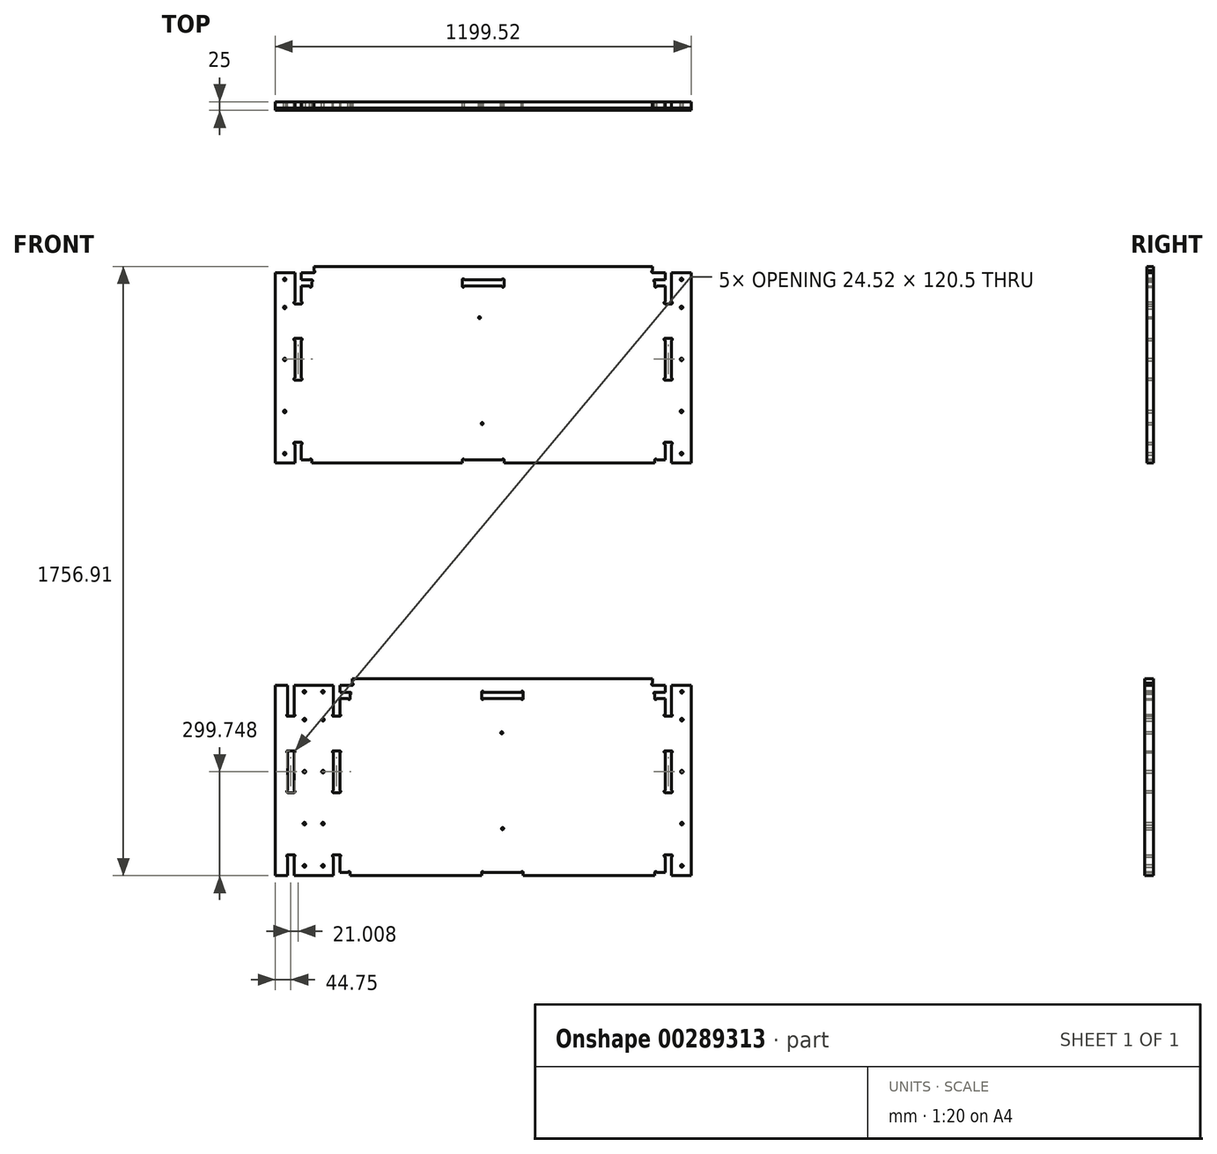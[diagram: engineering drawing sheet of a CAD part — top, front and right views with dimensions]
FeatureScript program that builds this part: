
annotation { "Feature Type Name" : "Feature", "Feature Type Description" : "" }
export const myFeature = defineFeature(function(context is Context, id is Id, definition is map)
    precondition{}
    {
        {
            var Q0;
            Q0=qCreatedBy(makeId("Front.planeOp"),FACE);
            var sketch = newSketch(context, id + "F0", { "sketchPlane" : qUnion([Q0])});
            skLineSegment(sketch, "E0", {"start": v(-600, -1200) * mm, "end": v(600, -1200) * mm});
            skLineSegment(sketch, "E1", {"start": v(600, 1200) * mm, "end": v(-600, 1200) * mm});
            skLineSegment(sketch, "E2", {"start": v(-600, -1149.94) * mm, "end": v(-564.5, -1149.94) * mm});
            skLineSegment(sketch, "E3", {"start": v(-564.5, -1149.94) * mm, "end": v(-564.5, -1066.44) * mm});
            skLineSegment(sketch, "E4", {"start": v(-564.5, -1066.44) * mm, "end": v(-564.5, -1066.21) * mm});
            skLineSegment(sketch, "E5", {"start": v(-564.5, -1066.21) * mm, "end": v(-564.73, -1066.2) * mm});
            skArc(sketch, "E6", {"start": v(-564.73, -1066.2) * mm, "mid": v(-567.52, -1063.07) * mm, "end": v(-564.5, -1060.17) * mm});
            skLineSegment(sketch, "E7", {"start": v(-564.5, -1060.17) * mm, "end": v(-546, -1060.17) * mm});
            skArc(sketch, "E8", {"start": v(-546, -1060.17) * mm, "mid": v(-543, -1063.07) * mm, "end": v(-545.77, -1066.2) * mm});
            skLineSegment(sketch, "E9", {"start": v(-545.77, -1066.2) * mm, "end": v(-546, -1066.21) * mm});
            skLineSegment(sketch, "E10", {"start": v(-546, -1066.21) * mm, "end": v(-546, -1066.44) * mm});
            skLineSegment(sketch, "E11", {"start": v(-546, -1066.44) * mm, "end": v(-546, -1149.94) * mm});
            skLineSegment(sketch, "E12", {"start": v(-546, -1149.94) * mm, "end": v(-432.5, -1149.94) * mm});
            skLineSegment(sketch, "E13", {"start": v(-432.5, -1149.94) * mm, "end": v(-432.5, -1066.44) * mm});
            skLineSegment(sketch, "E14", {"start": v(-432.5, -1066.44) * mm, "end": v(-432.5, -1066.21) * mm});
            skLineSegment(sketch, "E15", {"start": v(-432.5, -1066.21) * mm, "end": v(-432.73, -1066.2) * mm});
            skArc(sketch, "E16", {"start": v(-432.73, -1066.2) * mm, "mid": v(-435.52, -1063.07) * mm, "end": v(-432.5, -1060.17) * mm});
            skLineSegment(sketch, "E17", {"start": v(-432.5, -1060.17) * mm, "end": v(-414, -1060.17) * mm});
            skArc(sketch, "E18", {"start": v(-414, -1060.17) * mm, "mid": v(-411, -1063.07) * mm, "end": v(-413.77, -1066.2) * mm});
            skLineSegment(sketch, "E19", {"start": v(-413.77, -1066.2) * mm, "end": v(-414, -1066.21) * mm});
            skLineSegment(sketch, "E20", {"start": v(-414, -1066.21) * mm, "end": v(-414, -1066.44) * mm});
            skLineSegment(sketch, "E21", {"start": v(-414, -1066.44) * mm, "end": v(-414, -1111.17) * mm});
            skLineSegment(sketch, "E22", {"start": v(-414, -1111.17) * mm, "end": v(-390.27, -1111.17) * mm});
            skLineSegment(sketch, "E23", {"start": v(-390.27, -1111.17) * mm, "end": v(-390.04, -1111.17) * mm});
            skLineSegment(sketch, "E24", {"start": v(-390.04, -1111.17) * mm, "end": v(-390.02, -1110.94) * mm});
            skArc(sketch, "E25", {"start": v(-390.02, -1110.94) * mm, "mid": v(-386.9, -1108.16) * mm, "end": v(-384, -1111.17) * mm});
            skLineSegment(sketch, "E26", {"start": v(-384, -1111.17) * mm, "end": v(-384, -1123.4) * mm});
            skLineSegment(sketch, "E27", {"start": v(-384, -1123.4) * mm, "end": v(-384, -1123.64) * mm});
            skLineSegment(sketch, "E28", {"start": v(-384, -1123.64) * mm, "end": v(-383.77, -1123.65) * mm});
            skArc(sketch, "E29", {"start": v(-383.77, -1123.65) * mm, "mid": v(-380.98, -1126.77) * mm, "end": v(-384, -1129.67) * mm});
            skLineSegment(sketch, "E30", {"start": v(-384, -1129.67) * mm, "end": v(-414, -1129.67) * mm});
            skLineSegment(sketch, "E31", {"start": v(-414, -1129.67) * mm, "end": v(-414, -1149.94) * mm});
            skLineSegment(sketch, "E32", {"start": v(-414, -1149.94) * mm, "end": v(-378, -1149.94) * mm});
            skArc(sketch, "E33", {"start": v(-378, -1149.94) * mm, "mid": v(-375, -1152.84) * mm, "end": v(-377.77, -1155.96) * mm});
            skLineSegment(sketch, "E34", {"start": v(-377.77, -1155.96) * mm, "end": v(-378, -1155.98) * mm});
            skLineSegment(sketch, "E35", {"start": v(-378, -1155.98) * mm, "end": v(-378, -1156.2) * mm});
            skLineSegment(sketch, "E36", {"start": v(-378, -1156.2) * mm, "end": v(-378, -1167.94) * mm});
            skLineSegment(sketch, "E37", {"start": v(-378, -1167.94) * mm, "end": v(488.5, -1167.94) * mm});
            skLineSegment(sketch, "E38", {"start": v(488.5, -1167.94) * mm, "end": v(488.5, -1156.2) * mm});
            skLineSegment(sketch, "E39", {"start": v(488.5, -1156.2) * mm, "end": v(488.5, -1155.98) * mm});
            skLineSegment(sketch, "E40", {"start": v(488.5, -1155.98) * mm, "end": v(488.27, -1155.96) * mm});
            skArc(sketch, "E41", {"start": v(488.27, -1155.96) * mm, "mid": v(485.48, -1152.84) * mm, "end": v(488.5, -1149.94) * mm});
            skLineSegment(sketch, "E42", {"start": v(488.5, -1149.94) * mm, "end": v(524.5, -1149.94) * mm});
            skLineSegment(sketch, "E43", {"start": v(524.5, -1149.94) * mm, "end": v(524.5, -1129.67) * mm});
            skLineSegment(sketch, "E44", {"start": v(524.5, -1129.67) * mm, "end": v(494.5, -1129.67) * mm});
            skArc(sketch, "E45", {"start": v(494.5, -1129.67) * mm, "mid": v(491.5, -1126.77) * mm, "end": v(494.27, -1123.65) * mm});
            skLineSegment(sketch, "E46", {"start": v(494.27, -1123.65) * mm, "end": v(494.5, -1123.64) * mm});
            skLineSegment(sketch, "E47", {"start": v(494.5, -1123.64) * mm, "end": v(494.5, -1123.4) * mm});
            skLineSegment(sketch, "E48", {"start": v(494.5, -1123.4) * mm, "end": v(494.5, -1111.17) * mm});
            skArc(sketch, "E49", {"start": v(494.5, -1111.17) * mm, "mid": v(497.4, -1108.17) * mm, "end": v(500.52, -1110.94) * mm});
            skLineSegment(sketch, "E50", {"start": v(500.52, -1110.94) * mm, "end": v(500.54, -1111.17) * mm});
            skLineSegment(sketch, "E51", {"start": v(500.54, -1111.17) * mm, "end": v(500.77, -1111.17) * mm});
            skLineSegment(sketch, "E52", {"start": v(500.77, -1111.17) * mm, "end": v(524.5, -1111.17) * mm});
            skLineSegment(sketch, "E53", {"start": v(524.5, -1111.17) * mm, "end": v(524.5, -1066.44) * mm});
            skLineSegment(sketch, "E54", {"start": v(524.5, -1066.44) * mm, "end": v(524.5, -1066.21) * mm});
            skLineSegment(sketch, "E55", {"start": v(524.5, -1066.21) * mm, "end": v(524.27, -1066.2) * mm});
            skArc(sketch, "E56", {"start": v(524.27, -1066.2) * mm, "mid": v(521.48, -1063.07) * mm, "end": v(524.5, -1060.17) * mm});
            skLineSegment(sketch, "E57", {"start": v(524.5, -1060.17) * mm, "end": v(543, -1060.17) * mm});
            skArc(sketch, "E58", {"start": v(543, -1060.17) * mm, "mid": v(546, -1063.07) * mm, "end": v(543.23, -1066.2) * mm});
            skLineSegment(sketch, "E59", {"start": v(543.23, -1066.2) * mm, "end": v(543, -1066.21) * mm});
            skLineSegment(sketch, "E60", {"start": v(543, -1066.21) * mm, "end": v(543, -1066.44) * mm});
            skLineSegment(sketch, "E61", {"start": v(543, -1066.44) * mm, "end": v(543, -1149.94) * mm});
            skLineSegment(sketch, "E62", {"start": v(543, -1149.94) * mm, "end": v(599.5, -1149.94) * mm});
            skLineSegment(sketch, "E63", {"start": v(599.5, -1149.94) * mm, "end": v(599.5, -600.67) * mm});
            skLineSegment(sketch, "E64", {"start": v(599.5, -600.67) * mm, "end": v(543, -600.67) * mm});
            skLineSegment(sketch, "E65", {"start": v(543, -600.67) * mm, "end": v(543, -654.4) * mm});
            skLineSegment(sketch, "E66", {"start": v(543, -654.4) * mm, "end": v(543, -654.64) * mm});
            skLineSegment(sketch, "E67", {"start": v(543, -654.64) * mm, "end": v(543.23, -654.65) * mm});
            skArc(sketch, "E68", {"start": v(543.23, -654.65) * mm, "mid": v(546.02, -657.78) * mm, "end": v(543, -660.67) * mm});
            skLineSegment(sketch, "E69", {"start": v(543, -660.67) * mm, "end": v(524.5, -660.67) * mm});
            skArc(sketch, "E70", {"start": v(524.5, -660.67) * mm, "mid": v(521.5, -657.78) * mm, "end": v(524.27, -654.65) * mm});
            skLineSegment(sketch, "E71", {"start": v(524.27, -654.65) * mm, "end": v(524.5, -654.64) * mm});
            skLineSegment(sketch, "E72", {"start": v(524.5, -654.64) * mm, "end": v(524.5, -654.4) * mm});
            skLineSegment(sketch, "E73", {"start": v(524.5, -654.4) * mm, "end": v(524.5, -609.68) * mm});
            skLineSegment(sketch, "E74", {"start": v(524.5, -609.68) * mm, "end": v(500.77, -609.68) * mm});
            skLineSegment(sketch, "E75", {"start": v(500.77, -609.68) * mm, "end": v(500.54, -609.68) * mm});
            skLineSegment(sketch, "E76", {"start": v(500.54, -609.68) * mm, "end": v(500.52, -609.9) * mm});
            skArc(sketch, "E77", {"start": v(500.52, -609.9) * mm, "mid": v(497.4, -612.7) * mm, "end": v(494.5, -609.68) * mm});
            skLineSegment(sketch, "E78", {"start": v(494.5, -609.68) * mm, "end": v(494.5, -600.67) * mm});
            skLineSegment(sketch, "E79", {"start": v(494.5, -600.67) * mm, "end": v(115.5, -600.67) * mm});
            skLineSegment(sketch, "E80", {"start": v(115.5, -600.67) * mm, "end": v(115.5, -609.68) * mm});
            skArc(sketch, "E81", {"start": v(115.5, -609.68) * mm, "mid": v(112.6, -612.68) * mm, "end": v(109.48, -609.9) * mm});
            skLineSegment(sketch, "E82", {"start": v(109.48, -609.9) * mm, "end": v(109.46, -609.68) * mm});
            skLineSegment(sketch, "E83", {"start": v(109.46, -609.68) * mm, "end": v(109.23, -609.68) * mm});
            skLineSegment(sketch, "E84", {"start": v(109.23, -609.68) * mm, "end": v(1.27, -609.68) * mm});
            skLineSegment(sketch, "E85", {"start": v(1.27, -609.68) * mm, "end": v(1.04, -609.68) * mm});
            skLineSegment(sketch, "E86", {"start": v(1.04, -609.68) * mm, "end": v(1.02, -609.9) * mm});
            skArc(sketch, "E87", {"start": v(1.02, -609.9) * mm, "mid": v(-2.1, -612.7) * mm, "end": v(-5, -609.68) * mm});
            skLineSegment(sketch, "E88", {"start": v(-5, -609.68) * mm, "end": v(-5, -600.67) * mm});
            skLineSegment(sketch, "E89", {"start": v(-5, -600.67) * mm, "end": v(-384, -600.67) * mm});
            skLineSegment(sketch, "E90", {"start": v(-384, -600.67) * mm, "end": v(-384, -609.68) * mm});
            skArc(sketch, "E91", {"start": v(-384, -609.68) * mm, "mid": v(-386.9, -612.68) * mm, "end": v(-390.02, -609.9) * mm});
            skLineSegment(sketch, "E92", {"start": v(-390.02, -609.9) * mm, "end": v(-390.04, -609.68) * mm});
            skLineSegment(sketch, "E93", {"start": v(-390.04, -609.68) * mm, "end": v(-390.27, -609.68) * mm});
            skLineSegment(sketch, "E94", {"start": v(-390.27, -609.68) * mm, "end": v(-414, -609.68) * mm});
            skLineSegment(sketch, "E95", {"start": v(-414, -609.68) * mm, "end": v(-414, -654.4) * mm});
            skLineSegment(sketch, "E96", {"start": v(-414, -654.4) * mm, "end": v(-414, -654.63) * mm});
            skLineSegment(sketch, "E97", {"start": v(-414, -654.63) * mm, "end": v(-413.77, -654.65) * mm});
            skArc(sketch, "E98", {"start": v(-413.77, -654.65) * mm, "mid": v(-410.98, -657.77) * mm, "end": v(-414, -660.67) * mm});
            skLineSegment(sketch, "E99", {"start": v(-414, -660.67) * mm, "end": v(-432.5, -660.67) * mm});
            skArc(sketch, "E100", {"start": v(-432.5, -660.67) * mm, "mid": v(-435.5, -657.77) * mm, "end": v(-432.73, -654.65) * mm});
            skLineSegment(sketch, "E101", {"start": v(-432.73, -654.65) * mm, "end": v(-432.5, -654.63) * mm});
            skLineSegment(sketch, "E102", {"start": v(-432.5, -654.63) * mm, "end": v(-432.5, -654.4) * mm});
            skLineSegment(sketch, "E103", {"start": v(-432.5, -654.4) * mm, "end": v(-432.5, -600.67) * mm});
            skLineSegment(sketch, "E104", {"start": v(-432.5, -600.67) * mm, "end": v(-546, -600.67) * mm});
            skLineSegment(sketch, "E105", {"start": v(-546, -600.67) * mm, "end": v(-546, -654.4) * mm});
            skLineSegment(sketch, "E106", {"start": v(-546, -654.4) * mm, "end": v(-546, -654.63) * mm});
            skLineSegment(sketch, "E107", {"start": v(-546, -654.63) * mm, "end": v(-545.77, -654.65) * mm});
            skArc(sketch, "E108", {"start": v(-545.77, -654.65) * mm, "mid": v(-542.98, -657.77) * mm, "end": v(-546, -660.67) * mm});
            skLineSegment(sketch, "E109", {"start": v(-546, -660.67) * mm, "end": v(-564.5, -660.67) * mm});
            skArc(sketch, "E110", {"start": v(-564.5, -660.67) * mm, "mid": v(-567.5, -657.77) * mm, "end": v(-564.73, -654.65) * mm});
            skLineSegment(sketch, "E111", {"start": v(-564.73, -654.65) * mm, "end": v(-564.5, -654.63) * mm});
            skLineSegment(sketch, "E112", {"start": v(-564.5, -654.63) * mm, "end": v(-564.5, -654.4) * mm});
            skLineSegment(sketch, "E113", {"start": v(-564.5, -654.4) * mm, "end": v(-564.5, -600.67) * mm});
            skLineSegment(sketch, "E114", {"start": v(-564.5, -600.67) * mm, "end": v(-600, -600.67) * mm});
            skLineSegment(sketch, "E115", {"start": v(-600, -31.4) * mm, "end": v(-564.5, -31.4) * mm});
            skLineSegment(sketch, "E116", {"start": v(-564.5, -31.4) * mm, "end": v(-564.5, -114.9) * mm});
            skLineSegment(sketch, "E117", {"start": v(-564.5, -114.9) * mm, "end": v(-564.5, -115.13) * mm});
            skLineSegment(sketch, "E118", {"start": v(-564.5, -115.13) * mm, "end": v(-564.73, -115.15) * mm});
            skArc(sketch, "E119", {"start": v(-564.73, -115.15) * mm, "mid": v(-567.52, -118.27) * mm, "end": v(-564.5, -121.17) * mm});
            skLineSegment(sketch, "E120", {"start": v(-564.5, -121.17) * mm, "end": v(-546, -121.17) * mm});
            skArc(sketch, "E121", {"start": v(-546, -121.17) * mm, "mid": v(-543, -118.27) * mm, "end": v(-545.77, -115.15) * mm});
            skLineSegment(sketch, "E122", {"start": v(-545.77, -115.15) * mm, "end": v(-546, -115.13) * mm});
            skLineSegment(sketch, "E123", {"start": v(-546, -115.13) * mm, "end": v(-546, -114.9) * mm});
            skLineSegment(sketch, "E124", {"start": v(-546, -114.9) * mm, "end": v(-546, -31.4) * mm});
            skLineSegment(sketch, "E125", {"start": v(-546, -31.4) * mm, "end": v(-432.5, -31.4) * mm});
            skLineSegment(sketch, "E126", {"start": v(-432.5, -31.4) * mm, "end": v(-432.5, -114.9) * mm});
            skLineSegment(sketch, "E127", {"start": v(-432.5, -114.9) * mm, "end": v(-432.5, -115.14) * mm});
            skLineSegment(sketch, "E128", {"start": v(-432.5, -115.14) * mm, "end": v(-432.73, -115.15) * mm});
            skArc(sketch, "E129", {"start": v(-432.73, -115.15) * mm, "mid": v(-435.52, -118.27) * mm, "end": v(-432.5, -121.17) * mm});
            skLineSegment(sketch, "E130", {"start": v(-432.5, -121.17) * mm, "end": v(-414, -121.17) * mm});
            skArc(sketch, "E131", {"start": v(-414, -121.17) * mm, "mid": v(-411, -118.27) * mm, "end": v(-413.77, -115.15) * mm});
            skLineSegment(sketch, "E132", {"start": v(-413.77, -115.15) * mm, "end": v(-414, -115.13) * mm});
            skLineSegment(sketch, "E133", {"start": v(-414, -115.13) * mm, "end": v(-414, -114.9) * mm});
            skLineSegment(sketch, "E134", {"start": v(-414, -114.9) * mm, "end": v(-414, -70.17) * mm});
            skLineSegment(sketch, "E135", {"start": v(-414, -70.17) * mm, "end": v(-390.27, -70.17) * mm});
            skLineSegment(sketch, "E136", {"start": v(-390.27, -70.17) * mm, "end": v(-390.04, -70.17) * mm});
            skLineSegment(sketch, "E137", {"start": v(-390.04, -70.17) * mm, "end": v(-390.02, -70.4) * mm});
            skArc(sketch, "E138", {"start": v(-390.02, -70.4) * mm, "mid": v(-386.9, -73.19) * mm, "end": v(-384, -70.17) * mm});
            skLineSegment(sketch, "E139", {"start": v(-384, -70.17) * mm, "end": v(-384, -57.94) * mm});
            skLineSegment(sketch, "E140", {"start": v(-384, -57.94) * mm, "end": v(-384, -57.71) * mm});
            skLineSegment(sketch, "E141", {"start": v(-384, -57.71) * mm, "end": v(-383.77, -57.7) * mm});
            skArc(sketch, "E142", {"start": v(-383.77, -57.7) * mm, "mid": v(-380.98, -54.57) * mm, "end": v(-384, -51.67) * mm});
            skLineSegment(sketch, "E143", {"start": v(-384, -51.67) * mm, "end": v(-414, -51.67) * mm});
            skLineSegment(sketch, "E144", {"start": v(-414, -51.67) * mm, "end": v(-414, -31.4) * mm});
            skLineSegment(sketch, "E145", {"start": v(-414, -31.4) * mm, "end": v(-378, -31.4) * mm});
            skArc(sketch, "E146", {"start": v(-378, -31.4) * mm, "mid": v(-375, -28.5) * mm, "end": v(-377.77, -25.39) * mm});
            skLineSegment(sketch, "E147", {"start": v(-377.77, -25.39) * mm, "end": v(-378, -25.37) * mm});
            skLineSegment(sketch, "E148", {"start": v(-378, -25.37) * mm, "end": v(-378, -25.14) * mm});
            skLineSegment(sketch, "E149", {"start": v(-378, -25.14) * mm, "end": v(-378, -13.4) * mm});
            skLineSegment(sketch, "E150", {"start": v(-378, -13.4) * mm, "end": v(488.5, -13.4) * mm});
            skLineSegment(sketch, "E151", {"start": v(488.5, -13.4) * mm, "end": v(488.5, -25.14) * mm});
            skLineSegment(sketch, "E152", {"start": v(488.5, -25.14) * mm, "end": v(488.5, -25.37) * mm});
            skLineSegment(sketch, "E153", {"start": v(488.5, -25.37) * mm, "end": v(488.27, -25.39) * mm});
            skArc(sketch, "E154", {"start": v(488.27, -25.39) * mm, "mid": v(485.48, -28.5) * mm, "end": v(488.5, -31.4) * mm});
            skLineSegment(sketch, "E155", {"start": v(488.5, -31.4) * mm, "end": v(524.5, -31.4) * mm});
            skLineSegment(sketch, "E156", {"start": v(524.5, -31.4) * mm, "end": v(524.5, -51.67) * mm});
            skLineSegment(sketch, "E157", {"start": v(524.5, -51.67) * mm, "end": v(494.5, -51.67) * mm});
            skArc(sketch, "E158", {"start": v(494.5, -51.67) * mm, "mid": v(491.5, -54.57) * mm, "end": v(494.27, -57.7) * mm});
            skLineSegment(sketch, "E159", {"start": v(494.27, -57.7) * mm, "end": v(494.5, -57.71) * mm});
            skLineSegment(sketch, "E160", {"start": v(494.5, -57.71) * mm, "end": v(494.5, -57.94) * mm});
            skLineSegment(sketch, "E161", {"start": v(494.5, -57.94) * mm, "end": v(494.5, -70.17) * mm});
            skArc(sketch, "E162", {"start": v(494.5, -70.17) * mm, "mid": v(497.4, -73.18) * mm, "end": v(500.52, -70.4) * mm});
            skLineSegment(sketch, "E163", {"start": v(500.52, -70.4) * mm, "end": v(500.54, -70.17) * mm});
            skLineSegment(sketch, "E164", {"start": v(500.54, -70.17) * mm, "end": v(500.77, -70.17) * mm});
            skLineSegment(sketch, "E165", {"start": v(500.77, -70.17) * mm, "end": v(524.5, -70.17) * mm});
            skLineSegment(sketch, "E166", {"start": v(524.5, -70.17) * mm, "end": v(524.5, -114.9) * mm});
            skLineSegment(sketch, "E167", {"start": v(524.5, -114.9) * mm, "end": v(524.5, -115.13) * mm});
            skLineSegment(sketch, "E168", {"start": v(524.5, -115.13) * mm, "end": v(524.27, -115.15) * mm});
            skArc(sketch, "E169", {"start": v(524.27, -115.15) * mm, "mid": v(521.48, -118.27) * mm, "end": v(524.5, -121.17) * mm});
            skLineSegment(sketch, "E170", {"start": v(524.5, -121.17) * mm, "end": v(543, -121.17) * mm});
            skArc(sketch, "E171", {"start": v(543, -121.17) * mm, "mid": v(546, -118.27) * mm, "end": v(543.23, -115.15) * mm});
            skLineSegment(sketch, "E172", {"start": v(543.23, -115.15) * mm, "end": v(543, -115.13) * mm});
            skLineSegment(sketch, "E173", {"start": v(543, -115.13) * mm, "end": v(543, -114.9) * mm});
            skLineSegment(sketch, "E174", {"start": v(543, -114.9) * mm, "end": v(543, -31.4) * mm});
            skLineSegment(sketch, "E175", {"start": v(543, -31.4) * mm, "end": v(599.5, -31.4) * mm});
            skLineSegment(sketch, "E176", {"start": v(599.5, -31.4) * mm, "end": v(599.5, -580.67) * mm});
            skLineSegment(sketch, "E177", {"start": v(599.5, -580.67) * mm, "end": v(543, -580.67) * mm});
            skLineSegment(sketch, "E178", {"start": v(543, -580.67) * mm, "end": v(543, -526.94) * mm});
            skLineSegment(sketch, "E179", {"start": v(543, -526.94) * mm, "end": v(543, -526.7) * mm});
            skLineSegment(sketch, "E180", {"start": v(543, -526.7) * mm, "end": v(543.23, -526.7) * mm});
            skArc(sketch, "E181", {"start": v(543.23, -526.7) * mm, "mid": v(546.02, -523.57) * mm, "end": v(543, -520.67) * mm});
            skLineSegment(sketch, "E182", {"start": v(543, -520.67) * mm, "end": v(524.5, -520.67) * mm});
            skArc(sketch, "E183", {"start": v(524.5, -520.67) * mm, "mid": v(521.5, -523.57) * mm, "end": v(524.27, -526.7) * mm});
            skLineSegment(sketch, "E184", {"start": v(524.27, -526.7) * mm, "end": v(524.5, -526.71) * mm});
            skLineSegment(sketch, "E185", {"start": v(524.5, -526.71) * mm, "end": v(524.5, -526.94) * mm});
            skLineSegment(sketch, "E186", {"start": v(524.5, -526.94) * mm, "end": v(524.5, -571.67) * mm});
            skLineSegment(sketch, "E187", {"start": v(524.5, -571.67) * mm, "end": v(500.77, -571.67) * mm});
            skLineSegment(sketch, "E188", {"start": v(500.77, -571.67) * mm, "end": v(500.54, -571.67) * mm});
            skLineSegment(sketch, "E189", {"start": v(500.54, -571.67) * mm, "end": v(500.52, -571.44) * mm});
            skArc(sketch, "E190", {"start": v(500.52, -571.44) * mm, "mid": v(497.4, -568.65) * mm, "end": v(494.5, -571.67) * mm});
            skLineSegment(sketch, "E191", {"start": v(494.5, -571.67) * mm, "end": v(494.5, -580.67) * mm});
            skLineSegment(sketch, "E192", {"start": v(494.5, -580.67) * mm, "end": v(115.5, -580.67) * mm});
            skLineSegment(sketch, "E193", {"start": v(115.5, -580.67) * mm, "end": v(115.5, -571.67) * mm});
            skArc(sketch, "E194", {"start": v(115.5, -571.67) * mm, "mid": v(112.6, -568.66) * mm, "end": v(109.48, -571.44) * mm});
            skLineSegment(sketch, "E195", {"start": v(109.48, -571.44) * mm, "end": v(109.46, -571.67) * mm});
            skLineSegment(sketch, "E196", {"start": v(109.46, -571.67) * mm, "end": v(109.23, -571.67) * mm});
            skLineSegment(sketch, "E197", {"start": v(109.23, -571.67) * mm, "end": v(1.27, -571.67) * mm});
            skLineSegment(sketch, "E198", {"start": v(1.27, -571.67) * mm, "end": v(1.04, -571.67) * mm});
            skLineSegment(sketch, "E199", {"start": v(1.04, -571.67) * mm, "end": v(1.02, -571.44) * mm});
            skArc(sketch, "E200", {"start": v(1.02, -571.44) * mm, "mid": v(-2.1, -568.65) * mm, "end": v(-5, -571.67) * mm});
            skLineSegment(sketch, "E201", {"start": v(-5, -571.67) * mm, "end": v(-5, -580.67) * mm});
            skLineSegment(sketch, "E202", {"start": v(-5, -580.67) * mm, "end": v(-384, -580.67) * mm});
            skLineSegment(sketch, "E203", {"start": v(-384, -580.67) * mm, "end": v(-384, -571.67) * mm});
            skArc(sketch, "E204", {"start": v(-384, -571.67) * mm, "mid": v(-386.9, -568.66) * mm, "end": v(-390.02, -571.44) * mm});
            skLineSegment(sketch, "E205", {"start": v(-390.02, -571.44) * mm, "end": v(-390.04, -571.67) * mm});
            skLineSegment(sketch, "E206", {"start": v(-390.04, -571.67) * mm, "end": v(-390.27, -571.67) * mm});
            skLineSegment(sketch, "E207", {"start": v(-390.27, -571.67) * mm, "end": v(-414, -571.67) * mm});
            skLineSegment(sketch, "E208", {"start": v(-414, -571.67) * mm, "end": v(-414, -526.95) * mm});
            skLineSegment(sketch, "E209", {"start": v(-414, -526.95) * mm, "end": v(-414, -526.71) * mm});
            skLineSegment(sketch, "E210", {"start": v(-414, -526.71) * mm, "end": v(-413.77, -526.7) * mm});
            skArc(sketch, "E211", {"start": v(-413.77, -526.7) * mm, "mid": v(-410.98, -523.57) * mm, "end": v(-414, -520.68) * mm});
            skLineSegment(sketch, "E212", {"start": v(-414, -520.68) * mm, "end": v(-432.5, -520.68) * mm});
            skArc(sketch, "E213", {"start": v(-432.5, -520.68) * mm, "mid": v(-435.5, -523.57) * mm, "end": v(-432.73, -526.7) * mm});
            skLineSegment(sketch, "E214", {"start": v(-432.73, -526.7) * mm, "end": v(-432.5, -526.71) * mm});
            skLineSegment(sketch, "E215", {"start": v(-432.5, -526.71) * mm, "end": v(-432.5, -526.95) * mm});
            skLineSegment(sketch, "E216", {"start": v(-432.5, -526.95) * mm, "end": v(-432.5, -580.67) * mm});
            skLineSegment(sketch, "E217", {"start": v(-432.5, -580.67) * mm, "end": v(-546, -580.67) * mm});
            skLineSegment(sketch, "E218", {"start": v(-546, -580.67) * mm, "end": v(-546, -526.95) * mm});
            skLineSegment(sketch, "E219", {"start": v(-546, -526.95) * mm, "end": v(-546, -526.71) * mm});
            skLineSegment(sketch, "E220", {"start": v(-546, -526.71) * mm, "end": v(-545.77, -526.7) * mm});
            skArc(sketch, "E221", {"start": v(-545.77, -526.7) * mm, "mid": v(-542.98, -523.57) * mm, "end": v(-546, -520.68) * mm});
            skLineSegment(sketch, "E222", {"start": v(-546, -520.68) * mm, "end": v(-564.5, -520.68) * mm});
            skArc(sketch, "E223", {"start": v(-564.5, -520.68) * mm, "mid": v(-567.5, -523.57) * mm, "end": v(-564.73, -526.7) * mm});
            skLineSegment(sketch, "E224", {"start": v(-564.73, -526.7) * mm, "end": v(-564.5, -526.71) * mm});
            skLineSegment(sketch, "E225", {"start": v(-564.5, -526.71) * mm, "end": v(-564.5, -526.95) * mm});
            skLineSegment(sketch, "E226", {"start": v(-564.5, -526.95) * mm, "end": v(-564.5, -580.67) * mm});
            skLineSegment(sketch, "E227", {"start": v(-564.5, -580.67) * mm, "end": v(-600, -580.67) * mm});
            skLineSegment(sketch, "E228", {"start": v(-600, 608.96) * mm, "end": v(-543.5, 608.96) * mm});
            skLineSegment(sketch, "E229", {"start": v(-543.5, 608.96) * mm, "end": v(-543.5, 662.69) * mm});
            skLineSegment(sketch, "E230", {"start": v(-543.5, 662.69) * mm, "end": v(-543.5, 662.92) * mm});
            skLineSegment(sketch, "E231", {"start": v(-543.5, 662.92) * mm, "end": v(-543.73, 662.94) * mm});
            skArc(sketch, "E232", {"start": v(-543.73, 662.94) * mm, "mid": v(-546.52, 666.06) * mm, "end": v(-543.5, 668.96) * mm});
            skLineSegment(sketch, "E233", {"start": v(-543.5, 668.96) * mm, "end": v(-525, 668.96) * mm});
            skArc(sketch, "E234", {"start": v(-525, 668.96) * mm, "mid": v(-522, 666.06) * mm, "end": v(-524.77, 662.94) * mm});
            skLineSegment(sketch, "E235", {"start": v(-524.77, 662.94) * mm, "end": v(-525, 662.92) * mm});
            skLineSegment(sketch, "E236", {"start": v(-525, 662.92) * mm, "end": v(-525, 662.69) * mm});
            skLineSegment(sketch, "E237", {"start": v(-525, 662.69) * mm, "end": v(-525, 617.97) * mm});
            skLineSegment(sketch, "E238", {"start": v(-525, 617.97) * mm, "end": v(-501.27, 617.97) * mm});
            skLineSegment(sketch, "E239", {"start": v(-501.27, 617.97) * mm, "end": v(-501.04, 617.97) * mm});
            skLineSegment(sketch, "E240", {"start": v(-501.04, 617.97) * mm, "end": v(-501.02, 618.2) * mm});
            skArc(sketch, "E241", {"start": v(-501.02, 618.2) * mm, "mid": v(-497.9, 620.99) * mm, "end": v(-495, 617.97) * mm});
            skLineSegment(sketch, "E242", {"start": v(-495, 617.97) * mm, "end": v(-495, 608.96) * mm});
            skLineSegment(sketch, "E243", {"start": v(-495, 608.96) * mm, "end": v(-60.5, 608.95) * mm});
            skLineSegment(sketch, "E244", {"start": v(-60.5, 608.95) * mm, "end": v(-60.5, 617.96) * mm});
            skArc(sketch, "E245", {"start": v(-60.5, 617.96) * mm, "mid": v(-57.6, 620.96) * mm, "end": v(-54.48, 618.19) * mm});
            skLineSegment(sketch, "E246", {"start": v(-54.48, 618.19) * mm, "end": v(-54.46, 617.96) * mm});
            skLineSegment(sketch, "E247", {"start": v(-54.46, 617.96) * mm, "end": v(-54.23, 617.96) * mm});
            skLineSegment(sketch, "E248", {"start": v(-54.23, 617.96) * mm, "end": v(53.73, 617.96) * mm});
            skLineSegment(sketch, "E249", {"start": v(53.73, 617.96) * mm, "end": v(53.96, 617.96) * mm});
            skLineSegment(sketch, "E250", {"start": v(53.96, 617.96) * mm, "end": v(53.98, 618.19) * mm});
            skArc(sketch, "E251", {"start": v(53.98, 618.19) * mm, "mid": v(57.1, 620.97) * mm, "end": v(60, 617.96) * mm});
            skLineSegment(sketch, "E252", {"start": v(60, 617.96) * mm, "end": v(60, 608.95) * mm});
            skLineSegment(sketch, "E253", {"start": v(60, 608.95) * mm, "end": v(494.5, 608.97) * mm});
            skLineSegment(sketch, "E254", {"start": v(494.5, 608.97) * mm, "end": v(494.5, 617.95) * mm});
            skArc(sketch, "E255", {"start": v(494.5, 617.95) * mm, "mid": v(497.4, 620.95) * mm, "end": v(500.52, 618.18) * mm});
            skLineSegment(sketch, "E256", {"start": v(500.52, 618.18) * mm, "end": v(500.54, 617.95) * mm});
            skLineSegment(sketch, "E257", {"start": v(500.54, 617.95) * mm, "end": v(500.77, 617.95) * mm});
            skLineSegment(sketch, "E258", {"start": v(500.77, 617.95) * mm, "end": v(524.5, 617.95) * mm});
            skLineSegment(sketch, "E259", {"start": v(524.5, 617.95) * mm, "end": v(524.5, 662.67) * mm});
            skLineSegment(sketch, "E260", {"start": v(524.5, 662.67) * mm, "end": v(524.5, 662.9) * mm});
            skLineSegment(sketch, "E261", {"start": v(524.5, 662.9) * mm, "end": v(524.27, 662.92) * mm});
            skArc(sketch, "E262", {"start": v(524.27, 662.92) * mm, "mid": v(521.48, 666.04) * mm, "end": v(524.5, 668.94) * mm});
            skLineSegment(sketch, "E263", {"start": v(524.5, 668.94) * mm, "end": v(543, 668.94) * mm});
            skArc(sketch, "E264", {"start": v(543, 668.94) * mm, "mid": v(546, 666.04) * mm, "end": v(543.23, 662.92) * mm});
            skLineSegment(sketch, "E265", {"start": v(543.23, 662.92) * mm, "end": v(543, 662.9) * mm});
            skLineSegment(sketch, "E266", {"start": v(543, 662.9) * mm, "end": v(543, 662.67) * mm});
            skLineSegment(sketch, "E267", {"start": v(543, 662.67) * mm, "end": v(543, 608.95) * mm});
            skLineSegment(sketch, "E268", {"start": v(543, 608.95) * mm, "end": v(599.5, 608.95) * mm});
            skLineSegment(sketch, "E269", {"start": v(599.5, 608.95) * mm, "end": v(599.52, 1158.21) * mm});
            skLineSegment(sketch, "E270", {"start": v(599.52, 1158.21) * mm, "end": v(543.02, 1158.21) * mm});
            skLineSegment(sketch, "E271", {"start": v(543.02, 1158.21) * mm, "end": v(543.01, 1074.72) * mm});
            skLineSegment(sketch, "E272", {"start": v(543.01, 1074.72) * mm, "end": v(543.01, 1074.49) * mm});
            skLineSegment(sketch, "E273", {"start": v(543.01, 1074.49) * mm, "end": v(543.24, 1074.47) * mm});
            skArc(sketch, "E274", {"start": v(543.24, 1074.47) * mm, "mid": v(546.03, 1071.35) * mm, "end": v(543.01, 1068.45) * mm});
            skLineSegment(sketch, "E275", {"start": v(543.01, 1068.45) * mm, "end": v(524.51, 1068.45) * mm});
            skArc(sketch, "E276", {"start": v(524.51, 1068.45) * mm, "mid": v(521.5, 1071.35) * mm, "end": v(524.28, 1074.47) * mm});
            skLineSegment(sketch, "E277", {"start": v(524.28, 1074.47) * mm, "end": v(524.51, 1074.49) * mm});
            skLineSegment(sketch, "E278", {"start": v(524.51, 1074.49) * mm, "end": v(524.51, 1074.72) * mm});
            skLineSegment(sketch, "E279", {"start": v(524.51, 1074.72) * mm, "end": v(524.52, 1119.45) * mm});
            skLineSegment(sketch, "E280", {"start": v(524.52, 1119.45) * mm, "end": v(500.79, 1119.45) * mm});
            skLineSegment(sketch, "E281", {"start": v(500.79, 1119.45) * mm, "end": v(500.55, 1119.45) * mm});
            skLineSegment(sketch, "E282", {"start": v(500.55, 1119.45) * mm, "end": v(500.54, 1119.22) * mm});
            skArc(sketch, "E283", {"start": v(500.54, 1119.22) * mm, "mid": v(497.42, 1116.43) * mm, "end": v(494.52, 1119.45) * mm});
            skLineSegment(sketch, "E284", {"start": v(494.52, 1119.45) * mm, "end": v(494.52, 1131.68) * mm});
            skLineSegment(sketch, "E285", {"start": v(494.52, 1131.68) * mm, "end": v(494.52, 1131.91) * mm});
            skLineSegment(sketch, "E286", {"start": v(494.52, 1131.91) * mm, "end": v(494.29, 1131.93) * mm});
            skArc(sketch, "E287", {"start": v(494.29, 1131.93) * mm, "mid": v(491.5, 1135.05) * mm, "end": v(494.52, 1137.95) * mm});
            skLineSegment(sketch, "E288", {"start": v(494.52, 1137.95) * mm, "end": v(524.52, 1137.95) * mm});
            skLineSegment(sketch, "E289", {"start": v(524.52, 1137.95) * mm, "end": v(524.52, 1158.21) * mm});
            skLineSegment(sketch, "E290", {"start": v(524.52, 1158.21) * mm, "end": v(488.52, 1158.22) * mm});
            skArc(sketch, "E291", {"start": v(488.52, 1158.22) * mm, "mid": v(485.5, 1161.12) * mm, "end": v(488.28, 1164.24) * mm});
            skLineSegment(sketch, "E292", {"start": v(488.28, 1164.24) * mm, "end": v(488.52, 1164.25) * mm});
            skLineSegment(sketch, "E293", {"start": v(488.52, 1164.25) * mm, "end": v(488.52, 1164.49) * mm});
            skLineSegment(sketch, "E294", {"start": v(488.52, 1164.49) * mm, "end": v(488.52, 1176.22) * mm});
            skLineSegment(sketch, "E295", {"start": v(488.52, 1176.22) * mm, "end": v(-488.98, 1176.24) * mm});
            skLineSegment(sketch, "E296", {"start": v(-488.98, 1176.24) * mm, "end": v(-488.98, 1164.5) * mm});
            skLineSegment(sketch, "E297", {"start": v(-488.98, 1164.5) * mm, "end": v(-488.98, 1164.28) * mm});
            skLineSegment(sketch, "E298", {"start": v(-488.98, 1164.28) * mm, "end": v(-488.75, 1164.26) * mm});
            skArc(sketch, "E299", {"start": v(-488.75, 1164.26) * mm, "mid": v(-485.97, 1161.14) * mm, "end": v(-488.98, 1158.24) * mm});
            skLineSegment(sketch, "E300", {"start": v(-488.98, 1158.24) * mm, "end": v(-524.98, 1158.24) * mm});
            skLineSegment(sketch, "E301", {"start": v(-524.98, 1158.24) * mm, "end": v(-524.99, 1137.97) * mm});
            skLineSegment(sketch, "E302", {"start": v(-524.99, 1137.97) * mm, "end": v(-494.99, 1137.97) * mm});
            skArc(sketch, "E303", {"start": v(-494.99, 1137.97) * mm, "mid": v(-491.98, 1135.07) * mm, "end": v(-494.75, 1131.95) * mm});
            skLineSegment(sketch, "E304", {"start": v(-494.75, 1131.95) * mm, "end": v(-494.99, 1131.93) * mm});
            skLineSegment(sketch, "E305", {"start": v(-494.99, 1131.93) * mm, "end": v(-494.99, 1131.7) * mm});
            skLineSegment(sketch, "E306", {"start": v(-494.99, 1131.7) * mm, "end": v(-494.99, 1119.47) * mm});
            skArc(sketch, "E307", {"start": v(-494.99, 1119.47) * mm, "mid": v(-497.89, 1116.46) * mm, "end": v(-501, 1119.24) * mm});
            skLineSegment(sketch, "E308", {"start": v(-501, 1119.24) * mm, "end": v(-501.02, 1119.47) * mm});
            skLineSegment(sketch, "E309", {"start": v(-501.02, 1119.47) * mm, "end": v(-501.26, 1119.47) * mm});
            skLineSegment(sketch, "E310", {"start": v(-501.26, 1119.47) * mm, "end": v(-524.99, 1119.47) * mm});
            skLineSegment(sketch, "E311", {"start": v(-524.99, 1119.47) * mm, "end": v(-524.99, 1074.74) * mm});
            skLineSegment(sketch, "E312", {"start": v(-524.99, 1074.74) * mm, "end": v(-524.99, 1074.51) * mm});
            skLineSegment(sketch, "E313", {"start": v(-524.99, 1074.51) * mm, "end": v(-524.76, 1074.5) * mm});
            skArc(sketch, "E314", {"start": v(-524.76, 1074.5) * mm, "mid": v(-521.97, 1071.37) * mm, "end": v(-524.99, 1068.47) * mm});
            skLineSegment(sketch, "E315", {"start": v(-524.99, 1068.47) * mm, "end": v(-543.49, 1068.47) * mm});
            skArc(sketch, "E316", {"start": v(-543.49, 1068.47) * mm, "mid": v(-546.5, 1071.37) * mm, "end": v(-543.72, 1074.5) * mm});
            skLineSegment(sketch, "E317", {"start": v(-543.72, 1074.5) * mm, "end": v(-543.49, 1074.51) * mm});
            skLineSegment(sketch, "E318", {"start": v(-543.49, 1074.51) * mm, "end": v(-543.49, 1074.74) * mm});
            skLineSegment(sketch, "E319", {"start": v(-543.49, 1074.74) * mm, "end": v(-543.48, 1158.24) * mm});
            skLineSegment(sketch, "E320", {"start": v(-543.48, 1158.24) * mm, "end": v(-599.99, 1158.24) * mm});
            skLineSegment(sketch, "E321", {"start": v(-600, 16.68) * mm, "end": v(-543.5, 16.68) * mm});
            skLineSegment(sketch, "E322", {"start": v(-543.5, 16.68) * mm, "end": v(-543.5, 70.4) * mm});
            skLineSegment(sketch, "E323", {"start": v(-543.5, 70.4) * mm, "end": v(-543.5, 70.64) * mm});
            skLineSegment(sketch, "E324", {"start": v(-543.5, 70.64) * mm, "end": v(-543.73, 70.66) * mm});
            skArc(sketch, "E325", {"start": v(-543.73, 70.66) * mm, "mid": v(-546.52, 73.78) * mm, "end": v(-543.5, 76.68) * mm});
            skLineSegment(sketch, "E326", {"start": v(-543.5, 76.68) * mm, "end": v(-525, 76.68) * mm});
            skArc(sketch, "E327", {"start": v(-525, 76.68) * mm, "mid": v(-522, 73.78) * mm, "end": v(-524.77, 70.65) * mm});
            skLineSegment(sketch, "E328", {"start": v(-524.77, 70.65) * mm, "end": v(-525, 70.64) * mm});
            skLineSegment(sketch, "E329", {"start": v(-525, 70.64) * mm, "end": v(-525, 70.4) * mm});
            skLineSegment(sketch, "E330", {"start": v(-525, 70.4) * mm, "end": v(-525, 25.69) * mm});
            skLineSegment(sketch, "E331", {"start": v(-525, 25.69) * mm, "end": v(-501.27, 25.69) * mm});
            skLineSegment(sketch, "E332", {"start": v(-501.27, 25.69) * mm, "end": v(-501.04, 25.69) * mm});
            skLineSegment(sketch, "E333", {"start": v(-501.04, 25.69) * mm, "end": v(-501.02, 25.92) * mm});
            skArc(sketch, "E334", {"start": v(-501.02, 25.92) * mm, "mid": v(-497.9, 28.7) * mm, "end": v(-495, 25.69) * mm});
            skLineSegment(sketch, "E335", {"start": v(-495, 25.69) * mm, "end": v(-495, 16.68) * mm});
            skLineSegment(sketch, "E336", {"start": v(-495, 16.68) * mm, "end": v(-60.5, 16.67) * mm});
            skLineSegment(sketch, "E337", {"start": v(-60.5, 16.67) * mm, "end": v(-60.5, 25.68) * mm});
            skArc(sketch, "E338", {"start": v(-60.5, 25.68) * mm, "mid": v(-57.6, 28.68) * mm, "end": v(-54.48, 25.9) * mm});
            skLineSegment(sketch, "E339", {"start": v(-54.48, 25.9) * mm, "end": v(-54.46, 25.68) * mm});
            skLineSegment(sketch, "E340", {"start": v(-54.46, 25.68) * mm, "end": v(-54.23, 25.68) * mm});
            skLineSegment(sketch, "E341", {"start": v(-54.23, 25.68) * mm, "end": v(53.73, 25.67) * mm});
            skLineSegment(sketch, "E342", {"start": v(53.73, 25.67) * mm, "end": v(53.96, 25.67) * mm});
            skLineSegment(sketch, "E343", {"start": v(53.96, 25.67) * mm, "end": v(53.98, 25.9) * mm});
            skArc(sketch, "E344", {"start": v(53.98, 25.9) * mm, "mid": v(57.1, 28.7) * mm, "end": v(60, 25.67) * mm});
            skLineSegment(sketch, "E345", {"start": v(60, 25.67) * mm, "end": v(60, 16.67) * mm});
            skLineSegment(sketch, "E346", {"start": v(60, 16.67) * mm, "end": v(494.5, 16.7) * mm});
            skLineSegment(sketch, "E347", {"start": v(494.5, 16.7) * mm, "end": v(494.5, 25.67) * mm});
            skArc(sketch, "E348", {"start": v(494.5, 25.67) * mm, "mid": v(497.4, 28.67) * mm, "end": v(500.52, 25.9) * mm});
            skLineSegment(sketch, "E349", {"start": v(500.52, 25.9) * mm, "end": v(500.54, 25.67) * mm});
            skLineSegment(sketch, "E350", {"start": v(500.54, 25.67) * mm, "end": v(500.77, 25.67) * mm});
            skLineSegment(sketch, "E351", {"start": v(500.77, 25.67) * mm, "end": v(524.5, 25.67) * mm});
            skLineSegment(sketch, "E352", {"start": v(524.5, 25.67) * mm, "end": v(524.5, 70.4) * mm});
            skLineSegment(sketch, "E353", {"start": v(524.5, 70.4) * mm, "end": v(524.5, 70.62) * mm});
            skLineSegment(sketch, "E354", {"start": v(524.5, 70.62) * mm, "end": v(524.27, 70.64) * mm});
            skArc(sketch, "E355", {"start": v(524.27, 70.64) * mm, "mid": v(521.48, 73.76) * mm, "end": v(524.5, 76.66) * mm});
            skLineSegment(sketch, "E356", {"start": v(524.5, 76.66) * mm, "end": v(543, 76.66) * mm});
            skArc(sketch, "E357", {"start": v(543, 76.66) * mm, "mid": v(546, 73.76) * mm, "end": v(543.23, 70.64) * mm});
            skLineSegment(sketch, "E358", {"start": v(543.23, 70.64) * mm, "end": v(543, 70.62) * mm});
            skLineSegment(sketch, "E359", {"start": v(543, 70.62) * mm, "end": v(543, 70.4) * mm});
            skLineSegment(sketch, "E360", {"start": v(543, 70.4) * mm, "end": v(543, 16.67) * mm});
            skLineSegment(sketch, "E361", {"start": v(543, 16.67) * mm, "end": v(599.5, 16.67) * mm});
            skLineSegment(sketch, "E362", {"start": v(599.5, 16.67) * mm, "end": v(599.52, 565.93) * mm});
            skLineSegment(sketch, "E363", {"start": v(599.52, 565.93) * mm, "end": v(543.02, 565.93) * mm});
            skLineSegment(sketch, "E364", {"start": v(543.02, 565.93) * mm, "end": v(543.01, 482.44) * mm});
            skLineSegment(sketch, "E365", {"start": v(543.01, 482.44) * mm, "end": v(543.01, 482.2) * mm});
            skLineSegment(sketch, "E366", {"start": v(543.01, 482.2) * mm, "end": v(543.24, 482.19) * mm});
            skArc(sketch, "E367", {"start": v(543.24, 482.19) * mm, "mid": v(546.03, 479.07) * mm, "end": v(543.01, 476.17) * mm});
            skLineSegment(sketch, "E368", {"start": v(543.01, 476.17) * mm, "end": v(524.51, 476.17) * mm});
            skArc(sketch, "E369", {"start": v(524.51, 476.17) * mm, "mid": v(521.5, 479.07) * mm, "end": v(524.28, 482.19) * mm});
            skLineSegment(sketch, "E370", {"start": v(524.28, 482.19) * mm, "end": v(524.51, 482.2) * mm});
            skLineSegment(sketch, "E371", {"start": v(524.51, 482.2) * mm, "end": v(524.51, 482.44) * mm});
            skLineSegment(sketch, "E372", {"start": v(524.51, 482.44) * mm, "end": v(524.52, 527.17) * mm});
            skLineSegment(sketch, "E373", {"start": v(524.52, 527.17) * mm, "end": v(500.79, 527.17) * mm});
            skLineSegment(sketch, "E374", {"start": v(500.79, 527.17) * mm, "end": v(500.55, 527.17) * mm});
            skLineSegment(sketch, "E375", {"start": v(500.55, 527.17) * mm, "end": v(500.54, 526.94) * mm});
            skArc(sketch, "E376", {"start": v(500.54, 526.94) * mm, "mid": v(497.42, 524.15) * mm, "end": v(494.52, 527.17) * mm});
            skLineSegment(sketch, "E377", {"start": v(494.52, 527.17) * mm, "end": v(494.52, 539.4) * mm});
            skLineSegment(sketch, "E378", {"start": v(494.52, 539.4) * mm, "end": v(494.52, 539.63) * mm});
            skLineSegment(sketch, "E379", {"start": v(494.52, 539.63) * mm, "end": v(494.29, 539.65) * mm});
            skArc(sketch, "E380", {"start": v(494.29, 539.65) * mm, "mid": v(491.5, 542.77) * mm, "end": v(494.52, 545.67) * mm});
            skLineSegment(sketch, "E381", {"start": v(494.52, 545.67) * mm, "end": v(524.52, 545.67) * mm});
            skLineSegment(sketch, "E382", {"start": v(524.52, 545.67) * mm, "end": v(524.52, 565.93) * mm});
            skLineSegment(sketch, "E383", {"start": v(524.52, 565.93) * mm, "end": v(488.52, 565.94) * mm});
            skArc(sketch, "E384", {"start": v(488.52, 565.94) * mm, "mid": v(485.5, 568.84) * mm, "end": v(488.28, 571.96) * mm});
            skLineSegment(sketch, "E385", {"start": v(488.28, 571.96) * mm, "end": v(488.52, 571.97) * mm});
            skLineSegment(sketch, "E386", {"start": v(488.52, 571.97) * mm, "end": v(488.52, 572.2) * mm});
            skLineSegment(sketch, "E387", {"start": v(488.52, 572.2) * mm, "end": v(488.52, 583.93) * mm});
            skLineSegment(sketch, "E388", {"start": v(488.52, 583.93) * mm, "end": v(-488.98, 583.96) * mm});
            skLineSegment(sketch, "E389", {"start": v(-488.98, 583.96) * mm, "end": v(-488.98, 572.23) * mm});
            skLineSegment(sketch, "E390", {"start": v(-488.98, 572.23) * mm, "end": v(-488.98, 572) * mm});
            skLineSegment(sketch, "E391", {"start": v(-488.98, 572) * mm, "end": v(-488.75, 571.98) * mm});
            skArc(sketch, "E392", {"start": v(-488.75, 571.98) * mm, "mid": v(-485.97, 568.86) * mm, "end": v(-488.98, 565.96) * mm});
            skLineSegment(sketch, "E393", {"start": v(-488.98, 565.96) * mm, "end": v(-524.98, 565.96) * mm});
            skLineSegment(sketch, "E394", {"start": v(-524.98, 565.96) * mm, "end": v(-524.99, 545.7) * mm});
            skLineSegment(sketch, "E395", {"start": v(-524.99, 545.7) * mm, "end": v(-494.99, 545.7) * mm});
            skArc(sketch, "E396", {"start": v(-494.99, 545.7) * mm, "mid": v(-491.98, 542.8) * mm, "end": v(-494.75, 539.67) * mm});
            skLineSegment(sketch, "E397", {"start": v(-494.75, 539.67) * mm, "end": v(-494.99, 539.65) * mm});
            skLineSegment(sketch, "E398", {"start": v(-494.99, 539.65) * mm, "end": v(-494.99, 539.42) * mm});
            skLineSegment(sketch, "E399", {"start": v(-494.99, 539.42) * mm, "end": v(-494.99, 527.2) * mm});
            skArc(sketch, "E400", {"start": v(-494.99, 527.2) * mm, "mid": v(-497.89, 524.18) * mm, "end": v(-501, 526.96) * mm});
            skLineSegment(sketch, "E401", {"start": v(-501, 526.96) * mm, "end": v(-501.02, 527.2) * mm});
            skLineSegment(sketch, "E402", {"start": v(-501.02, 527.2) * mm, "end": v(-501.26, 527.2) * mm});
            skLineSegment(sketch, "E403", {"start": v(-501.26, 527.2) * mm, "end": v(-524.99, 527.2) * mm});
            skLineSegment(sketch, "E404", {"start": v(-524.99, 527.2) * mm, "end": v(-524.99, 482.46) * mm});
            skLineSegment(sketch, "E405", {"start": v(-524.99, 482.46) * mm, "end": v(-524.99, 482.23) * mm});
            skLineSegment(sketch, "E406", {"start": v(-524.99, 482.23) * mm, "end": v(-524.76, 482.21) * mm});
            skArc(sketch, "E407", {"start": v(-524.76, 482.21) * mm, "mid": v(-521.97, 479.1) * mm, "end": v(-524.99, 476.2) * mm});
            skLineSegment(sketch, "E408", {"start": v(-524.99, 476.2) * mm, "end": v(-543.49, 476.2) * mm});
            skArc(sketch, "E409", {"start": v(-543.49, 476.2) * mm, "mid": v(-546.5, 479.1) * mm, "end": v(-543.72, 482.21) * mm});
            skLineSegment(sketch, "E410", {"start": v(-543.72, 482.21) * mm, "end": v(-543.49, 482.23) * mm});
            skLineSegment(sketch, "E411", {"start": v(-543.49, 482.23) * mm, "end": v(-543.49, 482.46) * mm});
            skLineSegment(sketch, "E412", {"start": v(-543.49, 482.46) * mm, "end": v(-543.48, 565.96) * mm});
            skLineSegment(sketch, "E413", {"start": v(-543.48, 565.96) * mm, "end": v(-599.99, 565.96) * mm});
            skLineSegment(sketch, "E414", {"start": v(-432.5, -960.67) * mm, "end": v(-414, -960.67) * mm});
            skArc(sketch, "E415", {"start": v(-414, -960.67) * mm, "mid": v(-410.99, -957.66) * mm, "end": v(-414, -954.65) * mm});
            skLineSegment(sketch, "E416", {"start": v(-414, -954.65) * mm, "end": v(-414, -846.2) * mm});
            skArc(sketch, "E417", {"start": v(-414, -846.2) * mm, "mid": v(-410.99, -843.18) * mm, "end": v(-414, -840.17) * mm});
            skLineSegment(sketch, "E418", {"start": v(-414, -840.17) * mm, "end": v(-432.5, -840.17) * mm});
            skArc(sketch, "E419", {"start": v(-432.5, -840.17) * mm, "mid": v(-435.5, -843.18) * mm, "end": v(-432.5, -846.2) * mm});
            skLineSegment(sketch, "E420", {"start": v(-432.5, -846.2) * mm, "end": v(-432.5, -954.65) * mm});
            skArc(sketch, "E421", {"start": v(-432.5, -954.65) * mm, "mid": v(-435.5, -957.66) * mm, "end": v(-432.5, -960.67) * mm});
            skLineSegment(sketch, "E422", {"start": v(109.48, -1111.17) * mm, "end": v(1.02, -1111.17) * mm});
            skArc(sketch, "E423", {"start": v(1.02, -1111.17) * mm, "mid": v(-1.99, -1108.16) * mm, "end": v(-5, -1111.17) * mm});
            skLineSegment(sketch, "E424", {"start": v(-5, -1111.17) * mm, "end": v(-5, -1129.67) * mm});
            skArc(sketch, "E425", {"start": v(-5, -1129.67) * mm, "mid": v(-1.99, -1132.68) * mm, "end": v(1.02, -1129.67) * mm});
            skLineSegment(sketch, "E426", {"start": v(1.02, -1129.67) * mm, "end": v(109.48, -1129.67) * mm});
            skArc(sketch, "E427", {"start": v(109.48, -1129.67) * mm, "mid": v(112.5, -1132.68) * mm, "end": v(115.5, -1129.67) * mm});
            skLineSegment(sketch, "E428", {"start": v(115.5, -1129.67) * mm, "end": v(115.5, -1111.17) * mm});
            skArc(sketch, "E429", {"start": v(115.5, -1111.17) * mm, "mid": v(112.5, -1108.16) * mm, "end": v(109.48, -1111.17) * mm});
            skLineSegment(sketch, "E430", {"start": v(543, -954.65) * mm, "end": v(543, -846.2) * mm});
            skArc(sketch, "E431", {"start": v(543, -846.2) * mm, "mid": v(546.01, -843.18) * mm, "end": v(543, -840.17) * mm});
            skLineSegment(sketch, "E432", {"start": v(543, -840.17) * mm, "end": v(524.5, -840.17) * mm});
            skArc(sketch, "E433", {"start": v(524.5, -840.17) * mm, "mid": v(521.5, -843.18) * mm, "end": v(524.5, -846.2) * mm});
            skLineSegment(sketch, "E434", {"start": v(524.5, -846.2) * mm, "end": v(524.5, -954.65) * mm});
            skArc(sketch, "E435", {"start": v(524.5, -954.65) * mm, "mid": v(521.5, -957.66) * mm, "end": v(524.5, -960.67) * mm});
            skLineSegment(sketch, "E436", {"start": v(524.5, -960.67) * mm, "end": v(543, -960.67) * mm});
            skArc(sketch, "E437", {"start": v(543, -960.67) * mm, "mid": v(546.01, -957.66) * mm, "end": v(543, -954.65) * mm});
            skLineSegment(sketch, "E438", {"start": v(-564.5, -846.2) * mm, "end": v(-564.5, -954.65) * mm});
            skArc(sketch, "E439", {"start": v(-564.5, -954.65) * mm, "mid": v(-567.5, -957.66) * mm, "end": v(-564.5, -960.67) * mm});
            skLineSegment(sketch, "E440", {"start": v(-564.5, -960.67) * mm, "end": v(-546, -960.67) * mm});
            skArc(sketch, "E441", {"start": v(-546, -960.67) * mm, "mid": v(-542.99, -957.66) * mm, "end": v(-546, -954.65) * mm});
            skLineSegment(sketch, "E442", {"start": v(-546, -954.65) * mm, "end": v(-546, -846.2) * mm});
            skArc(sketch, "E443", {"start": v(-546, -846.2) * mm, "mid": v(-542.99, -843.18) * mm, "end": v(-546, -840.17) * mm});
            skLineSegment(sketch, "E444", {"start": v(-546, -840.17) * mm, "end": v(-564.5, -840.17) * mm});
            skArc(sketch, "E445", {"start": v(-564.5, -840.17) * mm, "mid": v(-567.5, -843.18) * mm, "end": v(-564.5, -846.2) * mm});
            skLineSegment(sketch, "E446", {"start": v(-432.5, -220.67) * mm, "end": v(-414, -220.67) * mm});
            skArc(sketch, "E447", {"start": v(-414, -220.67) * mm, "mid": v(-410.99, -223.68) * mm, "end": v(-414, -226.7) * mm});
            skLineSegment(sketch, "E448", {"start": v(-414, -226.7) * mm, "end": v(-414, -335.15) * mm});
            skArc(sketch, "E449", {"start": v(-414, -335.15) * mm, "mid": v(-410.99, -338.16) * mm, "end": v(-414, -341.17) * mm});
            skLineSegment(sketch, "E450", {"start": v(-414, -341.17) * mm, "end": v(-432.5, -341.17) * mm});
            skArc(sketch, "E451", {"start": v(-432.5, -341.17) * mm, "mid": v(-435.5, -338.16) * mm, "end": v(-432.5, -335.15) * mm});
            skLineSegment(sketch, "E452", {"start": v(-432.5, -335.15) * mm, "end": v(-432.5, -226.7) * mm});
            skArc(sketch, "E453", {"start": v(-432.5, -226.7) * mm, "mid": v(-435.5, -223.68) * mm, "end": v(-432.5, -220.67) * mm});
            skLineSegment(sketch, "E454", {"start": v(109.48, -70.17) * mm, "end": v(1.02, -70.17) * mm});
            skArc(sketch, "E455", {"start": v(1.02, -70.17) * mm, "mid": v(-1.99, -73.18) * mm, "end": v(-5, -70.17) * mm});
            skLineSegment(sketch, "E456", {"start": v(-5, -70.17) * mm, "end": v(-5, -51.67) * mm});
            skArc(sketch, "E457", {"start": v(-5, -51.67) * mm, "mid": v(-1.99, -48.66) * mm, "end": v(1.02, -51.67) * mm});
            skLineSegment(sketch, "E458", {"start": v(1.02, -51.67) * mm, "end": v(109.48, -51.67) * mm});
            skArc(sketch, "E459", {"start": v(109.48, -51.67) * mm, "mid": v(112.5, -48.66) * mm, "end": v(115.5, -51.67) * mm});
            skLineSegment(sketch, "E460", {"start": v(115.5, -51.67) * mm, "end": v(115.5, -70.17) * mm});
            skArc(sketch, "E461", {"start": v(115.5, -70.17) * mm, "mid": v(112.5, -73.18) * mm, "end": v(109.48, -70.17) * mm});
            skLineSegment(sketch, "E462", {"start": v(543, -226.7) * mm, "end": v(543, -335.15) * mm});
            skArc(sketch, "E463", {"start": v(543, -335.15) * mm, "mid": v(546.01, -338.16) * mm, "end": v(543, -341.17) * mm});
            skLineSegment(sketch, "E464", {"start": v(543, -341.17) * mm, "end": v(524.5, -341.17) * mm});
            skArc(sketch, "E465", {"start": v(524.5, -341.17) * mm, "mid": v(521.5, -338.16) * mm, "end": v(524.5, -335.15) * mm});
            skLineSegment(sketch, "E466", {"start": v(524.5, -335.15) * mm, "end": v(524.5, -226.7) * mm});
            skArc(sketch, "E467", {"start": v(524.5, -226.7) * mm, "mid": v(521.5, -223.68) * mm, "end": v(524.5, -220.67) * mm});
            skLineSegment(sketch, "E468", {"start": v(524.5, -220.67) * mm, "end": v(543, -220.67) * mm});
            skArc(sketch, "E469", {"start": v(543, -220.67) * mm, "mid": v(546.01, -223.68) * mm, "end": v(543, -226.7) * mm});
            skLineSegment(sketch, "E470", {"start": v(-564.5, -335.15) * mm, "end": v(-564.5, -226.7) * mm});
            skArc(sketch, "E471", {"start": v(-564.5, -226.7) * mm, "mid": v(-567.5, -223.68) * mm, "end": v(-564.5, -220.67) * mm});
            skLineSegment(sketch, "E472", {"start": v(-564.5, -220.67) * mm, "end": v(-546, -220.67) * mm});
            skArc(sketch, "E473", {"start": v(-546, -220.67) * mm, "mid": v(-542.99, -223.68) * mm, "end": v(-546, -226.7) * mm});
            skLineSegment(sketch, "E474", {"start": v(-546, -226.7) * mm, "end": v(-546, -335.15) * mm});
            skArc(sketch, "E475", {"start": v(-546, -335.15) * mm, "mid": v(-542.99, -338.16) * mm, "end": v(-546, -341.17) * mm});
            skLineSegment(sketch, "E476", {"start": v(-546, -341.17) * mm, "end": v(-564.5, -341.17) * mm});
            skArc(sketch, "E477", {"start": v(-564.5, -341.17) * mm, "mid": v(-567.5, -338.16) * mm, "end": v(-564.5, -335.15) * mm});
            skLineSegment(sketch, "E478", {"start": v(-54.47, 1119.46) * mm, "end": v(54, 1119.46) * mm});
            skArc(sketch, "E479", {"start": v(54, 1119.46) * mm, "mid": v(57, 1116.45) * mm, "end": v(60.01, 1119.46) * mm});
            skLineSegment(sketch, "E480", {"start": v(60.01, 1119.46) * mm, "end": v(60.01, 1137.96) * mm});
            skArc(sketch, "E481", {"start": v(60.01, 1137.96) * mm, "mid": v(57, 1140.97) * mm, "end": v(54, 1137.96) * mm});
            skLineSegment(sketch, "E482", {"start": v(54, 1137.96) * mm, "end": v(-54.47, 1137.96) * mm});
            skArc(sketch, "E483", {"start": v(-54.47, 1137.96) * mm, "mid": v(-57.48, 1140.97) * mm, "end": v(-60.49, 1137.96) * mm});
            skLineSegment(sketch, "E484", {"start": v(-60.49, 1137.96) * mm, "end": v(-60.49, 1119.46) * mm});
            skArc(sketch, "E485", {"start": v(-60.49, 1119.46) * mm, "mid": v(-57.48, 1116.45) * mm, "end": v(-54.47, 1119.46) * mm});
            skLineSegment(sketch, "E486", {"start": v(-543.5, 962.94) * mm, "end": v(-543.5, 854.48) * mm});
            skArc(sketch, "E487", {"start": v(-543.5, 854.48) * mm, "mid": v(-546.5, 851.47) * mm, "end": v(-543.5, 848.46) * mm});
            skLineSegment(sketch, "E488", {"start": v(-543.5, 848.46) * mm, "end": v(-525, 848.46) * mm});
            skArc(sketch, "E489", {"start": v(-525, 848.46) * mm, "mid": v(-521.98, 851.47) * mm, "end": v(-525, 854.48) * mm});
            skLineSegment(sketch, "E490", {"start": v(-525, 854.48) * mm, "end": v(-525, 962.94) * mm});
            skArc(sketch, "E491", {"start": v(-525, 962.94) * mm, "mid": v(-521.98, 965.95) * mm, "end": v(-525, 968.96) * mm});
            skLineSegment(sketch, "E492", {"start": v(-525, 968.96) * mm, "end": v(-543.5, 968.96) * mm});
            skArc(sketch, "E493", {"start": v(-543.5, 968.96) * mm, "mid": v(-546.5, 965.95) * mm, "end": v(-543.5, 962.94) * mm});
            skLineSegment(sketch, "E494", {"start": v(524.5, 848.45) * mm, "end": v(543, 848.45) * mm});
            skArc(sketch, "E495", {"start": v(543, 848.45) * mm, "mid": v(546.02, 851.46) * mm, "end": v(543, 854.47) * mm});
            skLineSegment(sketch, "E496", {"start": v(543, 854.47) * mm, "end": v(543, 962.93) * mm});
            skArc(sketch, "E497", {"start": v(543, 962.93) * mm, "mid": v(546.02, 965.94) * mm, "end": v(543, 968.95) * mm});
            skLineSegment(sketch, "E498", {"start": v(543, 968.95) * mm, "end": v(524.51, 968.95) * mm});
            skArc(sketch, "E499", {"start": v(524.51, 968.95) * mm, "mid": v(521.5, 965.94) * mm, "end": v(524.51, 962.93) * mm});
            skLineSegment(sketch, "E500", {"start": v(524.51, 962.93) * mm, "end": v(524.5, 854.47) * mm});
            skArc(sketch, "E501", {"start": v(524.5, 854.47) * mm, "mid": v(521.5, 851.46) * mm, "end": v(524.5, 848.45) * mm});
            skLineSegment(sketch, "E502", {"start": v(-54.47, 527.18) * mm, "end": v(54, 527.18) * mm});
            skArc(sketch, "E503", {"start": v(54, 527.18) * mm, "mid": v(57, 524.17) * mm, "end": v(60.01, 527.18) * mm});
            skLineSegment(sketch, "E504", {"start": v(60.01, 527.18) * mm, "end": v(60.01, 545.68) * mm});
            skArc(sketch, "E505", {"start": v(60.01, 545.68) * mm, "mid": v(57, 548.69) * mm, "end": v(54, 545.68) * mm});
            skLineSegment(sketch, "E506", {"start": v(54, 545.68) * mm, "end": v(-54.47, 545.68) * mm});
            skArc(sketch, "E507", {"start": v(-54.47, 545.68) * mm, "mid": v(-57.48, 548.7) * mm, "end": v(-60.49, 545.68) * mm});
            skLineSegment(sketch, "E508", {"start": v(-60.49, 545.68) * mm, "end": v(-60.49, 527.18) * mm});
            skArc(sketch, "E509", {"start": v(-60.49, 527.18) * mm, "mid": v(-57.48, 524.17) * mm, "end": v(-54.47, 527.18) * mm});
            skLineSegment(sketch, "E510", {"start": v(-543.5, 370.66) * mm, "end": v(-543.5, 262.2) * mm});
            skArc(sketch, "E511", {"start": v(-543.5, 262.2) * mm, "mid": v(-546.5, 259.19) * mm, "end": v(-543.5, 256.18) * mm});
            skLineSegment(sketch, "E512", {"start": v(-543.5, 256.18) * mm, "end": v(-525, 256.18) * mm});
            skArc(sketch, "E513", {"start": v(-525, 256.18) * mm, "mid": v(-521.98, 259.19) * mm, "end": v(-525, 262.2) * mm});
            skLineSegment(sketch, "E514", {"start": v(-525, 262.2) * mm, "end": v(-525, 370.66) * mm});
            skArc(sketch, "E515", {"start": v(-525, 370.66) * mm, "mid": v(-521.98, 373.67) * mm, "end": v(-525, 376.68) * mm});
            skLineSegment(sketch, "E516", {"start": v(-525, 376.68) * mm, "end": v(-543.5, 376.68) * mm});
            skArc(sketch, "E517", {"start": v(-543.5, 376.68) * mm, "mid": v(-546.5, 373.67) * mm, "end": v(-543.5, 370.66) * mm});
            skLineSegment(sketch, "E518", {"start": v(524.5, 256.17) * mm, "end": v(543, 256.17) * mm});
            skArc(sketch, "E519", {"start": v(543, 256.17) * mm, "mid": v(546.02, 259.18) * mm, "end": v(543, 262.19) * mm});
            skLineSegment(sketch, "E520", {"start": v(543, 262.19) * mm, "end": v(543, 370.65) * mm});
            skArc(sketch, "E521", {"start": v(543, 370.65) * mm, "mid": v(546.02, 373.66) * mm, "end": v(543, 376.67) * mm});
            skLineSegment(sketch, "E522", {"start": v(543, 376.67) * mm, "end": v(524.51, 376.67) * mm});
            skArc(sketch, "E523", {"start": v(524.51, 376.67) * mm, "mid": v(521.5, 373.66) * mm, "end": v(524.51, 370.65) * mm});
            skLineSegment(sketch, "E524", {"start": v(524.51, 370.65) * mm, "end": v(524.5, 262.19) * mm});
            skArc(sketch, "E525", {"start": v(524.5, 262.19) * mm, "mid": v(521.5, 259.18) * mm, "end": v(524.5, 256.17) * mm});
            skLineSegment(sketch, "E526", {"start": v(-109.7, 893.3) * mm, "end": v(-109.7, 933.28) * mm});
            skLineSegment(sketch, "E527", {"start": v(-109.7, 933.28) * mm, "end": v(-84.84, 933.28) * mm});
            skLineSegment(sketch, "E528", {"start": v(-109.7, 914.17) * mm, "end": v(-86.63, 914.17) * mm});
            skLineSegment(sketch, "E529", {"start": v(-52.54, 893.32) * mm, "end": v(-76.04, 893.32) * mm});
            skLineSegment(sketch, "E530", {"start": v(-76.04, 893.32) * mm, "end": v(-76.04, 933.27) * mm});
            skLineSegment(sketch, "E531", {"start": v(-37.38, 892.76) * mm, "end": v(-37.8, 892.75) * mm});
            skLineSegment(sketch, "E532", {"start": v(-37.8, 892.75) * mm, "end": v(-38.22, 892.76) * mm});
            skLineSegment(sketch, "E533", {"start": v(-38.22, 892.76) * mm, "end": v(-38.64, 892.78) * mm});
            skLineSegment(sketch, "E534", {"start": v(-38.64, 892.78) * mm, "end": v(-39.05, 892.8) * mm});
            skLineSegment(sketch, "E535", {"start": v(-39.05, 892.8) * mm, "end": v(-39.47, 892.84) * mm});
            skLineSegment(sketch, "E536", {"start": v(-39.47, 892.84) * mm, "end": v(-39.88, 892.9) * mm});
            skLineSegment(sketch, "E537", {"start": v(-39.88, 892.9) * mm, "end": v(-40.3, 892.95) * mm});
            skLineSegment(sketch, "E538", {"start": v(-40.3, 892.95) * mm, "end": v(-40.7, 893.02) * mm});
            skLineSegment(sketch, "E539", {"start": v(-40.7, 893.02) * mm, "end": v(-41.11, 893.1) * mm});
            skLineSegment(sketch, "E540", {"start": v(-41.11, 893.1) * mm, "end": v(-41.51, 893.2) * mm});
            skLineSegment(sketch, "E541", {"start": v(-41.51, 893.2) * mm, "end": v(-41.92, 893.3) * mm});
            skLineSegment(sketch, "E542", {"start": v(-41.92, 893.3) * mm, "end": v(-42.32, 893.4) * mm});
            skLineSegment(sketch, "E543", {"start": v(-42.32, 893.4) * mm, "end": v(-42.71, 893.52) * mm});
            skLineSegment(sketch, "E544", {"start": v(-42.71, 893.52) * mm, "end": v(-43.1, 893.65) * mm});
            skLineSegment(sketch, "E545", {"start": v(-43.1, 893.65) * mm, "end": v(-43.5, 893.79) * mm});
            skLineSegment(sketch, "E546", {"start": v(-43.5, 893.79) * mm, "end": v(-43.88, 893.94) * mm});
            skLineSegment(sketch, "E547", {"start": v(-43.88, 893.94) * mm, "end": v(-44.26, 894.1) * mm});
            skLineSegment(sketch, "E548", {"start": v(-44.26, 894.1) * mm, "end": v(-44.64, 894.26) * mm});
            skLineSegment(sketch, "E549", {"start": v(-44.64, 894.26) * mm, "end": v(-45.02, 894.44) * mm});
            skLineSegment(sketch, "E550", {"start": v(-45.02, 894.44) * mm, "end": v(-45.39, 894.62) * mm});
            skLineSegment(sketch, "E551", {"start": v(-45.39, 894.62) * mm, "end": v(-45.75, 894.82) * mm});
            skLineSegment(sketch, "E552", {"start": v(-45.75, 894.82) * mm, "end": v(-46.11, 895.02) * mm});
            skLineSegment(sketch, "E553", {"start": v(-46.11, 895.02) * mm, "end": v(-46.47, 895.24) * mm});
            skLineSegment(sketch, "E554", {"start": v(-46.47, 895.24) * mm, "end": v(-46.82, 895.46) * mm});
            skLineSegment(sketch, "E555", {"start": v(-46.82, 895.46) * mm, "end": v(-47.16, 895.69) * mm});
            skLineSegment(sketch, "E556", {"start": v(-47.16, 895.69) * mm, "end": v(-47.5, 895.93) * mm});
            skLineSegment(sketch, "E557", {"start": v(-47.5, 895.93) * mm, "end": v(-47.84, 896.18) * mm});
            skLineSegment(sketch, "E558", {"start": v(-47.84, 896.18) * mm, "end": v(-48.17, 896.44) * mm});
            skLineSegment(sketch, "E559", {"start": v(-48.17, 896.44) * mm, "end": v(-48.49, 896.7) * mm});
            skLineSegment(sketch, "E560", {"start": v(-48.49, 896.7) * mm, "end": v(-48.8, 896.98) * mm});
            skLineSegment(sketch, "E561", {"start": v(-48.8, 896.98) * mm, "end": v(-49.11, 897.26) * mm});
            skLineSegment(sketch, "E562", {"start": v(-49.11, 897.26) * mm, "end": v(-49.41, 897.55) * mm});
            skLineSegment(sketch, "E563", {"start": v(-49.41, 897.55) * mm, "end": v(-49.76, 897.93) * mm});
            skLineSegment(sketch, "E564", {"start": v(-49.76, 897.93) * mm, "end": v(-50.1, 898.32) * mm});
            skLineSegment(sketch, "E565", {"start": v(-50.1, 898.32) * mm, "end": v(-50.43, 898.72) * mm});
            skLineSegment(sketch, "E566", {"start": v(-50.43, 898.72) * mm, "end": v(-50.75, 899.12) * mm});
            skLineSegment(sketch, "E567", {"start": v(-50.75, 899.12) * mm, "end": v(-51.06, 899.53) * mm});
            skLineSegment(sketch, "E568", {"start": v(-51.06, 899.53) * mm, "end": v(-51.36, 899.95) * mm});
            skLineSegment(sketch, "E569", {"start": v(-51.36, 899.95) * mm, "end": v(-51.64, 900.37) * mm});
            skLineSegment(sketch, "E570", {"start": v(-51.64, 900.37) * mm, "end": v(-51.92, 900.8) * mm});
            skLineSegment(sketch, "E571", {"start": v(-51.92, 900.8) * mm, "end": v(-52.18, 901.24) * mm});
            skLineSegment(sketch, "E572", {"start": v(-52.18, 901.24) * mm, "end": v(-52.44, 901.68) * mm});
            skLineSegment(sketch, "E573", {"start": v(-52.44, 901.68) * mm, "end": v(-52.68, 902.13) * mm});
            skLineSegment(sketch, "E574", {"start": v(-52.68, 902.13) * mm, "end": v(-52.91, 902.58) * mm});
            skLineSegment(sketch, "E575", {"start": v(-52.91, 902.58) * mm, "end": v(-53.13, 903.04) * mm});
            skLineSegment(sketch, "E576", {"start": v(-53.13, 903.04) * mm, "end": v(-53.34, 903.5) * mm});
            skLineSegment(sketch, "E577", {"start": v(-53.34, 903.5) * mm, "end": v(-53.54, 903.98) * mm});
            skLineSegment(sketch, "E578", {"start": v(-53.54, 903.98) * mm, "end": v(-53.72, 904.45) * mm});
            skLineSegment(sketch, "E579", {"start": v(-53.72, 904.45) * mm, "end": v(-53.9, 904.93) * mm});
            skLineSegment(sketch, "E580", {"start": v(-53.9, 904.93) * mm, "end": v(-54.06, 905.41) * mm});
            skLineSegment(sketch, "E581", {"start": v(-54.06, 905.41) * mm, "end": v(-54.2, 905.9) * mm});
            skLineSegment(sketch, "E582", {"start": v(-54.2, 905.9) * mm, "end": v(-54.35, 906.4) * mm});
            skLineSegment(sketch, "E583", {"start": v(-54.35, 906.4) * mm, "end": v(-54.47, 906.89) * mm});
            skLineSegment(sketch, "E584", {"start": v(-54.47, 906.89) * mm, "end": v(-54.59, 907.38) * mm});
            skLineSegment(sketch, "E585", {"start": v(-54.59, 907.38) * mm, "end": v(-54.69, 907.88) * mm});
            skLineSegment(sketch, "E586", {"start": v(-54.69, 907.88) * mm, "end": v(-54.78, 908.39) * mm});
            skLineSegment(sketch, "E587", {"start": v(-54.78, 908.39) * mm, "end": v(-54.85, 908.9) * mm});
            skLineSegment(sketch, "E588", {"start": v(-54.85, 908.9) * mm, "end": v(-54.92, 909.4) * mm});
            skLineSegment(sketch, "E589", {"start": v(-54.92, 909.4) * mm, "end": v(-54.97, 909.9) * mm});
            skLineSegment(sketch, "E590", {"start": v(-54.97, 909.9) * mm, "end": v(-55.01, 910.42) * mm});
            skLineSegment(sketch, "E591", {"start": v(-55.01, 910.42) * mm, "end": v(-55.04, 910.93) * mm});
            skLineSegment(sketch, "E592", {"start": v(-55.04, 910.93) * mm, "end": v(-55.05, 911.45) * mm});
            skLineSegment(sketch, "E593", {"start": v(-55.05, 911.45) * mm, "end": v(-55.05, 911.96) * mm});
            skLineSegment(sketch, "E594", {"start": v(-55.05, 911.96) * mm, "end": v(-55.04, 912.48) * mm});
            skLineSegment(sketch, "E595", {"start": v(-55.04, 912.48) * mm, "end": v(-55.06, 913.04) * mm});
            skLineSegment(sketch, "E596", {"start": v(-55.06, 913.04) * mm, "end": v(-55.06, 913.6) * mm});
            skLineSegment(sketch, "E597", {"start": v(-55.06, 913.6) * mm, "end": v(-55.05, 914.16) * mm});
            skLineSegment(sketch, "E598", {"start": v(-55.05, 914.16) * mm, "end": v(-55.02, 914.72) * mm});
            skLineSegment(sketch, "E599", {"start": v(-55.02, 914.72) * mm, "end": v(-54.98, 915.28) * mm});
            skLineSegment(sketch, "E600", {"start": v(-54.98, 915.28) * mm, "end": v(-54.92, 915.83) * mm});
            skLineSegment(sketch, "E601", {"start": v(-54.92, 915.83) * mm, "end": v(-54.86, 916.38) * mm});
            skLineSegment(sketch, "E602", {"start": v(-54.86, 916.38) * mm, "end": v(-54.77, 916.93) * mm});
            skLineSegment(sketch, "E603", {"start": v(-54.77, 916.93) * mm, "end": v(-54.68, 917.48) * mm});
            skLineSegment(sketch, "E604", {"start": v(-54.68, 917.48) * mm, "end": v(-54.57, 918.02) * mm});
            skLineSegment(sketch, "E605", {"start": v(-54.57, 918.02) * mm, "end": v(-54.45, 918.56) * mm});
            skLineSegment(sketch, "E606", {"start": v(-54.45, 918.56) * mm, "end": v(-54.31, 919.1) * mm});
            skLineSegment(sketch, "E607", {"start": v(-54.31, 919.1) * mm, "end": v(-54.16, 919.63) * mm});
            skLineSegment(sketch, "E608", {"start": v(-54.16, 919.63) * mm, "end": v(-54, 920.16) * mm});
            skLineSegment(sketch, "E609", {"start": v(-54, 920.16) * mm, "end": v(-53.83, 920.68) * mm});
            skLineSegment(sketch, "E610", {"start": v(-53.83, 920.68) * mm, "end": v(-53.64, 921.2) * mm});
            skLineSegment(sketch, "E611", {"start": v(-53.64, 921.2) * mm, "end": v(-53.44, 921.72) * mm});
            skLineSegment(sketch, "E612", {"start": v(-53.44, 921.72) * mm, "end": v(-53.22, 922.23) * mm});
            skLineSegment(sketch, "E613", {"start": v(-53.22, 922.23) * mm, "end": v(-53, 922.73) * mm});
            skLineSegment(sketch, "E614", {"start": v(-53, 922.73) * mm, "end": v(-52.76, 923.23) * mm});
            skLineSegment(sketch, "E615", {"start": v(-52.76, 923.23) * mm, "end": v(-52.5, 923.72) * mm});
            skLineSegment(sketch, "E616", {"start": v(-52.5, 923.72) * mm, "end": v(-52.24, 924.21) * mm});
            skLineSegment(sketch, "E617", {"start": v(-52.24, 924.21) * mm, "end": v(-51.97, 924.7) * mm});
            skLineSegment(sketch, "E618", {"start": v(-51.97, 924.7) * mm, "end": v(-51.68, 925.17) * mm});
            skLineSegment(sketch, "E619", {"start": v(-51.68, 925.17) * mm, "end": v(-51.38, 925.63) * mm});
            skLineSegment(sketch, "E620", {"start": v(-51.38, 925.63) * mm, "end": v(-51.07, 926.1) * mm});
            skLineSegment(sketch, "E621", {"start": v(-51.07, 926.1) * mm, "end": v(-50.74, 926.55) * mm});
            skLineSegment(sketch, "E622", {"start": v(-50.74, 926.55) * mm, "end": v(-50.4, 927) * mm});
            skLineSegment(sketch, "E623", {"start": v(-50.4, 927) * mm, "end": v(-50.06, 927.43) * mm});
            skLineSegment(sketch, "E624", {"start": v(-50.06, 927.43) * mm, "end": v(-49.7, 927.86) * mm});
            skLineSegment(sketch, "E625", {"start": v(-49.7, 927.86) * mm, "end": v(-49.33, 928.28) * mm});
            skLineSegment(sketch, "E626", {"start": v(-49.33, 928.28) * mm, "end": v(-48.95, 928.69) * mm});
            skLineSegment(sketch, "E627", {"start": v(-48.95, 928.69) * mm, "end": v(-48.66, 928.98) * mm});
            skLineSegment(sketch, "E628", {"start": v(-48.66, 928.98) * mm, "end": v(-48.37, 929.26) * mm});
            skLineSegment(sketch, "E629", {"start": v(-48.37, 929.26) * mm, "end": v(-48.07, 929.54) * mm});
            skLineSegment(sketch, "E630", {"start": v(-48.07, 929.54) * mm, "end": v(-47.77, 929.8) * mm});
            skLineSegment(sketch, "E631", {"start": v(-47.77, 929.8) * mm, "end": v(-47.45, 930.06) * mm});
            skLineSegment(sketch, "E632", {"start": v(-47.45, 930.06) * mm, "end": v(-47.14, 930.3) * mm});
            skLineSegment(sketch, "E633", {"start": v(-47.14, 930.3) * mm, "end": v(-46.81, 930.55) * mm});
            skLineSegment(sketch, "E634", {"start": v(-46.81, 930.55) * mm, "end": v(-46.48, 930.78) * mm});
            skLineSegment(sketch, "E635", {"start": v(-46.48, 930.78) * mm, "end": v(-46.15, 931) * mm});
            skLineSegment(sketch, "E636", {"start": v(-46.15, 931) * mm, "end": v(-45.8, 931.22) * mm});
            skLineSegment(sketch, "E637", {"start": v(-45.8, 931.22) * mm, "end": v(-45.46, 931.42) * mm});
            skLineSegment(sketch, "E638", {"start": v(-45.46, 931.42) * mm, "end": v(-45.11, 931.62) * mm});
            skLineSegment(sketch, "E639", {"start": v(-45.11, 931.62) * mm, "end": v(-44.76, 931.8) * mm});
            skLineSegment(sketch, "E640", {"start": v(-44.76, 931.8) * mm, "end": v(-44.4, 931.98) * mm});
            skLineSegment(sketch, "E641", {"start": v(-44.4, 931.98) * mm, "end": v(-44.03, 932.15) * mm});
            skLineSegment(sketch, "E642", {"start": v(-44.03, 932.15) * mm, "end": v(-43.66, 932.3) * mm});
            skLineSegment(sketch, "E643", {"start": v(-43.66, 932.3) * mm, "end": v(-43.3, 932.46) * mm});
            skLineSegment(sketch, "E644", {"start": v(-43.3, 932.46) * mm, "end": v(-42.92, 932.6) * mm});
            skLineSegment(sketch, "E645", {"start": v(-42.92, 932.6) * mm, "end": v(-42.54, 932.73) * mm});
            skLineSegment(sketch, "E646", {"start": v(-42.54, 932.73) * mm, "end": v(-42.15, 932.85) * mm});
            skLineSegment(sketch, "E647", {"start": v(-42.15, 932.85) * mm, "end": v(-41.77, 932.96) * mm});
            skLineSegment(sketch, "E648", {"start": v(-41.77, 932.96) * mm, "end": v(-41.38, 933.06) * mm});
            skLineSegment(sketch, "E649", {"start": v(-41.38, 933.06) * mm, "end": v(-40.99, 933.15) * mm});
            skLineSegment(sketch, "E650", {"start": v(-40.99, 933.15) * mm, "end": v(-40.6, 933.24) * mm});
            skLineSegment(sketch, "E651", {"start": v(-40.6, 933.24) * mm, "end": v(-40.2, 933.3) * mm});
            skLineSegment(sketch, "E652", {"start": v(-40.2, 933.3) * mm, "end": v(-39.8, 933.37) * mm});
            skLineSegment(sketch, "E653", {"start": v(-39.8, 933.37) * mm, "end": v(-39.4, 933.42) * mm});
            skLineSegment(sketch, "E654", {"start": v(-39.4, 933.42) * mm, "end": v(-39, 933.46) * mm});
            skLineSegment(sketch, "E655", {"start": v(-39, 933.46) * mm, "end": v(-38.6, 933.49) * mm});
            skLineSegment(sketch, "E656", {"start": v(-38.6, 933.49) * mm, "end": v(-38.19, 933.5) * mm});
            skLineSegment(sketch, "E657", {"start": v(-38.19, 933.5) * mm, "end": v(-37.78, 933.52) * mm});
            skLineSegment(sketch, "E658", {"start": v(-37.78, 933.52) * mm, "end": v(-37.37, 933.52) * mm});
            skLineSegment(sketch, "E659", {"start": v(-37.37, 933.52) * mm, "end": v(-36.96, 933.51) * mm});
            skLineSegment(sketch, "E660", {"start": v(-36.96, 933.51) * mm, "end": v(-36.54, 933.5) * mm});
            skLineSegment(sketch, "E661", {"start": v(-36.54, 933.5) * mm, "end": v(-36.13, 933.47) * mm});
            skLineSegment(sketch, "E662", {"start": v(-36.13, 933.47) * mm, "end": v(-35.72, 933.44) * mm});
            skLineSegment(sketch, "E663", {"start": v(-35.72, 933.44) * mm, "end": v(-35.31, 933.4) * mm});
            skLineSegment(sketch, "E664", {"start": v(-35.31, 933.4) * mm, "end": v(-34.9, 933.33) * mm});
            skLineSegment(sketch, "E665", {"start": v(-34.9, 933.33) * mm, "end": v(-34.5, 933.27) * mm});
            skLineSegment(sketch, "E666", {"start": v(-34.5, 933.27) * mm, "end": v(-34.1, 933.19) * mm});
            skLineSegment(sketch, "E667", {"start": v(-34.1, 933.19) * mm, "end": v(-33.7, 933.1) * mm});
            skLineSegment(sketch, "E668", {"start": v(-33.7, 933.1) * mm, "end": v(-33.3, 933) * mm});
            skLineSegment(sketch, "E669", {"start": v(-33.3, 933) * mm, "end": v(-32.91, 932.9) * mm});
            skLineSegment(sketch, "E670", {"start": v(-32.91, 932.9) * mm, "end": v(-32.52, 932.78) * mm});
            skLineSegment(sketch, "E671", {"start": v(-32.52, 932.78) * mm, "end": v(-32.13, 932.65) * mm});
            skLineSegment(sketch, "E672", {"start": v(-32.13, 932.65) * mm, "end": v(-31.75, 932.51) * mm});
            skLineSegment(sketch, "E673", {"start": v(-31.75, 932.51) * mm, "end": v(-31.37, 932.37) * mm});
            skLineSegment(sketch, "E674", {"start": v(-31.37, 932.37) * mm, "end": v(-31, 932.2) * mm});
            skLineSegment(sketch, "E675", {"start": v(-31, 932.2) * mm, "end": v(-30.62, 932.04) * mm});
            skLineSegment(sketch, "E676", {"start": v(-30.62, 932.04) * mm, "end": v(-30.25, 931.87) * mm});
            skLineSegment(sketch, "E677", {"start": v(-30.25, 931.87) * mm, "end": v(-29.89, 931.68) * mm});
            skLineSegment(sketch, "E678", {"start": v(-29.89, 931.68) * mm, "end": v(-29.53, 931.49) * mm});
            skLineSegment(sketch, "E679", {"start": v(-29.53, 931.49) * mm, "end": v(-29.17, 931.29) * mm});
            skLineSegment(sketch, "E680", {"start": v(-29.17, 931.29) * mm, "end": v(-28.83, 931.07) * mm});
            skLineSegment(sketch, "E681", {"start": v(-28.83, 931.07) * mm, "end": v(-28.48, 930.85) * mm});
            skLineSegment(sketch, "E682", {"start": v(-28.48, 930.85) * mm, "end": v(-28.14, 930.62) * mm});
            skLineSegment(sketch, "E683", {"start": v(-28.14, 930.62) * mm, "end": v(-27.81, 930.38) * mm});
            skLineSegment(sketch, "E684", {"start": v(-27.81, 930.38) * mm, "end": v(-27.49, 930.13) * mm});
            skLineSegment(sketch, "E685", {"start": v(-27.49, 930.13) * mm, "end": v(-27.17, 929.88) * mm});
            skLineSegment(sketch, "E686", {"start": v(-27.17, 929.88) * mm, "end": v(-26.85, 929.61) * mm});
            skLineSegment(sketch, "E687", {"start": v(-26.85, 929.61) * mm, "end": v(-26.54, 929.34) * mm});
            skLineSegment(sketch, "E688", {"start": v(-26.54, 929.34) * mm, "end": v(-26.24, 929.05) * mm});
            skLineSegment(sketch, "E689", {"start": v(-26.24, 929.05) * mm, "end": v(-25.95, 928.76) * mm});
            skLineSegment(sketch, "E690", {"start": v(-25.95, 928.76) * mm, "end": v(-25.66, 928.47) * mm});
            skLineSegment(sketch, "E691", {"start": v(-25.66, 928.47) * mm, "end": v(-25.3, 928.06) * mm});
            skLineSegment(sketch, "E692", {"start": v(-25.3, 928.06) * mm, "end": v(-24.93, 927.64) * mm});
            skLineSegment(sketch, "E693", {"start": v(-24.93, 927.64) * mm, "end": v(-24.59, 927.21) * mm});
            skLineSegment(sketch, "E694", {"start": v(-24.59, 927.21) * mm, "end": v(-24.25, 926.78) * mm});
            skLineSegment(sketch, "E695", {"start": v(-24.25, 926.78) * mm, "end": v(-23.92, 926.34) * mm});
            skLineSegment(sketch, "E696", {"start": v(-23.92, 926.34) * mm, "end": v(-23.61, 925.89) * mm});
            skLineSegment(sketch, "E697", {"start": v(-23.61, 925.89) * mm, "end": v(-23.3, 925.43) * mm});
            skLineSegment(sketch, "E698", {"start": v(-23.3, 925.43) * mm, "end": v(-23.02, 924.97) * mm});
            skLineSegment(sketch, "E699", {"start": v(-23.02, 924.97) * mm, "end": v(-22.74, 924.5) * mm});
            skLineSegment(sketch, "E700", {"start": v(-22.74, 924.5) * mm, "end": v(-22.48, 924.02) * mm});
            skLineSegment(sketch, "E701", {"start": v(-22.48, 924.02) * mm, "end": v(-22.22, 923.54) * mm});
            skLineSegment(sketch, "E702", {"start": v(-22.22, 923.54) * mm, "end": v(-21.98, 923.05) * mm});
            skLineSegment(sketch, "E703", {"start": v(-21.98, 923.05) * mm, "end": v(-21.75, 922.56) * mm});
            skLineSegment(sketch, "E704", {"start": v(-21.75, 922.56) * mm, "end": v(-21.53, 922.06) * mm});
            skLineSegment(sketch, "E705", {"start": v(-21.53, 922.06) * mm, "end": v(-21.33, 921.56) * mm});
            skLineSegment(sketch, "E706", {"start": v(-21.33, 921.56) * mm, "end": v(-21.13, 921.05) * mm});
            skLineSegment(sketch, "E707", {"start": v(-21.13, 921.05) * mm, "end": v(-20.96, 920.54) * mm});
            skLineSegment(sketch, "E708", {"start": v(-20.96, 920.54) * mm, "end": v(-20.79, 920.02) * mm});
            skLineSegment(sketch, "E709", {"start": v(-20.79, 920.02) * mm, "end": v(-20.63, 919.5) * mm});
            skLineSegment(sketch, "E710", {"start": v(-20.63, 919.5) * mm, "end": v(-20.5, 918.97) * mm});
            skLineSegment(sketch, "E711", {"start": v(-20.5, 918.97) * mm, "end": v(-20.36, 918.44) * mm});
            skLineSegment(sketch, "E712", {"start": v(-20.36, 918.44) * mm, "end": v(-20.25, 917.9) * mm});
            skLineSegment(sketch, "E713", {"start": v(-20.25, 917.9) * mm, "end": v(-20.14, 917.37) * mm});
            skLineSegment(sketch, "E714", {"start": v(-20.14, 917.37) * mm, "end": v(-20.06, 916.83) * mm});
            skLineSegment(sketch, "E715", {"start": v(-20.06, 916.83) * mm, "end": v(-19.98, 916.3) * mm});
            skLineSegment(sketch, "E716", {"start": v(-19.98, 916.3) * mm, "end": v(-19.92, 915.75) * mm});
            skLineSegment(sketch, "E717", {"start": v(-19.92, 915.75) * mm, "end": v(-19.87, 915.2) * mm});
            skLineSegment(sketch, "E718", {"start": v(-19.87, 915.2) * mm, "end": v(-19.83, 914.66) * mm});
            skLineSegment(sketch, "E719", {"start": v(-19.83, 914.66) * mm, "end": v(-19.81, 914.1) * mm});
            skLineSegment(sketch, "E720", {"start": v(-19.81, 914.1) * mm, "end": v(-19.8, 913.56) * mm});
            skLineSegment(sketch, "E721", {"start": v(-19.8, 913.56) * mm, "end": v(-19.8, 913) * mm});
            skLineSegment(sketch, "E722", {"start": v(-19.8, 913) * mm, "end": v(-19.83, 912.46) * mm});
            skLineSegment(sketch, "E723", {"start": v(-19.83, 912.46) * mm, "end": v(-19.82, 911.94) * mm});
            skLineSegment(sketch, "E724", {"start": v(-19.82, 911.94) * mm, "end": v(-19.82, 911.43) * mm});
            skLineSegment(sketch, "E725", {"start": v(-19.82, 911.43) * mm, "end": v(-19.84, 910.92) * mm});
            skLineSegment(sketch, "E726", {"start": v(-19.84, 910.92) * mm, "end": v(-19.87, 910.4) * mm});
            skLineSegment(sketch, "E727", {"start": v(-19.87, 910.4) * mm, "end": v(-19.92, 909.9) * mm});
            skLineSegment(sketch, "E728", {"start": v(-19.92, 909.9) * mm, "end": v(-19.97, 909.39) * mm});
            skLineSegment(sketch, "E729", {"start": v(-19.97, 909.39) * mm, "end": v(-20.04, 908.88) * mm});
            skLineSegment(sketch, "E730", {"start": v(-20.04, 908.88) * mm, "end": v(-20.12, 908.38) * mm});
            skLineSegment(sketch, "E731", {"start": v(-20.12, 908.38) * mm, "end": v(-20.21, 907.88) * mm});
            skLineSegment(sketch, "E732", {"start": v(-20.21, 907.88) * mm, "end": v(-20.32, 907.38) * mm});
            skLineSegment(sketch, "E733", {"start": v(-20.32, 907.38) * mm, "end": v(-20.44, 906.89) * mm});
            skLineSegment(sketch, "E734", {"start": v(-20.44, 906.89) * mm, "end": v(-20.57, 906.4) * mm});
            skLineSegment(sketch, "E735", {"start": v(-20.57, 906.4) * mm, "end": v(-20.71, 905.91) * mm});
            skLineSegment(sketch, "E736", {"start": v(-20.71, 905.91) * mm, "end": v(-20.87, 905.43) * mm});
            skLineSegment(sketch, "E737", {"start": v(-20.87, 905.43) * mm, "end": v(-21.03, 904.95) * mm});
            skLineSegment(sketch, "E738", {"start": v(-21.03, 904.95) * mm, "end": v(-21.21, 904.47) * mm});
            skLineSegment(sketch, "E739", {"start": v(-21.21, 904.47) * mm, "end": v(-21.4, 904) * mm});
            skLineSegment(sketch, "E740", {"start": v(-21.4, 904) * mm, "end": v(-21.6, 903.54) * mm});
            skLineSegment(sketch, "E741", {"start": v(-21.6, 903.54) * mm, "end": v(-21.82, 903.08) * mm});
            skLineSegment(sketch, "E742", {"start": v(-21.82, 903.08) * mm, "end": v(-22.04, 902.62) * mm});
            skLineSegment(sketch, "E743", {"start": v(-22.04, 902.62) * mm, "end": v(-22.28, 902.17) * mm});
            skLineSegment(sketch, "E744", {"start": v(-22.28, 902.17) * mm, "end": v(-22.52, 901.73) * mm});
            skLineSegment(sketch, "E745", {"start": v(-22.52, 901.73) * mm, "end": v(-22.78, 901.29) * mm});
            skLineSegment(sketch, "E746", {"start": v(-22.78, 901.29) * mm, "end": v(-23.05, 900.86) * mm});
            skLineSegment(sketch, "E747", {"start": v(-23.05, 900.86) * mm, "end": v(-23.33, 900.43) * mm});
            skLineSegment(sketch, "E748", {"start": v(-23.33, 900.43) * mm, "end": v(-23.62, 900.01) * mm});
            skLineSegment(sketch, "E749", {"start": v(-23.62, 900.01) * mm, "end": v(-23.92, 899.6) * mm});
            skLineSegment(sketch, "E750", {"start": v(-23.92, 899.6) * mm, "end": v(-24.24, 899.2) * mm});
            skLineSegment(sketch, "E751", {"start": v(-24.24, 899.2) * mm, "end": v(-24.56, 898.8) * mm});
            skLineSegment(sketch, "E752", {"start": v(-24.56, 898.8) * mm, "end": v(-24.9, 898.41) * mm});
            skLineSegment(sketch, "E753", {"start": v(-24.9, 898.41) * mm, "end": v(-25.24, 898.03) * mm});
            skLineSegment(sketch, "E754", {"start": v(-25.24, 898.03) * mm, "end": v(-25.6, 897.65) * mm});
            skLineSegment(sketch, "E755", {"start": v(-25.6, 897.65) * mm, "end": v(-25.88, 897.36) * mm});
            skLineSegment(sketch, "E756", {"start": v(-25.88, 897.36) * mm, "end": v(-26.18, 897.08) * mm});
            skLineSegment(sketch, "E757", {"start": v(-26.18, 897.08) * mm, "end": v(-26.5, 896.8) * mm});
            skLineSegment(sketch, "E758", {"start": v(-26.5, 896.8) * mm, "end": v(-26.8, 896.54) * mm});
            skLineSegment(sketch, "E759", {"start": v(-26.8, 896.54) * mm, "end": v(-27.12, 896.28) * mm});
            skLineSegment(sketch, "E760", {"start": v(-27.12, 896.28) * mm, "end": v(-27.45, 896.03) * mm});
            skLineSegment(sketch, "E761", {"start": v(-27.45, 896.03) * mm, "end": v(-27.78, 895.79) * mm});
            skLineSegment(sketch, "E762", {"start": v(-27.78, 895.79) * mm, "end": v(-28.12, 895.56) * mm});
            skLineSegment(sketch, "E763", {"start": v(-28.12, 895.56) * mm, "end": v(-28.46, 895.33) * mm});
            skLineSegment(sketch, "E764", {"start": v(-28.46, 895.33) * mm, "end": v(-28.8, 895.12) * mm});
            skLineSegment(sketch, "E765", {"start": v(-28.8, 895.12) * mm, "end": v(-29.16, 894.91) * mm});
            skLineSegment(sketch, "E766", {"start": v(-29.16, 894.91) * mm, "end": v(-29.52, 894.71) * mm});
            skLineSegment(sketch, "E767", {"start": v(-29.52, 894.71) * mm, "end": v(-29.88, 894.53) * mm});
            skLineSegment(sketch, "E768", {"start": v(-29.88, 894.53) * mm, "end": v(-30.25, 894.35) * mm});
            skLineSegment(sketch, "E769", {"start": v(-30.25, 894.35) * mm, "end": v(-30.62, 894.18) * mm});
            skLineSegment(sketch, "E770", {"start": v(-30.62, 894.18) * mm, "end": v(-30.99, 894.01) * mm});
            skLineSegment(sketch, "E771", {"start": v(-30.99, 894.01) * mm, "end": v(-31.37, 893.86) * mm});
            skLineSegment(sketch, "E772", {"start": v(-31.37, 893.86) * mm, "end": v(-31.75, 893.72) * mm});
            skLineSegment(sketch, "E773", {"start": v(-31.75, 893.72) * mm, "end": v(-32.14, 893.59) * mm});
            skLineSegment(sketch, "E774", {"start": v(-32.14, 893.59) * mm, "end": v(-32.52, 893.46) * mm});
            skLineSegment(sketch, "E775", {"start": v(-32.52, 893.46) * mm, "end": v(-32.92, 893.35) * mm});
            skLineSegment(sketch, "E776", {"start": v(-32.92, 893.35) * mm, "end": v(-33.31, 893.25) * mm});
            skLineSegment(sketch, "E777", {"start": v(-33.31, 893.25) * mm, "end": v(-33.7, 893.15) * mm});
            skLineSegment(sketch, "E778", {"start": v(-33.7, 893.15) * mm, "end": v(-34.1, 893.07) * mm});
            skLineSegment(sketch, "E779", {"start": v(-34.1, 893.07) * mm, "end": v(-34.51, 893) * mm});
            skLineSegment(sketch, "E780", {"start": v(-34.51, 893) * mm, "end": v(-34.92, 892.93) * mm});
            skLineSegment(sketch, "E781", {"start": v(-34.92, 892.93) * mm, "end": v(-35.32, 892.87) * mm});
            skLineSegment(sketch, "E782", {"start": v(-35.32, 892.87) * mm, "end": v(-35.73, 892.83) * mm});
            skLineSegment(sketch, "E783", {"start": v(-35.73, 892.83) * mm, "end": v(-36.14, 892.8) * mm});
            skLineSegment(sketch, "E784", {"start": v(-36.14, 892.8) * mm, "end": v(-36.55, 892.77) * mm});
            skLineSegment(sketch, "E785", {"start": v(-36.55, 892.77) * mm, "end": v(-36.97, 892.76) * mm});
            skLineSegment(sketch, "E786", {"start": v(-36.97, 892.76) * mm, "end": v(-37.38, 892.76) * mm});
            skLineSegment(sketch, "E787", {"start": v(6.87, 892.76) * mm, "end": v(6.45, 892.75) * mm});
            skLineSegment(sketch, "E788", {"start": v(6.45, 892.75) * mm, "end": v(6.03, 892.76) * mm});
            skLineSegment(sketch, "E789", {"start": v(6.03, 892.76) * mm, "end": v(5.6, 892.78) * mm});
            skLineSegment(sketch, "E790", {"start": v(5.6, 892.78) * mm, "end": v(5.2, 892.8) * mm});
            skLineSegment(sketch, "E791", {"start": v(5.2, 892.8) * mm, "end": v(4.78, 892.84) * mm});
            skLineSegment(sketch, "E792", {"start": v(4.78, 892.84) * mm, "end": v(4.36, 892.9) * mm});
            skLineSegment(sketch, "E793", {"start": v(4.36, 892.9) * mm, "end": v(3.95, 892.95) * mm});
            skLineSegment(sketch, "E794", {"start": v(3.95, 892.95) * mm, "end": v(3.54, 893.02) * mm});
            skLineSegment(sketch, "E795", {"start": v(3.54, 893.02) * mm, "end": v(3.14, 893.1) * mm});
            skLineSegment(sketch, "E796", {"start": v(3.14, 893.1) * mm, "end": v(2.73, 893.2) * mm});
            skLineSegment(sketch, "E797", {"start": v(2.73, 893.2) * mm, "end": v(2.33, 893.3) * mm});
            skLineSegment(sketch, "E798", {"start": v(2.33, 893.3) * mm, "end": v(1.93, 893.4) * mm});
            skLineSegment(sketch, "E799", {"start": v(1.93, 893.4) * mm, "end": v(1.53, 893.52) * mm});
            skLineSegment(sketch, "E800", {"start": v(1.53, 893.52) * mm, "end": v(1.14, 893.65) * mm});
            skLineSegment(sketch, "E801", {"start": v(1.14, 893.65) * mm, "end": v(0.75, 893.79) * mm});
            skLineSegment(sketch, "E802", {"start": v(0.75, 893.79) * mm, "end": v(0.36, 893.94) * mm});
            skLineSegment(sketch, "E803", {"start": v(0.36, 893.94) * mm, "end": v(-0.02, 894.1) * mm});
            skLineSegment(sketch, "E804", {"start": v(-0.02, 894.1) * mm, "end": v(-0.4, 894.26) * mm});
            skLineSegment(sketch, "E805", {"start": v(-0.4, 894.26) * mm, "end": v(-0.77, 894.44) * mm});
            skLineSegment(sketch, "E806", {"start": v(-0.77, 894.44) * mm, "end": v(-1.14, 894.62) * mm});
            skLineSegment(sketch, "E807", {"start": v(-1.14, 894.62) * mm, "end": v(-1.5, 894.82) * mm});
            skLineSegment(sketch, "E808", {"start": v(-1.5, 894.82) * mm, "end": v(-1.87, 895.02) * mm});
            skLineSegment(sketch, "E809", {"start": v(-1.87, 895.02) * mm, "end": v(-2.22, 895.24) * mm});
            skLineSegment(sketch, "E810", {"start": v(-2.22, 895.24) * mm, "end": v(-2.57, 895.46) * mm});
            skLineSegment(sketch, "E811", {"start": v(-2.57, 895.46) * mm, "end": v(-2.92, 895.69) * mm});
            skLineSegment(sketch, "E812", {"start": v(-2.92, 895.69) * mm, "end": v(-3.26, 895.93) * mm});
            skLineSegment(sketch, "E813", {"start": v(-3.26, 895.93) * mm, "end": v(-3.6, 896.18) * mm});
            skLineSegment(sketch, "E814", {"start": v(-3.6, 896.18) * mm, "end": v(-3.92, 896.44) * mm});
            skLineSegment(sketch, "E815", {"start": v(-3.92, 896.44) * mm, "end": v(-4.24, 896.7) * mm});
            skLineSegment(sketch, "E816", {"start": v(-4.24, 896.7) * mm, "end": v(-4.56, 896.98) * mm});
            skLineSegment(sketch, "E817", {"start": v(-4.56, 896.98) * mm, "end": v(-4.87, 897.26) * mm});
            skLineSegment(sketch, "E818", {"start": v(-4.87, 897.26) * mm, "end": v(-5.17, 897.55) * mm});
            skLineSegment(sketch, "E819", {"start": v(-5.17, 897.55) * mm, "end": v(-5.52, 897.93) * mm});
            skLineSegment(sketch, "E820", {"start": v(-5.52, 897.93) * mm, "end": v(-5.86, 898.32) * mm});
            skLineSegment(sketch, "E821", {"start": v(-5.86, 898.32) * mm, "end": v(-6.19, 898.72) * mm});
            skLineSegment(sketch, "E822", {"start": v(-6.19, 898.72) * mm, "end": v(-6.5, 899.12) * mm});
            skLineSegment(sketch, "E823", {"start": v(-6.5, 899.12) * mm, "end": v(-6.81, 899.53) * mm});
            skLineSegment(sketch, "E824", {"start": v(-6.81, 899.53) * mm, "end": v(-7.11, 899.95) * mm});
            skLineSegment(sketch, "E825", {"start": v(-7.11, 899.95) * mm, "end": v(-7.4, 900.37) * mm});
            skLineSegment(sketch, "E826", {"start": v(-7.4, 900.37) * mm, "end": v(-7.67, 900.8) * mm});
            skLineSegment(sketch, "E827", {"start": v(-7.67, 900.8) * mm, "end": v(-7.94, 901.24) * mm});
            skLineSegment(sketch, "E828", {"start": v(-7.94, 901.24) * mm, "end": v(-8.2, 901.68) * mm});
            skLineSegment(sketch, "E829", {"start": v(-8.2, 901.68) * mm, "end": v(-8.43, 902.13) * mm});
            skLineSegment(sketch, "E830", {"start": v(-8.43, 902.13) * mm, "end": v(-8.67, 902.58) * mm});
            skLineSegment(sketch, "E831", {"start": v(-8.67, 902.58) * mm, "end": v(-8.89, 903.04) * mm});
            skLineSegment(sketch, "E832", {"start": v(-8.89, 903.04) * mm, "end": v(-9.1, 903.5) * mm});
            skLineSegment(sketch, "E833", {"start": v(-9.1, 903.5) * mm, "end": v(-9.3, 903.98) * mm});
            skLineSegment(sketch, "E834", {"start": v(-9.3, 903.98) * mm, "end": v(-9.48, 904.45) * mm});
            skLineSegment(sketch, "E835", {"start": v(-9.48, 904.45) * mm, "end": v(-9.65, 904.93) * mm});
            skLineSegment(sketch, "E836", {"start": v(-9.65, 904.93) * mm, "end": v(-9.81, 905.41) * mm});
            skLineSegment(sketch, "E837", {"start": v(-9.81, 905.41) * mm, "end": v(-9.96, 905.9) * mm});
            skLineSegment(sketch, "E838", {"start": v(-9.96, 905.9) * mm, "end": v(-10.1, 906.4) * mm});
            skLineSegment(sketch, "E839", {"start": v(-10.1, 906.4) * mm, "end": v(-10.23, 906.89) * mm});
            skLineSegment(sketch, "E840", {"start": v(-10.23, 906.89) * mm, "end": v(-10.34, 907.38) * mm});
            skLineSegment(sketch, "E841", {"start": v(-10.34, 907.38) * mm, "end": v(-10.44, 907.88) * mm});
            skLineSegment(sketch, "E842", {"start": v(-10.44, 907.88) * mm, "end": v(-10.53, 908.39) * mm});
            skLineSegment(sketch, "E843", {"start": v(-10.53, 908.39) * mm, "end": v(-10.6, 908.9) * mm});
            skLineSegment(sketch, "E844", {"start": v(-10.6, 908.9) * mm, "end": v(-10.67, 909.4) * mm});
            skLineSegment(sketch, "E845", {"start": v(-10.67, 909.4) * mm, "end": v(-10.73, 909.9) * mm});
            skLineSegment(sketch, "E846", {"start": v(-10.73, 909.9) * mm, "end": v(-10.77, 910.42) * mm});
            skLineSegment(sketch, "E847", {"start": v(-10.77, 910.42) * mm, "end": v(-10.8, 910.93) * mm});
            skLineSegment(sketch, "E848", {"start": v(-10.8, 910.93) * mm, "end": v(-10.8, 911.45) * mm});
            skLineSegment(sketch, "E849", {"start": v(-10.8, 911.45) * mm, "end": v(-10.8, 911.96) * mm});
            skLineSegment(sketch, "E850", {"start": v(-10.8, 911.96) * mm, "end": v(-10.8, 912.48) * mm});
            skLineSegment(sketch, "E851", {"start": v(-10.8, 912.48) * mm, "end": v(-10.81, 913.04) * mm});
            skLineSegment(sketch, "E852", {"start": v(-10.81, 913.04) * mm, "end": v(-10.81, 913.6) * mm});
            skLineSegment(sketch, "E853", {"start": v(-10.81, 913.6) * mm, "end": v(-10.8, 914.16) * mm});
            skLineSegment(sketch, "E854", {"start": v(-10.8, 914.16) * mm, "end": v(-10.77, 914.72) * mm});
            skLineSegment(sketch, "E855", {"start": v(-10.77, 914.72) * mm, "end": v(-10.73, 915.28) * mm});
            skLineSegment(sketch, "E856", {"start": v(-10.73, 915.28) * mm, "end": v(-10.68, 915.83) * mm});
            skLineSegment(sketch, "E857", {"start": v(-10.68, 915.83) * mm, "end": v(-10.61, 916.38) * mm});
            skLineSegment(sketch, "E858", {"start": v(-10.61, 916.38) * mm, "end": v(-10.53, 916.93) * mm});
            skLineSegment(sketch, "E859", {"start": v(-10.53, 916.93) * mm, "end": v(-10.43, 917.48) * mm});
            skLineSegment(sketch, "E860", {"start": v(-10.43, 917.48) * mm, "end": v(-10.32, 918.02) * mm});
            skLineSegment(sketch, "E861", {"start": v(-10.32, 918.02) * mm, "end": v(-10.2, 918.56) * mm});
            skLineSegment(sketch, "E862", {"start": v(-10.2, 918.56) * mm, "end": v(-10.07, 919.1) * mm});
            skLineSegment(sketch, "E863", {"start": v(-10.07, 919.1) * mm, "end": v(-9.92, 919.63) * mm});
            skLineSegment(sketch, "E864", {"start": v(-9.92, 919.63) * mm, "end": v(-9.76, 920.16) * mm});
            skLineSegment(sketch, "E865", {"start": v(-9.76, 920.16) * mm, "end": v(-9.58, 920.68) * mm});
            skLineSegment(sketch, "E866", {"start": v(-9.58, 920.68) * mm, "end": v(-9.4, 921.2) * mm});
            skLineSegment(sketch, "E867", {"start": v(-9.4, 921.2) * mm, "end": v(-9.2, 921.72) * mm});
            skLineSegment(sketch, "E868", {"start": v(-9.2, 921.72) * mm, "end": v(-8.98, 922.23) * mm});
            skLineSegment(sketch, "E869", {"start": v(-8.98, 922.23) * mm, "end": v(-8.75, 922.73) * mm});
            skLineSegment(sketch, "E870", {"start": v(-8.75, 922.73) * mm, "end": v(-8.51, 923.23) * mm});
            skLineSegment(sketch, "E871", {"start": v(-8.51, 923.23) * mm, "end": v(-8.26, 923.72) * mm});
            skLineSegment(sketch, "E872", {"start": v(-8.26, 923.72) * mm, "end": v(-8, 924.21) * mm});
            skLineSegment(sketch, "E873", {"start": v(-8, 924.21) * mm, "end": v(-7.72, 924.7) * mm});
            skLineSegment(sketch, "E874", {"start": v(-7.72, 924.7) * mm, "end": v(-7.43, 925.17) * mm});
            skLineSegment(sketch, "E875", {"start": v(-7.43, 925.17) * mm, "end": v(-7.13, 925.63) * mm});
            skLineSegment(sketch, "E876", {"start": v(-7.13, 925.63) * mm, "end": v(-6.82, 926.1) * mm});
            skLineSegment(sketch, "E877", {"start": v(-6.82, 926.1) * mm, "end": v(-6.5, 926.55) * mm});
            skLineSegment(sketch, "E878", {"start": v(-6.5, 926.55) * mm, "end": v(-6.16, 927) * mm});
            skLineSegment(sketch, "E879", {"start": v(-6.16, 927) * mm, "end": v(-5.82, 927.43) * mm});
            skLineSegment(sketch, "E880", {"start": v(-5.82, 927.43) * mm, "end": v(-5.46, 927.86) * mm});
            skLineSegment(sketch, "E881", {"start": v(-5.46, 927.86) * mm, "end": v(-5.09, 928.28) * mm});
            skLineSegment(sketch, "E882", {"start": v(-5.09, 928.28) * mm, "end": v(-4.7, 928.69) * mm});
            skLineSegment(sketch, "E883", {"start": v(-4.7, 928.69) * mm, "end": v(-4.42, 928.98) * mm});
            skLineSegment(sketch, "E884", {"start": v(-4.42, 928.98) * mm, "end": v(-4.13, 929.26) * mm});
            skLineSegment(sketch, "E885", {"start": v(-4.13, 929.26) * mm, "end": v(-3.83, 929.54) * mm});
            skLineSegment(sketch, "E886", {"start": v(-3.83, 929.54) * mm, "end": v(-3.52, 929.8) * mm});
            skLineSegment(sketch, "E887", {"start": v(-3.52, 929.8) * mm, "end": v(-3.2, 930.06) * mm});
            skLineSegment(sketch, "E888", {"start": v(-3.2, 930.06) * mm, "end": v(-2.9, 930.3) * mm});
            skLineSegment(sketch, "E889", {"start": v(-2.9, 930.3) * mm, "end": v(-2.57, 930.55) * mm});
            skLineSegment(sketch, "E890", {"start": v(-2.57, 930.55) * mm, "end": v(-2.24, 930.78) * mm});
            skLineSegment(sketch, "E891", {"start": v(-2.24, 930.78) * mm, "end": v(-1.9, 931) * mm});
            skLineSegment(sketch, "E892", {"start": v(-1.9, 931) * mm, "end": v(-1.56, 931.22) * mm});
            skLineSegment(sketch, "E893", {"start": v(-1.56, 931.22) * mm, "end": v(-1.22, 931.42) * mm});
            skLineSegment(sketch, "E894", {"start": v(-1.22, 931.42) * mm, "end": v(-0.87, 931.62) * mm});
            skLineSegment(sketch, "E895", {"start": v(-0.87, 931.62) * mm, "end": v(-0.51, 931.8) * mm});
            skLineSegment(sketch, "E896", {"start": v(-0.51, 931.8) * mm, "end": v(-0.15, 931.98) * mm});
            skLineSegment(sketch, "E897", {"start": v(-0.15, 931.98) * mm, "end": v(0.21, 932.15) * mm});
            skLineSegment(sketch, "E898", {"start": v(0.21, 932.15) * mm, "end": v(0.58, 932.3) * mm});
            skLineSegment(sketch, "E899", {"start": v(0.58, 932.3) * mm, "end": v(0.95, 932.46) * mm});
            skLineSegment(sketch, "E900", {"start": v(0.95, 932.46) * mm, "end": v(1.33, 932.6) * mm});
            skLineSegment(sketch, "E901", {"start": v(1.33, 932.6) * mm, "end": v(1.7, 932.73) * mm});
            skLineSegment(sketch, "E902", {"start": v(1.7, 932.73) * mm, "end": v(2.1, 932.85) * mm});
            skLineSegment(sketch, "E903", {"start": v(2.1, 932.85) * mm, "end": v(2.48, 932.96) * mm});
            skLineSegment(sketch, "E904", {"start": v(2.48, 932.96) * mm, "end": v(2.87, 933.06) * mm});
            skLineSegment(sketch, "E905", {"start": v(2.87, 933.06) * mm, "end": v(3.26, 933.15) * mm});
            skLineSegment(sketch, "E906", {"start": v(3.26, 933.15) * mm, "end": v(3.65, 933.24) * mm});
            skLineSegment(sketch, "E907", {"start": v(3.65, 933.24) * mm, "end": v(4.05, 933.3) * mm});
            skLineSegment(sketch, "E908", {"start": v(4.05, 933.3) * mm, "end": v(4.45, 933.37) * mm});
            skLineSegment(sketch, "E909", {"start": v(4.45, 933.37) * mm, "end": v(4.85, 933.42) * mm});
            skLineSegment(sketch, "E910", {"start": v(4.85, 933.42) * mm, "end": v(5.25, 933.46) * mm});
            skLineSegment(sketch, "E911", {"start": v(5.25, 933.46) * mm, "end": v(5.65, 933.49) * mm});
            skLineSegment(sketch, "E912", {"start": v(5.65, 933.49) * mm, "end": v(6.06, 933.5) * mm});
            skLineSegment(sketch, "E913", {"start": v(6.06, 933.5) * mm, "end": v(6.47, 933.52) * mm});
            skLineSegment(sketch, "E914", {"start": v(6.47, 933.52) * mm, "end": v(6.87, 933.52) * mm});
            skLineSegment(sketch, "E915", {"start": v(6.87, 933.52) * mm, "end": v(7.29, 933.51) * mm});
            skLineSegment(sketch, "E916", {"start": v(7.29, 933.51) * mm, "end": v(7.7, 933.5) * mm});
            skLineSegment(sketch, "E917", {"start": v(7.7, 933.5) * mm, "end": v(8.11, 933.47) * mm});
            skLineSegment(sketch, "E918", {"start": v(8.11, 933.47) * mm, "end": v(8.52, 933.44) * mm});
            skLineSegment(sketch, "E919", {"start": v(8.52, 933.44) * mm, "end": v(8.93, 933.4) * mm});
            skLineSegment(sketch, "E920", {"start": v(8.93, 933.4) * mm, "end": v(9.34, 933.33) * mm});
            skLineSegment(sketch, "E921", {"start": v(9.34, 933.33) * mm, "end": v(9.74, 933.27) * mm});
            skLineSegment(sketch, "E922", {"start": v(9.74, 933.27) * mm, "end": v(10.14, 933.19) * mm});
            skLineSegment(sketch, "E923", {"start": v(10.14, 933.19) * mm, "end": v(10.54, 933.1) * mm});
            skLineSegment(sketch, "E924", {"start": v(10.54, 933.1) * mm, "end": v(10.94, 933) * mm});
            skLineSegment(sketch, "E925", {"start": v(10.94, 933) * mm, "end": v(11.34, 932.9) * mm});
            skLineSegment(sketch, "E926", {"start": v(11.34, 932.9) * mm, "end": v(11.73, 932.78) * mm});
            skLineSegment(sketch, "E927", {"start": v(11.73, 932.78) * mm, "end": v(12.11, 932.65) * mm});
            skLineSegment(sketch, "E928", {"start": v(12.11, 932.65) * mm, "end": v(12.5, 932.51) * mm});
            skLineSegment(sketch, "E929", {"start": v(12.5, 932.51) * mm, "end": v(12.88, 932.37) * mm});
            skLineSegment(sketch, "E930", {"start": v(12.88, 932.37) * mm, "end": v(13.25, 932.2) * mm});
            skLineSegment(sketch, "E931", {"start": v(13.25, 932.2) * mm, "end": v(13.63, 932.04) * mm});
            skLineSegment(sketch, "E932", {"start": v(13.63, 932.04) * mm, "end": v(14, 931.87) * mm});
            skLineSegment(sketch, "E933", {"start": v(14, 931.87) * mm, "end": v(14.36, 931.68) * mm});
            skLineSegment(sketch, "E934", {"start": v(14.36, 931.68) * mm, "end": v(14.72, 931.49) * mm});
            skLineSegment(sketch, "E935", {"start": v(14.72, 931.49) * mm, "end": v(15.07, 931.29) * mm});
            skLineSegment(sketch, "E936", {"start": v(15.07, 931.29) * mm, "end": v(15.42, 931.07) * mm});
            skLineSegment(sketch, "E937", {"start": v(15.42, 931.07) * mm, "end": v(15.76, 930.85) * mm});
            skLineSegment(sketch, "E938", {"start": v(15.76, 930.85) * mm, "end": v(16.1, 930.62) * mm});
            skLineSegment(sketch, "E939", {"start": v(16.1, 930.62) * mm, "end": v(16.43, 930.38) * mm});
            skLineSegment(sketch, "E940", {"start": v(16.43, 930.38) * mm, "end": v(16.76, 930.13) * mm});
            skLineSegment(sketch, "E941", {"start": v(16.76, 930.13) * mm, "end": v(17.08, 929.88) * mm});
            skLineSegment(sketch, "E942", {"start": v(17.08, 929.88) * mm, "end": v(17.4, 929.61) * mm});
            skLineSegment(sketch, "E943", {"start": v(17.4, 929.61) * mm, "end": v(17.7, 929.34) * mm});
            skLineSegment(sketch, "E944", {"start": v(17.7, 929.34) * mm, "end": v(18, 929.05) * mm});
            skLineSegment(sketch, "E945", {"start": v(18, 929.05) * mm, "end": v(18.3, 928.76) * mm});
            skLineSegment(sketch, "E946", {"start": v(18.3, 928.76) * mm, "end": v(18.58, 928.47) * mm});
            skLineSegment(sketch, "E947", {"start": v(18.58, 928.47) * mm, "end": v(18.95, 928.06) * mm});
            skLineSegment(sketch, "E948", {"start": v(18.95, 928.06) * mm, "end": v(19.31, 927.64) * mm});
            skLineSegment(sketch, "E949", {"start": v(19.31, 927.64) * mm, "end": v(19.66, 927.21) * mm});
            skLineSegment(sketch, "E950", {"start": v(19.66, 927.21) * mm, "end": v(20, 926.78) * mm});
            skLineSegment(sketch, "E951", {"start": v(20, 926.78) * mm, "end": v(20.32, 926.34) * mm});
            skLineSegment(sketch, "E952", {"start": v(20.32, 926.34) * mm, "end": v(20.63, 925.89) * mm});
            skLineSegment(sketch, "E953", {"start": v(20.63, 925.89) * mm, "end": v(20.94, 925.43) * mm});
            skLineSegment(sketch, "E954", {"start": v(20.94, 925.43) * mm, "end": v(21.23, 924.97) * mm});
            skLineSegment(sketch, "E955", {"start": v(21.23, 924.97) * mm, "end": v(21.5, 924.5) * mm});
            skLineSegment(sketch, "E956", {"start": v(21.5, 924.5) * mm, "end": v(21.77, 924.02) * mm});
            skLineSegment(sketch, "E957", {"start": v(21.77, 924.02) * mm, "end": v(22.02, 923.54) * mm});
            skLineSegment(sketch, "E958", {"start": v(22.02, 923.54) * mm, "end": v(22.27, 923.05) * mm});
            skLineSegment(sketch, "E959", {"start": v(22.27, 923.05) * mm, "end": v(22.5, 922.56) * mm});
            skLineSegment(sketch, "E960", {"start": v(22.5, 922.56) * mm, "end": v(22.71, 922.06) * mm});
            skLineSegment(sketch, "E961", {"start": v(22.71, 922.06) * mm, "end": v(22.92, 921.56) * mm});
            skLineSegment(sketch, "E962", {"start": v(22.92, 921.56) * mm, "end": v(23.11, 921.05) * mm});
            skLineSegment(sketch, "E963", {"start": v(23.11, 921.05) * mm, "end": v(23.3, 920.54) * mm});
            skLineSegment(sketch, "E964", {"start": v(23.3, 920.54) * mm, "end": v(23.46, 920.02) * mm});
            skLineSegment(sketch, "E965", {"start": v(23.46, 920.02) * mm, "end": v(23.61, 919.5) * mm});
            skLineSegment(sketch, "E966", {"start": v(23.61, 919.5) * mm, "end": v(23.75, 918.97) * mm});
            skLineSegment(sketch, "E967", {"start": v(23.75, 918.97) * mm, "end": v(23.88, 918.44) * mm});
            skLineSegment(sketch, "E968", {"start": v(23.88, 918.44) * mm, "end": v(24, 917.9) * mm});
            skLineSegment(sketch, "E969", {"start": v(24, 917.9) * mm, "end": v(24.1, 917.37) * mm});
            skLineSegment(sketch, "E970", {"start": v(24.1, 917.37) * mm, "end": v(24.2, 916.83) * mm});
            skLineSegment(sketch, "E971", {"start": v(24.2, 916.83) * mm, "end": v(24.27, 916.3) * mm});
            skLineSegment(sketch, "E972", {"start": v(24.27, 916.3) * mm, "end": v(24.33, 915.75) * mm});
            skLineSegment(sketch, "E973", {"start": v(24.33, 915.75) * mm, "end": v(24.38, 915.2) * mm});
            skLineSegment(sketch, "E974", {"start": v(24.38, 915.2) * mm, "end": v(24.41, 914.66) * mm});
            skLineSegment(sketch, "E975", {"start": v(24.41, 914.66) * mm, "end": v(24.44, 914.1) * mm});
            skLineSegment(sketch, "E976", {"start": v(24.44, 914.1) * mm, "end": v(24.44, 913.56) * mm});
            skLineSegment(sketch, "E977", {"start": v(24.44, 913.56) * mm, "end": v(24.44, 913) * mm});
            skLineSegment(sketch, "E978", {"start": v(24.44, 913) * mm, "end": v(24.42, 912.46) * mm});
            skLineSegment(sketch, "E979", {"start": v(24.42, 912.46) * mm, "end": v(24.43, 911.94) * mm});
            skLineSegment(sketch, "E980", {"start": v(24.43, 911.94) * mm, "end": v(24.42, 911.43) * mm});
            skLineSegment(sketch, "E981", {"start": v(24.42, 911.43) * mm, "end": v(24.4, 910.92) * mm});
            skLineSegment(sketch, "E982", {"start": v(24.4, 910.92) * mm, "end": v(24.37, 910.4) * mm});
            skLineSegment(sketch, "E983", {"start": v(24.37, 910.4) * mm, "end": v(24.33, 909.9) * mm});
            skLineSegment(sketch, "E984", {"start": v(24.33, 909.9) * mm, "end": v(24.27, 909.39) * mm});
            skLineSegment(sketch, "E985", {"start": v(24.27, 909.39) * mm, "end": v(24.2, 908.88) * mm});
            skLineSegment(sketch, "E986", {"start": v(24.2, 908.88) * mm, "end": v(24.12, 908.38) * mm});
            skLineSegment(sketch, "E987", {"start": v(24.12, 908.38) * mm, "end": v(24.03, 907.88) * mm});
            skLineSegment(sketch, "E988", {"start": v(24.03, 907.88) * mm, "end": v(23.92, 907.38) * mm});
            skLineSegment(sketch, "E989", {"start": v(23.92, 907.38) * mm, "end": v(23.8, 906.89) * mm});
            skLineSegment(sketch, "E990", {"start": v(23.8, 906.89) * mm, "end": v(23.68, 906.4) * mm});
            skLineSegment(sketch, "E991", {"start": v(23.68, 906.4) * mm, "end": v(23.53, 905.91) * mm});
            skLineSegment(sketch, "E992", {"start": v(23.53, 905.91) * mm, "end": v(23.38, 905.43) * mm});
            skLineSegment(sketch, "E993", {"start": v(23.38, 905.43) * mm, "end": v(23.21, 904.95) * mm});
            skLineSegment(sketch, "E994", {"start": v(23.21, 904.95) * mm, "end": v(23.03, 904.47) * mm});
            skLineSegment(sketch, "E995", {"start": v(23.03, 904.47) * mm, "end": v(22.84, 904) * mm});
            skLineSegment(sketch, "E996", {"start": v(22.84, 904) * mm, "end": v(22.64, 903.54) * mm});
            skLineSegment(sketch, "E997", {"start": v(22.64, 903.54) * mm, "end": v(22.43, 903.08) * mm});
            skLineSegment(sketch, "E998", {"start": v(22.43, 903.08) * mm, "end": v(22.2, 902.62) * mm});
            skLineSegment(sketch, "E999", {"start": v(22.2, 902.62) * mm, "end": v(21.97, 902.17) * mm});
            skLineSegment(sketch, "E1000", {"start": v(21.97, 902.17) * mm, "end": v(21.72, 901.73) * mm});
            skLineSegment(sketch, "E1001", {"start": v(21.72, 901.73) * mm, "end": v(21.46, 901.29) * mm});
            skLineSegment(sketch, "E1002", {"start": v(21.46, 901.29) * mm, "end": v(21.2, 900.86) * mm});
            skLineSegment(sketch, "E1003", {"start": v(21.2, 900.86) * mm, "end": v(20.92, 900.43) * mm});
            skLineSegment(sketch, "E1004", {"start": v(20.92, 900.43) * mm, "end": v(20.62, 900.01) * mm});
            skLineSegment(sketch, "E1005", {"start": v(20.62, 900.01) * mm, "end": v(20.32, 899.6) * mm});
            skLineSegment(sketch, "E1006", {"start": v(20.32, 899.6) * mm, "end": v(20.01, 899.2) * mm});
            skLineSegment(sketch, "E1007", {"start": v(20.01, 899.2) * mm, "end": v(19.69, 898.8) * mm});
            skLineSegment(sketch, "E1008", {"start": v(19.69, 898.8) * mm, "end": v(19.35, 898.41) * mm});
            skLineSegment(sketch, "E1009", {"start": v(19.35, 898.41) * mm, "end": v(19, 898.03) * mm});
            skLineSegment(sketch, "E1010", {"start": v(19, 898.03) * mm, "end": v(18.66, 897.65) * mm});
            skLineSegment(sketch, "E1011", {"start": v(18.66, 897.65) * mm, "end": v(18.36, 897.36) * mm});
            skLineSegment(sketch, "E1012", {"start": v(18.36, 897.36) * mm, "end": v(18.06, 897.08) * mm});
            skLineSegment(sketch, "E1013", {"start": v(18.06, 897.08) * mm, "end": v(17.75, 896.8) * mm});
            skLineSegment(sketch, "E1014", {"start": v(17.75, 896.8) * mm, "end": v(17.44, 896.54) * mm});
            skLineSegment(sketch, "E1015", {"start": v(17.44, 896.54) * mm, "end": v(17.12, 896.28) * mm});
            skLineSegment(sketch, "E1016", {"start": v(17.12, 896.28) * mm, "end": v(16.8, 896.03) * mm});
            skLineSegment(sketch, "E1017", {"start": v(16.8, 896.03) * mm, "end": v(16.46, 895.79) * mm});
            skLineSegment(sketch, "E1018", {"start": v(16.46, 895.79) * mm, "end": v(16.13, 895.56) * mm});
            skLineSegment(sketch, "E1019", {"start": v(16.13, 895.56) * mm, "end": v(15.78, 895.33) * mm});
            skLineSegment(sketch, "E1020", {"start": v(15.78, 895.33) * mm, "end": v(15.44, 895.12) * mm});
            skLineSegment(sketch, "E1021", {"start": v(15.44, 895.12) * mm, "end": v(15.09, 894.91) * mm});
            skLineSegment(sketch, "E1022", {"start": v(15.09, 894.91) * mm, "end": v(14.73, 894.71) * mm});
            skLineSegment(sketch, "E1023", {"start": v(14.73, 894.71) * mm, "end": v(14.37, 894.53) * mm});
            skLineSegment(sketch, "E1024", {"start": v(14.37, 894.53) * mm, "end": v(14, 894.35) * mm});
            skLineSegment(sketch, "E1025", {"start": v(14, 894.35) * mm, "end": v(13.63, 894.18) * mm});
            skLineSegment(sketch, "E1026", {"start": v(13.63, 894.18) * mm, "end": v(13.26, 894.01) * mm});
            skLineSegment(sketch, "E1027", {"start": v(13.26, 894.01) * mm, "end": v(12.88, 893.86) * mm});
            skLineSegment(sketch, "E1028", {"start": v(12.88, 893.86) * mm, "end": v(12.5, 893.72) * mm});
            skLineSegment(sketch, "E1029", {"start": v(12.5, 893.72) * mm, "end": v(12.1, 893.59) * mm});
            skLineSegment(sketch, "E1030", {"start": v(12.1, 893.59) * mm, "end": v(11.72, 893.46) * mm});
            skLineSegment(sketch, "E1031", {"start": v(11.72, 893.46) * mm, "end": v(11.33, 893.35) * mm});
            skLineSegment(sketch, "E1032", {"start": v(11.33, 893.35) * mm, "end": v(10.93, 893.25) * mm});
            skLineSegment(sketch, "E1033", {"start": v(10.93, 893.25) * mm, "end": v(10.54, 893.15) * mm});
            skLineSegment(sketch, "E1034", {"start": v(10.54, 893.15) * mm, "end": v(10.14, 893.07) * mm});
            skLineSegment(sketch, "E1035", {"start": v(10.14, 893.07) * mm, "end": v(9.73, 893) * mm});
            skLineSegment(sketch, "E1036", {"start": v(9.73, 893) * mm, "end": v(9.33, 892.93) * mm});
            skLineSegment(sketch, "E1037", {"start": v(9.33, 892.93) * mm, "end": v(8.92, 892.87) * mm});
            skLineSegment(sketch, "E1038", {"start": v(8.92, 892.87) * mm, "end": v(8.51, 892.83) * mm});
            skLineSegment(sketch, "E1039", {"start": v(8.51, 892.83) * mm, "end": v(8.1, 892.8) * mm});
            skLineSegment(sketch, "E1040", {"start": v(8.1, 892.8) * mm, "end": v(7.7, 892.77) * mm});
            skLineSegment(sketch, "E1041", {"start": v(7.7, 892.77) * mm, "end": v(7.28, 892.76) * mm});
            skLineSegment(sketch, "E1042", {"start": v(7.28, 892.76) * mm, "end": v(6.87, 892.76) * mm});
            skLineSegment(sketch, "E1043", {"start": v(33.44, 893.32) * mm, "end": v(33.44, 933.28) * mm});
            skLineSegment(sketch, "E1044", {"start": v(33.44, 933.28) * mm, "end": v(51, 933.28) * mm});
            skLineSegment(sketch, "E1045", {"start": v(51, 933.28) * mm, "end": v(51.5, 933.27) * mm});
            skLineSegment(sketch, "E1046", {"start": v(51.5, 933.27) * mm, "end": v(51.98, 933.24) * mm});
            skLineSegment(sketch, "E1047", {"start": v(51.98, 933.24) * mm, "end": v(52.47, 933.19) * mm});
            skLineSegment(sketch, "E1048", {"start": v(52.47, 933.19) * mm, "end": v(52.96, 933.11) * mm});
            skLineSegment(sketch, "E1049", {"start": v(52.96, 933.11) * mm, "end": v(53.43, 933) * mm});
            skLineSegment(sketch, "E1050", {"start": v(53.43, 933) * mm, "end": v(53.9, 932.88) * mm});
            skLineSegment(sketch, "E1051", {"start": v(53.9, 932.88) * mm, "end": v(54.37, 932.73) * mm});
            skLineSegment(sketch, "E1052", {"start": v(54.37, 932.73) * mm, "end": v(54.82, 932.56) * mm});
            skLineSegment(sketch, "E1053", {"start": v(54.82, 932.56) * mm, "end": v(55.27, 932.36) * mm});
            skLineSegment(sketch, "E1054", {"start": v(55.27, 932.36) * mm, "end": v(55.7, 932.14) * mm});
            skLineSegment(sketch, "E1055", {"start": v(55.7, 932.14) * mm, "end": v(56.13, 931.9) * mm});
            skLineSegment(sketch, "E1056", {"start": v(56.13, 931.9) * mm, "end": v(56.54, 931.64) * mm});
            skLineSegment(sketch, "E1057", {"start": v(56.54, 931.64) * mm, "end": v(56.93, 931.35) * mm});
            skLineSegment(sketch, "E1058", {"start": v(56.93, 931.35) * mm, "end": v(57.32, 931.05) * mm});
            skLineSegment(sketch, "E1059", {"start": v(57.32, 931.05) * mm, "end": v(57.69, 930.72) * mm});
            skLineSegment(sketch, "E1060", {"start": v(57.69, 930.72) * mm, "end": v(58.04, 930.37) * mm});
            skLineSegment(sketch, "E1061", {"start": v(58.04, 930.37) * mm, "end": v(58.38, 930.02) * mm});
            skLineSegment(sketch, "E1062", {"start": v(58.38, 930.02) * mm, "end": v(58.7, 929.66) * mm});
            skLineSegment(sketch, "E1063", {"start": v(58.7, 929.66) * mm, "end": v(59, 929.27) * mm});
            skLineSegment(sketch, "E1064", {"start": v(59, 929.27) * mm, "end": v(59.29, 928.88) * mm});
            skLineSegment(sketch, "E1065", {"start": v(59.29, 928.88) * mm, "end": v(59.55, 928.47) * mm});
            skLineSegment(sketch, "E1066", {"start": v(59.55, 928.47) * mm, "end": v(59.79, 928.05) * mm});
            skLineSegment(sketch, "E1067", {"start": v(59.79, 928.05) * mm, "end": v(60, 927.62) * mm});
            skLineSegment(sketch, "E1068", {"start": v(60, 927.62) * mm, "end": v(60.2, 927.18) * mm});
            skLineSegment(sketch, "E1069", {"start": v(60.2, 927.18) * mm, "end": v(60.38, 926.73) * mm});
            skLineSegment(sketch, "E1070", {"start": v(60.38, 926.73) * mm, "end": v(60.53, 926.27) * mm});
            skLineSegment(sketch, "E1071", {"start": v(60.53, 926.27) * mm, "end": v(60.66, 925.8) * mm});
            skLineSegment(sketch, "E1072", {"start": v(60.66, 925.8) * mm, "end": v(60.77, 925.33) * mm});
            skLineSegment(sketch, "E1073", {"start": v(60.77, 925.33) * mm, "end": v(60.85, 924.86) * mm});
            skLineSegment(sketch, "E1074", {"start": v(60.85, 924.86) * mm, "end": v(60.91, 924.37) * mm});
            skLineSegment(sketch, "E1075", {"start": v(60.91, 924.37) * mm, "end": v(60.95, 923.89) * mm});
            skLineSegment(sketch, "E1076", {"start": v(60.95, 923.89) * mm, "end": v(60.96, 923.4) * mm});
            skLineSegment(sketch, "E1077", {"start": v(60.96, 923.4) * mm, "end": v(60.96, 922.9) * mm});
            skLineSegment(sketch, "E1078", {"start": v(60.96, 922.9) * mm, "end": v(60.94, 922.4) * mm});
            skLineSegment(sketch, "E1079", {"start": v(60.94, 922.4) * mm, "end": v(60.9, 921.9) * mm});
            skLineSegment(sketch, "E1080", {"start": v(60.9, 921.9) * mm, "end": v(60.82, 921.41) * mm});
            skLineSegment(sketch, "E1081", {"start": v(60.82, 921.41) * mm, "end": v(60.72, 920.93) * mm});
            skLineSegment(sketch, "E1082", {"start": v(60.72, 920.93) * mm, "end": v(60.6, 920.45) * mm});
            skLineSegment(sketch, "E1083", {"start": v(60.6, 920.45) * mm, "end": v(60.45, 919.97) * mm});
            skLineSegment(sketch, "E1084", {"start": v(60.45, 919.97) * mm, "end": v(60.28, 919.5) * mm});
            skLineSegment(sketch, "E1085", {"start": v(60.28, 919.5) * mm, "end": v(60.09, 919.05) * mm});
            skLineSegment(sketch, "E1086", {"start": v(60.09, 919.05) * mm, "end": v(59.87, 918.6) * mm});
            skLineSegment(sketch, "E1087", {"start": v(59.87, 918.6) * mm, "end": v(59.63, 918.18) * mm});
            skLineSegment(sketch, "E1088", {"start": v(59.63, 918.18) * mm, "end": v(59.37, 917.75) * mm});
            skLineSegment(sketch, "E1089", {"start": v(59.37, 917.75) * mm, "end": v(59.1, 917.34) * mm});
            skLineSegment(sketch, "E1090", {"start": v(59.1, 917.34) * mm, "end": v(58.79, 916.95) * mm});
            skLineSegment(sketch, "E1091", {"start": v(58.79, 916.95) * mm, "end": v(58.47, 916.57) * mm});
            skLineSegment(sketch, "E1092", {"start": v(58.47, 916.57) * mm, "end": v(58.12, 916.2) * mm});
            skLineSegment(sketch, "E1093", {"start": v(58.12, 916.2) * mm, "end": v(57.76, 915.86) * mm});
            skLineSegment(sketch, "E1094", {"start": v(57.76, 915.86) * mm, "end": v(57.39, 915.54) * mm});
            skLineSegment(sketch, "E1095", {"start": v(57.39, 915.54) * mm, "end": v(57, 915.23) * mm});
            skLineSegment(sketch, "E1096", {"start": v(57, 915.23) * mm, "end": v(56.6, 914.95) * mm});
            skLineSegment(sketch, "E1097", {"start": v(56.6, 914.95) * mm, "end": v(56.17, 914.69) * mm});
            skLineSegment(sketch, "E1098", {"start": v(56.17, 914.69) * mm, "end": v(55.74, 914.45) * mm});
            skLineSegment(sketch, "E1099", {"start": v(55.74, 914.45) * mm, "end": v(55.3, 914.23) * mm});
            skLineSegment(sketch, "E1100", {"start": v(55.3, 914.23) * mm, "end": v(54.85, 914.03) * mm});
            skLineSegment(sketch, "E1101", {"start": v(54.85, 914.03) * mm, "end": v(54.4, 913.86) * mm});
            skLineSegment(sketch, "E1102", {"start": v(54.4, 913.86) * mm, "end": v(53.93, 913.7) * mm});
            skLineSegment(sketch, "E1103", {"start": v(53.93, 913.7) * mm, "end": v(53.45, 913.58) * mm});
            skLineSegment(sketch, "E1104", {"start": v(53.45, 913.58) * mm, "end": v(52.97, 913.48) * mm});
            skLineSegment(sketch, "E1105", {"start": v(52.97, 913.48) * mm, "end": v(52.48, 913.4) * mm});
            skLineSegment(sketch, "E1106", {"start": v(52.48, 913.4) * mm, "end": v(52, 913.34) * mm});
            skLineSegment(sketch, "E1107", {"start": v(52, 913.34) * mm, "end": v(51.5, 913.31) * mm});
            skLineSegment(sketch, "E1108", {"start": v(51.5, 913.31) * mm, "end": v(51, 913.3) * mm});
            skLineSegment(sketch, "E1109", {"start": v(51, 913.3) * mm, "end": v(33.44, 913.3) * mm});
            skLineSegment(sketch, "E1110", {"start": v(51, 913.3) * mm, "end": v(51.4, 913.3) * mm});
            skLineSegment(sketch, "E1111", {"start": v(51.4, 913.3) * mm, "end": v(51.82, 913.28) * mm});
            skLineSegment(sketch, "E1112", {"start": v(51.82, 913.28) * mm, "end": v(52.22, 913.24) * mm});
            skLineSegment(sketch, "E1113", {"start": v(52.22, 913.24) * mm, "end": v(52.62, 913.17) * mm});
            skLineSegment(sketch, "E1114", {"start": v(52.62, 913.17) * mm, "end": v(53.02, 913.09) * mm});
            skLineSegment(sketch, "E1115", {"start": v(53.02, 913.09) * mm, "end": v(53.4, 912.98) * mm});
            skLineSegment(sketch, "E1116", {"start": v(53.4, 912.98) * mm, "end": v(53.8, 912.86) * mm});
            skLineSegment(sketch, "E1117", {"start": v(53.8, 912.86) * mm, "end": v(54.17, 912.72) * mm});
            skLineSegment(sketch, "E1118", {"start": v(54.17, 912.72) * mm, "end": v(54.54, 912.56) * mm});
            skLineSegment(sketch, "E1119", {"start": v(54.54, 912.56) * mm, "end": v(54.9, 912.38) * mm});
            skLineSegment(sketch, "E1120", {"start": v(54.9, 912.38) * mm, "end": v(55.25, 912.18) * mm});
            skLineSegment(sketch, "E1121", {"start": v(55.25, 912.18) * mm, "end": v(55.6, 911.96) * mm});
            skLineSegment(sketch, "E1122", {"start": v(55.6, 911.96) * mm, "end": v(55.93, 911.73) * mm});
            skLineSegment(sketch, "E1123", {"start": v(55.93, 911.73) * mm, "end": v(56.25, 911.48) * mm});
            skLineSegment(sketch, "E1124", {"start": v(56.25, 911.48) * mm, "end": v(56.56, 911.2) * mm});
            skLineSegment(sketch, "E1125", {"start": v(56.56, 911.2) * mm, "end": v(56.85, 910.92) * mm});
            skLineSegment(sketch, "E1126", {"start": v(56.85, 910.92) * mm, "end": v(57.2, 910.42) * mm});
            skLineSegment(sketch, "E1127", {"start": v(57.2, 910.42) * mm, "end": v(57.5, 909.9) * mm});
            skLineSegment(sketch, "E1128", {"start": v(57.5, 909.9) * mm, "end": v(57.8, 909.38) * mm});
            skLineSegment(sketch, "E1129", {"start": v(57.8, 909.38) * mm, "end": v(58.07, 908.85) * mm});
            skLineSegment(sketch, "E1130", {"start": v(58.07, 908.85) * mm, "end": v(58.31, 908.3) * mm});
            skLineSegment(sketch, "E1131", {"start": v(58.31, 908.3) * mm, "end": v(58.53, 907.74) * mm});
            skLineSegment(sketch, "E1132", {"start": v(58.53, 907.74) * mm, "end": v(58.73, 907.17) * mm});
            skLineSegment(sketch, "E1133", {"start": v(58.73, 907.17) * mm, "end": v(58.9, 906.6) * mm});
            skLineSegment(sketch, "E1134", {"start": v(58.9, 906.6) * mm, "end": v(59.04, 906.02) * mm});
            skLineSegment(sketch, "E1135", {"start": v(59.04, 906.02) * mm, "end": v(59.16, 905.43) * mm});
            skLineSegment(sketch, "E1136", {"start": v(59.16, 905.43) * mm, "end": v(59.25, 904.84) * mm});
            skLineSegment(sketch, "E1137", {"start": v(59.25, 904.84) * mm, "end": v(59.32, 904.24) * mm});
            skLineSegment(sketch, "E1138", {"start": v(59.32, 904.24) * mm, "end": v(59.36, 903.64) * mm});
            skLineSegment(sketch, "E1139", {"start": v(59.36, 903.64) * mm, "end": v(59.37, 903.04) * mm});
            skLineSegment(sketch, "E1140", {"start": v(59.37, 903.04) * mm, "end": v(59.35, 902.44) * mm});
            skLineSegment(sketch, "E1141", {"start": v(59.35, 902.44) * mm, "end": v(59.31, 901.84) * mm});
            skLineSegment(sketch, "E1142", {"start": v(59.31, 901.84) * mm, "end": v(59.3, 901.3) * mm});
            skLineSegment(sketch, "E1143", {"start": v(59.3, 901.3) * mm, "end": v(59.3, 900.76) * mm});
            skLineSegment(sketch, "E1144", {"start": v(59.3, 900.76) * mm, "end": v(59.32, 900.22) * mm});
            skLineSegment(sketch, "E1145", {"start": v(59.32, 900.22) * mm, "end": v(59.34, 899.68) * mm});
            skLineSegment(sketch, "E1146", {"start": v(59.34, 899.68) * mm, "end": v(59.37, 899.15) * mm});
            skLineSegment(sketch, "E1147", {"start": v(59.37, 899.15) * mm, "end": v(59.4, 898.61) * mm});
            skLineSegment(sketch, "E1148", {"start": v(59.4, 898.61) * mm, "end": v(59.46, 898.07) * mm});
            skLineSegment(sketch, "E1149", {"start": v(59.46, 898.07) * mm, "end": v(59.52, 897.54) * mm});
            skLineSegment(sketch, "E1150", {"start": v(59.52, 897.54) * mm, "end": v(59.59, 897) * mm});
            skLineSegment(sketch, "E1151", {"start": v(59.59, 897) * mm, "end": v(59.67, 896.47) * mm});
            skLineSegment(sketch, "E1152", {"start": v(59.67, 896.47) * mm, "end": v(59.76, 895.94) * mm});
            skLineSegment(sketch, "E1153", {"start": v(59.76, 895.94) * mm, "end": v(59.85, 895.41) * mm});
            skLineSegment(sketch, "E1154", {"start": v(59.85, 895.41) * mm, "end": v(59.96, 894.88) * mm});
            skLineSegment(sketch, "E1155", {"start": v(59.96, 894.88) * mm, "end": v(60.08, 894.36) * mm});
            skLineSegment(sketch, "E1156", {"start": v(60.08, 894.36) * mm, "end": v(60.2, 893.84) * mm});
            skLineSegment(sketch, "E1157", {"start": v(60.2, 893.84) * mm, "end": v(60.34, 893.32) * mm});
            skLineSegment(sketch, "E1158", {"start": v(96.56, 923.24) * mm, "end": v(96.6, 923.8) * mm});
            skLineSegment(sketch, "E1159", {"start": v(96.6, 923.8) * mm, "end": v(96.68, 924.36) * mm});
            skLineSegment(sketch, "E1160", {"start": v(96.68, 924.36) * mm, "end": v(96.78, 924.9) * mm});
            skLineSegment(sketch, "E1161", {"start": v(96.78, 924.9) * mm, "end": v(96.9, 925.45) * mm});
            skLineSegment(sketch, "E1162", {"start": v(96.9, 925.45) * mm, "end": v(97.05, 925.98) * mm});
            skLineSegment(sketch, "E1163", {"start": v(97.05, 925.98) * mm, "end": v(97.22, 926.5) * mm});
            skLineSegment(sketch, "E1164", {"start": v(97.22, 926.5) * mm, "end": v(97.42, 927) * mm});
            skLineSegment(sketch, "E1165", {"start": v(97.42, 927) * mm, "end": v(97.64, 927.5) * mm});
            skLineSegment(sketch, "E1166", {"start": v(97.64, 927.5) * mm, "end": v(97.89, 927.98) * mm});
            skLineSegment(sketch, "E1167", {"start": v(97.89, 927.98) * mm, "end": v(98.15, 928.45) * mm});
            skLineSegment(sketch, "E1168", {"start": v(98.15, 928.45) * mm, "end": v(98.44, 928.9) * mm});
            skLineSegment(sketch, "E1169", {"start": v(98.44, 928.9) * mm, "end": v(98.74, 929.35) * mm});
            skLineSegment(sketch, "E1170", {"start": v(98.74, 929.35) * mm, "end": v(99.07, 929.78) * mm});
            skLineSegment(sketch, "E1171", {"start": v(99.07, 929.78) * mm, "end": v(99.41, 930.19) * mm});
            skLineSegment(sketch, "E1172", {"start": v(99.41, 930.19) * mm, "end": v(99.78, 930.58) * mm});
            skLineSegment(sketch, "E1173", {"start": v(99.78, 930.58) * mm, "end": v(100.16, 930.96) * mm});
            skLineSegment(sketch, "E1174", {"start": v(100.16, 930.96) * mm, "end": v(100.55, 931.31) * mm});
            skLineSegment(sketch, "E1175", {"start": v(100.55, 931.31) * mm, "end": v(100.97, 931.65) * mm});
            skLineSegment(sketch, "E1176", {"start": v(100.97, 931.65) * mm, "end": v(101.4, 931.98) * mm});
            skLineSegment(sketch, "E1177", {"start": v(101.4, 931.98) * mm, "end": v(101.84, 932.28) * mm});
            skLineSegment(sketch, "E1178", {"start": v(101.84, 932.28) * mm, "end": v(102.3, 932.56) * mm});
            skLineSegment(sketch, "E1179", {"start": v(102.3, 932.56) * mm, "end": v(102.77, 932.82) * mm});
            skLineSegment(sketch, "E1180", {"start": v(102.77, 932.82) * mm, "end": v(103.25, 933.06) * mm});
            skLineSegment(sketch, "E1181", {"start": v(103.25, 933.06) * mm, "end": v(103.75, 933.27) * mm});
            skLineSegment(sketch, "E1182", {"start": v(103.75, 933.27) * mm, "end": v(104.26, 933.46) * mm});
            skLineSegment(sketch, "E1183", {"start": v(104.26, 933.46) * mm, "end": v(104.78, 933.63) * mm});
            skLineSegment(sketch, "E1184", {"start": v(104.78, 933.63) * mm, "end": v(105.3, 933.78) * mm});
            skLineSegment(sketch, "E1185", {"start": v(105.3, 933.78) * mm, "end": v(105.84, 933.9) * mm});
            skLineSegment(sketch, "E1186", {"start": v(105.84, 933.9) * mm, "end": v(106.39, 934) * mm});
            skLineSegment(sketch, "E1187", {"start": v(106.39, 934) * mm, "end": v(106.94, 934.06) * mm});
            skLineSegment(sketch, "E1188", {"start": v(106.94, 934.06) * mm, "end": v(107.5, 934.1) * mm});
            skLineSegment(sketch, "E1189", {"start": v(107.5, 934.1) * mm, "end": v(108.08, 934.12) * mm});
            skLineSegment(sketch, "E1190", {"start": v(108.08, 934.12) * mm, "end": v(109.04, 934.12) * mm});
            skLineSegment(sketch, "E1191", {"start": v(109.04, 934.12) * mm, "end": v(109.7, 934.1) * mm});
            skLineSegment(sketch, "E1192", {"start": v(109.7, 934.1) * mm, "end": v(110.35, 934.06) * mm});
            skLineSegment(sketch, "E1193", {"start": v(110.35, 934.06) * mm, "end": v(110.99, 934) * mm});
            skLineSegment(sketch, "E1194", {"start": v(110.99, 934) * mm, "end": v(111.62, 933.91) * mm});
            skLineSegment(sketch, "E1195", {"start": v(111.62, 933.91) * mm, "end": v(112.24, 933.8) * mm});
            skLineSegment(sketch, "E1196", {"start": v(112.24, 933.8) * mm, "end": v(112.84, 933.67) * mm});
            skLineSegment(sketch, "E1197", {"start": v(112.84, 933.67) * mm, "end": v(113.44, 933.51) * mm});
            skLineSegment(sketch, "E1198", {"start": v(113.44, 933.51) * mm, "end": v(114.02, 933.34) * mm});
            skLineSegment(sketch, "E1199", {"start": v(114.02, 933.34) * mm, "end": v(114.59, 933.14) * mm});
            skLineSegment(sketch, "E1200", {"start": v(114.59, 933.14) * mm, "end": v(115.14, 932.92) * mm});
            skLineSegment(sketch, "E1201", {"start": v(115.14, 932.92) * mm, "end": v(115.67, 932.68) * mm});
            skLineSegment(sketch, "E1202", {"start": v(115.67, 932.68) * mm, "end": v(116.2, 932.42) * mm});
            skLineSegment(sketch, "E1203", {"start": v(116.2, 932.42) * mm, "end": v(116.7, 932.15) * mm});
            skLineSegment(sketch, "E1204", {"start": v(116.7, 932.15) * mm, "end": v(117.18, 931.85) * mm});
            skLineSegment(sketch, "E1205", {"start": v(117.18, 931.85) * mm, "end": v(117.64, 931.54) * mm});
            skLineSegment(sketch, "E1206", {"start": v(117.64, 931.54) * mm, "end": v(118.09, 931.21) * mm});
            skLineSegment(sketch, "E1207", {"start": v(118.09, 931.21) * mm, "end": v(118.51, 930.87) * mm});
            skLineSegment(sketch, "E1208", {"start": v(118.51, 930.87) * mm, "end": v(118.91, 930.5) * mm});
            skLineSegment(sketch, "E1209", {"start": v(118.91, 930.5) * mm, "end": v(119.3, 930.13) * mm});
            skLineSegment(sketch, "E1210", {"start": v(119.3, 930.13) * mm, "end": v(119.65, 929.74) * mm});
            skLineSegment(sketch, "E1211", {"start": v(119.65, 929.74) * mm, "end": v(119.98, 929.34) * mm});
            skLineSegment(sketch, "E1212", {"start": v(119.98, 929.34) * mm, "end": v(120.3, 928.92) * mm});
            skLineSegment(sketch, "E1213", {"start": v(120.3, 928.92) * mm, "end": v(120.57, 928.5) * mm});
            skLineSegment(sketch, "E1214", {"start": v(120.57, 928.5) * mm, "end": v(120.83, 928.06) * mm});
            skLineSegment(sketch, "E1215", {"start": v(120.83, 928.06) * mm, "end": v(121.06, 927.6) * mm});
            skLineSegment(sketch, "E1216", {"start": v(121.06, 927.6) * mm, "end": v(121.16, 927.38) * mm});
            skLineSegment(sketch, "E1217", {"start": v(121.16, 927.38) * mm, "end": v(121.26, 927.15) * mm});
            skLineSegment(sketch, "E1218", {"start": v(121.26, 927.15) * mm, "end": v(121.35, 926.91) * mm});
            skLineSegment(sketch, "E1219", {"start": v(121.35, 926.91) * mm, "end": v(121.43, 926.68) * mm});
            skLineSegment(sketch, "E1220", {"start": v(121.43, 926.68) * mm, "end": v(121.5, 926.44) * mm});
            skLineSegment(sketch, "E1221", {"start": v(121.5, 926.44) * mm, "end": v(121.58, 926.2) * mm});
            skLineSegment(sketch, "E1222", {"start": v(121.58, 926.2) * mm, "end": v(121.64, 925.95) * mm});
            skLineSegment(sketch, "E1223", {"start": v(121.64, 925.95) * mm, "end": v(121.69, 925.7) * mm});
            skLineSegment(sketch, "E1224", {"start": v(121.69, 925.7) * mm, "end": v(121.73, 925.46) * mm});
            skLineSegment(sketch, "E1225", {"start": v(121.73, 925.46) * mm, "end": v(121.77, 925.21) * mm});
            skLineSegment(sketch, "E1226", {"start": v(121.77, 925.21) * mm, "end": v(121.8, 924.96) * mm});
            skLineSegment(sketch, "E1227", {"start": v(121.8, 924.96) * mm, "end": v(121.82, 924.7) * mm});
            skLineSegment(sketch, "E1228", {"start": v(121.82, 924.7) * mm, "end": v(121.83, 924.45) * mm});
            skLineSegment(sketch, "E1229", {"start": v(121.83, 924.45) * mm, "end": v(121.84, 924.2) * mm});
            skLineSegment(sketch, "E1230", {"start": v(121.84, 924.2) * mm, "end": v(121.84, 923.72) * mm});
            skLineSegment(sketch, "E1231", {"start": v(121.84, 923.72) * mm, "end": v(121.83, 923.42) * mm});
            skLineSegment(sketch, "E1232", {"start": v(121.83, 923.42) * mm, "end": v(121.82, 923.13) * mm});
            skLineSegment(sketch, "E1233", {"start": v(121.82, 923.13) * mm, "end": v(121.8, 922.84) * mm});
            skLineSegment(sketch, "E1234", {"start": v(121.8, 922.84) * mm, "end": v(121.77, 922.54) * mm});
            skLineSegment(sketch, "E1235", {"start": v(121.77, 922.54) * mm, "end": v(121.73, 922.25) * mm});
            skLineSegment(sketch, "E1236", {"start": v(121.73, 922.25) * mm, "end": v(121.69, 921.97) * mm});
            skLineSegment(sketch, "E1237", {"start": v(121.69, 921.97) * mm, "end": v(121.64, 921.68) * mm});
            skLineSegment(sketch, "E1238", {"start": v(121.64, 921.68) * mm, "end": v(121.58, 921.4) * mm});
            skLineSegment(sketch, "E1239", {"start": v(121.58, 921.4) * mm, "end": v(121.5, 921.11) * mm});
            skLineSegment(sketch, "E1240", {"start": v(121.5, 921.11) * mm, "end": v(121.43, 920.83) * mm});
            skLineSegment(sketch, "E1241", {"start": v(121.43, 920.83) * mm, "end": v(121.35, 920.55) * mm});
            skLineSegment(sketch, "E1242", {"start": v(121.35, 920.55) * mm, "end": v(121.26, 920.28) * mm});
            skLineSegment(sketch, "E1243", {"start": v(121.26, 920.28) * mm, "end": v(121.16, 920) * mm});
            skLineSegment(sketch, "E1244", {"start": v(121.16, 920) * mm, "end": v(121.06, 919.74) * mm});
            skLineSegment(sketch, "E1245", {"start": v(121.06, 919.74) * mm, "end": v(120.95, 919.47) * mm});
            skLineSegment(sketch, "E1246", {"start": v(120.95, 919.47) * mm, "end": v(120.83, 919.2) * mm});
            skLineSegment(sketch, "E1247", {"start": v(120.83, 919.2) * mm, "end": v(120.7, 918.95) * mm});
            skLineSegment(sketch, "E1248", {"start": v(120.7, 918.95) * mm, "end": v(120.57, 918.69) * mm});
            skLineSegment(sketch, "E1249", {"start": v(120.57, 918.69) * mm, "end": v(120.43, 918.44) * mm});
            skLineSegment(sketch, "E1250", {"start": v(120.43, 918.44) * mm, "end": v(120.28, 918.19) * mm});
            skLineSegment(sketch, "E1251", {"start": v(120.28, 918.19) * mm, "end": v(120.12, 917.94) * mm});
            skLineSegment(sketch, "E1252", {"start": v(120.12, 917.94) * mm, "end": v(119.96, 917.7) * mm});
            skLineSegment(sketch, "E1253", {"start": v(119.96, 917.7) * mm, "end": v(119.8, 917.46) * mm});
            skLineSegment(sketch, "E1254", {"start": v(119.8, 917.46) * mm, "end": v(119.62, 917.23) * mm});
            skLineSegment(sketch, "E1255", {"start": v(119.62, 917.23) * mm, "end": v(119.44, 917) * mm});
            skLineSegment(sketch, "E1256", {"start": v(119.44, 917) * mm, "end": v(119.25, 916.78) * mm});
            skLineSegment(sketch, "E1257", {"start": v(119.25, 916.78) * mm, "end": v(119.06, 916.56) * mm});
            skLineSegment(sketch, "E1258", {"start": v(119.06, 916.56) * mm, "end": v(118.86, 916.35) * mm});
            skLineSegment(sketch, "E1259", {"start": v(118.86, 916.35) * mm, "end": v(118.65, 916.14) * mm});
            skLineSegment(sketch, "E1260", {"start": v(118.65, 916.14) * mm, "end": v(118.44, 915.94) * mm});
            skLineSegment(sketch, "E1261", {"start": v(118.44, 915.94) * mm, "end": v(118.22, 915.75) * mm});
            skLineSegment(sketch, "E1262", {"start": v(118.22, 915.75) * mm, "end": v(118, 915.56) * mm});
            skLineSegment(sketch, "E1263", {"start": v(118, 915.56) * mm, "end": v(102.8, 905.64) * mm});
            skLineSegment(sketch, "E1264", {"start": v(102.8, 905.64) * mm, "end": v(102.41, 905.38) * mm});
            skLineSegment(sketch, "E1265", {"start": v(102.41, 905.38) * mm, "end": v(102.04, 905.1) * mm});
            skLineSegment(sketch, "E1266", {"start": v(102.04, 905.1) * mm, "end": v(101.67, 904.82) * mm});
            skLineSegment(sketch, "E1267", {"start": v(101.67, 904.82) * mm, "end": v(101.31, 904.53) * mm});
            skLineSegment(sketch, "E1268", {"start": v(101.31, 904.53) * mm, "end": v(100.97, 904.23) * mm});
            skLineSegment(sketch, "E1269", {"start": v(100.97, 904.23) * mm, "end": v(100.63, 903.91) * mm});
            skLineSegment(sketch, "E1270", {"start": v(100.63, 903.91) * mm, "end": v(100.3, 903.6) * mm});
            skLineSegment(sketch, "E1271", {"start": v(100.3, 903.6) * mm, "end": v(100, 903.26) * mm});
            skLineSegment(sketch, "E1272", {"start": v(100, 903.26) * mm, "end": v(99.7, 902.92) * mm});
            skLineSegment(sketch, "E1273", {"start": v(99.7, 902.92) * mm, "end": v(99.4, 902.57) * mm});
            skLineSegment(sketch, "E1274", {"start": v(99.4, 902.57) * mm, "end": v(99.12, 902.22) * mm});
            skLineSegment(sketch, "E1275", {"start": v(99.12, 902.22) * mm, "end": v(98.85, 901.85) * mm});
            skLineSegment(sketch, "E1276", {"start": v(98.85, 901.85) * mm, "end": v(98.6, 901.48) * mm});
            skLineSegment(sketch, "E1277", {"start": v(98.6, 901.48) * mm, "end": v(98.34, 901.1) * mm});
            skLineSegment(sketch, "E1278", {"start": v(98.34, 901.1) * mm, "end": v(98.1, 900.71) * mm});
            skLineSegment(sketch, "E1279", {"start": v(98.1, 900.71) * mm, "end": v(97.89, 900.32) * mm});
            skLineSegment(sketch, "E1280", {"start": v(97.89, 900.32) * mm, "end": v(97.68, 899.92) * mm});
            skLineSegment(sketch, "E1281", {"start": v(97.68, 899.92) * mm, "end": v(97.48, 899.5) * mm});
            skLineSegment(sketch, "E1282", {"start": v(97.48, 899.5) * mm, "end": v(97.3, 899.1) * mm});
            skLineSegment(sketch, "E1283", {"start": v(97.3, 899.1) * mm, "end": v(97.12, 898.68) * mm});
            skLineSegment(sketch, "E1284", {"start": v(97.12, 898.68) * mm, "end": v(96.96, 898.25) * mm});
            skLineSegment(sketch, "E1285", {"start": v(96.96, 898.25) * mm, "end": v(96.8, 897.82) * mm});
            skLineSegment(sketch, "E1286", {"start": v(96.8, 897.82) * mm, "end": v(96.67, 897.39) * mm});
            skLineSegment(sketch, "E1287", {"start": v(96.67, 897.39) * mm, "end": v(96.55, 896.95) * mm});
            skLineSegment(sketch, "E1288", {"start": v(96.55, 896.95) * mm, "end": v(96.44, 896.5) * mm});
            skLineSegment(sketch, "E1289", {"start": v(96.44, 896.5) * mm, "end": v(96.35, 896.06) * mm});
            skLineSegment(sketch, "E1290", {"start": v(96.35, 896.06) * mm, "end": v(96.27, 895.61) * mm});
            skLineSegment(sketch, "E1291", {"start": v(96.27, 895.61) * mm, "end": v(96.2, 895.16) * mm});
            skLineSegment(sketch, "E1292", {"start": v(96.2, 895.16) * mm, "end": v(96.15, 894.7) * mm});
            skLineSegment(sketch, "E1293", {"start": v(96.15, 894.7) * mm, "end": v(96.11, 894.24) * mm});
            skLineSegment(sketch, "E1294", {"start": v(96.11, 894.24) * mm, "end": v(96.09, 893.78) * mm});
            skLineSegment(sketch, "E1295", {"start": v(96.09, 893.78) * mm, "end": v(96.08, 893.32) * mm});
            skLineSegment(sketch, "E1296", {"start": v(96.08, 893.32) * mm, "end": v(122.64, 893.32) * mm});
            skLineSegment(sketch, "E1297", {"start": v(-98.9, 302.87) * mm, "end": v(-98.9, 342.86) * mm});
            skLineSegment(sketch, "E1298", {"start": v(-98.9, 342.86) * mm, "end": v(-74.04, 342.86) * mm});
            skLineSegment(sketch, "E1299", {"start": v(-98.9, 323.75) * mm, "end": v(-75.83, 323.75) * mm});
            skLineSegment(sketch, "E1300", {"start": v(-41.75, 302.9) * mm, "end": v(-65.24, 302.9) * mm});
            skLineSegment(sketch, "E1301", {"start": v(-65.24, 302.9) * mm, "end": v(-65.24, 342.85) * mm});
            skLineSegment(sketch, "E1302", {"start": v(-26.58, 302.34) * mm, "end": v(-27, 302.33) * mm});
            skLineSegment(sketch, "E1303", {"start": v(-27, 302.33) * mm, "end": v(-27.42, 302.34) * mm});
            skLineSegment(sketch, "E1304", {"start": v(-27.42, 302.34) * mm, "end": v(-27.84, 302.36) * mm});
            skLineSegment(sketch, "E1305", {"start": v(-27.84, 302.36) * mm, "end": v(-28.26, 302.39) * mm});
            skLineSegment(sketch, "E1306", {"start": v(-28.26, 302.39) * mm, "end": v(-28.67, 302.42) * mm});
            skLineSegment(sketch, "E1307", {"start": v(-28.67, 302.42) * mm, "end": v(-29.09, 302.47) * mm});
            skLineSegment(sketch, "E1308", {"start": v(-29.09, 302.47) * mm, "end": v(-29.5, 302.53) * mm});
            skLineSegment(sketch, "E1309", {"start": v(-29.5, 302.53) * mm, "end": v(-29.9, 302.6) * mm});
            skLineSegment(sketch, "E1310", {"start": v(-29.9, 302.6) * mm, "end": v(-30.31, 302.68) * mm});
            skLineSegment(sketch, "E1311", {"start": v(-30.31, 302.68) * mm, "end": v(-30.72, 302.77) * mm});
            skLineSegment(sketch, "E1312", {"start": v(-30.72, 302.77) * mm, "end": v(-31.12, 302.87) * mm});
            skLineSegment(sketch, "E1313", {"start": v(-31.12, 302.87) * mm, "end": v(-31.52, 302.98) * mm});
            skLineSegment(sketch, "E1314", {"start": v(-31.52, 302.98) * mm, "end": v(-31.92, 303.1) * mm});
            skLineSegment(sketch, "E1315", {"start": v(-31.92, 303.1) * mm, "end": v(-32.31, 303.23) * mm});
            skLineSegment(sketch, "E1316", {"start": v(-32.31, 303.23) * mm, "end": v(-32.7, 303.37) * mm});
            skLineSegment(sketch, "E1317", {"start": v(-32.7, 303.37) * mm, "end": v(-33.09, 303.52) * mm});
            skLineSegment(sketch, "E1318", {"start": v(-33.09, 303.52) * mm, "end": v(-33.47, 303.67) * mm});
            skLineSegment(sketch, "E1319", {"start": v(-33.47, 303.67) * mm, "end": v(-33.85, 303.84) * mm});
            skLineSegment(sketch, "E1320", {"start": v(-33.85, 303.84) * mm, "end": v(-34.22, 304.02) * mm});
            skLineSegment(sketch, "E1321", {"start": v(-34.22, 304.02) * mm, "end": v(-34.6, 304.2) * mm});
            skLineSegment(sketch, "E1322", {"start": v(-34.6, 304.2) * mm, "end": v(-34.96, 304.4) * mm});
            skLineSegment(sketch, "E1323", {"start": v(-34.96, 304.4) * mm, "end": v(-35.32, 304.6) * mm});
            skLineSegment(sketch, "E1324", {"start": v(-35.32, 304.6) * mm, "end": v(-35.67, 304.82) * mm});
            skLineSegment(sketch, "E1325", {"start": v(-35.67, 304.82) * mm, "end": v(-36.02, 305.04) * mm});
            skLineSegment(sketch, "E1326", {"start": v(-36.02, 305.04) * mm, "end": v(-36.37, 305.27) * mm});
            skLineSegment(sketch, "E1327", {"start": v(-36.37, 305.27) * mm, "end": v(-36.7, 305.5) * mm});
            skLineSegment(sketch, "E1328", {"start": v(-36.7, 305.5) * mm, "end": v(-37.04, 305.76) * mm});
            skLineSegment(sketch, "E1329", {"start": v(-37.04, 305.76) * mm, "end": v(-37.37, 306.02) * mm});
            skLineSegment(sketch, "E1330", {"start": v(-37.37, 306.02) * mm, "end": v(-37.7, 306.28) * mm});
            skLineSegment(sketch, "E1331", {"start": v(-37.7, 306.28) * mm, "end": v(-38, 306.56) * mm});
            skLineSegment(sketch, "E1332", {"start": v(-38, 306.56) * mm, "end": v(-38.32, 306.84) * mm});
            skLineSegment(sketch, "E1333", {"start": v(-38.32, 306.84) * mm, "end": v(-38.62, 307.13) * mm});
            skLineSegment(sketch, "E1334", {"start": v(-38.62, 307.13) * mm, "end": v(-38.97, 307.51) * mm});
            skLineSegment(sketch, "E1335", {"start": v(-38.97, 307.51) * mm, "end": v(-39.3, 307.9) * mm});
            skLineSegment(sketch, "E1336", {"start": v(-39.3, 307.9) * mm, "end": v(-39.64, 308.3) * mm});
            skLineSegment(sketch, "E1337", {"start": v(-39.64, 308.3) * mm, "end": v(-39.96, 308.7) * mm});
            skLineSegment(sketch, "E1338", {"start": v(-39.96, 308.7) * mm, "end": v(-40.26, 309.1) * mm});
            skLineSegment(sketch, "E1339", {"start": v(-40.26, 309.1) * mm, "end": v(-40.56, 309.53) * mm});
            skLineSegment(sketch, "E1340", {"start": v(-40.56, 309.53) * mm, "end": v(-40.85, 309.95) * mm});
            skLineSegment(sketch, "E1341", {"start": v(-40.85, 309.95) * mm, "end": v(-41.12, 310.38) * mm});
            skLineSegment(sketch, "E1342", {"start": v(-41.12, 310.38) * mm, "end": v(-41.39, 310.82) * mm});
            skLineSegment(sketch, "E1343", {"start": v(-41.39, 310.82) * mm, "end": v(-41.64, 311.26) * mm});
            skLineSegment(sketch, "E1344", {"start": v(-41.64, 311.26) * mm, "end": v(-41.88, 311.7) * mm});
            skLineSegment(sketch, "E1345", {"start": v(-41.88, 311.7) * mm, "end": v(-42.12, 312.16) * mm});
            skLineSegment(sketch, "E1346", {"start": v(-42.12, 312.16) * mm, "end": v(-42.33, 312.62) * mm});
            skLineSegment(sketch, "E1347", {"start": v(-42.33, 312.62) * mm, "end": v(-42.54, 313.09) * mm});
            skLineSegment(sketch, "E1348", {"start": v(-42.54, 313.09) * mm, "end": v(-42.74, 313.56) * mm});
            skLineSegment(sketch, "E1349", {"start": v(-42.74, 313.56) * mm, "end": v(-42.93, 314.03) * mm});
            skLineSegment(sketch, "E1350", {"start": v(-42.93, 314.03) * mm, "end": v(-43.1, 314.51) * mm});
            skLineSegment(sketch, "E1351", {"start": v(-43.1, 314.51) * mm, "end": v(-43.26, 315) * mm});
            skLineSegment(sketch, "E1352", {"start": v(-43.26, 315) * mm, "end": v(-43.41, 315.48) * mm});
            skLineSegment(sketch, "E1353", {"start": v(-43.41, 315.48) * mm, "end": v(-43.55, 315.97) * mm});
            skLineSegment(sketch, "E1354", {"start": v(-43.55, 315.97) * mm, "end": v(-43.68, 316.47) * mm});
            skLineSegment(sketch, "E1355", {"start": v(-43.68, 316.47) * mm, "end": v(-43.8, 316.96) * mm});
            skLineSegment(sketch, "E1356", {"start": v(-43.8, 316.96) * mm, "end": v(-43.9, 317.46) * mm});
            skLineSegment(sketch, "E1357", {"start": v(-43.9, 317.46) * mm, "end": v(-43.98, 317.97) * mm});
            skLineSegment(sketch, "E1358", {"start": v(-43.98, 317.97) * mm, "end": v(-44.06, 318.47) * mm});
            skLineSegment(sketch, "E1359", {"start": v(-44.06, 318.47) * mm, "end": v(-44.12, 318.98) * mm});
            skLineSegment(sketch, "E1360", {"start": v(-44.12, 318.98) * mm, "end": v(-44.18, 319.49) * mm});
            skLineSegment(sketch, "E1361", {"start": v(-44.18, 319.49) * mm, "end": v(-44.22, 320) * mm});
            skLineSegment(sketch, "E1362", {"start": v(-44.22, 320) * mm, "end": v(-44.24, 320.51) * mm});
            skLineSegment(sketch, "E1363", {"start": v(-44.24, 320.51) * mm, "end": v(-44.26, 321.03) * mm});
            skLineSegment(sketch, "E1364", {"start": v(-44.26, 321.03) * mm, "end": v(-44.26, 321.54) * mm});
            skLineSegment(sketch, "E1365", {"start": v(-44.26, 321.54) * mm, "end": v(-44.25, 322.06) * mm});
            skLineSegment(sketch, "E1366", {"start": v(-44.25, 322.06) * mm, "end": v(-44.26, 322.62) * mm});
            skLineSegment(sketch, "E1367", {"start": v(-44.26, 322.62) * mm, "end": v(-44.26, 323.18) * mm});
            skLineSegment(sketch, "E1368", {"start": v(-44.26, 323.18) * mm, "end": v(-44.25, 323.74) * mm});
            skLineSegment(sketch, "E1369", {"start": v(-44.25, 323.74) * mm, "end": v(-44.22, 324.3) * mm});
            skLineSegment(sketch, "E1370", {"start": v(-44.22, 324.3) * mm, "end": v(-44.18, 324.85) * mm});
            skLineSegment(sketch, "E1371", {"start": v(-44.18, 324.85) * mm, "end": v(-44.13, 325.4) * mm});
            skLineSegment(sketch, "E1372", {"start": v(-44.13, 325.4) * mm, "end": v(-44.06, 325.96) * mm});
            skLineSegment(sketch, "E1373", {"start": v(-44.06, 325.96) * mm, "end": v(-43.98, 326.5) * mm});
            skLineSegment(sketch, "E1374", {"start": v(-43.98, 326.5) * mm, "end": v(-43.88, 327.06) * mm});
            skLineSegment(sketch, "E1375", {"start": v(-43.88, 327.06) * mm, "end": v(-43.77, 327.6) * mm});
            skLineSegment(sketch, "E1376", {"start": v(-43.77, 327.6) * mm, "end": v(-43.65, 328.14) * mm});
            skLineSegment(sketch, "E1377", {"start": v(-43.65, 328.14) * mm, "end": v(-43.52, 328.68) * mm});
            skLineSegment(sketch, "E1378", {"start": v(-43.52, 328.68) * mm, "end": v(-43.37, 329.2) * mm});
            skLineSegment(sketch, "E1379", {"start": v(-43.37, 329.2) * mm, "end": v(-43.2, 329.74) * mm});
            skLineSegment(sketch, "E1380", {"start": v(-43.2, 329.74) * mm, "end": v(-43.03, 330.26) * mm});
            skLineSegment(sketch, "E1381", {"start": v(-43.03, 330.26) * mm, "end": v(-42.84, 330.78) * mm});
            skLineSegment(sketch, "E1382", {"start": v(-42.84, 330.78) * mm, "end": v(-42.64, 331.3) * mm});
            skLineSegment(sketch, "E1383", {"start": v(-42.64, 331.3) * mm, "end": v(-42.43, 331.8) * mm});
            skLineSegment(sketch, "E1384", {"start": v(-42.43, 331.8) * mm, "end": v(-42.2, 332.31) * mm});
            skLineSegment(sketch, "E1385", {"start": v(-42.2, 332.31) * mm, "end": v(-41.96, 332.81) * mm});
            skLineSegment(sketch, "E1386", {"start": v(-41.96, 332.81) * mm, "end": v(-41.71, 333.3) * mm});
            skLineSegment(sketch, "E1387", {"start": v(-41.71, 333.3) * mm, "end": v(-41.45, 333.8) * mm});
            skLineSegment(sketch, "E1388", {"start": v(-41.45, 333.8) * mm, "end": v(-41.17, 334.27) * mm});
            skLineSegment(sketch, "E1389", {"start": v(-41.17, 334.27) * mm, "end": v(-40.88, 334.75) * mm});
            skLineSegment(sketch, "E1390", {"start": v(-40.88, 334.75) * mm, "end": v(-40.58, 335.21) * mm});
            skLineSegment(sketch, "E1391", {"start": v(-40.58, 335.21) * mm, "end": v(-40.27, 335.67) * mm});
            skLineSegment(sketch, "E1392", {"start": v(-40.27, 335.67) * mm, "end": v(-39.95, 336.13) * mm});
            skLineSegment(sketch, "E1393", {"start": v(-39.95, 336.13) * mm, "end": v(-39.61, 336.57) * mm});
            skLineSegment(sketch, "E1394", {"start": v(-39.61, 336.57) * mm, "end": v(-39.27, 337) * mm});
            skLineSegment(sketch, "E1395", {"start": v(-39.27, 337) * mm, "end": v(-38.9, 337.44) * mm});
            skLineSegment(sketch, "E1396", {"start": v(-38.9, 337.44) * mm, "end": v(-38.54, 337.86) * mm});
            skLineSegment(sketch, "E1397", {"start": v(-38.54, 337.86) * mm, "end": v(-38.15, 338.27) * mm});
            skLineSegment(sketch, "E1398", {"start": v(-38.15, 338.27) * mm, "end": v(-37.87, 338.56) * mm});
            skLineSegment(sketch, "E1399", {"start": v(-37.87, 338.56) * mm, "end": v(-37.58, 338.84) * mm});
            skLineSegment(sketch, "E1400", {"start": v(-37.58, 338.84) * mm, "end": v(-37.28, 339.12) * mm});
            skLineSegment(sketch, "E1401", {"start": v(-37.28, 339.12) * mm, "end": v(-36.97, 339.38) * mm});
            skLineSegment(sketch, "E1402", {"start": v(-36.97, 339.38) * mm, "end": v(-36.66, 339.64) * mm});
            skLineSegment(sketch, "E1403", {"start": v(-36.66, 339.64) * mm, "end": v(-36.34, 339.89) * mm});
            skLineSegment(sketch, "E1404", {"start": v(-36.34, 339.89) * mm, "end": v(-36.02, 340.13) * mm});
            skLineSegment(sketch, "E1405", {"start": v(-36.02, 340.13) * mm, "end": v(-35.69, 340.36) * mm});
            skLineSegment(sketch, "E1406", {"start": v(-35.69, 340.36) * mm, "end": v(-35.35, 340.58) * mm});
            skLineSegment(sketch, "E1407", {"start": v(-35.35, 340.58) * mm, "end": v(-35.01, 340.8) * mm});
            skLineSegment(sketch, "E1408", {"start": v(-35.01, 340.8) * mm, "end": v(-34.67, 341) * mm});
            skLineSegment(sketch, "E1409", {"start": v(-34.67, 341) * mm, "end": v(-34.32, 341.2) * mm});
            skLineSegment(sketch, "E1410", {"start": v(-34.32, 341.2) * mm, "end": v(-33.96, 341.38) * mm});
            skLineSegment(sketch, "E1411", {"start": v(-33.96, 341.38) * mm, "end": v(-33.6, 341.56) * mm});
            skLineSegment(sketch, "E1412", {"start": v(-33.6, 341.56) * mm, "end": v(-33.24, 341.73) * mm});
            skLineSegment(sketch, "E1413", {"start": v(-33.24, 341.73) * mm, "end": v(-32.87, 341.89) * mm});
            skLineSegment(sketch, "E1414", {"start": v(-32.87, 341.89) * mm, "end": v(-32.5, 342.04) * mm});
            skLineSegment(sketch, "E1415", {"start": v(-32.5, 342.04) * mm, "end": v(-32.12, 342.18) * mm});
            skLineSegment(sketch, "E1416", {"start": v(-32.12, 342.18) * mm, "end": v(-31.74, 342.3) * mm});
            skLineSegment(sketch, "E1417", {"start": v(-31.74, 342.3) * mm, "end": v(-31.36, 342.43) * mm});
            skLineSegment(sketch, "E1418", {"start": v(-31.36, 342.43) * mm, "end": v(-30.97, 342.54) * mm});
            skLineSegment(sketch, "E1419", {"start": v(-30.97, 342.54) * mm, "end": v(-30.58, 342.64) * mm});
            skLineSegment(sketch, "E1420", {"start": v(-30.58, 342.64) * mm, "end": v(-30.2, 342.73) * mm});
            skLineSegment(sketch, "E1421", {"start": v(-30.2, 342.73) * mm, "end": v(-29.8, 342.82) * mm});
            skLineSegment(sketch, "E1422", {"start": v(-29.8, 342.82) * mm, "end": v(-29.4, 342.89) * mm});
            skLineSegment(sketch, "E1423", {"start": v(-29.4, 342.89) * mm, "end": v(-29, 342.95) * mm});
            skLineSegment(sketch, "E1424", {"start": v(-29, 342.95) * mm, "end": v(-28.6, 343) * mm});
            skLineSegment(sketch, "E1425", {"start": v(-28.6, 343) * mm, "end": v(-28.2, 343.04) * mm});
            skLineSegment(sketch, "E1426", {"start": v(-28.2, 343.04) * mm, "end": v(-27.8, 343.07) * mm});
            skLineSegment(sketch, "E1427", {"start": v(-27.8, 343.07) * mm, "end": v(-27.4, 343.09) * mm});
            skLineSegment(sketch, "E1428", {"start": v(-27.4, 343.09) * mm, "end": v(-26.98, 343.1) * mm});
            skLineSegment(sketch, "E1429", {"start": v(-26.98, 343.1) * mm, "end": v(-26.58, 343.1) * mm});
            skLineSegment(sketch, "E1430", {"start": v(-26.58, 343.1) * mm, "end": v(-26.16, 343.1) * mm});
            skLineSegment(sketch, "E1431", {"start": v(-26.16, 343.1) * mm, "end": v(-25.75, 343.08) * mm});
            skLineSegment(sketch, "E1432", {"start": v(-25.75, 343.08) * mm, "end": v(-25.34, 343.05) * mm});
            skLineSegment(sketch, "E1433", {"start": v(-25.34, 343.05) * mm, "end": v(-24.93, 343.02) * mm});
            skLineSegment(sketch, "E1434", {"start": v(-24.93, 343.02) * mm, "end": v(-24.52, 342.97) * mm});
            skLineSegment(sketch, "E1435", {"start": v(-24.52, 342.97) * mm, "end": v(-24.11, 342.91) * mm});
            skLineSegment(sketch, "E1436", {"start": v(-24.11, 342.91) * mm, "end": v(-23.7, 342.85) * mm});
            skLineSegment(sketch, "E1437", {"start": v(-23.7, 342.85) * mm, "end": v(-23.3, 342.77) * mm});
            skLineSegment(sketch, "E1438", {"start": v(-23.3, 342.77) * mm, "end": v(-22.9, 342.68) * mm});
            skLineSegment(sketch, "E1439", {"start": v(-22.9, 342.68) * mm, "end": v(-22.5, 342.58) * mm});
            skLineSegment(sketch, "E1440", {"start": v(-22.5, 342.58) * mm, "end": v(-22.11, 342.48) * mm});
            skLineSegment(sketch, "E1441", {"start": v(-22.11, 342.48) * mm, "end": v(-21.72, 342.36) * mm});
            skLineSegment(sketch, "E1442", {"start": v(-21.72, 342.36) * mm, "end": v(-21.34, 342.23) * mm});
            skLineSegment(sketch, "E1443", {"start": v(-21.34, 342.23) * mm, "end": v(-20.95, 342.1) * mm});
            skLineSegment(sketch, "E1444", {"start": v(-20.95, 342.1) * mm, "end": v(-20.57, 341.95) * mm});
            skLineSegment(sketch, "E1445", {"start": v(-20.57, 341.95) * mm, "end": v(-20.2, 341.79) * mm});
            skLineSegment(sketch, "E1446", {"start": v(-20.2, 341.79) * mm, "end": v(-19.82, 341.62) * mm});
            skLineSegment(sketch, "E1447", {"start": v(-19.82, 341.62) * mm, "end": v(-19.46, 341.45) * mm});
            skLineSegment(sketch, "E1448", {"start": v(-19.46, 341.45) * mm, "end": v(-19.1, 341.26) * mm});
            skLineSegment(sketch, "E1449", {"start": v(-19.1, 341.26) * mm, "end": v(-18.73, 341.07) * mm});
            skLineSegment(sketch, "E1450", {"start": v(-18.73, 341.07) * mm, "end": v(-18.38, 340.86) * mm});
            skLineSegment(sketch, "E1451", {"start": v(-18.38, 340.86) * mm, "end": v(-18.03, 340.65) * mm});
            skLineSegment(sketch, "E1452", {"start": v(-18.03, 340.65) * mm, "end": v(-17.69, 340.43) * mm});
            skLineSegment(sketch, "E1453", {"start": v(-17.69, 340.43) * mm, "end": v(-17.35, 340.2) * mm});
            skLineSegment(sketch, "E1454", {"start": v(-17.35, 340.2) * mm, "end": v(-17.02, 339.96) * mm});
            skLineSegment(sketch, "E1455", {"start": v(-17.02, 339.96) * mm, "end": v(-16.7, 339.71) * mm});
            skLineSegment(sketch, "E1456", {"start": v(-16.7, 339.71) * mm, "end": v(-16.37, 339.46) * mm});
            skLineSegment(sketch, "E1457", {"start": v(-16.37, 339.46) * mm, "end": v(-16.06, 339.2) * mm});
            skLineSegment(sketch, "E1458", {"start": v(-16.06, 339.2) * mm, "end": v(-15.75, 338.92) * mm});
            skLineSegment(sketch, "E1459", {"start": v(-15.75, 338.92) * mm, "end": v(-15.45, 338.63) * mm});
            skLineSegment(sketch, "E1460", {"start": v(-15.45, 338.63) * mm, "end": v(-15.15, 338.34) * mm});
            skLineSegment(sketch, "E1461", {"start": v(-15.15, 338.34) * mm, "end": v(-14.87, 338.05) * mm});
            skLineSegment(sketch, "E1462", {"start": v(-14.87, 338.05) * mm, "end": v(-14.5, 337.64) * mm});
            skLineSegment(sketch, "E1463", {"start": v(-14.5, 337.64) * mm, "end": v(-14.14, 337.22) * mm});
            skLineSegment(sketch, "E1464", {"start": v(-14.14, 337.22) * mm, "end": v(-13.79, 336.8) * mm});
            skLineSegment(sketch, "E1465", {"start": v(-13.79, 336.8) * mm, "end": v(-13.45, 336.36) * mm});
            skLineSegment(sketch, "E1466", {"start": v(-13.45, 336.36) * mm, "end": v(-13.13, 335.92) * mm});
            skLineSegment(sketch, "E1467", {"start": v(-13.13, 335.92) * mm, "end": v(-12.82, 335.47) * mm});
            skLineSegment(sketch, "E1468", {"start": v(-12.82, 335.47) * mm, "end": v(-12.51, 335.01) * mm});
            skLineSegment(sketch, "E1469", {"start": v(-12.51, 335.01) * mm, "end": v(-12.22, 334.55) * mm});
            skLineSegment(sketch, "E1470", {"start": v(-12.22, 334.55) * mm, "end": v(-11.95, 334.08) * mm});
            skLineSegment(sketch, "E1471", {"start": v(-11.95, 334.08) * mm, "end": v(-11.68, 333.6) * mm});
            skLineSegment(sketch, "E1472", {"start": v(-11.68, 333.6) * mm, "end": v(-11.43, 333.12) * mm});
            skLineSegment(sketch, "E1473", {"start": v(-11.43, 333.12) * mm, "end": v(-11.18, 332.63) * mm});
            skLineSegment(sketch, "E1474", {"start": v(-11.18, 332.63) * mm, "end": v(-10.95, 332.14) * mm});
            skLineSegment(sketch, "E1475", {"start": v(-10.95, 332.14) * mm, "end": v(-10.74, 331.64) * mm});
            skLineSegment(sketch, "E1476", {"start": v(-10.74, 331.64) * mm, "end": v(-10.53, 331.14) * mm});
            skLineSegment(sketch, "E1477", {"start": v(-10.53, 331.14) * mm, "end": v(-10.34, 330.63) * mm});
            skLineSegment(sketch, "E1478", {"start": v(-10.34, 330.63) * mm, "end": v(-10.16, 330.11) * mm});
            skLineSegment(sketch, "E1479", {"start": v(-10.16, 330.11) * mm, "end": v(-10, 329.6) * mm});
            skLineSegment(sketch, "E1480", {"start": v(-10, 329.6) * mm, "end": v(-9.84, 329.08) * mm});
            skLineSegment(sketch, "E1481", {"start": v(-9.84, 329.08) * mm, "end": v(-9.7, 328.55) * mm});
            skLineSegment(sketch, "E1482", {"start": v(-9.7, 328.55) * mm, "end": v(-9.57, 328.02) * mm});
            skLineSegment(sketch, "E1483", {"start": v(-9.57, 328.02) * mm, "end": v(-9.45, 327.49) * mm});
            skLineSegment(sketch, "E1484", {"start": v(-9.45, 327.49) * mm, "end": v(-9.35, 326.95) * mm});
            skLineSegment(sketch, "E1485", {"start": v(-9.35, 326.95) * mm, "end": v(-9.26, 326.41) * mm});
            skLineSegment(sketch, "E1486", {"start": v(-9.26, 326.41) * mm, "end": v(-9.18, 325.87) * mm});
            skLineSegment(sketch, "E1487", {"start": v(-9.18, 325.87) * mm, "end": v(-9.12, 325.33) * mm});
            skLineSegment(sketch, "E1488", {"start": v(-9.12, 325.33) * mm, "end": v(-9.07, 324.79) * mm});
            skLineSegment(sketch, "E1489", {"start": v(-9.07, 324.79) * mm, "end": v(-9.04, 324.24) * mm});
            skLineSegment(sketch, "E1490", {"start": v(-9.04, 324.24) * mm, "end": v(-9.01, 323.69) * mm});
            skLineSegment(sketch, "E1491", {"start": v(-9.01, 323.69) * mm, "end": v(-9, 323.14) * mm});
            skLineSegment(sketch, "E1492", {"start": v(-9, 323.14) * mm, "end": v(-9.01, 322.59) * mm});
            skLineSegment(sketch, "E1493", {"start": v(-9.01, 322.59) * mm, "end": v(-9.03, 322.04) * mm});
            skLineSegment(sketch, "E1494", {"start": v(-9.03, 322.04) * mm, "end": v(-9.02, 321.52) * mm});
            skLineSegment(sketch, "E1495", {"start": v(-9.02, 321.52) * mm, "end": v(-9.03, 321) * mm});
            skLineSegment(sketch, "E1496", {"start": v(-9.03, 321) * mm, "end": v(-9.05, 320.5) * mm});
            skLineSegment(sketch, "E1497", {"start": v(-9.05, 320.5) * mm, "end": v(-9.08, 319.98) * mm});
            skLineSegment(sketch, "E1498", {"start": v(-9.08, 319.98) * mm, "end": v(-9.12, 319.48) * mm});
            skLineSegment(sketch, "E1499", {"start": v(-9.12, 319.48) * mm, "end": v(-9.18, 318.97) * mm});
            skLineSegment(sketch, "E1500", {"start": v(-9.18, 318.97) * mm, "end": v(-9.24, 318.46) * mm});
            skLineSegment(sketch, "E1501", {"start": v(-9.24, 318.46) * mm, "end": v(-9.33, 317.96) * mm});
            skLineSegment(sketch, "E1502", {"start": v(-9.33, 317.96) * mm, "end": v(-9.42, 317.46) * mm});
            skLineSegment(sketch, "E1503", {"start": v(-9.42, 317.46) * mm, "end": v(-9.53, 316.96) * mm});
            skLineSegment(sketch, "E1504", {"start": v(-9.53, 316.96) * mm, "end": v(-9.64, 316.47) * mm});
            skLineSegment(sketch, "E1505", {"start": v(-9.64, 316.47) * mm, "end": v(-9.77, 315.98) * mm});
            skLineSegment(sketch, "E1506", {"start": v(-9.77, 315.98) * mm, "end": v(-9.92, 315.5) * mm});
            skLineSegment(sketch, "E1507", {"start": v(-9.92, 315.5) * mm, "end": v(-10.07, 315) * mm});
            skLineSegment(sketch, "E1508", {"start": v(-10.07, 315) * mm, "end": v(-10.24, 314.53) * mm});
            skLineSegment(sketch, "E1509", {"start": v(-10.24, 314.53) * mm, "end": v(-10.42, 314.05) * mm});
            skLineSegment(sketch, "E1510", {"start": v(-10.42, 314.05) * mm, "end": v(-10.6, 313.58) * mm});
            skLineSegment(sketch, "E1511", {"start": v(-10.6, 313.58) * mm, "end": v(-10.8, 313.12) * mm});
            skLineSegment(sketch, "E1512", {"start": v(-10.8, 313.12) * mm, "end": v(-11.02, 312.66) * mm});
            skLineSegment(sketch, "E1513", {"start": v(-11.02, 312.66) * mm, "end": v(-11.24, 312.2) * mm});
            skLineSegment(sketch, "E1514", {"start": v(-11.24, 312.2) * mm, "end": v(-11.48, 311.75) * mm});
            skLineSegment(sketch, "E1515", {"start": v(-11.48, 311.75) * mm, "end": v(-11.73, 311.3) * mm});
            skLineSegment(sketch, "E1516", {"start": v(-11.73, 311.3) * mm, "end": v(-11.98, 310.87) * mm});
            skLineSegment(sketch, "E1517", {"start": v(-11.98, 310.87) * mm, "end": v(-12.25, 310.44) * mm});
            skLineSegment(sketch, "E1518", {"start": v(-12.25, 310.44) * mm, "end": v(-12.53, 310.01) * mm});
            skLineSegment(sketch, "E1519", {"start": v(-12.53, 310.01) * mm, "end": v(-12.83, 309.6) * mm});
            skLineSegment(sketch, "E1520", {"start": v(-12.83, 309.6) * mm, "end": v(-13.13, 309.18) * mm});
            skLineSegment(sketch, "E1521", {"start": v(-13.13, 309.18) * mm, "end": v(-13.44, 308.78) * mm});
            skLineSegment(sketch, "E1522", {"start": v(-13.44, 308.78) * mm, "end": v(-13.76, 308.38) * mm});
            skLineSegment(sketch, "E1523", {"start": v(-13.76, 308.38) * mm, "end": v(-14.1, 307.99) * mm});
            skLineSegment(sketch, "E1524", {"start": v(-14.1, 307.99) * mm, "end": v(-14.44, 307.6) * mm});
            skLineSegment(sketch, "E1525", {"start": v(-14.44, 307.6) * mm, "end": v(-14.8, 307.23) * mm});
            skLineSegment(sketch, "E1526", {"start": v(-14.8, 307.23) * mm, "end": v(-15.09, 306.94) * mm});
            skLineSegment(sketch, "E1527", {"start": v(-15.09, 306.94) * mm, "end": v(-15.39, 306.66) * mm});
            skLineSegment(sketch, "E1528", {"start": v(-15.39, 306.66) * mm, "end": v(-15.7, 306.39) * mm});
            skLineSegment(sketch, "E1529", {"start": v(-15.7, 306.39) * mm, "end": v(-16, 306.12) * mm});
            skLineSegment(sketch, "E1530", {"start": v(-16, 306.12) * mm, "end": v(-16.33, 305.86) * mm});
            skLineSegment(sketch, "E1531", {"start": v(-16.33, 305.86) * mm, "end": v(-16.65, 305.61) * mm});
            skLineSegment(sketch, "E1532", {"start": v(-16.65, 305.61) * mm, "end": v(-16.99, 305.37) * mm});
            skLineSegment(sketch, "E1533", {"start": v(-16.99, 305.37) * mm, "end": v(-17.32, 305.14) * mm});
            skLineSegment(sketch, "E1534", {"start": v(-17.32, 305.14) * mm, "end": v(-17.66, 304.91) * mm});
            skLineSegment(sketch, "E1535", {"start": v(-17.66, 304.91) * mm, "end": v(-18.01, 304.7) * mm});
            skLineSegment(sketch, "E1536", {"start": v(-18.01, 304.7) * mm, "end": v(-18.36, 304.5) * mm});
            skLineSegment(sketch, "E1537", {"start": v(-18.36, 304.5) * mm, "end": v(-18.72, 304.3) * mm});
            skLineSegment(sketch, "E1538", {"start": v(-18.72, 304.3) * mm, "end": v(-19.08, 304.1) * mm});
            skLineSegment(sketch, "E1539", {"start": v(-19.08, 304.1) * mm, "end": v(-19.45, 303.93) * mm});
            skLineSegment(sketch, "E1540", {"start": v(-19.45, 303.93) * mm, "end": v(-19.82, 303.76) * mm});
            skLineSegment(sketch, "E1541", {"start": v(-19.82, 303.76) * mm, "end": v(-20.2, 303.6) * mm});
            skLineSegment(sketch, "E1542", {"start": v(-20.2, 303.6) * mm, "end": v(-20.57, 303.44) * mm});
            skLineSegment(sketch, "E1543", {"start": v(-20.57, 303.44) * mm, "end": v(-20.95, 303.3) * mm});
            skLineSegment(sketch, "E1544", {"start": v(-20.95, 303.3) * mm, "end": v(-21.34, 303.17) * mm});
            skLineSegment(sketch, "E1545", {"start": v(-21.34, 303.17) * mm, "end": v(-21.73, 303.04) * mm});
            skLineSegment(sketch, "E1546", {"start": v(-21.73, 303.04) * mm, "end": v(-22.12, 302.93) * mm});
            skLineSegment(sketch, "E1547", {"start": v(-22.12, 302.93) * mm, "end": v(-22.52, 302.83) * mm});
            skLineSegment(sketch, "E1548", {"start": v(-22.52, 302.83) * mm, "end": v(-22.91, 302.73) * mm});
            skLineSegment(sketch, "E1549", {"start": v(-22.91, 302.73) * mm, "end": v(-23.31, 302.65) * mm});
            skLineSegment(sketch, "E1550", {"start": v(-23.31, 302.65) * mm, "end": v(-23.72, 302.57) * mm});
            skLineSegment(sketch, "E1551", {"start": v(-23.72, 302.57) * mm, "end": v(-24.12, 302.5) * mm});
            skLineSegment(sketch, "E1552", {"start": v(-24.12, 302.5) * mm, "end": v(-24.53, 302.45) * mm});
            skLineSegment(sketch, "E1553", {"start": v(-24.53, 302.45) * mm, "end": v(-24.94, 302.4) * mm});
            skLineSegment(sketch, "E1554", {"start": v(-24.94, 302.4) * mm, "end": v(-25.35, 302.38) * mm});
            skLineSegment(sketch, "E1555", {"start": v(-25.35, 302.38) * mm, "end": v(-25.76, 302.35) * mm});
            skLineSegment(sketch, "E1556", {"start": v(-25.76, 302.35) * mm, "end": v(-26.17, 302.34) * mm});
            skLineSegment(sketch, "E1557", {"start": v(-26.17, 302.34) * mm, "end": v(-26.58, 302.34) * mm});
            skLineSegment(sketch, "E1558", {"start": v(17.66, 302.34) * mm, "end": v(17.24, 302.33) * mm});
            skLineSegment(sketch, "E1559", {"start": v(17.24, 302.33) * mm, "end": v(16.82, 302.34) * mm});
            skLineSegment(sketch, "E1560", {"start": v(16.82, 302.34) * mm, "end": v(16.4, 302.36) * mm});
            skLineSegment(sketch, "E1561", {"start": v(16.4, 302.36) * mm, "end": v(15.99, 302.39) * mm});
            skLineSegment(sketch, "E1562", {"start": v(15.99, 302.39) * mm, "end": v(15.57, 302.42) * mm});
            skLineSegment(sketch, "E1563", {"start": v(15.57, 302.42) * mm, "end": v(15.16, 302.47) * mm});
            skLineSegment(sketch, "E1564", {"start": v(15.16, 302.47) * mm, "end": v(14.75, 302.53) * mm});
            skLineSegment(sketch, "E1565", {"start": v(14.75, 302.53) * mm, "end": v(14.34, 302.6) * mm});
            skLineSegment(sketch, "E1566", {"start": v(14.34, 302.6) * mm, "end": v(13.93, 302.68) * mm});
            skLineSegment(sketch, "E1567", {"start": v(13.93, 302.68) * mm, "end": v(13.53, 302.77) * mm});
            skLineSegment(sketch, "E1568", {"start": v(13.53, 302.77) * mm, "end": v(13.12, 302.87) * mm});
            skLineSegment(sketch, "E1569", {"start": v(13.12, 302.87) * mm, "end": v(12.72, 302.98) * mm});
            skLineSegment(sketch, "E1570", {"start": v(12.72, 302.98) * mm, "end": v(12.33, 303.1) * mm});
            skLineSegment(sketch, "E1571", {"start": v(12.33, 303.1) * mm, "end": v(11.93, 303.23) * mm});
            skLineSegment(sketch, "E1572", {"start": v(11.93, 303.23) * mm, "end": v(11.55, 303.37) * mm});
            skLineSegment(sketch, "E1573", {"start": v(11.55, 303.37) * mm, "end": v(11.16, 303.52) * mm});
            skLineSegment(sketch, "E1574", {"start": v(11.16, 303.52) * mm, "end": v(10.78, 303.67) * mm});
            skLineSegment(sketch, "E1575", {"start": v(10.78, 303.67) * mm, "end": v(10.4, 303.84) * mm});
            skLineSegment(sketch, "E1576", {"start": v(10.4, 303.84) * mm, "end": v(10.02, 304.02) * mm});
            skLineSegment(sketch, "E1577", {"start": v(10.02, 304.02) * mm, "end": v(9.65, 304.2) * mm});
            skLineSegment(sketch, "E1578", {"start": v(9.65, 304.2) * mm, "end": v(9.29, 304.4) * mm});
            skLineSegment(sketch, "E1579", {"start": v(9.29, 304.4) * mm, "end": v(8.93, 304.6) * mm});
            skLineSegment(sketch, "E1580", {"start": v(8.93, 304.6) * mm, "end": v(8.57, 304.82) * mm});
            skLineSegment(sketch, "E1581", {"start": v(8.57, 304.82) * mm, "end": v(8.22, 305.04) * mm});
            skLineSegment(sketch, "E1582", {"start": v(8.22, 305.04) * mm, "end": v(7.88, 305.27) * mm});
            skLineSegment(sketch, "E1583", {"start": v(7.88, 305.27) * mm, "end": v(7.54, 305.5) * mm});
            skLineSegment(sketch, "E1584", {"start": v(7.54, 305.5) * mm, "end": v(7.2, 305.76) * mm});
            skLineSegment(sketch, "E1585", {"start": v(7.2, 305.76) * mm, "end": v(6.88, 306.02) * mm});
            skLineSegment(sketch, "E1586", {"start": v(6.88, 306.02) * mm, "end": v(6.55, 306.28) * mm});
            skLineSegment(sketch, "E1587", {"start": v(6.55, 306.28) * mm, "end": v(6.24, 306.56) * mm});
            skLineSegment(sketch, "E1588", {"start": v(6.24, 306.56) * mm, "end": v(5.93, 306.84) * mm});
            skLineSegment(sketch, "E1589", {"start": v(5.93, 306.84) * mm, "end": v(5.63, 307.13) * mm});
            skLineSegment(sketch, "E1590", {"start": v(5.63, 307.13) * mm, "end": v(5.28, 307.51) * mm});
            skLineSegment(sketch, "E1591", {"start": v(5.28, 307.51) * mm, "end": v(4.94, 307.9) * mm});
            skLineSegment(sketch, "E1592", {"start": v(4.94, 307.9) * mm, "end": v(4.6, 308.3) * mm});
            skLineSegment(sketch, "E1593", {"start": v(4.6, 308.3) * mm, "end": v(4.29, 308.7) * mm});
            skLineSegment(sketch, "E1594", {"start": v(4.29, 308.7) * mm, "end": v(3.98, 309.1) * mm});
            skLineSegment(sketch, "E1595", {"start": v(3.98, 309.1) * mm, "end": v(3.68, 309.53) * mm});
            skLineSegment(sketch, "E1596", {"start": v(3.68, 309.53) * mm, "end": v(3.4, 309.95) * mm});
            skLineSegment(sketch, "E1597", {"start": v(3.4, 309.95) * mm, "end": v(3.12, 310.38) * mm});
            skLineSegment(sketch, "E1598", {"start": v(3.12, 310.38) * mm, "end": v(2.86, 310.82) * mm});
            skLineSegment(sketch, "E1599", {"start": v(2.86, 310.82) * mm, "end": v(2.6, 311.26) * mm});
            skLineSegment(sketch, "E1600", {"start": v(2.6, 311.26) * mm, "end": v(2.36, 311.7) * mm});
            skLineSegment(sketch, "E1601", {"start": v(2.36, 311.7) * mm, "end": v(2.13, 312.16) * mm});
            skLineSegment(sketch, "E1602", {"start": v(2.13, 312.16) * mm, "end": v(1.91, 312.62) * mm});
            skLineSegment(sketch, "E1603", {"start": v(1.91, 312.62) * mm, "end": v(1.7, 313.09) * mm});
            skLineSegment(sketch, "E1604", {"start": v(1.7, 313.09) * mm, "end": v(1.5, 313.56) * mm});
            skLineSegment(sketch, "E1605", {"start": v(1.5, 313.56) * mm, "end": v(1.32, 314.03) * mm});
            skLineSegment(sketch, "E1606", {"start": v(1.32, 314.03) * mm, "end": v(1.15, 314.51) * mm});
            skLineSegment(sketch, "E1607", {"start": v(1.15, 314.51) * mm, "end": v(0.98, 315) * mm});
            skLineSegment(sketch, "E1608", {"start": v(0.98, 315) * mm, "end": v(0.83, 315.48) * mm});
            skLineSegment(sketch, "E1609", {"start": v(0.83, 315.48) * mm, "end": v(0.7, 315.97) * mm});
            skLineSegment(sketch, "E1610", {"start": v(0.7, 315.97) * mm, "end": v(0.57, 316.47) * mm});
            skLineSegment(sketch, "E1611", {"start": v(0.57, 316.47) * mm, "end": v(0.45, 316.96) * mm});
            skLineSegment(sketch, "E1612", {"start": v(0.45, 316.96) * mm, "end": v(0.35, 317.46) * mm});
            skLineSegment(sketch, "E1613", {"start": v(0.35, 317.46) * mm, "end": v(0.26, 317.97) * mm});
            skLineSegment(sketch, "E1614", {"start": v(0.26, 317.97) * mm, "end": v(0.19, 318.47) * mm});
            skLineSegment(sketch, "E1615", {"start": v(0.19, 318.47) * mm, "end": v(0.12, 318.98) * mm});
            skLineSegment(sketch, "E1616", {"start": v(0.12, 318.98) * mm, "end": v(0.07, 319.49) * mm});
            skLineSegment(sketch, "E1617", {"start": v(0.07, 319.49) * mm, "end": v(0.03, 320) * mm});
            skLineSegment(sketch, "E1618", {"start": v(0.03, 320) * mm, "end": v(0, 320.51) * mm});
            skLineSegment(sketch, "E1619", {"start": v(0, 320.51) * mm, "end": v(-0.01, 321.03) * mm});
            skLineSegment(sketch, "E1620", {"start": v(-0.01, 321.03) * mm, "end": v(-0.01, 321.54) * mm});
            skLineSegment(sketch, "E1621", {"start": v(-0.01, 321.54) * mm, "end": v(0, 322.06) * mm});
            skLineSegment(sketch, "E1622", {"start": v(0, 322.06) * mm, "end": v(-0.02, 322.62) * mm});
            skLineSegment(sketch, "E1623", {"start": v(-0.02, 322.62) * mm, "end": v(-0.02, 323.18) * mm});
            skLineSegment(sketch, "E1624", {"start": v(-0.02, 323.18) * mm, "end": v(0, 323.74) * mm});
            skLineSegment(sketch, "E1625", {"start": v(0, 323.74) * mm, "end": v(0.02, 324.3) * mm});
            skLineSegment(sketch, "E1626", {"start": v(0.02, 324.3) * mm, "end": v(0.06, 324.85) * mm});
            skLineSegment(sketch, "E1627", {"start": v(0.06, 324.85) * mm, "end": v(0.12, 325.4) * mm});
            skLineSegment(sketch, "E1628", {"start": v(0.12, 325.4) * mm, "end": v(0.18, 325.96) * mm});
            skLineSegment(sketch, "E1629", {"start": v(0.18, 325.96) * mm, "end": v(0.27, 326.5) * mm});
            skLineSegment(sketch, "E1630", {"start": v(0.27, 326.5) * mm, "end": v(0.36, 327.06) * mm});
            skLineSegment(sketch, "E1631", {"start": v(0.36, 327.06) * mm, "end": v(0.47, 327.6) * mm});
            skLineSegment(sketch, "E1632", {"start": v(0.47, 327.6) * mm, "end": v(0.6, 328.14) * mm});
            skLineSegment(sketch, "E1633", {"start": v(0.6, 328.14) * mm, "end": v(0.73, 328.68) * mm});
            skLineSegment(sketch, "E1634", {"start": v(0.73, 328.68) * mm, "end": v(0.88, 329.2) * mm});
            skLineSegment(sketch, "E1635", {"start": v(0.88, 329.2) * mm, "end": v(1.04, 329.74) * mm});
            skLineSegment(sketch, "E1636", {"start": v(1.04, 329.74) * mm, "end": v(1.22, 330.26) * mm});
            skLineSegment(sketch, "E1637", {"start": v(1.22, 330.26) * mm, "end": v(1.4, 330.78) * mm});
            skLineSegment(sketch, "E1638", {"start": v(1.4, 330.78) * mm, "end": v(1.6, 331.3) * mm});
            skLineSegment(sketch, "E1639", {"start": v(1.6, 331.3) * mm, "end": v(1.82, 331.8) * mm});
            skLineSegment(sketch, "E1640", {"start": v(1.82, 331.8) * mm, "end": v(2.04, 332.31) * mm});
            skLineSegment(sketch, "E1641", {"start": v(2.04, 332.31) * mm, "end": v(2.28, 332.81) * mm});
            skLineSegment(sketch, "E1642", {"start": v(2.28, 332.81) * mm, "end": v(2.53, 333.3) * mm});
            skLineSegment(sketch, "E1643", {"start": v(2.53, 333.3) * mm, "end": v(2.8, 333.8) * mm});
            skLineSegment(sketch, "E1644", {"start": v(2.8, 333.8) * mm, "end": v(3.07, 334.27) * mm});
            skLineSegment(sketch, "E1645", {"start": v(3.07, 334.27) * mm, "end": v(3.36, 334.75) * mm});
            skLineSegment(sketch, "E1646", {"start": v(3.36, 334.75) * mm, "end": v(3.66, 335.21) * mm});
            skLineSegment(sketch, "E1647", {"start": v(3.66, 335.21) * mm, "end": v(3.97, 335.67) * mm});
            skLineSegment(sketch, "E1648", {"start": v(3.97, 335.67) * mm, "end": v(4.3, 336.13) * mm});
            skLineSegment(sketch, "E1649", {"start": v(4.3, 336.13) * mm, "end": v(4.63, 336.57) * mm});
            skLineSegment(sketch, "E1650", {"start": v(4.63, 336.57) * mm, "end": v(4.98, 337) * mm});
            skLineSegment(sketch, "E1651", {"start": v(4.98, 337) * mm, "end": v(5.34, 337.44) * mm});
            skLineSegment(sketch, "E1652", {"start": v(5.34, 337.44) * mm, "end": v(5.7, 337.86) * mm});
            skLineSegment(sketch, "E1653", {"start": v(5.7, 337.86) * mm, "end": v(6.1, 338.27) * mm});
            skLineSegment(sketch, "E1654", {"start": v(6.1, 338.27) * mm, "end": v(6.38, 338.56) * mm});
            skLineSegment(sketch, "E1655", {"start": v(6.38, 338.56) * mm, "end": v(6.67, 338.84) * mm});
            skLineSegment(sketch, "E1656", {"start": v(6.67, 338.84) * mm, "end": v(6.97, 339.12) * mm});
            skLineSegment(sketch, "E1657", {"start": v(6.97, 339.12) * mm, "end": v(7.27, 339.38) * mm});
            skLineSegment(sketch, "E1658", {"start": v(7.27, 339.38) * mm, "end": v(7.59, 339.64) * mm});
            skLineSegment(sketch, "E1659", {"start": v(7.59, 339.64) * mm, "end": v(7.9, 339.89) * mm});
            skLineSegment(sketch, "E1660", {"start": v(7.9, 339.89) * mm, "end": v(8.23, 340.13) * mm});
            skLineSegment(sketch, "E1661", {"start": v(8.23, 340.13) * mm, "end": v(8.56, 340.36) * mm});
            skLineSegment(sketch, "E1662", {"start": v(8.56, 340.36) * mm, "end": v(8.9, 340.58) * mm});
            skLineSegment(sketch, "E1663", {"start": v(8.9, 340.58) * mm, "end": v(9.23, 340.8) * mm});
            skLineSegment(sketch, "E1664", {"start": v(9.23, 340.8) * mm, "end": v(9.58, 341) * mm});
            skLineSegment(sketch, "E1665", {"start": v(9.58, 341) * mm, "end": v(9.93, 341.2) * mm});
            skLineSegment(sketch, "E1666", {"start": v(9.93, 341.2) * mm, "end": v(10.29, 341.38) * mm});
            skLineSegment(sketch, "E1667", {"start": v(10.29, 341.38) * mm, "end": v(10.64, 341.56) * mm});
            skLineSegment(sketch, "E1668", {"start": v(10.64, 341.56) * mm, "end": v(11, 341.73) * mm});
            skLineSegment(sketch, "E1669", {"start": v(11, 341.73) * mm, "end": v(11.38, 341.89) * mm});
            skLineSegment(sketch, "E1670", {"start": v(11.38, 341.89) * mm, "end": v(11.75, 342.04) * mm});
            skLineSegment(sketch, "E1671", {"start": v(11.75, 342.04) * mm, "end": v(12.12, 342.18) * mm});
            skLineSegment(sketch, "E1672", {"start": v(12.12, 342.18) * mm, "end": v(12.5, 342.3) * mm});
            skLineSegment(sketch, "E1673", {"start": v(12.5, 342.3) * mm, "end": v(12.89, 342.43) * mm});
            skLineSegment(sketch, "E1674", {"start": v(12.89, 342.43) * mm, "end": v(13.27, 342.54) * mm});
            skLineSegment(sketch, "E1675", {"start": v(13.27, 342.54) * mm, "end": v(13.66, 342.64) * mm});
            skLineSegment(sketch, "E1676", {"start": v(13.66, 342.64) * mm, "end": v(14.05, 342.73) * mm});
            skLineSegment(sketch, "E1677", {"start": v(14.05, 342.73) * mm, "end": v(14.45, 342.82) * mm});
            skLineSegment(sketch, "E1678", {"start": v(14.45, 342.82) * mm, "end": v(14.84, 342.89) * mm});
            skLineSegment(sketch, "E1679", {"start": v(14.84, 342.89) * mm, "end": v(15.24, 342.95) * mm});
            skLineSegment(sketch, "E1680", {"start": v(15.24, 342.95) * mm, "end": v(15.64, 343) * mm});
            skLineSegment(sketch, "E1681", {"start": v(15.64, 343) * mm, "end": v(16.05, 343.04) * mm});
            skLineSegment(sketch, "E1682", {"start": v(16.05, 343.04) * mm, "end": v(16.45, 343.07) * mm});
            skLineSegment(sketch, "E1683", {"start": v(16.45, 343.07) * mm, "end": v(16.86, 343.09) * mm});
            skLineSegment(sketch, "E1684", {"start": v(16.86, 343.09) * mm, "end": v(17.26, 343.1) * mm});
            skLineSegment(sketch, "E1685", {"start": v(17.26, 343.1) * mm, "end": v(17.67, 343.1) * mm});
            skLineSegment(sketch, "E1686", {"start": v(17.67, 343.1) * mm, "end": v(18.08, 343.1) * mm});
            skLineSegment(sketch, "E1687", {"start": v(18.08, 343.1) * mm, "end": v(18.5, 343.08) * mm});
            skLineSegment(sketch, "E1688", {"start": v(18.5, 343.08) * mm, "end": v(18.9, 343.05) * mm});
            skLineSegment(sketch, "E1689", {"start": v(18.9, 343.05) * mm, "end": v(19.32, 343.02) * mm});
            skLineSegment(sketch, "E1690", {"start": v(19.32, 343.02) * mm, "end": v(19.73, 342.97) * mm});
            skLineSegment(sketch, "E1691", {"start": v(19.73, 342.97) * mm, "end": v(20.13, 342.91) * mm});
            skLineSegment(sketch, "E1692", {"start": v(20.13, 342.91) * mm, "end": v(20.54, 342.85) * mm});
            skLineSegment(sketch, "E1693", {"start": v(20.54, 342.85) * mm, "end": v(20.94, 342.77) * mm});
            skLineSegment(sketch, "E1694", {"start": v(20.94, 342.77) * mm, "end": v(21.34, 342.68) * mm});
            skLineSegment(sketch, "E1695", {"start": v(21.34, 342.68) * mm, "end": v(21.74, 342.58) * mm});
            skLineSegment(sketch, "E1696", {"start": v(21.74, 342.58) * mm, "end": v(22.13, 342.48) * mm});
            skLineSegment(sketch, "E1697", {"start": v(22.13, 342.48) * mm, "end": v(22.52, 342.36) * mm});
            skLineSegment(sketch, "E1698", {"start": v(22.52, 342.36) * mm, "end": v(22.9, 342.23) * mm});
            skLineSegment(sketch, "E1699", {"start": v(22.9, 342.23) * mm, "end": v(23.3, 342.1) * mm});
            skLineSegment(sketch, "E1700", {"start": v(23.3, 342.1) * mm, "end": v(23.67, 341.95) * mm});
            skLineSegment(sketch, "E1701", {"start": v(23.67, 341.95) * mm, "end": v(24.05, 341.79) * mm});
            skLineSegment(sketch, "E1702", {"start": v(24.05, 341.79) * mm, "end": v(24.42, 341.62) * mm});
            skLineSegment(sketch, "E1703", {"start": v(24.42, 341.62) * mm, "end": v(24.8, 341.45) * mm});
            skLineSegment(sketch, "E1704", {"start": v(24.8, 341.45) * mm, "end": v(25.15, 341.26) * mm});
            skLineSegment(sketch, "E1705", {"start": v(25.15, 341.26) * mm, "end": v(25.51, 341.07) * mm});
            skLineSegment(sketch, "E1706", {"start": v(25.51, 341.07) * mm, "end": v(25.87, 340.86) * mm});
            skLineSegment(sketch, "E1707", {"start": v(25.87, 340.86) * mm, "end": v(26.22, 340.65) * mm});
            skLineSegment(sketch, "E1708", {"start": v(26.22, 340.65) * mm, "end": v(26.56, 340.43) * mm});
            skLineSegment(sketch, "E1709", {"start": v(26.56, 340.43) * mm, "end": v(26.9, 340.2) * mm});
            skLineSegment(sketch, "E1710", {"start": v(26.9, 340.2) * mm, "end": v(27.23, 339.96) * mm});
            skLineSegment(sketch, "E1711", {"start": v(27.23, 339.96) * mm, "end": v(27.56, 339.71) * mm});
            skLineSegment(sketch, "E1712", {"start": v(27.56, 339.71) * mm, "end": v(27.88, 339.46) * mm});
            skLineSegment(sketch, "E1713", {"start": v(27.88, 339.46) * mm, "end": v(28.19, 339.2) * mm});
            skLineSegment(sketch, "E1714", {"start": v(28.19, 339.2) * mm, "end": v(28.5, 338.92) * mm});
            skLineSegment(sketch, "E1715", {"start": v(28.5, 338.92) * mm, "end": v(28.8, 338.63) * mm});
            skLineSegment(sketch, "E1716", {"start": v(28.8, 338.63) * mm, "end": v(29.1, 338.34) * mm});
            skLineSegment(sketch, "E1717", {"start": v(29.1, 338.34) * mm, "end": v(29.38, 338.05) * mm});
            skLineSegment(sketch, "E1718", {"start": v(29.38, 338.05) * mm, "end": v(29.75, 337.64) * mm});
            skLineSegment(sketch, "E1719", {"start": v(29.75, 337.64) * mm, "end": v(30.1, 337.22) * mm});
            skLineSegment(sketch, "E1720", {"start": v(30.1, 337.22) * mm, "end": v(30.46, 336.8) * mm});
            skLineSegment(sketch, "E1721", {"start": v(30.46, 336.8) * mm, "end": v(30.8, 336.36) * mm});
            skLineSegment(sketch, "E1722", {"start": v(30.8, 336.36) * mm, "end": v(31.12, 335.92) * mm});
            skLineSegment(sketch, "E1723", {"start": v(31.12, 335.92) * mm, "end": v(31.43, 335.47) * mm});
            skLineSegment(sketch, "E1724", {"start": v(31.43, 335.47) * mm, "end": v(31.73, 335.01) * mm});
            skLineSegment(sketch, "E1725", {"start": v(31.73, 335.01) * mm, "end": v(32.02, 334.55) * mm});
            skLineSegment(sketch, "E1726", {"start": v(32.02, 334.55) * mm, "end": v(32.3, 334.08) * mm});
            skLineSegment(sketch, "E1727", {"start": v(32.3, 334.08) * mm, "end": v(32.57, 333.6) * mm});
            skLineSegment(sketch, "E1728", {"start": v(32.57, 333.6) * mm, "end": v(32.82, 333.12) * mm});
            skLineSegment(sketch, "E1729", {"start": v(32.82, 333.12) * mm, "end": v(33.06, 332.63) * mm});
            skLineSegment(sketch, "E1730", {"start": v(33.06, 332.63) * mm, "end": v(33.3, 332.14) * mm});
            skLineSegment(sketch, "E1731", {"start": v(33.3, 332.14) * mm, "end": v(33.5, 331.64) * mm});
            skLineSegment(sketch, "E1732", {"start": v(33.5, 331.64) * mm, "end": v(33.71, 331.14) * mm});
            skLineSegment(sketch, "E1733", {"start": v(33.71, 331.14) * mm, "end": v(33.9, 330.63) * mm});
            skLineSegment(sketch, "E1734", {"start": v(33.9, 330.63) * mm, "end": v(34.09, 330.11) * mm});
            skLineSegment(sketch, "E1735", {"start": v(34.09, 330.11) * mm, "end": v(34.25, 329.6) * mm});
            skLineSegment(sketch, "E1736", {"start": v(34.25, 329.6) * mm, "end": v(34.4, 329.08) * mm});
            skLineSegment(sketch, "E1737", {"start": v(34.4, 329.08) * mm, "end": v(34.55, 328.55) * mm});
            skLineSegment(sketch, "E1738", {"start": v(34.55, 328.55) * mm, "end": v(34.68, 328.02) * mm});
            skLineSegment(sketch, "E1739", {"start": v(34.68, 328.02) * mm, "end": v(34.8, 327.49) * mm});
            skLineSegment(sketch, "E1740", {"start": v(34.8, 327.49) * mm, "end": v(34.9, 326.95) * mm});
            skLineSegment(sketch, "E1741", {"start": v(34.9, 326.95) * mm, "end": v(34.99, 326.41) * mm});
            skLineSegment(sketch, "E1742", {"start": v(34.99, 326.41) * mm, "end": v(35.06, 325.87) * mm});
            skLineSegment(sketch, "E1743", {"start": v(35.06, 325.87) * mm, "end": v(35.12, 325.33) * mm});
            skLineSegment(sketch, "E1744", {"start": v(35.12, 325.33) * mm, "end": v(35.17, 324.79) * mm});
            skLineSegment(sketch, "E1745", {"start": v(35.17, 324.79) * mm, "end": v(35.2, 324.24) * mm});
            skLineSegment(sketch, "E1746", {"start": v(35.2, 324.24) * mm, "end": v(35.23, 323.69) * mm});
            skLineSegment(sketch, "E1747", {"start": v(35.23, 323.69) * mm, "end": v(35.24, 323.14) * mm});
            skLineSegment(sketch, "E1748", {"start": v(35.24, 323.14) * mm, "end": v(35.23, 322.59) * mm});
            skLineSegment(sketch, "E1749", {"start": v(35.23, 322.59) * mm, "end": v(35.21, 322.04) * mm});
            skLineSegment(sketch, "E1750", {"start": v(35.21, 322.04) * mm, "end": v(35.22, 321.52) * mm});
            skLineSegment(sketch, "E1751", {"start": v(35.22, 321.52) * mm, "end": v(35.22, 321) * mm});
            skLineSegment(sketch, "E1752", {"start": v(35.22, 321) * mm, "end": v(35.2, 320.5) * mm});
            skLineSegment(sketch, "E1753", {"start": v(35.2, 320.5) * mm, "end": v(35.17, 319.98) * mm});
            skLineSegment(sketch, "E1754", {"start": v(35.17, 319.98) * mm, "end": v(35.13, 319.48) * mm});
            skLineSegment(sketch, "E1755", {"start": v(35.13, 319.48) * mm, "end": v(35.07, 318.97) * mm});
            skLineSegment(sketch, "E1756", {"start": v(35.07, 318.97) * mm, "end": v(35, 318.46) * mm});
            skLineSegment(sketch, "E1757", {"start": v(35, 318.46) * mm, "end": v(34.92, 317.96) * mm});
            skLineSegment(sketch, "E1758", {"start": v(34.92, 317.96) * mm, "end": v(34.83, 317.46) * mm});
            skLineSegment(sketch, "E1759", {"start": v(34.83, 317.46) * mm, "end": v(34.72, 316.96) * mm});
            skLineSegment(sketch, "E1760", {"start": v(34.72, 316.96) * mm, "end": v(34.6, 316.47) * mm});
            skLineSegment(sketch, "E1761", {"start": v(34.6, 316.47) * mm, "end": v(34.47, 315.98) * mm});
            skLineSegment(sketch, "E1762", {"start": v(34.47, 315.98) * mm, "end": v(34.33, 315.5) * mm});
            skLineSegment(sketch, "E1763", {"start": v(34.33, 315.5) * mm, "end": v(34.17, 315) * mm});
            skLineSegment(sketch, "E1764", {"start": v(34.17, 315) * mm, "end": v(34, 314.53) * mm});
            skLineSegment(sketch, "E1765", {"start": v(34, 314.53) * mm, "end": v(33.83, 314.05) * mm});
            skLineSegment(sketch, "E1766", {"start": v(33.83, 314.05) * mm, "end": v(33.64, 313.58) * mm});
            skLineSegment(sketch, "E1767", {"start": v(33.64, 313.58) * mm, "end": v(33.44, 313.12) * mm});
            skLineSegment(sketch, "E1768", {"start": v(33.44, 313.12) * mm, "end": v(33.23, 312.66) * mm});
            skLineSegment(sketch, "E1769", {"start": v(33.23, 312.66) * mm, "end": v(33, 312.2) * mm});
            skLineSegment(sketch, "E1770", {"start": v(33, 312.2) * mm, "end": v(32.77, 311.75) * mm});
            skLineSegment(sketch, "E1771", {"start": v(32.77, 311.75) * mm, "end": v(32.52, 311.3) * mm});
            skLineSegment(sketch, "E1772", {"start": v(32.52, 311.3) * mm, "end": v(32.26, 310.87) * mm});
            skLineSegment(sketch, "E1773", {"start": v(32.26, 310.87) * mm, "end": v(32, 310.44) * mm});
            skLineSegment(sketch, "E1774", {"start": v(32, 310.44) * mm, "end": v(31.71, 310.01) * mm});
            skLineSegment(sketch, "E1775", {"start": v(31.71, 310.01) * mm, "end": v(31.42, 309.6) * mm});
            skLineSegment(sketch, "E1776", {"start": v(31.42, 309.6) * mm, "end": v(31.12, 309.18) * mm});
            skLineSegment(sketch, "E1777", {"start": v(31.12, 309.18) * mm, "end": v(30.8, 308.78) * mm});
            skLineSegment(sketch, "E1778", {"start": v(30.8, 308.78) * mm, "end": v(30.48, 308.38) * mm});
            skLineSegment(sketch, "E1779", {"start": v(30.48, 308.38) * mm, "end": v(30.15, 307.99) * mm});
            skLineSegment(sketch, "E1780", {"start": v(30.15, 307.99) * mm, "end": v(29.8, 307.6) * mm});
            skLineSegment(sketch, "E1781", {"start": v(29.8, 307.6) * mm, "end": v(29.45, 307.23) * mm});
            skLineSegment(sketch, "E1782", {"start": v(29.45, 307.23) * mm, "end": v(29.16, 306.94) * mm});
            skLineSegment(sketch, "E1783", {"start": v(29.16, 306.94) * mm, "end": v(28.86, 306.66) * mm});
            skLineSegment(sketch, "E1784", {"start": v(28.86, 306.66) * mm, "end": v(28.55, 306.39) * mm});
            skLineSegment(sketch, "E1785", {"start": v(28.55, 306.39) * mm, "end": v(28.24, 306.12) * mm});
            skLineSegment(sketch, "E1786", {"start": v(28.24, 306.12) * mm, "end": v(27.92, 305.86) * mm});
            skLineSegment(sketch, "E1787", {"start": v(27.92, 305.86) * mm, "end": v(27.6, 305.61) * mm});
            skLineSegment(sketch, "E1788", {"start": v(27.6, 305.61) * mm, "end": v(27.26, 305.37) * mm});
            skLineSegment(sketch, "E1789", {"start": v(27.26, 305.37) * mm, "end": v(26.92, 305.14) * mm});
            skLineSegment(sketch, "E1790", {"start": v(26.92, 305.14) * mm, "end": v(26.58, 304.91) * mm});
            skLineSegment(sketch, "E1791", {"start": v(26.58, 304.91) * mm, "end": v(26.23, 304.7) * mm});
            skLineSegment(sketch, "E1792", {"start": v(26.23, 304.7) * mm, "end": v(25.88, 304.5) * mm});
            skLineSegment(sketch, "E1793", {"start": v(25.88, 304.5) * mm, "end": v(25.52, 304.3) * mm});
            skLineSegment(sketch, "E1794", {"start": v(25.52, 304.3) * mm, "end": v(25.16, 304.1) * mm});
            skLineSegment(sketch, "E1795", {"start": v(25.16, 304.1) * mm, "end": v(24.8, 303.93) * mm});
            skLineSegment(sketch, "E1796", {"start": v(24.8, 303.93) * mm, "end": v(24.43, 303.76) * mm});
            skLineSegment(sketch, "E1797", {"start": v(24.43, 303.76) * mm, "end": v(24.05, 303.6) * mm});
            skLineSegment(sketch, "E1798", {"start": v(24.05, 303.6) * mm, "end": v(23.67, 303.44) * mm});
            skLineSegment(sketch, "E1799", {"start": v(23.67, 303.44) * mm, "end": v(23.3, 303.3) * mm});
            skLineSegment(sketch, "E1800", {"start": v(23.3, 303.3) * mm, "end": v(22.9, 303.17) * mm});
            skLineSegment(sketch, "E1801", {"start": v(22.9, 303.17) * mm, "end": v(22.52, 303.04) * mm});
            skLineSegment(sketch, "E1802", {"start": v(22.52, 303.04) * mm, "end": v(22.12, 302.93) * mm});
            skLineSegment(sketch, "E1803", {"start": v(22.12, 302.93) * mm, "end": v(21.73, 302.83) * mm});
            skLineSegment(sketch, "E1804", {"start": v(21.73, 302.83) * mm, "end": v(21.33, 302.73) * mm});
            skLineSegment(sketch, "E1805", {"start": v(21.33, 302.73) * mm, "end": v(20.93, 302.65) * mm});
            skLineSegment(sketch, "E1806", {"start": v(20.93, 302.65) * mm, "end": v(20.53, 302.57) * mm});
            skLineSegment(sketch, "E1807", {"start": v(20.53, 302.57) * mm, "end": v(20.12, 302.5) * mm});
            skLineSegment(sketch, "E1808", {"start": v(20.12, 302.5) * mm, "end": v(19.72, 302.45) * mm});
            skLineSegment(sketch, "E1809", {"start": v(19.72, 302.45) * mm, "end": v(19.3, 302.4) * mm});
            skLineSegment(sketch, "E1810", {"start": v(19.3, 302.4) * mm, "end": v(18.9, 302.38) * mm});
            skLineSegment(sketch, "E1811", {"start": v(18.9, 302.38) * mm, "end": v(18.49, 302.35) * mm});
            skLineSegment(sketch, "E1812", {"start": v(18.49, 302.35) * mm, "end": v(18.08, 302.34) * mm});
            skLineSegment(sketch, "E1813", {"start": v(18.08, 302.34) * mm, "end": v(17.66, 302.34) * mm});
            skLineSegment(sketch, "E1814", {"start": v(44.24, 302.9) * mm, "end": v(44.24, 342.86) * mm});
            skLineSegment(sketch, "E1815", {"start": v(44.24, 342.86) * mm, "end": v(61.8, 342.86) * mm});
            skLineSegment(sketch, "E1816", {"start": v(61.8, 342.86) * mm, "end": v(62.29, 342.85) * mm});
            skLineSegment(sketch, "E1817", {"start": v(62.29, 342.85) * mm, "end": v(62.78, 342.82) * mm});
            skLineSegment(sketch, "E1818", {"start": v(62.78, 342.82) * mm, "end": v(63.27, 342.77) * mm});
            skLineSegment(sketch, "E1819", {"start": v(63.27, 342.77) * mm, "end": v(63.75, 342.7) * mm});
            skLineSegment(sketch, "E1820", {"start": v(63.75, 342.7) * mm, "end": v(64.23, 342.59) * mm});
            skLineSegment(sketch, "E1821", {"start": v(64.23, 342.59) * mm, "end": v(64.7, 342.46) * mm});
            skLineSegment(sketch, "E1822", {"start": v(64.7, 342.46) * mm, "end": v(65.16, 342.3) * mm});
            skLineSegment(sketch, "E1823", {"start": v(65.16, 342.3) * mm, "end": v(65.62, 342.14) * mm});
            skLineSegment(sketch, "E1824", {"start": v(65.62, 342.14) * mm, "end": v(66.06, 341.94) * mm});
            skLineSegment(sketch, "E1825", {"start": v(66.06, 341.94) * mm, "end": v(66.5, 341.72) * mm});
            skLineSegment(sketch, "E1826", {"start": v(66.5, 341.72) * mm, "end": v(66.92, 341.48) * mm});
            skLineSegment(sketch, "E1827", {"start": v(66.92, 341.48) * mm, "end": v(67.33, 341.21) * mm});
            skLineSegment(sketch, "E1828", {"start": v(67.33, 341.21) * mm, "end": v(67.73, 340.93) * mm});
            skLineSegment(sketch, "E1829", {"start": v(67.73, 340.93) * mm, "end": v(68.11, 340.63) * mm});
            skLineSegment(sketch, "E1830", {"start": v(68.11, 340.63) * mm, "end": v(68.48, 340.3) * mm});
            skLineSegment(sketch, "E1831", {"start": v(68.48, 340.3) * mm, "end": v(68.84, 339.95) * mm});
            skLineSegment(sketch, "E1832", {"start": v(68.84, 339.95) * mm, "end": v(69.18, 339.6) * mm});
            skLineSegment(sketch, "E1833", {"start": v(69.18, 339.6) * mm, "end": v(69.5, 339.24) * mm});
            skLineSegment(sketch, "E1834", {"start": v(69.5, 339.24) * mm, "end": v(69.8, 338.85) * mm});
            skLineSegment(sketch, "E1835", {"start": v(69.8, 338.85) * mm, "end": v(70.08, 338.46) * mm});
            skLineSegment(sketch, "E1836", {"start": v(70.08, 338.46) * mm, "end": v(70.34, 338.05) * mm});
            skLineSegment(sketch, "E1837", {"start": v(70.34, 338.05) * mm, "end": v(70.58, 337.63) * mm});
            skLineSegment(sketch, "E1838", {"start": v(70.58, 337.63) * mm, "end": v(70.8, 337.2) * mm});
            skLineSegment(sketch, "E1839", {"start": v(70.8, 337.2) * mm, "end": v(71, 336.76) * mm});
            skLineSegment(sketch, "E1840", {"start": v(71, 336.76) * mm, "end": v(71.17, 336.31) * mm});
            skLineSegment(sketch, "E1841", {"start": v(71.17, 336.31) * mm, "end": v(71.33, 335.85) * mm});
            skLineSegment(sketch, "E1842", {"start": v(71.33, 335.85) * mm, "end": v(71.46, 335.39) * mm});
            skLineSegment(sketch, "E1843", {"start": v(71.46, 335.39) * mm, "end": v(71.56, 334.91) * mm});
            skLineSegment(sketch, "E1844", {"start": v(71.56, 334.91) * mm, "end": v(71.65, 334.44) * mm});
            skLineSegment(sketch, "E1845", {"start": v(71.65, 334.44) * mm, "end": v(71.7, 333.95) * mm});
            skLineSegment(sketch, "E1846", {"start": v(71.7, 333.95) * mm, "end": v(71.74, 333.47) * mm});
            skLineSegment(sketch, "E1847", {"start": v(71.74, 333.47) * mm, "end": v(71.75, 332.98) * mm});
            skLineSegment(sketch, "E1848", {"start": v(71.75, 332.98) * mm, "end": v(71.76, 332.48) * mm});
            skLineSegment(sketch, "E1849", {"start": v(71.76, 332.48) * mm, "end": v(71.73, 331.98) * mm});
            skLineSegment(sketch, "E1850", {"start": v(71.73, 331.98) * mm, "end": v(71.69, 331.48) * mm});
            skLineSegment(sketch, "E1851", {"start": v(71.69, 331.48) * mm, "end": v(71.61, 331) * mm});
            skLineSegment(sketch, "E1852", {"start": v(71.61, 331) * mm, "end": v(71.52, 330.5) * mm});
            skLineSegment(sketch, "E1853", {"start": v(71.52, 330.5) * mm, "end": v(71.4, 330.03) * mm});
            skLineSegment(sketch, "E1854", {"start": v(71.4, 330.03) * mm, "end": v(71.25, 329.55) * mm});
            skLineSegment(sketch, "E1855", {"start": v(71.25, 329.55) * mm, "end": v(71.08, 329.09) * mm});
            skLineSegment(sketch, "E1856", {"start": v(71.08, 329.09) * mm, "end": v(70.88, 328.63) * mm});
            skLineSegment(sketch, "E1857", {"start": v(70.88, 328.63) * mm, "end": v(70.67, 328.19) * mm});
            skLineSegment(sketch, "E1858", {"start": v(70.67, 328.19) * mm, "end": v(70.43, 327.76) * mm});
            skLineSegment(sketch, "E1859", {"start": v(70.43, 327.76) * mm, "end": v(70.17, 327.33) * mm});
            skLineSegment(sketch, "E1860", {"start": v(70.17, 327.33) * mm, "end": v(69.89, 326.92) * mm});
            skLineSegment(sketch, "E1861", {"start": v(69.89, 326.92) * mm, "end": v(69.59, 326.53) * mm});
            skLineSegment(sketch, "E1862", {"start": v(69.59, 326.53) * mm, "end": v(69.26, 326.15) * mm});
            skLineSegment(sketch, "E1863", {"start": v(69.26, 326.15) * mm, "end": v(68.92, 325.78) * mm});
            skLineSegment(sketch, "E1864", {"start": v(68.92, 325.78) * mm, "end": v(68.56, 325.44) * mm});
            skLineSegment(sketch, "E1865", {"start": v(68.56, 325.44) * mm, "end": v(68.18, 325.12) * mm});
            skLineSegment(sketch, "E1866", {"start": v(68.18, 325.12) * mm, "end": v(67.8, 324.81) * mm});
            skLineSegment(sketch, "E1867", {"start": v(67.8, 324.81) * mm, "end": v(67.39, 324.53) * mm});
            skLineSegment(sketch, "E1868", {"start": v(67.39, 324.53) * mm, "end": v(66.97, 324.27) * mm});
            skLineSegment(sketch, "E1869", {"start": v(66.97, 324.27) * mm, "end": v(66.54, 324.03) * mm});
            skLineSegment(sketch, "E1870", {"start": v(66.54, 324.03) * mm, "end": v(66.1, 323.8) * mm});
            skLineSegment(sketch, "E1871", {"start": v(66.1, 323.8) * mm, "end": v(65.65, 323.61) * mm});
            skLineSegment(sketch, "E1872", {"start": v(65.65, 323.61) * mm, "end": v(65.2, 323.44) * mm});
            skLineSegment(sketch, "E1873", {"start": v(65.2, 323.44) * mm, "end": v(64.72, 323.29) * mm});
            skLineSegment(sketch, "E1874", {"start": v(64.72, 323.29) * mm, "end": v(64.25, 323.16) * mm});
            skLineSegment(sketch, "E1875", {"start": v(64.25, 323.16) * mm, "end": v(63.77, 323.06) * mm});
            skLineSegment(sketch, "E1876", {"start": v(63.77, 323.06) * mm, "end": v(63.28, 322.98) * mm});
            skLineSegment(sketch, "E1877", {"start": v(63.28, 322.98) * mm, "end": v(62.79, 322.92) * mm});
            skLineSegment(sketch, "E1878", {"start": v(62.79, 322.92) * mm, "end": v(62.3, 322.9) * mm});
            skLineSegment(sketch, "E1879", {"start": v(62.3, 322.9) * mm, "end": v(61.8, 322.89) * mm});
            skLineSegment(sketch, "E1880", {"start": v(61.8, 322.89) * mm, "end": v(44.24, 322.89) * mm});
            skLineSegment(sketch, "E1881", {"start": v(61.8, 322.89) * mm, "end": v(62.2, 322.88) * mm});
            skLineSegment(sketch, "E1882", {"start": v(62.2, 322.88) * mm, "end": v(62.61, 322.86) * mm});
            skLineSegment(sketch, "E1883", {"start": v(62.61, 322.86) * mm, "end": v(63.02, 322.82) * mm});
            skLineSegment(sketch, "E1884", {"start": v(63.02, 322.82) * mm, "end": v(63.42, 322.75) * mm});
            skLineSegment(sketch, "E1885", {"start": v(63.42, 322.75) * mm, "end": v(63.81, 322.67) * mm});
            skLineSegment(sketch, "E1886", {"start": v(63.81, 322.67) * mm, "end": v(64.2, 322.56) * mm});
            skLineSegment(sketch, "E1887", {"start": v(64.2, 322.56) * mm, "end": v(64.59, 322.44) * mm});
            skLineSegment(sketch, "E1888", {"start": v(64.59, 322.44) * mm, "end": v(64.97, 322.3) * mm});
            skLineSegment(sketch, "E1889", {"start": v(64.97, 322.3) * mm, "end": v(65.34, 322.14) * mm});
            skLineSegment(sketch, "E1890", {"start": v(65.34, 322.14) * mm, "end": v(65.7, 321.96) * mm});
            skLineSegment(sketch, "E1891", {"start": v(65.7, 321.96) * mm, "end": v(66.05, 321.76) * mm});
            skLineSegment(sketch, "E1892", {"start": v(66.05, 321.76) * mm, "end": v(66.4, 321.54) * mm});
            skLineSegment(sketch, "E1893", {"start": v(66.4, 321.54) * mm, "end": v(66.72, 321.3) * mm});
            skLineSegment(sketch, "E1894", {"start": v(66.72, 321.3) * mm, "end": v(67.04, 321.05) * mm});
            skLineSegment(sketch, "E1895", {"start": v(67.04, 321.05) * mm, "end": v(67.35, 320.79) * mm});
            skLineSegment(sketch, "E1896", {"start": v(67.35, 320.79) * mm, "end": v(67.65, 320.5) * mm});
            skLineSegment(sketch, "E1897", {"start": v(67.65, 320.5) * mm, "end": v(67.99, 320) * mm});
            skLineSegment(sketch, "E1898", {"start": v(67.99, 320) * mm, "end": v(68.3, 319.49) * mm});
            skLineSegment(sketch, "E1899", {"start": v(68.3, 319.49) * mm, "end": v(68.6, 318.96) * mm});
            skLineSegment(sketch, "E1900", {"start": v(68.6, 318.96) * mm, "end": v(68.87, 318.43) * mm});
            skLineSegment(sketch, "E1901", {"start": v(68.87, 318.43) * mm, "end": v(69.11, 317.88) * mm});
            skLineSegment(sketch, "E1902", {"start": v(69.11, 317.88) * mm, "end": v(69.33, 317.32) * mm});
            skLineSegment(sketch, "E1903", {"start": v(69.33, 317.32) * mm, "end": v(69.52, 316.75) * mm});
            skLineSegment(sketch, "E1904", {"start": v(69.52, 316.75) * mm, "end": v(69.7, 316.18) * mm});
            skLineSegment(sketch, "E1905", {"start": v(69.7, 316.18) * mm, "end": v(69.84, 315.6) * mm});
            skLineSegment(sketch, "E1906", {"start": v(69.84, 315.6) * mm, "end": v(69.96, 315.01) * mm});
            skLineSegment(sketch, "E1907", {"start": v(69.96, 315.01) * mm, "end": v(70.05, 314.42) * mm});
            skLineSegment(sketch, "E1908", {"start": v(70.05, 314.42) * mm, "end": v(70.11, 313.82) * mm});
            skLineSegment(sketch, "E1909", {"start": v(70.11, 313.82) * mm, "end": v(70.15, 313.22) * mm});
            skLineSegment(sketch, "E1910", {"start": v(70.15, 313.22) * mm, "end": v(70.16, 312.62) * mm});
            skLineSegment(sketch, "E1911", {"start": v(70.16, 312.62) * mm, "end": v(70.15, 312.02) * mm});
            skLineSegment(sketch, "E1912", {"start": v(70.15, 312.02) * mm, "end": v(70.1, 311.42) * mm});
            skLineSegment(sketch, "E1913", {"start": v(70.1, 311.42) * mm, "end": v(70.1, 310.88) * mm});
            skLineSegment(sketch, "E1914", {"start": v(70.1, 310.88) * mm, "end": v(70.1, 310.34) * mm});
            skLineSegment(sketch, "E1915", {"start": v(70.1, 310.34) * mm, "end": v(70.11, 309.8) * mm});
            skLineSegment(sketch, "E1916", {"start": v(70.11, 309.8) * mm, "end": v(70.13, 309.26) * mm});
            skLineSegment(sketch, "E1917", {"start": v(70.13, 309.26) * mm, "end": v(70.16, 308.73) * mm});
            skLineSegment(sketch, "E1918", {"start": v(70.16, 308.73) * mm, "end": v(70.2, 308.19) * mm});
            skLineSegment(sketch, "E1919", {"start": v(70.2, 308.19) * mm, "end": v(70.25, 307.65) * mm});
            skLineSegment(sketch, "E1920", {"start": v(70.25, 307.65) * mm, "end": v(70.31, 307.12) * mm});
            skLineSegment(sketch, "E1921", {"start": v(70.31, 307.12) * mm, "end": v(70.38, 306.58) * mm});
            skLineSegment(sketch, "E1922", {"start": v(70.38, 306.58) * mm, "end": v(70.46, 306.05) * mm});
            skLineSegment(sketch, "E1923", {"start": v(70.46, 306.05) * mm, "end": v(70.55, 305.52) * mm});
            skLineSegment(sketch, "E1924", {"start": v(70.55, 305.52) * mm, "end": v(70.65, 305) * mm});
            skLineSegment(sketch, "E1925", {"start": v(70.65, 305) * mm, "end": v(70.76, 304.46) * mm});
            skLineSegment(sketch, "E1926", {"start": v(70.76, 304.46) * mm, "end": v(70.88, 303.94) * mm});
            skLineSegment(sketch, "E1927", {"start": v(70.88, 303.94) * mm, "end": v(71, 303.42) * mm});
            skLineSegment(sketch, "E1928", {"start": v(71, 303.42) * mm, "end": v(71.14, 302.9) * mm});
            skLineSegment(sketch, "E1929", {"start": v(107.35, 332.82) * mm, "end": v(107.4, 333.38) * mm});
            skLineSegment(sketch, "E1930", {"start": v(107.4, 333.38) * mm, "end": v(107.47, 333.94) * mm});
            skLineSegment(sketch, "E1931", {"start": v(107.47, 333.94) * mm, "end": v(107.57, 334.49) * mm});
            skLineSegment(sketch, "E1932", {"start": v(107.57, 334.49) * mm, "end": v(107.7, 335.03) * mm});
            skLineSegment(sketch, "E1933", {"start": v(107.7, 335.03) * mm, "end": v(107.85, 335.56) * mm});
            skLineSegment(sketch, "E1934", {"start": v(107.85, 335.56) * mm, "end": v(108.02, 336.08) * mm});
            skLineSegment(sketch, "E1935", {"start": v(108.02, 336.08) * mm, "end": v(108.22, 336.59) * mm});
            skLineSegment(sketch, "E1936", {"start": v(108.22, 336.59) * mm, "end": v(108.44, 337.08) * mm});
            skLineSegment(sketch, "E1937", {"start": v(108.44, 337.08) * mm, "end": v(108.68, 337.56) * mm});
            skLineSegment(sketch, "E1938", {"start": v(108.68, 337.56) * mm, "end": v(108.95, 338.03) * mm});
            skLineSegment(sketch, "E1939", {"start": v(108.95, 338.03) * mm, "end": v(109.23, 338.49) * mm});
            skLineSegment(sketch, "E1940", {"start": v(109.23, 338.49) * mm, "end": v(109.54, 338.93) * mm});
            skLineSegment(sketch, "E1941", {"start": v(109.54, 338.93) * mm, "end": v(109.86, 339.36) * mm});
            skLineSegment(sketch, "E1942", {"start": v(109.86, 339.36) * mm, "end": v(110.2, 339.77) * mm});
            skLineSegment(sketch, "E1943", {"start": v(110.2, 339.77) * mm, "end": v(110.57, 340.16) * mm});
            skLineSegment(sketch, "E1944", {"start": v(110.57, 340.16) * mm, "end": v(110.95, 340.54) * mm});
            skLineSegment(sketch, "E1945", {"start": v(110.95, 340.54) * mm, "end": v(111.35, 340.9) * mm});
            skLineSegment(sketch, "E1946", {"start": v(111.35, 340.9) * mm, "end": v(111.76, 341.23) * mm});
            skLineSegment(sketch, "E1947", {"start": v(111.76, 341.23) * mm, "end": v(112.2, 341.56) * mm});
            skLineSegment(sketch, "E1948", {"start": v(112.2, 341.56) * mm, "end": v(112.63, 341.86) * mm});
            skLineSegment(sketch, "E1949", {"start": v(112.63, 341.86) * mm, "end": v(113.1, 342.14) * mm});
            skLineSegment(sketch, "E1950", {"start": v(113.1, 342.14) * mm, "end": v(113.56, 342.4) * mm});
            skLineSegment(sketch, "E1951", {"start": v(113.56, 342.4) * mm, "end": v(114.05, 342.63) * mm});
            skLineSegment(sketch, "E1952", {"start": v(114.05, 342.63) * mm, "end": v(114.54, 342.85) * mm});
            skLineSegment(sketch, "E1953", {"start": v(114.54, 342.85) * mm, "end": v(115.05, 343.04) * mm});
            skLineSegment(sketch, "E1954", {"start": v(115.05, 343.04) * mm, "end": v(115.57, 343.21) * mm});
            skLineSegment(sketch, "E1955", {"start": v(115.57, 343.21) * mm, "end": v(116.1, 343.36) * mm});
            skLineSegment(sketch, "E1956", {"start": v(116.1, 343.36) * mm, "end": v(116.64, 343.48) * mm});
            skLineSegment(sketch, "E1957", {"start": v(116.64, 343.48) * mm, "end": v(117.18, 343.57) * mm});
            skLineSegment(sketch, "E1958", {"start": v(117.18, 343.57) * mm, "end": v(117.74, 343.64) * mm});
            skLineSegment(sketch, "E1959", {"start": v(117.74, 343.64) * mm, "end": v(118.3, 343.68) * mm});
            skLineSegment(sketch, "E1960", {"start": v(118.3, 343.68) * mm, "end": v(118.87, 343.7) * mm});
            skLineSegment(sketch, "E1961", {"start": v(118.87, 343.7) * mm, "end": v(119.83, 343.7) * mm});
            skLineSegment(sketch, "E1962", {"start": v(119.83, 343.7) * mm, "end": v(120.5, 343.68) * mm});
            skLineSegment(sketch, "E1963", {"start": v(120.5, 343.68) * mm, "end": v(121.14, 343.64) * mm});
            skLineSegment(sketch, "E1964", {"start": v(121.14, 343.64) * mm, "end": v(121.78, 343.58) * mm});
            skLineSegment(sketch, "E1965", {"start": v(121.78, 343.58) * mm, "end": v(122.41, 343.5) * mm});
            skLineSegment(sketch, "E1966", {"start": v(122.41, 343.5) * mm, "end": v(123.03, 343.38) * mm});
            skLineSegment(sketch, "E1967", {"start": v(123.03, 343.38) * mm, "end": v(123.64, 343.25) * mm});
            skLineSegment(sketch, "E1968", {"start": v(123.64, 343.25) * mm, "end": v(124.23, 343.1) * mm});
            skLineSegment(sketch, "E1969", {"start": v(124.23, 343.1) * mm, "end": v(124.81, 342.92) * mm});
            skLineSegment(sketch, "E1970", {"start": v(124.81, 342.92) * mm, "end": v(125.38, 342.72) * mm});
            skLineSegment(sketch, "E1971", {"start": v(125.38, 342.72) * mm, "end": v(125.93, 342.5) * mm});
            skLineSegment(sketch, "E1972", {"start": v(125.93, 342.5) * mm, "end": v(126.47, 342.26) * mm});
            skLineSegment(sketch, "E1973", {"start": v(126.47, 342.26) * mm, "end": v(126.99, 342) * mm});
            skLineSegment(sketch, "E1974", {"start": v(126.99, 342) * mm, "end": v(127.5, 341.72) * mm});
            skLineSegment(sketch, "E1975", {"start": v(127.5, 341.72) * mm, "end": v(127.97, 341.43) * mm});
            skLineSegment(sketch, "E1976", {"start": v(127.97, 341.43) * mm, "end": v(128.44, 341.12) * mm});
            skLineSegment(sketch, "E1977", {"start": v(128.44, 341.12) * mm, "end": v(128.88, 340.8) * mm});
            skLineSegment(sketch, "E1978", {"start": v(128.88, 340.8) * mm, "end": v(129.3, 340.45) * mm});
            skLineSegment(sketch, "E1979", {"start": v(129.3, 340.45) * mm, "end": v(129.7, 340.09) * mm});
            skLineSegment(sketch, "E1980", {"start": v(129.7, 340.09) * mm, "end": v(130.09, 339.71) * mm});
            skLineSegment(sketch, "E1981", {"start": v(130.09, 339.71) * mm, "end": v(130.45, 339.32) * mm});
            skLineSegment(sketch, "E1982", {"start": v(130.45, 339.32) * mm, "end": v(130.78, 338.92) * mm});
            skLineSegment(sketch, "E1983", {"start": v(130.78, 338.92) * mm, "end": v(131.09, 338.5) * mm});
            skLineSegment(sketch, "E1984", {"start": v(131.09, 338.5) * mm, "end": v(131.37, 338.08) * mm});
            skLineSegment(sketch, "E1985", {"start": v(131.37, 338.08) * mm, "end": v(131.63, 337.64) * mm});
            skLineSegment(sketch, "E1986", {"start": v(131.63, 337.64) * mm, "end": v(131.86, 337.19) * mm});
            skLineSegment(sketch, "E1987", {"start": v(131.86, 337.19) * mm, "end": v(131.96, 336.96) * mm});
            skLineSegment(sketch, "E1988", {"start": v(131.96, 336.96) * mm, "end": v(132.06, 336.73) * mm});
            skLineSegment(sketch, "E1989", {"start": v(132.06, 336.73) * mm, "end": v(132.15, 336.5) * mm});
            skLineSegment(sketch, "E1990", {"start": v(132.15, 336.5) * mm, "end": v(132.23, 336.25) * mm});
            skLineSegment(sketch, "E1991", {"start": v(132.23, 336.25) * mm, "end": v(132.3, 336.02) * mm});
            skLineSegment(sketch, "E1992", {"start": v(132.3, 336.02) * mm, "end": v(132.37, 335.77) * mm});
            skLineSegment(sketch, "E1993", {"start": v(132.37, 335.77) * mm, "end": v(132.43, 335.53) * mm});
            skLineSegment(sketch, "E1994", {"start": v(132.43, 335.53) * mm, "end": v(132.48, 335.29) * mm});
            skLineSegment(sketch, "E1995", {"start": v(132.48, 335.29) * mm, "end": v(132.53, 335.04) * mm});
            skLineSegment(sketch, "E1996", {"start": v(132.53, 335.04) * mm, "end": v(132.57, 334.79) * mm});
            skLineSegment(sketch, "E1997", {"start": v(132.57, 334.79) * mm, "end": v(132.6, 334.54) * mm});
            skLineSegment(sketch, "E1998", {"start": v(132.6, 334.54) * mm, "end": v(132.62, 334.29) * mm});
            skLineSegment(sketch, "E1999", {"start": v(132.62, 334.29) * mm, "end": v(132.63, 334.03) * mm});
            skLineSegment(sketch, "E2000", {"start": v(132.63, 334.03) * mm, "end": v(132.63, 333.78) * mm});
            skLineSegment(sketch, "E2001", {"start": v(132.63, 333.78) * mm, "end": v(132.63, 333.3) * mm});
            skLineSegment(sketch, "E2002", {"start": v(132.63, 333.3) * mm, "end": v(132.63, 333) * mm});
            skLineSegment(sketch, "E2003", {"start": v(132.63, 333) * mm, "end": v(132.62, 332.7) * mm});
            skLineSegment(sketch, "E2004", {"start": v(132.62, 332.7) * mm, "end": v(132.6, 332.41) * mm});
            skLineSegment(sketch, "E2005", {"start": v(132.6, 332.41) * mm, "end": v(132.57, 332.12) * mm});
            skLineSegment(sketch, "E2006", {"start": v(132.57, 332.12) * mm, "end": v(132.53, 331.83) * mm});
            skLineSegment(sketch, "E2007", {"start": v(132.53, 331.83) * mm, "end": v(132.49, 331.55) * mm});
            skLineSegment(sketch, "E2008", {"start": v(132.49, 331.55) * mm, "end": v(132.43, 331.26) * mm});
            skLineSegment(sketch, "E2009", {"start": v(132.43, 331.26) * mm, "end": v(132.37, 330.97) * mm});
            skLineSegment(sketch, "E2010", {"start": v(132.37, 330.97) * mm, "end": v(132.3, 330.7) * mm});
            skLineSegment(sketch, "E2011", {"start": v(132.3, 330.7) * mm, "end": v(132.23, 330.41) * mm});
            skLineSegment(sketch, "E2012", {"start": v(132.23, 330.41) * mm, "end": v(132.15, 330.13) * mm});
            skLineSegment(sketch, "E2013", {"start": v(132.15, 330.13) * mm, "end": v(132.06, 329.86) * mm});
            skLineSegment(sketch, "E2014", {"start": v(132.06, 329.86) * mm, "end": v(131.96, 329.59) * mm});
            skLineSegment(sketch, "E2015", {"start": v(131.96, 329.59) * mm, "end": v(131.85, 329.32) * mm});
            skLineSegment(sketch, "E2016", {"start": v(131.85, 329.32) * mm, "end": v(131.74, 329.05) * mm});
            skLineSegment(sketch, "E2017", {"start": v(131.74, 329.05) * mm, "end": v(131.62, 328.79) * mm});
            skLineSegment(sketch, "E2018", {"start": v(131.62, 328.79) * mm, "end": v(131.5, 328.53) * mm});
            skLineSegment(sketch, "E2019", {"start": v(131.5, 328.53) * mm, "end": v(131.36, 328.27) * mm});
            skLineSegment(sketch, "E2020", {"start": v(131.36, 328.27) * mm, "end": v(131.22, 328.02) * mm});
            skLineSegment(sketch, "E2021", {"start": v(131.22, 328.02) * mm, "end": v(131.07, 327.77) * mm});
            skLineSegment(sketch, "E2022", {"start": v(131.07, 327.77) * mm, "end": v(130.92, 327.52) * mm});
            skLineSegment(sketch, "E2023", {"start": v(130.92, 327.52) * mm, "end": v(130.76, 327.28) * mm});
            skLineSegment(sketch, "E2024", {"start": v(130.76, 327.28) * mm, "end": v(130.6, 327.04) * mm});
            skLineSegment(sketch, "E2025", {"start": v(130.6, 327.04) * mm, "end": v(130.42, 326.81) * mm});
            skLineSegment(sketch, "E2026", {"start": v(130.42, 326.81) * mm, "end": v(130.23, 326.58) * mm});
            skLineSegment(sketch, "E2027", {"start": v(130.23, 326.58) * mm, "end": v(130.05, 326.36) * mm});
            skLineSegment(sketch, "E2028", {"start": v(130.05, 326.36) * mm, "end": v(129.85, 326.14) * mm});
            skLineSegment(sketch, "E2029", {"start": v(129.85, 326.14) * mm, "end": v(129.65, 325.93) * mm});
            skLineSegment(sketch, "E2030", {"start": v(129.65, 325.93) * mm, "end": v(129.45, 325.72) * mm});
            skLineSegment(sketch, "E2031", {"start": v(129.45, 325.72) * mm, "end": v(129.24, 325.52) * mm});
            skLineSegment(sketch, "E2032", {"start": v(129.24, 325.52) * mm, "end": v(129.02, 325.33) * mm});
            skLineSegment(sketch, "E2033", {"start": v(129.02, 325.33) * mm, "end": v(128.8, 325.14) * mm});
            skLineSegment(sketch, "E2034", {"start": v(128.8, 325.14) * mm, "end": v(113.6, 315.22) * mm});
            skLineSegment(sketch, "E2035", {"start": v(113.6, 315.22) * mm, "end": v(113.2, 314.96) * mm});
            skLineSegment(sketch, "E2036", {"start": v(113.2, 314.96) * mm, "end": v(112.83, 314.68) * mm});
            skLineSegment(sketch, "E2037", {"start": v(112.83, 314.68) * mm, "end": v(112.47, 314.4) * mm});
            skLineSegment(sketch, "E2038", {"start": v(112.47, 314.4) * mm, "end": v(112.1, 314.1) * mm});
            skLineSegment(sketch, "E2039", {"start": v(112.1, 314.1) * mm, "end": v(111.76, 313.8) * mm});
            skLineSegment(sketch, "E2040", {"start": v(111.76, 313.8) * mm, "end": v(111.43, 313.5) * mm});
            skLineSegment(sketch, "E2041", {"start": v(111.43, 313.5) * mm, "end": v(111.1, 313.17) * mm});
            skLineSegment(sketch, "E2042", {"start": v(111.1, 313.17) * mm, "end": v(110.8, 312.84) * mm});
            skLineSegment(sketch, "E2043", {"start": v(110.8, 312.84) * mm, "end": v(110.49, 312.5) * mm});
            skLineSegment(sketch, "E2044", {"start": v(110.49, 312.5) * mm, "end": v(110.2, 312.15) * mm});
            skLineSegment(sketch, "E2045", {"start": v(110.2, 312.15) * mm, "end": v(109.91, 311.8) * mm});
            skLineSegment(sketch, "E2046", {"start": v(109.91, 311.8) * mm, "end": v(109.64, 311.43) * mm});
            skLineSegment(sketch, "E2047", {"start": v(109.64, 311.43) * mm, "end": v(109.39, 311.06) * mm});
            skLineSegment(sketch, "E2048", {"start": v(109.39, 311.06) * mm, "end": v(109.14, 310.68) * mm});
            skLineSegment(sketch, "E2049", {"start": v(109.14, 310.68) * mm, "end": v(108.9, 310.29) * mm});
            skLineSegment(sketch, "E2050", {"start": v(108.9, 310.29) * mm, "end": v(108.68, 309.9) * mm});
            skLineSegment(sketch, "E2051", {"start": v(108.68, 309.9) * mm, "end": v(108.47, 309.5) * mm});
            skLineSegment(sketch, "E2052", {"start": v(108.47, 309.5) * mm, "end": v(108.27, 309.09) * mm});
            skLineSegment(sketch, "E2053", {"start": v(108.27, 309.09) * mm, "end": v(108.09, 308.67) * mm});
            skLineSegment(sketch, "E2054", {"start": v(108.09, 308.67) * mm, "end": v(107.91, 308.26) * mm});
            skLineSegment(sketch, "E2055", {"start": v(107.91, 308.26) * mm, "end": v(107.75, 307.83) * mm});
            skLineSegment(sketch, "E2056", {"start": v(107.75, 307.83) * mm, "end": v(107.6, 307.4) * mm});
            skLineSegment(sketch, "E2057", {"start": v(107.6, 307.4) * mm, "end": v(107.47, 306.97) * mm});
            skLineSegment(sketch, "E2058", {"start": v(107.47, 306.97) * mm, "end": v(107.35, 306.53) * mm});
            skLineSegment(sketch, "E2059", {"start": v(107.35, 306.53) * mm, "end": v(107.24, 306.09) * mm});
            skLineSegment(sketch, "E2060", {"start": v(107.24, 306.09) * mm, "end": v(107.15, 305.64) * mm});
            skLineSegment(sketch, "E2061", {"start": v(107.15, 305.64) * mm, "end": v(107.06, 305.2) * mm});
            skLineSegment(sketch, "E2062", {"start": v(107.06, 305.2) * mm, "end": v(107, 304.74) * mm});
            skLineSegment(sketch, "E2063", {"start": v(107, 304.74) * mm, "end": v(106.94, 304.28) * mm});
            skLineSegment(sketch, "E2064", {"start": v(106.94, 304.28) * mm, "end": v(106.9, 303.82) * mm});
            skLineSegment(sketch, "E2065", {"start": v(106.9, 303.82) * mm, "end": v(106.88, 303.36) * mm});
            skLineSegment(sketch, "E2066", {"start": v(106.88, 303.36) * mm, "end": v(106.87, 302.9) * mm});
            skLineSegment(sketch, "E2067", {"start": v(106.87, 302.9) * mm, "end": v(133.43, 302.9) * mm});
            skLineSegment(sketch, "E2068", {"start": v(-45.24, -300.2) * mm, "end": v(-45.24, -260.2) * mm});
            skLineSegment(sketch, "E2069", {"start": v(-45.24, -260.2) * mm, "end": v(-20.37, -260.2) * mm});
            skLineSegment(sketch, "E2070", {"start": v(-45.24, -279.32) * mm, "end": v(-22.17, -279.32) * mm});
            skLineSegment(sketch, "E2071", {"start": v(11.92, -300.18) * mm, "end": v(-11.57, -300.18) * mm});
            skLineSegment(sketch, "E2072", {"start": v(-11.57, -300.18) * mm, "end": v(-11.57, -260.22) * mm});
            skLineSegment(sketch, "E2073", {"start": v(27.08, -300.74) * mm, "end": v(26.66, -300.74) * mm});
            skLineSegment(sketch, "E2074", {"start": v(26.66, -300.74) * mm, "end": v(26.24, -300.73) * mm});
            skLineSegment(sketch, "E2075", {"start": v(26.24, -300.73) * mm, "end": v(25.83, -300.71) * mm});
            skLineSegment(sketch, "E2076", {"start": v(25.83, -300.71) * mm, "end": v(25.41, -300.69) * mm});
            skLineSegment(sketch, "E2077", {"start": v(25.41, -300.69) * mm, "end": v(25, -300.65) * mm});
            skLineSegment(sketch, "E2078", {"start": v(25, -300.65) * mm, "end": v(24.58, -300.6) * mm});
            skLineSegment(sketch, "E2079", {"start": v(24.58, -300.6) * mm, "end": v(24.17, -300.54) * mm});
            skLineSegment(sketch, "E2080", {"start": v(24.17, -300.54) * mm, "end": v(23.76, -300.47) * mm});
            skLineSegment(sketch, "E2081", {"start": v(23.76, -300.47) * mm, "end": v(23.35, -300.39) * mm});
            skLineSegment(sketch, "E2082", {"start": v(23.35, -300.39) * mm, "end": v(22.95, -300.3) * mm});
            skLineSegment(sketch, "E2083", {"start": v(22.95, -300.3) * mm, "end": v(22.55, -300.2) * mm});
            skLineSegment(sketch, "E2084", {"start": v(22.55, -300.2) * mm, "end": v(22.15, -300.1) * mm});
            skLineSegment(sketch, "E2085", {"start": v(22.15, -300.1) * mm, "end": v(21.75, -299.97) * mm});
            skLineSegment(sketch, "E2086", {"start": v(21.75, -299.97) * mm, "end": v(21.36, -299.84) * mm});
            skLineSegment(sketch, "E2087", {"start": v(21.36, -299.84) * mm, "end": v(20.97, -299.7) * mm});
            skLineSegment(sketch, "E2088", {"start": v(20.97, -299.7) * mm, "end": v(20.58, -299.56) * mm});
            skLineSegment(sketch, "E2089", {"start": v(20.58, -299.56) * mm, "end": v(20.2, -299.4) * mm});
            skLineSegment(sketch, "E2090", {"start": v(20.2, -299.4) * mm, "end": v(19.82, -299.23) * mm});
            skLineSegment(sketch, "E2091", {"start": v(19.82, -299.23) * mm, "end": v(19.45, -299.05) * mm});
            skLineSegment(sketch, "E2092", {"start": v(19.45, -299.05) * mm, "end": v(19.08, -298.87) * mm});
            skLineSegment(sketch, "E2093", {"start": v(19.08, -298.87) * mm, "end": v(18.71, -298.67) * mm});
            skLineSegment(sketch, "E2094", {"start": v(18.71, -298.67) * mm, "end": v(18.35, -298.47) * mm});
            skLineSegment(sketch, "E2095", {"start": v(18.35, -298.47) * mm, "end": v(18, -298.26) * mm});
            skLineSegment(sketch, "E2096", {"start": v(18, -298.26) * mm, "end": v(17.64, -298.03) * mm});
            skLineSegment(sketch, "E2097", {"start": v(17.64, -298.03) * mm, "end": v(17.3, -297.8) * mm});
            skLineSegment(sketch, "E2098", {"start": v(17.3, -297.8) * mm, "end": v(16.96, -297.56) * mm});
            skLineSegment(sketch, "E2099", {"start": v(16.96, -297.56) * mm, "end": v(16.63, -297.31) * mm});
            skLineSegment(sketch, "E2100", {"start": v(16.63, -297.31) * mm, "end": v(16.3, -297.06) * mm});
            skLineSegment(sketch, "E2101", {"start": v(16.3, -297.06) * mm, "end": v(15.98, -296.8) * mm});
            skLineSegment(sketch, "E2102", {"start": v(15.98, -296.8) * mm, "end": v(15.66, -296.52) * mm});
            skLineSegment(sketch, "E2103", {"start": v(15.66, -296.52) * mm, "end": v(15.35, -296.23) * mm});
            skLineSegment(sketch, "E2104", {"start": v(15.35, -296.23) * mm, "end": v(15.05, -295.94) * mm});
            skLineSegment(sketch, "E2105", {"start": v(15.05, -295.94) * mm, "end": v(14.7, -295.56) * mm});
            skLineSegment(sketch, "E2106", {"start": v(14.7, -295.56) * mm, "end": v(14.36, -295.17) * mm});
            skLineSegment(sketch, "E2107", {"start": v(14.36, -295.17) * mm, "end": v(14.03, -294.78) * mm});
            skLineSegment(sketch, "E2108", {"start": v(14.03, -294.78) * mm, "end": v(13.71, -294.37) * mm});
            skLineSegment(sketch, "E2109", {"start": v(13.71, -294.37) * mm, "end": v(13.4, -293.96) * mm});
            skLineSegment(sketch, "E2110", {"start": v(13.4, -293.96) * mm, "end": v(13.1, -293.55) * mm});
            skLineSegment(sketch, "E2111", {"start": v(13.1, -293.55) * mm, "end": v(12.82, -293.12) * mm});
            skLineSegment(sketch, "E2112", {"start": v(12.82, -293.12) * mm, "end": v(12.54, -292.7) * mm});
            skLineSegment(sketch, "E2113", {"start": v(12.54, -292.7) * mm, "end": v(12.28, -292.25) * mm});
            skLineSegment(sketch, "E2114", {"start": v(12.28, -292.25) * mm, "end": v(12.03, -291.81) * mm});
            skLineSegment(sketch, "E2115", {"start": v(12.03, -291.81) * mm, "end": v(11.78, -291.36) * mm});
            skLineSegment(sketch, "E2116", {"start": v(11.78, -291.36) * mm, "end": v(11.55, -290.9) * mm});
            skLineSegment(sketch, "E2117", {"start": v(11.55, -290.9) * mm, "end": v(11.33, -290.45) * mm});
            skLineSegment(sketch, "E2118", {"start": v(11.33, -290.45) * mm, "end": v(11.12, -289.98) * mm});
            skLineSegment(sketch, "E2119", {"start": v(11.12, -289.98) * mm, "end": v(10.93, -289.51) * mm});
            skLineSegment(sketch, "E2120", {"start": v(10.93, -289.51) * mm, "end": v(10.74, -289.04) * mm});
            skLineSegment(sketch, "E2121", {"start": v(10.74, -289.04) * mm, "end": v(10.57, -288.56) * mm});
            skLineSegment(sketch, "E2122", {"start": v(10.57, -288.56) * mm, "end": v(10.4, -288.08) * mm});
            skLineSegment(sketch, "E2123", {"start": v(10.4, -288.08) * mm, "end": v(10.26, -287.6) * mm});
            skLineSegment(sketch, "E2124", {"start": v(10.26, -287.6) * mm, "end": v(10.12, -287.1) * mm});
            skLineSegment(sketch, "E2125", {"start": v(10.12, -287.1) * mm, "end": v(10, -286.6) * mm});
            skLineSegment(sketch, "E2126", {"start": v(10, -286.6) * mm, "end": v(9.88, -286.1) * mm});
            skLineSegment(sketch, "E2127", {"start": v(9.88, -286.1) * mm, "end": v(9.78, -285.6) * mm});
            skLineSegment(sketch, "E2128", {"start": v(9.78, -285.6) * mm, "end": v(9.69, -285.1) * mm});
            skLineSegment(sketch, "E2129", {"start": v(9.69, -285.1) * mm, "end": v(9.6, -284.6) * mm});
            skLineSegment(sketch, "E2130", {"start": v(9.6, -284.6) * mm, "end": v(9.54, -284.1) * mm});
            skLineSegment(sketch, "E2131", {"start": v(9.54, -284.1) * mm, "end": v(9.5, -283.58) * mm});
            skLineSegment(sketch, "E2132", {"start": v(9.5, -283.58) * mm, "end": v(9.45, -283.07) * mm});
            skLineSegment(sketch, "E2133", {"start": v(9.45, -283.07) * mm, "end": v(9.43, -282.56) * mm});
            skLineSegment(sketch, "E2134", {"start": v(9.43, -282.56) * mm, "end": v(9.41, -282.04) * mm});
            skLineSegment(sketch, "E2135", {"start": v(9.41, -282.04) * mm, "end": v(9.41, -281.53) * mm});
            skLineSegment(sketch, "E2136", {"start": v(9.41, -281.53) * mm, "end": v(9.42, -281.01) * mm});
            skLineSegment(sketch, "E2137", {"start": v(9.42, -281.01) * mm, "end": v(9.4, -280.45) * mm});
            skLineSegment(sketch, "E2138", {"start": v(9.4, -280.45) * mm, "end": v(9.4, -279.89) * mm});
            skLineSegment(sketch, "E2139", {"start": v(9.4, -279.89) * mm, "end": v(9.42, -279.33) * mm});
            skLineSegment(sketch, "E2140", {"start": v(9.42, -279.33) * mm, "end": v(9.44, -278.77) * mm});
            skLineSegment(sketch, "E2141", {"start": v(9.44, -278.77) * mm, "end": v(9.48, -278.22) * mm});
            skLineSegment(sketch, "E2142", {"start": v(9.48, -278.22) * mm, "end": v(9.54, -277.66) * mm});
            skLineSegment(sketch, "E2143", {"start": v(9.54, -277.66) * mm, "end": v(9.6, -277.11) * mm});
            skLineSegment(sketch, "E2144", {"start": v(9.6, -277.11) * mm, "end": v(9.69, -276.56) * mm});
            skLineSegment(sketch, "E2145", {"start": v(9.69, -276.56) * mm, "end": v(9.78, -276.02) * mm});
            skLineSegment(sketch, "E2146", {"start": v(9.78, -276.02) * mm, "end": v(9.9, -275.47) * mm});
            skLineSegment(sketch, "E2147", {"start": v(9.9, -275.47) * mm, "end": v(10.02, -274.93) * mm});
            skLineSegment(sketch, "E2148", {"start": v(10.02, -274.93) * mm, "end": v(10.15, -274.4) * mm});
            skLineSegment(sketch, "E2149", {"start": v(10.15, -274.4) * mm, "end": v(10.3, -273.86) * mm});
            skLineSegment(sketch, "E2150", {"start": v(10.3, -273.86) * mm, "end": v(10.46, -273.33) * mm});
            skLineSegment(sketch, "E2151", {"start": v(10.46, -273.33) * mm, "end": v(10.64, -272.8) * mm});
            skLineSegment(sketch, "E2152", {"start": v(10.64, -272.8) * mm, "end": v(10.83, -272.29) * mm});
            skLineSegment(sketch, "E2153", {"start": v(10.83, -272.29) * mm, "end": v(11.03, -271.77) * mm});
            skLineSegment(sketch, "E2154", {"start": v(11.03, -271.77) * mm, "end": v(11.24, -271.26) * mm});
            skLineSegment(sketch, "E2155", {"start": v(11.24, -271.26) * mm, "end": v(11.47, -270.76) * mm});
            skLineSegment(sketch, "E2156", {"start": v(11.47, -270.76) * mm, "end": v(11.7, -270.26) * mm});
            skLineSegment(sketch, "E2157", {"start": v(11.7, -270.26) * mm, "end": v(11.96, -269.77) * mm});
            skLineSegment(sketch, "E2158", {"start": v(11.96, -269.77) * mm, "end": v(12.22, -269.28) * mm});
            skLineSegment(sketch, "E2159", {"start": v(12.22, -269.28) * mm, "end": v(12.5, -268.8) * mm});
            skLineSegment(sketch, "E2160", {"start": v(12.5, -268.8) * mm, "end": v(12.78, -268.33) * mm});
            skLineSegment(sketch, "E2161", {"start": v(12.78, -268.33) * mm, "end": v(13.08, -267.86) * mm});
            skLineSegment(sketch, "E2162", {"start": v(13.08, -267.86) * mm, "end": v(13.4, -267.4) * mm});
            skLineSegment(sketch, "E2163", {"start": v(13.4, -267.4) * mm, "end": v(13.72, -266.95) * mm});
            skLineSegment(sketch, "E2164", {"start": v(13.72, -266.95) * mm, "end": v(14.06, -266.5) * mm});
            skLineSegment(sketch, "E2165", {"start": v(14.06, -266.5) * mm, "end": v(14.4, -266.06) * mm});
            skLineSegment(sketch, "E2166", {"start": v(14.4, -266.06) * mm, "end": v(14.76, -265.63) * mm});
            skLineSegment(sketch, "E2167", {"start": v(14.76, -265.63) * mm, "end": v(15.13, -265.21) * mm});
            skLineSegment(sketch, "E2168", {"start": v(15.13, -265.21) * mm, "end": v(15.51, -264.8) * mm});
            skLineSegment(sketch, "E2169", {"start": v(15.51, -264.8) * mm, "end": v(15.8, -264.51) * mm});
            skLineSegment(sketch, "E2170", {"start": v(15.8, -264.51) * mm, "end": v(16.1, -264.23) * mm});
            skLineSegment(sketch, "E2171", {"start": v(16.1, -264.23) * mm, "end": v(16.4, -263.96) * mm});
            skLineSegment(sketch, "E2172", {"start": v(16.4, -263.96) * mm, "end": v(16.7, -263.69) * mm});
            skLineSegment(sketch, "E2173", {"start": v(16.7, -263.69) * mm, "end": v(17, -263.43) * mm});
            skLineSegment(sketch, "E2174", {"start": v(17, -263.43) * mm, "end": v(17.33, -263.18) * mm});
            skLineSegment(sketch, "E2175", {"start": v(17.33, -263.18) * mm, "end": v(17.65, -262.94) * mm});
            skLineSegment(sketch, "E2176", {"start": v(17.65, -262.94) * mm, "end": v(17.98, -262.71) * mm});
            skLineSegment(sketch, "E2177", {"start": v(17.98, -262.71) * mm, "end": v(18.32, -262.49) * mm});
            skLineSegment(sketch, "E2178", {"start": v(18.32, -262.49) * mm, "end": v(18.66, -262.28) * mm});
            skLineSegment(sketch, "E2179", {"start": v(18.66, -262.28) * mm, "end": v(19, -262.07) * mm});
            skLineSegment(sketch, "E2180", {"start": v(19, -262.07) * mm, "end": v(19.35, -261.87) * mm});
            skLineSegment(sketch, "E2181", {"start": v(19.35, -261.87) * mm, "end": v(19.7, -261.69) * mm});
            skLineSegment(sketch, "E2182", {"start": v(19.7, -261.69) * mm, "end": v(20.07, -261.5) * mm});
            skLineSegment(sketch, "E2183", {"start": v(20.07, -261.5) * mm, "end": v(20.43, -261.34) * mm});
            skLineSegment(sketch, "E2184", {"start": v(20.43, -261.34) * mm, "end": v(20.8, -261.18) * mm});
            skLineSegment(sketch, "E2185", {"start": v(20.8, -261.18) * mm, "end": v(21.17, -261.03) * mm});
            skLineSegment(sketch, "E2186", {"start": v(21.17, -261.03) * mm, "end": v(21.55, -260.9) * mm});
            skLineSegment(sketch, "E2187", {"start": v(21.55, -260.9) * mm, "end": v(21.93, -260.76) * mm});
            skLineSegment(sketch, "E2188", {"start": v(21.93, -260.76) * mm, "end": v(22.3, -260.64) * mm});
            skLineSegment(sketch, "E2189", {"start": v(22.3, -260.64) * mm, "end": v(22.7, -260.53) * mm});
            skLineSegment(sketch, "E2190", {"start": v(22.7, -260.53) * mm, "end": v(23.08, -260.43) * mm});
            skLineSegment(sketch, "E2191", {"start": v(23.08, -260.43) * mm, "end": v(23.48, -260.34) * mm});
            skLineSegment(sketch, "E2192", {"start": v(23.48, -260.34) * mm, "end": v(23.87, -260.26) * mm});
            skLineSegment(sketch, "E2193", {"start": v(23.87, -260.26) * mm, "end": v(24.27, -260.19) * mm});
            skLineSegment(sketch, "E2194", {"start": v(24.27, -260.19) * mm, "end": v(24.67, -260.12) * mm});
            skLineSegment(sketch, "E2195", {"start": v(24.67, -260.12) * mm, "end": v(25.07, -260.07) * mm});
            skLineSegment(sketch, "E2196", {"start": v(25.07, -260.07) * mm, "end": v(25.47, -260.03) * mm});
            skLineSegment(sketch, "E2197", {"start": v(25.47, -260.03) * mm, "end": v(25.87, -260) * mm});
            skLineSegment(sketch, "E2198", {"start": v(25.87, -260) * mm, "end": v(26.28, -259.98) * mm});
            skLineSegment(sketch, "E2199", {"start": v(26.28, -259.98) * mm, "end": v(26.68, -259.97) * mm});
            skLineSegment(sketch, "E2200", {"start": v(26.68, -259.97) * mm, "end": v(27.1, -259.98) * mm});
            skLineSegment(sketch, "E2201", {"start": v(27.1, -259.98) * mm, "end": v(27.5, -259.98) * mm});
            skLineSegment(sketch, "E2202", {"start": v(27.5, -259.98) * mm, "end": v(27.92, -260) * mm});
            skLineSegment(sketch, "E2203", {"start": v(27.92, -260) * mm, "end": v(28.33, -260.02) * mm});
            skLineSegment(sketch, "E2204", {"start": v(28.33, -260.02) * mm, "end": v(28.74, -260.06) * mm});
            skLineSegment(sketch, "E2205", {"start": v(28.74, -260.06) * mm, "end": v(29.15, -260.1) * mm});
            skLineSegment(sketch, "E2206", {"start": v(29.15, -260.1) * mm, "end": v(29.56, -260.16) * mm});
            skLineSegment(sketch, "E2207", {"start": v(29.56, -260.16) * mm, "end": v(29.96, -260.23) * mm});
            skLineSegment(sketch, "E2208", {"start": v(29.96, -260.23) * mm, "end": v(30.36, -260.3) * mm});
            skLineSegment(sketch, "E2209", {"start": v(30.36, -260.3) * mm, "end": v(30.76, -260.4) * mm});
            skLineSegment(sketch, "E2210", {"start": v(30.76, -260.4) * mm, "end": v(31.16, -260.49) * mm});
            skLineSegment(sketch, "E2211", {"start": v(31.16, -260.49) * mm, "end": v(31.55, -260.6) * mm});
            skLineSegment(sketch, "E2212", {"start": v(31.55, -260.6) * mm, "end": v(31.94, -260.71) * mm});
            skLineSegment(sketch, "E2213", {"start": v(31.94, -260.71) * mm, "end": v(32.33, -260.84) * mm});
            skLineSegment(sketch, "E2214", {"start": v(32.33, -260.84) * mm, "end": v(32.72, -260.98) * mm});
            skLineSegment(sketch, "E2215", {"start": v(32.72, -260.98) * mm, "end": v(33.1, -261.13) * mm});
            skLineSegment(sketch, "E2216", {"start": v(33.1, -261.13) * mm, "end": v(33.47, -261.28) * mm});
            skLineSegment(sketch, "E2217", {"start": v(33.47, -261.28) * mm, "end": v(33.84, -261.45) * mm});
            skLineSegment(sketch, "E2218", {"start": v(33.84, -261.45) * mm, "end": v(34.21, -261.62) * mm});
            skLineSegment(sketch, "E2219", {"start": v(34.21, -261.62) * mm, "end": v(34.58, -261.8) * mm});
            skLineSegment(sketch, "E2220", {"start": v(34.58, -261.8) * mm, "end": v(34.93, -262) * mm});
            skLineSegment(sketch, "E2221", {"start": v(34.93, -262) * mm, "end": v(35.29, -262.2) * mm});
            skLineSegment(sketch, "E2222", {"start": v(35.29, -262.2) * mm, "end": v(35.64, -262.42) * mm});
            skLineSegment(sketch, "E2223", {"start": v(35.64, -262.42) * mm, "end": v(35.98, -262.64) * mm});
            skLineSegment(sketch, "E2224", {"start": v(35.98, -262.64) * mm, "end": v(36.32, -262.87) * mm});
            skLineSegment(sketch, "E2225", {"start": v(36.32, -262.87) * mm, "end": v(36.65, -263.11) * mm});
            skLineSegment(sketch, "E2226", {"start": v(36.65, -263.11) * mm, "end": v(36.98, -263.36) * mm});
            skLineSegment(sketch, "E2227", {"start": v(36.98, -263.36) * mm, "end": v(37.3, -263.62) * mm});
            skLineSegment(sketch, "E2228", {"start": v(37.3, -263.62) * mm, "end": v(37.61, -263.88) * mm});
            skLineSegment(sketch, "E2229", {"start": v(37.61, -263.88) * mm, "end": v(37.92, -264.15) * mm});
            skLineSegment(sketch, "E2230", {"start": v(37.92, -264.15) * mm, "end": v(38.22, -264.44) * mm});
            skLineSegment(sketch, "E2231", {"start": v(38.22, -264.44) * mm, "end": v(38.51, -264.73) * mm});
            skLineSegment(sketch, "E2232", {"start": v(38.51, -264.73) * mm, "end": v(38.8, -265.03) * mm});
            skLineSegment(sketch, "E2233", {"start": v(38.8, -265.03) * mm, "end": v(39.17, -265.44) * mm});
            skLineSegment(sketch, "E2234", {"start": v(39.17, -265.44) * mm, "end": v(39.53, -265.85) * mm});
            skLineSegment(sketch, "E2235", {"start": v(39.53, -265.85) * mm, "end": v(39.88, -266.28) * mm});
            skLineSegment(sketch, "E2236", {"start": v(39.88, -266.28) * mm, "end": v(40.21, -266.71) * mm});
            skLineSegment(sketch, "E2237", {"start": v(40.21, -266.71) * mm, "end": v(40.54, -267.16) * mm});
            skLineSegment(sketch, "E2238", {"start": v(40.54, -267.16) * mm, "end": v(40.85, -267.6) * mm});
            skLineSegment(sketch, "E2239", {"start": v(40.85, -267.6) * mm, "end": v(41.15, -268.06) * mm});
            skLineSegment(sketch, "E2240", {"start": v(41.15, -268.06) * mm, "end": v(41.44, -268.52) * mm});
            skLineSegment(sketch, "E2241", {"start": v(41.44, -268.52) * mm, "end": v(41.72, -269) * mm});
            skLineSegment(sketch, "E2242", {"start": v(41.72, -269) * mm, "end": v(41.99, -269.47) * mm});
            skLineSegment(sketch, "E2243", {"start": v(41.99, -269.47) * mm, "end": v(42.24, -269.95) * mm});
            skLineSegment(sketch, "E2244", {"start": v(42.24, -269.95) * mm, "end": v(42.48, -270.44) * mm});
            skLineSegment(sketch, "E2245", {"start": v(42.48, -270.44) * mm, "end": v(42.71, -270.93) * mm});
            skLineSegment(sketch, "E2246", {"start": v(42.71, -270.93) * mm, "end": v(42.93, -271.43) * mm});
            skLineSegment(sketch, "E2247", {"start": v(42.93, -271.43) * mm, "end": v(43.14, -271.93) * mm});
            skLineSegment(sketch, "E2248", {"start": v(43.14, -271.93) * mm, "end": v(43.33, -272.44) * mm});
            skLineSegment(sketch, "E2249", {"start": v(43.33, -272.44) * mm, "end": v(43.5, -272.96) * mm});
            skLineSegment(sketch, "E2250", {"start": v(43.5, -272.96) * mm, "end": v(43.68, -273.47) * mm});
            skLineSegment(sketch, "E2251", {"start": v(43.68, -273.47) * mm, "end": v(43.83, -274) * mm});
            skLineSegment(sketch, "E2252", {"start": v(43.83, -274) * mm, "end": v(43.97, -274.52) * mm});
            skLineSegment(sketch, "E2253", {"start": v(43.97, -274.52) * mm, "end": v(44.1, -275.05) * mm});
            skLineSegment(sketch, "E2254", {"start": v(44.1, -275.05) * mm, "end": v(44.22, -275.58) * mm});
            skLineSegment(sketch, "E2255", {"start": v(44.22, -275.58) * mm, "end": v(44.32, -276.12) * mm});
            skLineSegment(sketch, "E2256", {"start": v(44.32, -276.12) * mm, "end": v(44.4, -276.66) * mm});
            skLineSegment(sketch, "E2257", {"start": v(44.4, -276.66) * mm, "end": v(44.48, -277.2) * mm});
            skLineSegment(sketch, "E2258", {"start": v(44.48, -277.2) * mm, "end": v(44.55, -277.74) * mm});
            skLineSegment(sketch, "E2259", {"start": v(44.55, -277.74) * mm, "end": v(44.6, -278.29) * mm});
            skLineSegment(sketch, "E2260", {"start": v(44.6, -278.29) * mm, "end": v(44.63, -278.83) * mm});
            skLineSegment(sketch, "E2261", {"start": v(44.63, -278.83) * mm, "end": v(44.65, -279.38) * mm});
            skLineSegment(sketch, "E2262", {"start": v(44.65, -279.38) * mm, "end": v(44.66, -279.93) * mm});
            skLineSegment(sketch, "E2263", {"start": v(44.66, -279.93) * mm, "end": v(44.66, -280.48) * mm});
            skLineSegment(sketch, "E2264", {"start": v(44.66, -280.48) * mm, "end": v(44.64, -281.03) * mm});
            skLineSegment(sketch, "E2265", {"start": v(44.64, -281.03) * mm, "end": v(44.64, -281.55) * mm});
            skLineSegment(sketch, "E2266", {"start": v(44.64, -281.55) * mm, "end": v(44.64, -282.06) * mm});
            skLineSegment(sketch, "E2267", {"start": v(44.64, -282.06) * mm, "end": v(44.62, -282.58) * mm});
            skLineSegment(sketch, "E2268", {"start": v(44.62, -282.58) * mm, "end": v(44.6, -283.09) * mm});
            skLineSegment(sketch, "E2269", {"start": v(44.6, -283.09) * mm, "end": v(44.55, -283.6) * mm});
            skLineSegment(sketch, "E2270", {"start": v(44.55, -283.6) * mm, "end": v(44.5, -284.1) * mm});
            skLineSegment(sketch, "E2271", {"start": v(44.5, -284.1) * mm, "end": v(44.42, -284.6) * mm});
            skLineSegment(sketch, "E2272", {"start": v(44.42, -284.6) * mm, "end": v(44.34, -285.11) * mm});
            skLineSegment(sketch, "E2273", {"start": v(44.34, -285.11) * mm, "end": v(44.25, -285.61) * mm});
            skLineSegment(sketch, "E2274", {"start": v(44.25, -285.61) * mm, "end": v(44.14, -286.1) * mm});
            skLineSegment(sketch, "E2275", {"start": v(44.14, -286.1) * mm, "end": v(44.02, -286.6) * mm});
            skLineSegment(sketch, "E2276", {"start": v(44.02, -286.6) * mm, "end": v(43.9, -287.1) * mm});
            skLineSegment(sketch, "E2277", {"start": v(43.9, -287.1) * mm, "end": v(43.75, -287.58) * mm});
            skLineSegment(sketch, "E2278", {"start": v(43.75, -287.58) * mm, "end": v(43.6, -288.06) * mm});
            skLineSegment(sketch, "E2279", {"start": v(43.6, -288.06) * mm, "end": v(43.43, -288.54) * mm});
            skLineSegment(sketch, "E2280", {"start": v(43.43, -288.54) * mm, "end": v(43.25, -289.02) * mm});
            skLineSegment(sketch, "E2281", {"start": v(43.25, -289.02) * mm, "end": v(43.06, -289.49) * mm});
            skLineSegment(sketch, "E2282", {"start": v(43.06, -289.49) * mm, "end": v(42.86, -289.95) * mm});
            skLineSegment(sketch, "E2283", {"start": v(42.86, -289.95) * mm, "end": v(42.65, -290.42) * mm});
            skLineSegment(sketch, "E2284", {"start": v(42.65, -290.42) * mm, "end": v(42.42, -290.87) * mm});
            skLineSegment(sketch, "E2285", {"start": v(42.42, -290.87) * mm, "end": v(42.19, -291.32) * mm});
            skLineSegment(sketch, "E2286", {"start": v(42.19, -291.32) * mm, "end": v(41.94, -291.76) * mm});
            skLineSegment(sketch, "E2287", {"start": v(41.94, -291.76) * mm, "end": v(41.68, -292.2) * mm});
            skLineSegment(sketch, "E2288", {"start": v(41.68, -292.2) * mm, "end": v(41.41, -292.63) * mm});
            skLineSegment(sketch, "E2289", {"start": v(41.41, -292.63) * mm, "end": v(41.13, -293.06) * mm});
            skLineSegment(sketch, "E2290", {"start": v(41.13, -293.06) * mm, "end": v(40.84, -293.48) * mm});
            skLineSegment(sketch, "E2291", {"start": v(40.84, -293.48) * mm, "end": v(40.54, -293.9) * mm});
            skLineSegment(sketch, "E2292", {"start": v(40.54, -293.9) * mm, "end": v(40.23, -294.3) * mm});
            skLineSegment(sketch, "E2293", {"start": v(40.23, -294.3) * mm, "end": v(39.9, -294.7) * mm});
            skLineSegment(sketch, "E2294", {"start": v(39.9, -294.7) * mm, "end": v(39.57, -295.08) * mm});
            skLineSegment(sketch, "E2295", {"start": v(39.57, -295.08) * mm, "end": v(39.23, -295.46) * mm});
            skLineSegment(sketch, "E2296", {"start": v(39.23, -295.46) * mm, "end": v(38.87, -295.84) * mm});
            skLineSegment(sketch, "E2297", {"start": v(38.87, -295.84) * mm, "end": v(38.58, -296.13) * mm});
            skLineSegment(sketch, "E2298", {"start": v(38.58, -296.13) * mm, "end": v(38.28, -296.41) * mm});
            skLineSegment(sketch, "E2299", {"start": v(38.28, -296.41) * mm, "end": v(37.97, -296.69) * mm});
            skLineSegment(sketch, "E2300", {"start": v(37.97, -296.69) * mm, "end": v(37.66, -296.95) * mm});
            skLineSegment(sketch, "E2301", {"start": v(37.66, -296.95) * mm, "end": v(37.34, -297.21) * mm});
            skLineSegment(sketch, "E2302", {"start": v(37.34, -297.21) * mm, "end": v(37.01, -297.46) * mm});
            skLineSegment(sketch, "E2303", {"start": v(37.01, -297.46) * mm, "end": v(36.68, -297.7) * mm});
            skLineSegment(sketch, "E2304", {"start": v(36.68, -297.7) * mm, "end": v(36.35, -297.94) * mm});
            skLineSegment(sketch, "E2305", {"start": v(36.35, -297.94) * mm, "end": v(36, -298.16) * mm});
            skLineSegment(sketch, "E2306", {"start": v(36, -298.16) * mm, "end": v(35.66, -298.37) * mm});
            skLineSegment(sketch, "E2307", {"start": v(35.66, -298.37) * mm, "end": v(35.3, -298.58) * mm});
            skLineSegment(sketch, "E2308", {"start": v(35.3, -298.58) * mm, "end": v(34.95, -298.78) * mm});
            skLineSegment(sketch, "E2309", {"start": v(34.95, -298.78) * mm, "end": v(34.58, -298.97) * mm});
            skLineSegment(sketch, "E2310", {"start": v(34.58, -298.97) * mm, "end": v(34.22, -299.15) * mm});
            skLineSegment(sketch, "E2311", {"start": v(34.22, -299.15) * mm, "end": v(33.85, -299.32) * mm});
            skLineSegment(sketch, "E2312", {"start": v(33.85, -299.32) * mm, "end": v(33.47, -299.48) * mm});
            skLineSegment(sketch, "E2313", {"start": v(33.47, -299.48) * mm, "end": v(33.1, -299.63) * mm});
            skLineSegment(sketch, "E2314", {"start": v(33.1, -299.63) * mm, "end": v(32.71, -299.77) * mm});
            skLineSegment(sketch, "E2315", {"start": v(32.71, -299.77) * mm, "end": v(32.33, -299.9) * mm});
            skLineSegment(sketch, "E2316", {"start": v(32.33, -299.9) * mm, "end": v(31.94, -300.03) * mm});
            skLineSegment(sketch, "E2317", {"start": v(31.94, -300.03) * mm, "end": v(31.55, -300.14) * mm});
            skLineSegment(sketch, "E2318", {"start": v(31.55, -300.14) * mm, "end": v(31.15, -300.25) * mm});
            skLineSegment(sketch, "E2319", {"start": v(31.15, -300.25) * mm, "end": v(30.75, -300.34) * mm});
            skLineSegment(sketch, "E2320", {"start": v(30.75, -300.34) * mm, "end": v(30.35, -300.42) * mm});
            skLineSegment(sketch, "E2321", {"start": v(30.35, -300.42) * mm, "end": v(29.95, -300.5) * mm});
            skLineSegment(sketch, "E2322", {"start": v(29.95, -300.5) * mm, "end": v(29.55, -300.56) * mm});
            skLineSegment(sketch, "E2323", {"start": v(29.55, -300.56) * mm, "end": v(29.14, -300.62) * mm});
            skLineSegment(sketch, "E2324", {"start": v(29.14, -300.62) * mm, "end": v(28.73, -300.66) * mm});
            skLineSegment(sketch, "E2325", {"start": v(28.73, -300.66) * mm, "end": v(28.32, -300.7) * mm});
            skLineSegment(sketch, "E2326", {"start": v(28.32, -300.7) * mm, "end": v(27.91, -300.72) * mm});
            skLineSegment(sketch, "E2327", {"start": v(27.91, -300.72) * mm, "end": v(27.5, -300.73) * mm});
            skLineSegment(sketch, "E2328", {"start": v(27.5, -300.73) * mm, "end": v(27.08, -300.74) * mm});
            skLineSegment(sketch, "E2329", {"start": v(71.33, -300.74) * mm, "end": v(70.9, -300.74) * mm});
            skLineSegment(sketch, "E2330", {"start": v(70.9, -300.74) * mm, "end": v(70.5, -300.73) * mm});
            skLineSegment(sketch, "E2331", {"start": v(70.5, -300.73) * mm, "end": v(70.07, -300.71) * mm});
            skLineSegment(sketch, "E2332", {"start": v(70.07, -300.71) * mm, "end": v(69.66, -300.69) * mm});
            skLineSegment(sketch, "E2333", {"start": v(69.66, -300.69) * mm, "end": v(69.24, -300.65) * mm});
            skLineSegment(sketch, "E2334", {"start": v(69.24, -300.65) * mm, "end": v(68.83, -300.6) * mm});
            skLineSegment(sketch, "E2335", {"start": v(68.83, -300.6) * mm, "end": v(68.42, -300.54) * mm});
            skLineSegment(sketch, "E2336", {"start": v(68.42, -300.54) * mm, "end": v(68, -300.47) * mm});
            skLineSegment(sketch, "E2337", {"start": v(68, -300.47) * mm, "end": v(67.6, -300.39) * mm});
            skLineSegment(sketch, "E2338", {"start": v(67.6, -300.39) * mm, "end": v(67.2, -300.3) * mm});
            skLineSegment(sketch, "E2339", {"start": v(67.2, -300.3) * mm, "end": v(66.8, -300.2) * mm});
            skLineSegment(sketch, "E2340", {"start": v(66.8, -300.2) * mm, "end": v(66.4, -300.1) * mm});
            skLineSegment(sketch, "E2341", {"start": v(66.4, -300.1) * mm, "end": v(66, -299.97) * mm});
            skLineSegment(sketch, "E2342", {"start": v(66, -299.97) * mm, "end": v(65.6, -299.84) * mm});
            skLineSegment(sketch, "E2343", {"start": v(65.6, -299.84) * mm, "end": v(65.21, -299.7) * mm});
            skLineSegment(sketch, "E2344", {"start": v(65.21, -299.7) * mm, "end": v(64.83, -299.56) * mm});
            skLineSegment(sketch, "E2345", {"start": v(64.83, -299.56) * mm, "end": v(64.44, -299.4) * mm});
            skLineSegment(sketch, "E2346", {"start": v(64.44, -299.4) * mm, "end": v(64.07, -299.23) * mm});
            skLineSegment(sketch, "E2347", {"start": v(64.07, -299.23) * mm, "end": v(63.7, -299.05) * mm});
            skLineSegment(sketch, "E2348", {"start": v(63.7, -299.05) * mm, "end": v(63.32, -298.87) * mm});
            skLineSegment(sketch, "E2349", {"start": v(63.32, -298.87) * mm, "end": v(62.96, -298.67) * mm});
            skLineSegment(sketch, "E2350", {"start": v(62.96, -298.67) * mm, "end": v(62.6, -298.47) * mm});
            skLineSegment(sketch, "E2351", {"start": v(62.6, -298.47) * mm, "end": v(62.24, -298.26) * mm});
            skLineSegment(sketch, "E2352", {"start": v(62.24, -298.26) * mm, "end": v(61.89, -298.03) * mm});
            skLineSegment(sketch, "E2353", {"start": v(61.89, -298.03) * mm, "end": v(61.54, -297.8) * mm});
            skLineSegment(sketch, "E2354", {"start": v(61.54, -297.8) * mm, "end": v(61.2, -297.56) * mm});
            skLineSegment(sketch, "E2355", {"start": v(61.2, -297.56) * mm, "end": v(60.87, -297.31) * mm});
            skLineSegment(sketch, "E2356", {"start": v(60.87, -297.31) * mm, "end": v(60.54, -297.06) * mm});
            skLineSegment(sketch, "E2357", {"start": v(60.54, -297.06) * mm, "end": v(60.22, -296.8) * mm});
            skLineSegment(sketch, "E2358", {"start": v(60.22, -296.8) * mm, "end": v(59.9, -296.52) * mm});
            skLineSegment(sketch, "E2359", {"start": v(59.9, -296.52) * mm, "end": v(59.6, -296.23) * mm});
            skLineSegment(sketch, "E2360", {"start": v(59.6, -296.23) * mm, "end": v(59.3, -295.94) * mm});
            skLineSegment(sketch, "E2361", {"start": v(59.3, -295.94) * mm, "end": v(58.94, -295.56) * mm});
            skLineSegment(sketch, "E2362", {"start": v(58.94, -295.56) * mm, "end": v(58.6, -295.17) * mm});
            skLineSegment(sketch, "E2363", {"start": v(58.6, -295.17) * mm, "end": v(58.28, -294.78) * mm});
            skLineSegment(sketch, "E2364", {"start": v(58.28, -294.78) * mm, "end": v(57.96, -294.37) * mm});
            skLineSegment(sketch, "E2365", {"start": v(57.96, -294.37) * mm, "end": v(57.65, -293.96) * mm});
            skLineSegment(sketch, "E2366", {"start": v(57.65, -293.96) * mm, "end": v(57.35, -293.55) * mm});
            skLineSegment(sketch, "E2367", {"start": v(57.35, -293.55) * mm, "end": v(57.07, -293.12) * mm});
            skLineSegment(sketch, "E2368", {"start": v(57.07, -293.12) * mm, "end": v(56.79, -292.7) * mm});
            skLineSegment(sketch, "E2369", {"start": v(56.79, -292.7) * mm, "end": v(56.53, -292.25) * mm});
            skLineSegment(sketch, "E2370", {"start": v(56.53, -292.25) * mm, "end": v(56.27, -291.81) * mm});
            skLineSegment(sketch, "E2371", {"start": v(56.27, -291.81) * mm, "end": v(56.03, -291.36) * mm});
            skLineSegment(sketch, "E2372", {"start": v(56.03, -291.36) * mm, "end": v(55.8, -290.9) * mm});
            skLineSegment(sketch, "E2373", {"start": v(55.8, -290.9) * mm, "end": v(55.58, -290.45) * mm});
            skLineSegment(sketch, "E2374", {"start": v(55.58, -290.45) * mm, "end": v(55.37, -289.98) * mm});
            skLineSegment(sketch, "E2375", {"start": v(55.37, -289.98) * mm, "end": v(55.17, -289.51) * mm});
            skLineSegment(sketch, "E2376", {"start": v(55.17, -289.51) * mm, "end": v(54.99, -289.04) * mm});
            skLineSegment(sketch, "E2377", {"start": v(54.99, -289.04) * mm, "end": v(54.81, -288.56) * mm});
            skLineSegment(sketch, "E2378", {"start": v(54.81, -288.56) * mm, "end": v(54.65, -288.08) * mm});
            skLineSegment(sketch, "E2379", {"start": v(54.65, -288.08) * mm, "end": v(54.5, -287.6) * mm});
            skLineSegment(sketch, "E2380", {"start": v(54.5, -287.6) * mm, "end": v(54.36, -287.1) * mm});
            skLineSegment(sketch, "E2381", {"start": v(54.36, -287.1) * mm, "end": v(54.24, -286.6) * mm});
            skLineSegment(sketch, "E2382", {"start": v(54.24, -286.6) * mm, "end": v(54.12, -286.1) * mm});
            skLineSegment(sketch, "E2383", {"start": v(54.12, -286.1) * mm, "end": v(54.02, -285.6) * mm});
            skLineSegment(sketch, "E2384", {"start": v(54.02, -285.6) * mm, "end": v(53.93, -285.1) * mm});
            skLineSegment(sketch, "E2385", {"start": v(53.93, -285.1) * mm, "end": v(53.85, -284.6) * mm});
            skLineSegment(sketch, "E2386", {"start": v(53.85, -284.6) * mm, "end": v(53.79, -284.1) * mm});
            skLineSegment(sketch, "E2387", {"start": v(53.79, -284.1) * mm, "end": v(53.74, -283.58) * mm});
            skLineSegment(sketch, "E2388", {"start": v(53.74, -283.58) * mm, "end": v(53.7, -283.07) * mm});
            skLineSegment(sketch, "E2389", {"start": v(53.7, -283.07) * mm, "end": v(53.67, -282.56) * mm});
            skLineSegment(sketch, "E2390", {"start": v(53.67, -282.56) * mm, "end": v(53.66, -282.04) * mm});
            skLineSegment(sketch, "E2391", {"start": v(53.66, -282.04) * mm, "end": v(53.66, -281.53) * mm});
            skLineSegment(sketch, "E2392", {"start": v(53.66, -281.53) * mm, "end": v(53.67, -281.01) * mm});
            skLineSegment(sketch, "E2393", {"start": v(53.67, -281.01) * mm, "end": v(53.65, -280.45) * mm});
            skLineSegment(sketch, "E2394", {"start": v(53.65, -280.45) * mm, "end": v(53.65, -279.89) * mm});
            skLineSegment(sketch, "E2395", {"start": v(53.65, -279.89) * mm, "end": v(53.66, -279.33) * mm});
            skLineSegment(sketch, "E2396", {"start": v(53.66, -279.33) * mm, "end": v(53.69, -278.77) * mm});
            skLineSegment(sketch, "E2397", {"start": v(53.69, -278.77) * mm, "end": v(53.73, -278.22) * mm});
            skLineSegment(sketch, "E2398", {"start": v(53.73, -278.22) * mm, "end": v(53.78, -277.66) * mm});
            skLineSegment(sketch, "E2399", {"start": v(53.78, -277.66) * mm, "end": v(53.85, -277.11) * mm});
            skLineSegment(sketch, "E2400", {"start": v(53.85, -277.11) * mm, "end": v(53.93, -276.56) * mm});
            skLineSegment(sketch, "E2401", {"start": v(53.93, -276.56) * mm, "end": v(54.03, -276.02) * mm});
            skLineSegment(sketch, "E2402", {"start": v(54.03, -276.02) * mm, "end": v(54.14, -275.47) * mm});
            skLineSegment(sketch, "E2403", {"start": v(54.14, -275.47) * mm, "end": v(54.26, -274.93) * mm});
            skLineSegment(sketch, "E2404", {"start": v(54.26, -274.93) * mm, "end": v(54.4, -274.4) * mm});
            skLineSegment(sketch, "E2405", {"start": v(54.4, -274.4) * mm, "end": v(54.55, -273.86) * mm});
            skLineSegment(sketch, "E2406", {"start": v(54.55, -273.86) * mm, "end": v(54.7, -273.33) * mm});
            skLineSegment(sketch, "E2407", {"start": v(54.7, -273.33) * mm, "end": v(54.88, -272.8) * mm});
            skLineSegment(sketch, "E2408", {"start": v(54.88, -272.8) * mm, "end": v(55.07, -272.29) * mm});
            skLineSegment(sketch, "E2409", {"start": v(55.07, -272.29) * mm, "end": v(55.27, -271.77) * mm});
            skLineSegment(sketch, "E2410", {"start": v(55.27, -271.77) * mm, "end": v(55.49, -271.26) * mm});
            skLineSegment(sketch, "E2411", {"start": v(55.49, -271.26) * mm, "end": v(55.71, -270.76) * mm});
            skLineSegment(sketch, "E2412", {"start": v(55.71, -270.76) * mm, "end": v(55.95, -270.26) * mm});
            skLineSegment(sketch, "E2413", {"start": v(55.95, -270.26) * mm, "end": v(56.2, -269.77) * mm});
            skLineSegment(sketch, "E2414", {"start": v(56.2, -269.77) * mm, "end": v(56.47, -269.28) * mm});
            skLineSegment(sketch, "E2415", {"start": v(56.47, -269.28) * mm, "end": v(56.74, -268.8) * mm});
            skLineSegment(sketch, "E2416", {"start": v(56.74, -268.8) * mm, "end": v(57.03, -268.33) * mm});
            skLineSegment(sketch, "E2417", {"start": v(57.03, -268.33) * mm, "end": v(57.33, -267.86) * mm});
            skLineSegment(sketch, "E2418", {"start": v(57.33, -267.86) * mm, "end": v(57.64, -267.4) * mm});
            skLineSegment(sketch, "E2419", {"start": v(57.64, -267.4) * mm, "end": v(57.96, -266.95) * mm});
            skLineSegment(sketch, "E2420", {"start": v(57.96, -266.95) * mm, "end": v(58.3, -266.5) * mm});
            skLineSegment(sketch, "E2421", {"start": v(58.3, -266.5) * mm, "end": v(58.65, -266.06) * mm});
            skLineSegment(sketch, "E2422", {"start": v(58.65, -266.06) * mm, "end": v(59, -265.63) * mm});
            skLineSegment(sketch, "E2423", {"start": v(59, -265.63) * mm, "end": v(59.38, -265.21) * mm});
            skLineSegment(sketch, "E2424", {"start": v(59.38, -265.21) * mm, "end": v(59.76, -264.8) * mm});
            skLineSegment(sketch, "E2425", {"start": v(59.76, -264.8) * mm, "end": v(60.04, -264.51) * mm});
            skLineSegment(sketch, "E2426", {"start": v(60.04, -264.51) * mm, "end": v(60.34, -264.23) * mm});
            skLineSegment(sketch, "E2427", {"start": v(60.34, -264.23) * mm, "end": v(60.64, -263.96) * mm});
            skLineSegment(sketch, "E2428", {"start": v(60.64, -263.96) * mm, "end": v(60.94, -263.69) * mm});
            skLineSegment(sketch, "E2429", {"start": v(60.94, -263.69) * mm, "end": v(61.25, -263.43) * mm});
            skLineSegment(sketch, "E2430", {"start": v(61.25, -263.43) * mm, "end": v(61.57, -263.18) * mm});
            skLineSegment(sketch, "E2431", {"start": v(61.57, -263.18) * mm, "end": v(61.9, -262.94) * mm});
            skLineSegment(sketch, "E2432", {"start": v(61.9, -262.94) * mm, "end": v(62.23, -262.71) * mm});
            skLineSegment(sketch, "E2433", {"start": v(62.23, -262.71) * mm, "end": v(62.56, -262.49) * mm});
            skLineSegment(sketch, "E2434", {"start": v(62.56, -262.49) * mm, "end": v(62.9, -262.28) * mm});
            skLineSegment(sketch, "E2435", {"start": v(62.9, -262.28) * mm, "end": v(63.25, -262.07) * mm});
            skLineSegment(sketch, "E2436", {"start": v(63.25, -262.07) * mm, "end": v(63.6, -261.87) * mm});
            skLineSegment(sketch, "E2437", {"start": v(63.6, -261.87) * mm, "end": v(63.95, -261.69) * mm});
            skLineSegment(sketch, "E2438", {"start": v(63.95, -261.69) * mm, "end": v(64.31, -261.5) * mm});
            skLineSegment(sketch, "E2439", {"start": v(64.31, -261.5) * mm, "end": v(64.68, -261.34) * mm});
            skLineSegment(sketch, "E2440", {"start": v(64.68, -261.34) * mm, "end": v(65.04, -261.18) * mm});
            skLineSegment(sketch, "E2441", {"start": v(65.04, -261.18) * mm, "end": v(65.42, -261.03) * mm});
            skLineSegment(sketch, "E2442", {"start": v(65.42, -261.03) * mm, "end": v(65.8, -260.9) * mm});
            skLineSegment(sketch, "E2443", {"start": v(65.8, -260.9) * mm, "end": v(66.17, -260.76) * mm});
            skLineSegment(sketch, "E2444", {"start": v(66.17, -260.76) * mm, "end": v(66.55, -260.64) * mm});
            skLineSegment(sketch, "E2445", {"start": v(66.55, -260.64) * mm, "end": v(66.94, -260.53) * mm});
            skLineSegment(sketch, "E2446", {"start": v(66.94, -260.53) * mm, "end": v(67.33, -260.43) * mm});
            skLineSegment(sketch, "E2447", {"start": v(67.33, -260.43) * mm, "end": v(67.72, -260.34) * mm});
            skLineSegment(sketch, "E2448", {"start": v(67.72, -260.34) * mm, "end": v(68.12, -260.26) * mm});
            skLineSegment(sketch, "E2449", {"start": v(68.12, -260.26) * mm, "end": v(68.51, -260.19) * mm});
            skLineSegment(sketch, "E2450", {"start": v(68.51, -260.19) * mm, "end": v(68.91, -260.12) * mm});
            skLineSegment(sketch, "E2451", {"start": v(68.91, -260.12) * mm, "end": v(69.31, -260.07) * mm});
            skLineSegment(sketch, "E2452", {"start": v(69.31, -260.07) * mm, "end": v(69.71, -260.03) * mm});
            skLineSegment(sketch, "E2453", {"start": v(69.71, -260.03) * mm, "end": v(70.12, -260) * mm});
            skLineSegment(sketch, "E2454", {"start": v(70.12, -260) * mm, "end": v(70.52, -259.98) * mm});
            skLineSegment(sketch, "E2455", {"start": v(70.52, -259.98) * mm, "end": v(70.93, -259.97) * mm});
            skLineSegment(sketch, "E2456", {"start": v(70.93, -259.97) * mm, "end": v(71.34, -259.98) * mm});
            skLineSegment(sketch, "E2457", {"start": v(71.34, -259.98) * mm, "end": v(71.75, -259.98) * mm});
            skLineSegment(sketch, "E2458", {"start": v(71.75, -259.98) * mm, "end": v(72.16, -260) * mm});
            skLineSegment(sketch, "E2459", {"start": v(72.16, -260) * mm, "end": v(72.58, -260.02) * mm});
            skLineSegment(sketch, "E2460", {"start": v(72.58, -260.02) * mm, "end": v(72.99, -260.06) * mm});
            skLineSegment(sketch, "E2461", {"start": v(72.99, -260.06) * mm, "end": v(73.4, -260.1) * mm});
            skLineSegment(sketch, "E2462", {"start": v(73.4, -260.1) * mm, "end": v(73.8, -260.16) * mm});
            skLineSegment(sketch, "E2463", {"start": v(73.8, -260.16) * mm, "end": v(74.2, -260.23) * mm});
            skLineSegment(sketch, "E2464", {"start": v(74.2, -260.23) * mm, "end": v(74.6, -260.3) * mm});
            skLineSegment(sketch, "E2465", {"start": v(74.6, -260.3) * mm, "end": v(75, -260.4) * mm});
            skLineSegment(sketch, "E2466", {"start": v(75, -260.4) * mm, "end": v(75.4, -260.49) * mm});
            skLineSegment(sketch, "E2467", {"start": v(75.4, -260.49) * mm, "end": v(75.8, -260.6) * mm});
            skLineSegment(sketch, "E2468", {"start": v(75.8, -260.6) * mm, "end": v(76.19, -260.71) * mm});
            skLineSegment(sketch, "E2469", {"start": v(76.19, -260.71) * mm, "end": v(76.58, -260.84) * mm});
            skLineSegment(sketch, "E2470", {"start": v(76.58, -260.84) * mm, "end": v(76.96, -260.98) * mm});
            skLineSegment(sketch, "E2471", {"start": v(76.96, -260.98) * mm, "end": v(77.34, -261.13) * mm});
            skLineSegment(sketch, "E2472", {"start": v(77.34, -261.13) * mm, "end": v(77.72, -261.28) * mm});
            skLineSegment(sketch, "E2473", {"start": v(77.72, -261.28) * mm, "end": v(78.09, -261.45) * mm});
            skLineSegment(sketch, "E2474", {"start": v(78.09, -261.45) * mm, "end": v(78.46, -261.62) * mm});
            skLineSegment(sketch, "E2475", {"start": v(78.46, -261.62) * mm, "end": v(78.82, -261.8) * mm});
            skLineSegment(sketch, "E2476", {"start": v(78.82, -261.8) * mm, "end": v(79.18, -262) * mm});
            skLineSegment(sketch, "E2477", {"start": v(79.18, -262) * mm, "end": v(79.53, -262.2) * mm});
            skLineSegment(sketch, "E2478", {"start": v(79.53, -262.2) * mm, "end": v(79.88, -262.42) * mm});
            skLineSegment(sketch, "E2479", {"start": v(79.88, -262.42) * mm, "end": v(80.23, -262.64) * mm});
            skLineSegment(sketch, "E2480", {"start": v(80.23, -262.64) * mm, "end": v(80.56, -262.87) * mm});
            skLineSegment(sketch, "E2481", {"start": v(80.56, -262.87) * mm, "end": v(80.9, -263.11) * mm});
            skLineSegment(sketch, "E2482", {"start": v(80.9, -263.11) * mm, "end": v(81.22, -263.36) * mm});
            skLineSegment(sketch, "E2483", {"start": v(81.22, -263.36) * mm, "end": v(81.54, -263.62) * mm});
            skLineSegment(sketch, "E2484", {"start": v(81.54, -263.62) * mm, "end": v(81.86, -263.88) * mm});
            skLineSegment(sketch, "E2485", {"start": v(81.86, -263.88) * mm, "end": v(82.16, -264.15) * mm});
            skLineSegment(sketch, "E2486", {"start": v(82.16, -264.15) * mm, "end": v(82.47, -264.44) * mm});
            skLineSegment(sketch, "E2487", {"start": v(82.47, -264.44) * mm, "end": v(82.76, -264.73) * mm});
            skLineSegment(sketch, "E2488", {"start": v(82.76, -264.73) * mm, "end": v(83.05, -265.03) * mm});
            skLineSegment(sketch, "E2489", {"start": v(83.05, -265.03) * mm, "end": v(83.42, -265.44) * mm});
            skLineSegment(sketch, "E2490", {"start": v(83.42, -265.44) * mm, "end": v(83.78, -265.85) * mm});
            skLineSegment(sketch, "E2491", {"start": v(83.78, -265.85) * mm, "end": v(84.12, -266.28) * mm});
            skLineSegment(sketch, "E2492", {"start": v(84.12, -266.28) * mm, "end": v(84.46, -266.71) * mm});
            skLineSegment(sketch, "E2493", {"start": v(84.46, -266.71) * mm, "end": v(84.78, -267.16) * mm});
            skLineSegment(sketch, "E2494", {"start": v(84.78, -267.16) * mm, "end": v(85.1, -267.6) * mm});
            skLineSegment(sketch, "E2495", {"start": v(85.1, -267.6) * mm, "end": v(85.4, -268.06) * mm});
            skLineSegment(sketch, "E2496", {"start": v(85.4, -268.06) * mm, "end": v(85.69, -268.52) * mm});
            skLineSegment(sketch, "E2497", {"start": v(85.69, -268.52) * mm, "end": v(85.97, -269) * mm});
            skLineSegment(sketch, "E2498", {"start": v(85.97, -269) * mm, "end": v(86.23, -269.47) * mm});
            skLineSegment(sketch, "E2499", {"start": v(86.23, -269.47) * mm, "end": v(86.49, -269.95) * mm});
            skLineSegment(sketch, "E2500", {"start": v(86.49, -269.95) * mm, "end": v(86.73, -270.44) * mm});
            skLineSegment(sketch, "E2501", {"start": v(86.73, -270.44) * mm, "end": v(86.96, -270.93) * mm});
            skLineSegment(sketch, "E2502", {"start": v(86.96, -270.93) * mm, "end": v(87.18, -271.43) * mm});
            skLineSegment(sketch, "E2503", {"start": v(87.18, -271.43) * mm, "end": v(87.38, -271.93) * mm});
            skLineSegment(sketch, "E2504", {"start": v(87.38, -271.93) * mm, "end": v(87.57, -272.44) * mm});
            skLineSegment(sketch, "E2505", {"start": v(87.57, -272.44) * mm, "end": v(87.75, -272.96) * mm});
            skLineSegment(sketch, "E2506", {"start": v(87.75, -272.96) * mm, "end": v(87.92, -273.47) * mm});
            skLineSegment(sketch, "E2507", {"start": v(87.92, -273.47) * mm, "end": v(88.08, -274) * mm});
            skLineSegment(sketch, "E2508", {"start": v(88.08, -274) * mm, "end": v(88.22, -274.52) * mm});
            skLineSegment(sketch, "E2509", {"start": v(88.22, -274.52) * mm, "end": v(88.35, -275.05) * mm});
            skLineSegment(sketch, "E2510", {"start": v(88.35, -275.05) * mm, "end": v(88.46, -275.58) * mm});
            skLineSegment(sketch, "E2511", {"start": v(88.46, -275.58) * mm, "end": v(88.56, -276.12) * mm});
            skLineSegment(sketch, "E2512", {"start": v(88.56, -276.12) * mm, "end": v(88.65, -276.66) * mm});
            skLineSegment(sketch, "E2513", {"start": v(88.65, -276.66) * mm, "end": v(88.73, -277.2) * mm});
            skLineSegment(sketch, "E2514", {"start": v(88.73, -277.2) * mm, "end": v(88.8, -277.74) * mm});
            skLineSegment(sketch, "E2515", {"start": v(88.8, -277.74) * mm, "end": v(88.84, -278.29) * mm});
            skLineSegment(sketch, "E2516", {"start": v(88.84, -278.29) * mm, "end": v(88.88, -278.83) * mm});
            skLineSegment(sketch, "E2517", {"start": v(88.88, -278.83) * mm, "end": v(88.9, -279.38) * mm});
            skLineSegment(sketch, "E2518", {"start": v(88.9, -279.38) * mm, "end": v(88.9, -279.93) * mm});
            skLineSegment(sketch, "E2519", {"start": v(88.9, -279.93) * mm, "end": v(88.9, -280.48) * mm});
            skLineSegment(sketch, "E2520", {"start": v(88.9, -280.48) * mm, "end": v(88.88, -281.03) * mm});
            skLineSegment(sketch, "E2521", {"start": v(88.88, -281.03) * mm, "end": v(88.89, -281.55) * mm});
            skLineSegment(sketch, "E2522", {"start": v(88.89, -281.55) * mm, "end": v(88.88, -282.06) * mm});
            skLineSegment(sketch, "E2523", {"start": v(88.88, -282.06) * mm, "end": v(88.87, -282.58) * mm});
            skLineSegment(sketch, "E2524", {"start": v(88.87, -282.58) * mm, "end": v(88.84, -283.09) * mm});
            skLineSegment(sketch, "E2525", {"start": v(88.84, -283.09) * mm, "end": v(88.8, -283.6) * mm});
            skLineSegment(sketch, "E2526", {"start": v(88.8, -283.6) * mm, "end": v(88.74, -284.1) * mm});
            skLineSegment(sketch, "E2527", {"start": v(88.74, -284.1) * mm, "end": v(88.67, -284.6) * mm});
            skLineSegment(sketch, "E2528", {"start": v(88.67, -284.6) * mm, "end": v(88.59, -285.11) * mm});
            skLineSegment(sketch, "E2529", {"start": v(88.59, -285.11) * mm, "end": v(88.5, -285.61) * mm});
            skLineSegment(sketch, "E2530", {"start": v(88.5, -285.61) * mm, "end": v(88.39, -286.1) * mm});
            skLineSegment(sketch, "E2531", {"start": v(88.39, -286.1) * mm, "end": v(88.27, -286.6) * mm});
            skLineSegment(sketch, "E2532", {"start": v(88.27, -286.6) * mm, "end": v(88.14, -287.1) * mm});
            skLineSegment(sketch, "E2533", {"start": v(88.14, -287.1) * mm, "end": v(88, -287.58) * mm});
            skLineSegment(sketch, "E2534", {"start": v(88, -287.58) * mm, "end": v(87.84, -288.06) * mm});
            skLineSegment(sketch, "E2535", {"start": v(87.84, -288.06) * mm, "end": v(87.68, -288.54) * mm});
            skLineSegment(sketch, "E2536", {"start": v(87.68, -288.54) * mm, "end": v(87.5, -289.02) * mm});
            skLineSegment(sketch, "E2537", {"start": v(87.5, -289.02) * mm, "end": v(87.3, -289.49) * mm});
            skLineSegment(sketch, "E2538", {"start": v(87.3, -289.49) * mm, "end": v(87.1, -289.95) * mm});
            skLineSegment(sketch, "E2539", {"start": v(87.1, -289.95) * mm, "end": v(86.9, -290.42) * mm});
            skLineSegment(sketch, "E2540", {"start": v(86.9, -290.42) * mm, "end": v(86.67, -290.87) * mm});
            skLineSegment(sketch, "E2541", {"start": v(86.67, -290.87) * mm, "end": v(86.43, -291.32) * mm});
            skLineSegment(sketch, "E2542", {"start": v(86.43, -291.32) * mm, "end": v(86.19, -291.76) * mm});
            skLineSegment(sketch, "E2543", {"start": v(86.19, -291.76) * mm, "end": v(85.93, -292.2) * mm});
            skLineSegment(sketch, "E2544", {"start": v(85.93, -292.2) * mm, "end": v(85.66, -292.63) * mm});
            skLineSegment(sketch, "E2545", {"start": v(85.66, -292.63) * mm, "end": v(85.38, -293.06) * mm});
            skLineSegment(sketch, "E2546", {"start": v(85.38, -293.06) * mm, "end": v(85.09, -293.48) * mm});
            skLineSegment(sketch, "E2547", {"start": v(85.09, -293.48) * mm, "end": v(84.79, -293.9) * mm});
            skLineSegment(sketch, "E2548", {"start": v(84.79, -293.9) * mm, "end": v(84.47, -294.3) * mm});
            skLineSegment(sketch, "E2549", {"start": v(84.47, -294.3) * mm, "end": v(84.15, -294.7) * mm});
            skLineSegment(sketch, "E2550", {"start": v(84.15, -294.7) * mm, "end": v(83.82, -295.08) * mm});
            skLineSegment(sketch, "E2551", {"start": v(83.82, -295.08) * mm, "end": v(83.47, -295.46) * mm});
            skLineSegment(sketch, "E2552", {"start": v(83.47, -295.46) * mm, "end": v(83.12, -295.84) * mm});
            skLineSegment(sketch, "E2553", {"start": v(83.12, -295.84) * mm, "end": v(82.82, -296.13) * mm});
            skLineSegment(sketch, "E2554", {"start": v(82.82, -296.13) * mm, "end": v(82.52, -296.41) * mm});
            skLineSegment(sketch, "E2555", {"start": v(82.52, -296.41) * mm, "end": v(82.22, -296.69) * mm});
            skLineSegment(sketch, "E2556", {"start": v(82.22, -296.69) * mm, "end": v(81.9, -296.95) * mm});
            skLineSegment(sketch, "E2557", {"start": v(81.9, -296.95) * mm, "end": v(81.58, -297.21) * mm});
            skLineSegment(sketch, "E2558", {"start": v(81.58, -297.21) * mm, "end": v(81.26, -297.46) * mm});
            skLineSegment(sketch, "E2559", {"start": v(81.26, -297.46) * mm, "end": v(80.93, -297.7) * mm});
            skLineSegment(sketch, "E2560", {"start": v(80.93, -297.7) * mm, "end": v(80.6, -297.94) * mm});
            skLineSegment(sketch, "E2561", {"start": v(80.6, -297.94) * mm, "end": v(80.25, -298.16) * mm});
            skLineSegment(sketch, "E2562", {"start": v(80.25, -298.16) * mm, "end": v(79.9, -298.37) * mm});
            skLineSegment(sketch, "E2563", {"start": v(79.9, -298.37) * mm, "end": v(79.55, -298.58) * mm});
            skLineSegment(sketch, "E2564", {"start": v(79.55, -298.58) * mm, "end": v(79.2, -298.78) * mm});
            skLineSegment(sketch, "E2565", {"start": v(79.2, -298.78) * mm, "end": v(78.83, -298.97) * mm});
            skLineSegment(sketch, "E2566", {"start": v(78.83, -298.97) * mm, "end": v(78.46, -299.15) * mm});
            skLineSegment(sketch, "E2567", {"start": v(78.46, -299.15) * mm, "end": v(78.1, -299.32) * mm});
            skLineSegment(sketch, "E2568", {"start": v(78.1, -299.32) * mm, "end": v(77.72, -299.48) * mm});
            skLineSegment(sketch, "E2569", {"start": v(77.72, -299.48) * mm, "end": v(77.34, -299.63) * mm});
            skLineSegment(sketch, "E2570", {"start": v(77.34, -299.63) * mm, "end": v(76.96, -299.77) * mm});
            skLineSegment(sketch, "E2571", {"start": v(76.96, -299.77) * mm, "end": v(76.57, -299.9) * mm});
            skLineSegment(sketch, "E2572", {"start": v(76.57, -299.9) * mm, "end": v(76.18, -300.03) * mm});
            skLineSegment(sketch, "E2573", {"start": v(76.18, -300.03) * mm, "end": v(75.8, -300.14) * mm});
            skLineSegment(sketch, "E2574", {"start": v(75.8, -300.14) * mm, "end": v(75.4, -300.25) * mm});
            skLineSegment(sketch, "E2575", {"start": v(75.4, -300.25) * mm, "end": v(75, -300.34) * mm});
            skLineSegment(sketch, "E2576", {"start": v(75, -300.34) * mm, "end": v(74.6, -300.42) * mm});
            skLineSegment(sketch, "E2577", {"start": v(74.6, -300.42) * mm, "end": v(74.2, -300.5) * mm});
            skLineSegment(sketch, "E2578", {"start": v(74.2, -300.5) * mm, "end": v(73.8, -300.56) * mm});
            skLineSegment(sketch, "E2579", {"start": v(73.8, -300.56) * mm, "end": v(73.39, -300.62) * mm});
            skLineSegment(sketch, "E2580", {"start": v(73.39, -300.62) * mm, "end": v(72.98, -300.66) * mm});
            skLineSegment(sketch, "E2581", {"start": v(72.98, -300.66) * mm, "end": v(72.57, -300.7) * mm});
            skLineSegment(sketch, "E2582", {"start": v(72.57, -300.7) * mm, "end": v(72.16, -300.72) * mm});
            skLineSegment(sketch, "E2583", {"start": v(72.16, -300.72) * mm, "end": v(71.74, -300.73) * mm});
            skLineSegment(sketch, "E2584", {"start": v(71.74, -300.73) * mm, "end": v(71.33, -300.74) * mm});
            skLineSegment(sketch, "E2585", {"start": v(97.9, -300.18) * mm, "end": v(97.9, -260.22) * mm});
            skLineSegment(sketch, "E2586", {"start": v(97.9, -260.22) * mm, "end": v(115.46, -260.22) * mm});
            skLineSegment(sketch, "E2587", {"start": v(115.46, -260.22) * mm, "end": v(115.96, -260.22) * mm});
            skLineSegment(sketch, "E2588", {"start": v(115.96, -260.22) * mm, "end": v(116.45, -260.25) * mm});
            skLineSegment(sketch, "E2589", {"start": v(116.45, -260.25) * mm, "end": v(116.94, -260.3) * mm});
            skLineSegment(sketch, "E2590", {"start": v(116.94, -260.3) * mm, "end": v(117.42, -260.38) * mm});
            skLineSegment(sketch, "E2591", {"start": v(117.42, -260.38) * mm, "end": v(117.9, -260.48) * mm});
            skLineSegment(sketch, "E2592", {"start": v(117.9, -260.48) * mm, "end": v(118.37, -260.61) * mm});
            skLineSegment(sketch, "E2593", {"start": v(118.37, -260.61) * mm, "end": v(118.83, -260.76) * mm});
            skLineSegment(sketch, "E2594", {"start": v(118.83, -260.76) * mm, "end": v(119.28, -260.94) * mm});
            skLineSegment(sketch, "E2595", {"start": v(119.28, -260.94) * mm, "end": v(119.73, -261.13) * mm});
            skLineSegment(sketch, "E2596", {"start": v(119.73, -261.13) * mm, "end": v(120.16, -261.35) * mm});
            skLineSegment(sketch, "E2597", {"start": v(120.16, -261.35) * mm, "end": v(120.59, -261.6) * mm});
            skLineSegment(sketch, "E2598", {"start": v(120.59, -261.6) * mm, "end": v(121, -261.86) * mm});
            skLineSegment(sketch, "E2599", {"start": v(121, -261.86) * mm, "end": v(121.4, -262.14) * mm});
            skLineSegment(sketch, "E2600", {"start": v(121.4, -262.14) * mm, "end": v(121.78, -262.45) * mm});
            skLineSegment(sketch, "E2601", {"start": v(121.78, -262.45) * mm, "end": v(122.15, -262.77) * mm});
            skLineSegment(sketch, "E2602", {"start": v(122.15, -262.77) * mm, "end": v(122.5, -263.12) * mm});
            skLineSegment(sketch, "E2603", {"start": v(122.5, -263.12) * mm, "end": v(122.85, -263.47) * mm});
            skLineSegment(sketch, "E2604", {"start": v(122.85, -263.47) * mm, "end": v(123.17, -263.84) * mm});
            skLineSegment(sketch, "E2605", {"start": v(123.17, -263.84) * mm, "end": v(123.47, -264.22) * mm});
            skLineSegment(sketch, "E2606", {"start": v(123.47, -264.22) * mm, "end": v(123.75, -264.61) * mm});
            skLineSegment(sketch, "E2607", {"start": v(123.75, -264.61) * mm, "end": v(124, -265.02) * mm});
            skLineSegment(sketch, "E2608", {"start": v(124, -265.02) * mm, "end": v(124.25, -265.44) * mm});
            skLineSegment(sketch, "E2609", {"start": v(124.25, -265.44) * mm, "end": v(124.47, -265.87) * mm});
            skLineSegment(sketch, "E2610", {"start": v(124.47, -265.87) * mm, "end": v(124.67, -266.31) * mm});
            skLineSegment(sketch, "E2611", {"start": v(124.67, -266.31) * mm, "end": v(124.84, -266.76) * mm});
            skLineSegment(sketch, "E2612", {"start": v(124.84, -266.76) * mm, "end": v(125, -267.22) * mm});
            skLineSegment(sketch, "E2613", {"start": v(125, -267.22) * mm, "end": v(125.12, -267.69) * mm});
            skLineSegment(sketch, "E2614", {"start": v(125.12, -267.69) * mm, "end": v(125.23, -268.16) * mm});
            skLineSegment(sketch, "E2615", {"start": v(125.23, -268.16) * mm, "end": v(125.32, -268.64) * mm});
            skLineSegment(sketch, "E2616", {"start": v(125.32, -268.64) * mm, "end": v(125.38, -269.12) * mm});
            skLineSegment(sketch, "E2617", {"start": v(125.38, -269.12) * mm, "end": v(125.41, -269.6) * mm});
            skLineSegment(sketch, "E2618", {"start": v(125.41, -269.6) * mm, "end": v(125.42, -270.1) * mm});
            skLineSegment(sketch, "E2619", {"start": v(125.42, -270.1) * mm, "end": v(125.43, -270.6) * mm});
            skLineSegment(sketch, "E2620", {"start": v(125.43, -270.6) * mm, "end": v(125.4, -271.1) * mm});
            skLineSegment(sketch, "E2621", {"start": v(125.4, -271.1) * mm, "end": v(125.35, -271.59) * mm});
            skLineSegment(sketch, "E2622", {"start": v(125.35, -271.59) * mm, "end": v(125.28, -272.08) * mm});
            skLineSegment(sketch, "E2623", {"start": v(125.28, -272.08) * mm, "end": v(125.18, -272.57) * mm});
            skLineSegment(sketch, "E2624", {"start": v(125.18, -272.57) * mm, "end": v(125.06, -273.05) * mm});
            skLineSegment(sketch, "E2625", {"start": v(125.06, -273.05) * mm, "end": v(124.91, -273.52) * mm});
            skLineSegment(sketch, "E2626", {"start": v(124.91, -273.52) * mm, "end": v(124.74, -273.98) * mm});
            skLineSegment(sketch, "E2627", {"start": v(124.74, -273.98) * mm, "end": v(124.55, -274.44) * mm});
            skLineSegment(sketch, "E2628", {"start": v(124.55, -274.44) * mm, "end": v(124.34, -274.88) * mm});
            skLineSegment(sketch, "E2629", {"start": v(124.34, -274.88) * mm, "end": v(124.1, -275.32) * mm});
            skLineSegment(sketch, "E2630", {"start": v(124.1, -275.32) * mm, "end": v(123.84, -275.74) * mm});
            skLineSegment(sketch, "E2631", {"start": v(123.84, -275.74) * mm, "end": v(123.56, -276.15) * mm});
            skLineSegment(sketch, "E2632", {"start": v(123.56, -276.15) * mm, "end": v(123.25, -276.54) * mm});
            skLineSegment(sketch, "E2633", {"start": v(123.25, -276.54) * mm, "end": v(122.93, -276.92) * mm});
            skLineSegment(sketch, "E2634", {"start": v(122.93, -276.92) * mm, "end": v(122.59, -277.29) * mm});
            skLineSegment(sketch, "E2635", {"start": v(122.59, -277.29) * mm, "end": v(122.22, -277.63) * mm});
            skLineSegment(sketch, "E2636", {"start": v(122.22, -277.63) * mm, "end": v(121.85, -277.96) * mm});
            skLineSegment(sketch, "E2637", {"start": v(121.85, -277.96) * mm, "end": v(121.46, -278.26) * mm});
            skLineSegment(sketch, "E2638", {"start": v(121.46, -278.26) * mm, "end": v(121.05, -278.54) * mm});
            skLineSegment(sketch, "E2639", {"start": v(121.05, -278.54) * mm, "end": v(120.64, -278.8) * mm});
            skLineSegment(sketch, "E2640", {"start": v(120.64, -278.8) * mm, "end": v(120.2, -279.05) * mm});
            skLineSegment(sketch, "E2641", {"start": v(120.2, -279.05) * mm, "end": v(119.77, -279.26) * mm});
            skLineSegment(sketch, "E2642", {"start": v(119.77, -279.26) * mm, "end": v(119.32, -279.46) * mm});
            skLineSegment(sketch, "E2643", {"start": v(119.32, -279.46) * mm, "end": v(118.86, -279.63) * mm});
            skLineSegment(sketch, "E2644", {"start": v(118.86, -279.63) * mm, "end": v(118.4, -279.78) * mm});
            skLineSegment(sketch, "E2645", {"start": v(118.4, -279.78) * mm, "end": v(117.92, -279.91) * mm});
            skLineSegment(sketch, "E2646", {"start": v(117.92, -279.91) * mm, "end": v(117.43, -280.02) * mm});
            skLineSegment(sketch, "E2647", {"start": v(117.43, -280.02) * mm, "end": v(116.95, -280.1) * mm});
            skLineSegment(sketch, "E2648", {"start": v(116.95, -280.1) * mm, "end": v(116.46, -280.15) * mm});
            skLineSegment(sketch, "E2649", {"start": v(116.46, -280.15) * mm, "end": v(115.96, -280.18) * mm});
            skLineSegment(sketch, "E2650", {"start": v(115.96, -280.18) * mm, "end": v(115.46, -280.19) * mm});
            skLineSegment(sketch, "E2651", {"start": v(115.46, -280.19) * mm, "end": v(97.9, -280.19) * mm});
            skLineSegment(sketch, "E2652", {"start": v(115.46, -280.19) * mm, "end": v(115.87, -280.19) * mm});
            skLineSegment(sketch, "E2653", {"start": v(115.87, -280.19) * mm, "end": v(116.28, -280.21) * mm});
            skLineSegment(sketch, "E2654", {"start": v(116.28, -280.21) * mm, "end": v(116.68, -280.25) * mm});
            skLineSegment(sketch, "E2655", {"start": v(116.68, -280.25) * mm, "end": v(117.08, -280.32) * mm});
            skLineSegment(sketch, "E2656", {"start": v(117.08, -280.32) * mm, "end": v(117.48, -280.4) * mm});
            skLineSegment(sketch, "E2657", {"start": v(117.48, -280.4) * mm, "end": v(117.87, -280.5) * mm});
            skLineSegment(sketch, "E2658", {"start": v(117.87, -280.5) * mm, "end": v(118.26, -280.63) * mm});
            skLineSegment(sketch, "E2659", {"start": v(118.26, -280.63) * mm, "end": v(118.63, -280.77) * mm});
            skLineSegment(sketch, "E2660", {"start": v(118.63, -280.77) * mm, "end": v(119, -280.94) * mm});
            skLineSegment(sketch, "E2661", {"start": v(119, -280.94) * mm, "end": v(119.37, -281.12) * mm});
            skLineSegment(sketch, "E2662", {"start": v(119.37, -281.12) * mm, "end": v(119.72, -281.31) * mm});
            skLineSegment(sketch, "E2663", {"start": v(119.72, -281.31) * mm, "end": v(120.06, -281.53) * mm});
            skLineSegment(sketch, "E2664", {"start": v(120.06, -281.53) * mm, "end": v(120.4, -281.77) * mm});
            skLineSegment(sketch, "E2665", {"start": v(120.4, -281.77) * mm, "end": v(120.71, -282.02) * mm});
            skLineSegment(sketch, "E2666", {"start": v(120.71, -282.02) * mm, "end": v(121.02, -282.29) * mm});
            skLineSegment(sketch, "E2667", {"start": v(121.02, -282.29) * mm, "end": v(121.31, -282.57) * mm});
            skLineSegment(sketch, "E2668", {"start": v(121.31, -282.57) * mm, "end": v(121.65, -283.07) * mm});
            skLineSegment(sketch, "E2669", {"start": v(121.65, -283.07) * mm, "end": v(121.97, -283.58) * mm});
            skLineSegment(sketch, "E2670", {"start": v(121.97, -283.58) * mm, "end": v(122.26, -284.1) * mm});
            skLineSegment(sketch, "E2671", {"start": v(122.26, -284.1) * mm, "end": v(122.53, -284.65) * mm});
            skLineSegment(sketch, "E2672", {"start": v(122.53, -284.65) * mm, "end": v(122.78, -285.2) * mm});
            skLineSegment(sketch, "E2673", {"start": v(122.78, -285.2) * mm, "end": v(123, -285.75) * mm});
            skLineSegment(sketch, "E2674", {"start": v(123, -285.75) * mm, "end": v(123.2, -286.32) * mm});
            skLineSegment(sketch, "E2675", {"start": v(123.2, -286.32) * mm, "end": v(123.36, -286.9) * mm});
            skLineSegment(sketch, "E2676", {"start": v(123.36, -286.9) * mm, "end": v(123.5, -287.47) * mm});
            skLineSegment(sketch, "E2677", {"start": v(123.5, -287.47) * mm, "end": v(123.62, -288.06) * mm});
            skLineSegment(sketch, "E2678", {"start": v(123.62, -288.06) * mm, "end": v(123.72, -288.65) * mm});
            skLineSegment(sketch, "E2679", {"start": v(123.72, -288.65) * mm, "end": v(123.78, -289.25) * mm});
            skLineSegment(sketch, "E2680", {"start": v(123.78, -289.25) * mm, "end": v(123.82, -289.85) * mm});
            skLineSegment(sketch, "E2681", {"start": v(123.82, -289.85) * mm, "end": v(123.83, -290.45) * mm});
            skLineSegment(sketch, "E2682", {"start": v(123.83, -290.45) * mm, "end": v(123.82, -291.05) * mm});
            skLineSegment(sketch, "E2683", {"start": v(123.82, -291.05) * mm, "end": v(123.77, -291.66) * mm});
            skLineSegment(sketch, "E2684", {"start": v(123.77, -291.66) * mm, "end": v(123.77, -292.2) * mm});
            skLineSegment(sketch, "E2685", {"start": v(123.77, -292.2) * mm, "end": v(123.77, -292.73) * mm});
            skLineSegment(sketch, "E2686", {"start": v(123.77, -292.73) * mm, "end": v(123.78, -293.27) * mm});
            skLineSegment(sketch, "E2687", {"start": v(123.78, -293.27) * mm, "end": v(123.8, -293.8) * mm});
            skLineSegment(sketch, "E2688", {"start": v(123.8, -293.8) * mm, "end": v(123.83, -294.34) * mm});
            skLineSegment(sketch, "E2689", {"start": v(123.83, -294.34) * mm, "end": v(123.87, -294.88) * mm});
            skLineSegment(sketch, "E2690", {"start": v(123.87, -294.88) * mm, "end": v(123.92, -295.42) * mm});
            skLineSegment(sketch, "E2691", {"start": v(123.92, -295.42) * mm, "end": v(123.98, -295.95) * mm});
            skLineSegment(sketch, "E2692", {"start": v(123.98, -295.95) * mm, "end": v(124.05, -296.49) * mm});
            skLineSegment(sketch, "E2693", {"start": v(124.05, -296.49) * mm, "end": v(124.13, -297.02) * mm});
            skLineSegment(sketch, "E2694", {"start": v(124.13, -297.02) * mm, "end": v(124.22, -297.55) * mm});
            skLineSegment(sketch, "E2695", {"start": v(124.22, -297.55) * mm, "end": v(124.32, -298.08) * mm});
            skLineSegment(sketch, "E2696", {"start": v(124.32, -298.08) * mm, "end": v(124.43, -298.6) * mm});
            skLineSegment(sketch, "E2697", {"start": v(124.43, -298.6) * mm, "end": v(124.54, -299.13) * mm});
            skLineSegment(sketch, "E2698", {"start": v(124.54, -299.13) * mm, "end": v(124.67, -299.66) * mm});
            skLineSegment(sketch, "E2699", {"start": v(124.67, -299.66) * mm, "end": v(124.8, -300.18) * mm});
            skLineSegment(sketch, "E2700", {"start": v(181.66, -300.18) * mm, "end": v(181.66, -260.18) * mm});
            skLineSegment(sketch, "E2701", {"start": v(181.66, -260.18) * mm, "end": v(180.7, -260.18) * mm});
            skLineSegment(sketch, "E2702", {"start": v(180.7, -260.18) * mm, "end": v(160.54, -287.06) * mm});
            skLineSegment(sketch, "E2703", {"start": v(160.54, -287.06) * mm, "end": v(160.54, -289.3) * mm});
            skLineSegment(sketch, "E2704", {"start": v(160.54, -289.3) * mm, "end": v(190.94, -289.3) * mm});
            skLineSegment(sketch, "E2705", {"start": v(-45.24, -918.23) * mm, "end": v(-45.24, -878.24) * mm});
            skLineSegment(sketch, "E2706", {"start": v(-45.24, -878.24) * mm, "end": v(-20.37, -878.24) * mm});
            skLineSegment(sketch, "E2707", {"start": v(-45.24, -897.35) * mm, "end": v(-22.17, -897.35) * mm});
            skLineSegment(sketch, "E2708", {"start": v(11.92, -918.2) * mm, "end": v(-11.57, -918.2) * mm});
            skLineSegment(sketch, "E2709", {"start": v(-11.57, -918.2) * mm, "end": v(-11.57, -878.26) * mm});
            skLineSegment(sketch, "E2710", {"start": v(27.08, -918.77) * mm, "end": v(26.66, -918.77) * mm});
            skLineSegment(sketch, "E2711", {"start": v(26.66, -918.77) * mm, "end": v(26.24, -918.77) * mm});
            skLineSegment(sketch, "E2712", {"start": v(26.24, -918.77) * mm, "end": v(25.83, -918.75) * mm});
            skLineSegment(sketch, "E2713", {"start": v(25.83, -918.75) * mm, "end": v(25.41, -918.72) * mm});
            skLineSegment(sketch, "E2714", {"start": v(25.41, -918.72) * mm, "end": v(25, -918.68) * mm});
            skLineSegment(sketch, "E2715", {"start": v(25, -918.68) * mm, "end": v(24.58, -918.63) * mm});
            skLineSegment(sketch, "E2716", {"start": v(24.58, -918.63) * mm, "end": v(24.17, -918.57) * mm});
            skLineSegment(sketch, "E2717", {"start": v(24.17, -918.57) * mm, "end": v(23.76, -918.5) * mm});
            skLineSegment(sketch, "E2718", {"start": v(23.76, -918.5) * mm, "end": v(23.35, -918.42) * mm});
            skLineSegment(sketch, "E2719", {"start": v(23.35, -918.42) * mm, "end": v(22.95, -918.33) * mm});
            skLineSegment(sketch, "E2720", {"start": v(22.95, -918.33) * mm, "end": v(22.55, -918.23) * mm});
            skLineSegment(sketch, "E2721", {"start": v(22.55, -918.23) * mm, "end": v(22.15, -918.12) * mm});
            skLineSegment(sketch, "E2722", {"start": v(22.15, -918.12) * mm, "end": v(21.75, -918) * mm});
            skLineSegment(sketch, "E2723", {"start": v(21.75, -918) * mm, "end": v(21.36, -917.88) * mm});
            skLineSegment(sketch, "E2724", {"start": v(21.36, -917.88) * mm, "end": v(20.97, -917.74) * mm});
            skLineSegment(sketch, "E2725", {"start": v(20.97, -917.74) * mm, "end": v(20.58, -917.59) * mm});
            skLineSegment(sketch, "E2726", {"start": v(20.58, -917.59) * mm, "end": v(20.2, -917.43) * mm});
            skLineSegment(sketch, "E2727", {"start": v(20.2, -917.43) * mm, "end": v(19.82, -917.26) * mm});
            skLineSegment(sketch, "E2728", {"start": v(19.82, -917.26) * mm, "end": v(19.45, -917.09) * mm});
            skLineSegment(sketch, "E2729", {"start": v(19.45, -917.09) * mm, "end": v(19.08, -916.9) * mm});
            skLineSegment(sketch, "E2730", {"start": v(19.08, -916.9) * mm, "end": v(18.71, -916.7) * mm});
            skLineSegment(sketch, "E2731", {"start": v(18.71, -916.7) * mm, "end": v(18.35, -916.5) * mm});
            skLineSegment(sketch, "E2732", {"start": v(18.35, -916.5) * mm, "end": v(18, -916.29) * mm});
            skLineSegment(sketch, "E2733", {"start": v(18, -916.29) * mm, "end": v(17.64, -916.07) * mm});
            skLineSegment(sketch, "E2734", {"start": v(17.64, -916.07) * mm, "end": v(17.3, -915.84) * mm});
            skLineSegment(sketch, "E2735", {"start": v(17.3, -915.84) * mm, "end": v(16.96, -915.6) * mm});
            skLineSegment(sketch, "E2736", {"start": v(16.96, -915.6) * mm, "end": v(16.63, -915.35) * mm});
            skLineSegment(sketch, "E2737", {"start": v(16.63, -915.35) * mm, "end": v(16.3, -915.09) * mm});
            skLineSegment(sketch, "E2738", {"start": v(16.3, -915.09) * mm, "end": v(15.98, -914.82) * mm});
            skLineSegment(sketch, "E2739", {"start": v(15.98, -914.82) * mm, "end": v(15.66, -914.55) * mm});
            skLineSegment(sketch, "E2740", {"start": v(15.66, -914.55) * mm, "end": v(15.35, -914.27) * mm});
            skLineSegment(sketch, "E2741", {"start": v(15.35, -914.27) * mm, "end": v(15.05, -913.97) * mm});
            skLineSegment(sketch, "E2742", {"start": v(15.05, -913.97) * mm, "end": v(14.7, -913.6) * mm});
            skLineSegment(sketch, "E2743", {"start": v(14.7, -913.6) * mm, "end": v(14.36, -913.2) * mm});
            skLineSegment(sketch, "E2744", {"start": v(14.36, -913.2) * mm, "end": v(14.03, -912.81) * mm});
            skLineSegment(sketch, "E2745", {"start": v(14.03, -912.81) * mm, "end": v(13.71, -912.4) * mm});
            skLineSegment(sketch, "E2746", {"start": v(13.71, -912.4) * mm, "end": v(13.4, -912) * mm});
            skLineSegment(sketch, "E2747", {"start": v(13.4, -912) * mm, "end": v(13.1, -911.58) * mm});
            skLineSegment(sketch, "E2748", {"start": v(13.1, -911.58) * mm, "end": v(12.82, -911.15) * mm});
            skLineSegment(sketch, "E2749", {"start": v(12.82, -911.15) * mm, "end": v(12.54, -910.72) * mm});
            skLineSegment(sketch, "E2750", {"start": v(12.54, -910.72) * mm, "end": v(12.28, -910.29) * mm});
            skLineSegment(sketch, "E2751", {"start": v(12.28, -910.29) * mm, "end": v(12.03, -909.84) * mm});
            skLineSegment(sketch, "E2752", {"start": v(12.03, -909.84) * mm, "end": v(11.78, -909.4) * mm});
            skLineSegment(sketch, "E2753", {"start": v(11.78, -909.4) * mm, "end": v(11.55, -908.94) * mm});
            skLineSegment(sketch, "E2754", {"start": v(11.55, -908.94) * mm, "end": v(11.33, -908.48) * mm});
            skLineSegment(sketch, "E2755", {"start": v(11.33, -908.48) * mm, "end": v(11.12, -908.02) * mm});
            skLineSegment(sketch, "E2756", {"start": v(11.12, -908.02) * mm, "end": v(10.93, -907.55) * mm});
            skLineSegment(sketch, "E2757", {"start": v(10.93, -907.55) * mm, "end": v(10.74, -907.07) * mm});
            skLineSegment(sketch, "E2758", {"start": v(10.74, -907.07) * mm, "end": v(10.57, -906.6) * mm});
            skLineSegment(sketch, "E2759", {"start": v(10.57, -906.6) * mm, "end": v(10.4, -906.11) * mm});
            skLineSegment(sketch, "E2760", {"start": v(10.4, -906.11) * mm, "end": v(10.26, -905.62) * mm});
            skLineSegment(sketch, "E2761", {"start": v(10.26, -905.62) * mm, "end": v(10.12, -905.13) * mm});
            skLineSegment(sketch, "E2762", {"start": v(10.12, -905.13) * mm, "end": v(10, -904.64) * mm});
            skLineSegment(sketch, "E2763", {"start": v(10, -904.64) * mm, "end": v(9.88, -904.14) * mm});
            skLineSegment(sketch, "E2764", {"start": v(9.88, -904.14) * mm, "end": v(9.78, -903.64) * mm});
            skLineSegment(sketch, "E2765", {"start": v(9.78, -903.64) * mm, "end": v(9.69, -903.14) * mm});
            skLineSegment(sketch, "E2766", {"start": v(9.69, -903.14) * mm, "end": v(9.6, -902.63) * mm});
            skLineSegment(sketch, "E2767", {"start": v(9.6, -902.63) * mm, "end": v(9.54, -902.13) * mm});
            skLineSegment(sketch, "E2768", {"start": v(9.54, -902.13) * mm, "end": v(9.5, -901.62) * mm});
            skLineSegment(sketch, "E2769", {"start": v(9.5, -901.62) * mm, "end": v(9.45, -901.1) * mm});
            skLineSegment(sketch, "E2770", {"start": v(9.45, -901.1) * mm, "end": v(9.43, -900.6) * mm});
            skLineSegment(sketch, "E2771", {"start": v(9.43, -900.6) * mm, "end": v(9.41, -900.08) * mm});
            skLineSegment(sketch, "E2772", {"start": v(9.41, -900.08) * mm, "end": v(9.41, -899.56) * mm});
            skLineSegment(sketch, "E2773", {"start": v(9.41, -899.56) * mm, "end": v(9.42, -899.04) * mm});
            skLineSegment(sketch, "E2774", {"start": v(9.42, -899.04) * mm, "end": v(9.4, -898.48) * mm});
            skLineSegment(sketch, "E2775", {"start": v(9.4, -898.48) * mm, "end": v(9.4, -897.92) * mm});
            skLineSegment(sketch, "E2776", {"start": v(9.4, -897.92) * mm, "end": v(9.42, -897.36) * mm});
            skLineSegment(sketch, "E2777", {"start": v(9.42, -897.36) * mm, "end": v(9.44, -896.8) * mm});
            skLineSegment(sketch, "E2778", {"start": v(9.44, -896.8) * mm, "end": v(9.48, -896.25) * mm});
            skLineSegment(sketch, "E2779", {"start": v(9.48, -896.25) * mm, "end": v(9.54, -895.7) * mm});
            skLineSegment(sketch, "E2780", {"start": v(9.54, -895.7) * mm, "end": v(9.6, -895.14) * mm});
            skLineSegment(sketch, "E2781", {"start": v(9.6, -895.14) * mm, "end": v(9.69, -894.6) * mm});
            skLineSegment(sketch, "E2782", {"start": v(9.69, -894.6) * mm, "end": v(9.78, -894.05) * mm});
            skLineSegment(sketch, "E2783", {"start": v(9.78, -894.05) * mm, "end": v(9.9, -893.5) * mm});
            skLineSegment(sketch, "E2784", {"start": v(9.9, -893.5) * mm, "end": v(10.02, -892.97) * mm});
            skLineSegment(sketch, "E2785", {"start": v(10.02, -892.97) * mm, "end": v(10.15, -892.43) * mm});
            skLineSegment(sketch, "E2786", {"start": v(10.15, -892.43) * mm, "end": v(10.3, -891.9) * mm});
            skLineSegment(sketch, "E2787", {"start": v(10.3, -891.9) * mm, "end": v(10.46, -891.37) * mm});
            skLineSegment(sketch, "E2788", {"start": v(10.46, -891.37) * mm, "end": v(10.64, -890.84) * mm});
            skLineSegment(sketch, "E2789", {"start": v(10.64, -890.84) * mm, "end": v(10.83, -890.32) * mm});
            skLineSegment(sketch, "E2790", {"start": v(10.83, -890.32) * mm, "end": v(11.03, -889.8) * mm});
            skLineSegment(sketch, "E2791", {"start": v(11.03, -889.8) * mm, "end": v(11.24, -889.3) * mm});
            skLineSegment(sketch, "E2792", {"start": v(11.24, -889.3) * mm, "end": v(11.47, -888.8) * mm});
            skLineSegment(sketch, "E2793", {"start": v(11.47, -888.8) * mm, "end": v(11.7, -888.3) * mm});
            skLineSegment(sketch, "E2794", {"start": v(11.7, -888.3) * mm, "end": v(11.96, -887.8) * mm});
            skLineSegment(sketch, "E2795", {"start": v(11.96, -887.8) * mm, "end": v(12.22, -887.31) * mm});
            skLineSegment(sketch, "E2796", {"start": v(12.22, -887.31) * mm, "end": v(12.5, -886.83) * mm});
            skLineSegment(sketch, "E2797", {"start": v(12.5, -886.83) * mm, "end": v(12.78, -886.36) * mm});
            skLineSegment(sketch, "E2798", {"start": v(12.78, -886.36) * mm, "end": v(13.08, -885.9) * mm});
            skLineSegment(sketch, "E2799", {"start": v(13.08, -885.9) * mm, "end": v(13.4, -885.43) * mm});
            skLineSegment(sketch, "E2800", {"start": v(13.4, -885.43) * mm, "end": v(13.72, -884.98) * mm});
            skLineSegment(sketch, "E2801", {"start": v(13.72, -884.98) * mm, "end": v(14.06, -884.53) * mm});
            skLineSegment(sketch, "E2802", {"start": v(14.06, -884.53) * mm, "end": v(14.4, -884.1) * mm});
            skLineSegment(sketch, "E2803", {"start": v(14.4, -884.1) * mm, "end": v(14.76, -883.67) * mm});
            skLineSegment(sketch, "E2804", {"start": v(14.76, -883.67) * mm, "end": v(15.13, -883.25) * mm});
            skLineSegment(sketch, "E2805", {"start": v(15.13, -883.25) * mm, "end": v(15.51, -882.84) * mm});
            skLineSegment(sketch, "E2806", {"start": v(15.51, -882.84) * mm, "end": v(15.8, -882.54) * mm});
            skLineSegment(sketch, "E2807", {"start": v(15.8, -882.54) * mm, "end": v(16.1, -882.26) * mm});
            skLineSegment(sketch, "E2808", {"start": v(16.1, -882.26) * mm, "end": v(16.4, -881.99) * mm});
            skLineSegment(sketch, "E2809", {"start": v(16.4, -881.99) * mm, "end": v(16.7, -881.72) * mm});
            skLineSegment(sketch, "E2810", {"start": v(16.7, -881.72) * mm, "end": v(17, -881.47) * mm});
            skLineSegment(sketch, "E2811", {"start": v(17, -881.47) * mm, "end": v(17.33, -881.22) * mm});
            skLineSegment(sketch, "E2812", {"start": v(17.33, -881.22) * mm, "end": v(17.65, -880.98) * mm});
            skLineSegment(sketch, "E2813", {"start": v(17.65, -880.98) * mm, "end": v(17.98, -880.74) * mm});
            skLineSegment(sketch, "E2814", {"start": v(17.98, -880.74) * mm, "end": v(18.32, -880.52) * mm});
            skLineSegment(sketch, "E2815", {"start": v(18.32, -880.52) * mm, "end": v(18.66, -880.3) * mm});
            skLineSegment(sketch, "E2816", {"start": v(18.66, -880.3) * mm, "end": v(19, -880.1) * mm});
            skLineSegment(sketch, "E2817", {"start": v(19, -880.1) * mm, "end": v(19.35, -879.9) * mm});
            skLineSegment(sketch, "E2818", {"start": v(19.35, -879.9) * mm, "end": v(19.7, -879.72) * mm});
            skLineSegment(sketch, "E2819", {"start": v(19.7, -879.72) * mm, "end": v(20.07, -879.54) * mm});
            skLineSegment(sketch, "E2820", {"start": v(20.07, -879.54) * mm, "end": v(20.43, -879.37) * mm});
            skLineSegment(sketch, "E2821", {"start": v(20.43, -879.37) * mm, "end": v(20.8, -879.22) * mm});
            skLineSegment(sketch, "E2822", {"start": v(20.8, -879.22) * mm, "end": v(21.17, -879.07) * mm});
            skLineSegment(sketch, "E2823", {"start": v(21.17, -879.07) * mm, "end": v(21.55, -878.93) * mm});
            skLineSegment(sketch, "E2824", {"start": v(21.55, -878.93) * mm, "end": v(21.93, -878.8) * mm});
            skLineSegment(sketch, "E2825", {"start": v(21.93, -878.8) * mm, "end": v(22.3, -878.67) * mm});
            skLineSegment(sketch, "E2826", {"start": v(22.3, -878.67) * mm, "end": v(22.7, -878.56) * mm});
            skLineSegment(sketch, "E2827", {"start": v(22.7, -878.56) * mm, "end": v(23.08, -878.46) * mm});
            skLineSegment(sketch, "E2828", {"start": v(23.08, -878.46) * mm, "end": v(23.48, -878.37) * mm});
            skLineSegment(sketch, "E2829", {"start": v(23.48, -878.37) * mm, "end": v(23.87, -878.29) * mm});
            skLineSegment(sketch, "E2830", {"start": v(23.87, -878.29) * mm, "end": v(24.27, -878.22) * mm});
            skLineSegment(sketch, "E2831", {"start": v(24.27, -878.22) * mm, "end": v(24.67, -878.16) * mm});
            skLineSegment(sketch, "E2832", {"start": v(24.67, -878.16) * mm, "end": v(25.07, -878.1) * mm});
            skLineSegment(sketch, "E2833", {"start": v(25.07, -878.1) * mm, "end": v(25.47, -878.07) * mm});
            skLineSegment(sketch, "E2834", {"start": v(25.47, -878.07) * mm, "end": v(25.87, -878.04) * mm});
            skLineSegment(sketch, "E2835", {"start": v(25.87, -878.04) * mm, "end": v(26.28, -878.02) * mm});
            skLineSegment(sketch, "E2836", {"start": v(26.28, -878.02) * mm, "end": v(26.68, -878) * mm});
            skLineSegment(sketch, "E2837", {"start": v(26.68, -878) * mm, "end": v(27.1, -878) * mm});
            skLineSegment(sketch, "E2838", {"start": v(27.1, -878) * mm, "end": v(27.5, -878.01) * mm});
            skLineSegment(sketch, "E2839", {"start": v(27.5, -878.01) * mm, "end": v(27.92, -878.03) * mm});
            skLineSegment(sketch, "E2840", {"start": v(27.92, -878.03) * mm, "end": v(28.33, -878.05) * mm});
            skLineSegment(sketch, "E2841", {"start": v(28.33, -878.05) * mm, "end": v(28.74, -878.09) * mm});
            skLineSegment(sketch, "E2842", {"start": v(28.74, -878.09) * mm, "end": v(29.15, -878.13) * mm});
            skLineSegment(sketch, "E2843", {"start": v(29.15, -878.13) * mm, "end": v(29.56, -878.2) * mm});
            skLineSegment(sketch, "E2844", {"start": v(29.56, -878.2) * mm, "end": v(29.96, -878.26) * mm});
            skLineSegment(sketch, "E2845", {"start": v(29.96, -878.26) * mm, "end": v(30.36, -878.34) * mm});
            skLineSegment(sketch, "E2846", {"start": v(30.36, -878.34) * mm, "end": v(30.76, -878.42) * mm});
            skLineSegment(sketch, "E2847", {"start": v(30.76, -878.42) * mm, "end": v(31.16, -878.52) * mm});
            skLineSegment(sketch, "E2848", {"start": v(31.16, -878.52) * mm, "end": v(31.55, -878.63) * mm});
            skLineSegment(sketch, "E2849", {"start": v(31.55, -878.63) * mm, "end": v(31.94, -878.75) * mm});
            skLineSegment(sketch, "E2850", {"start": v(31.94, -878.75) * mm, "end": v(32.33, -878.87) * mm});
            skLineSegment(sketch, "E2851", {"start": v(32.33, -878.87) * mm, "end": v(32.72, -879.01) * mm});
            skLineSegment(sketch, "E2852", {"start": v(32.72, -879.01) * mm, "end": v(33.1, -879.16) * mm});
            skLineSegment(sketch, "E2853", {"start": v(33.1, -879.16) * mm, "end": v(33.47, -879.32) * mm});
            skLineSegment(sketch, "E2854", {"start": v(33.47, -879.32) * mm, "end": v(33.84, -879.48) * mm});
            skLineSegment(sketch, "E2855", {"start": v(33.84, -879.48) * mm, "end": v(34.21, -879.66) * mm});
            skLineSegment(sketch, "E2856", {"start": v(34.21, -879.66) * mm, "end": v(34.58, -879.84) * mm});
            skLineSegment(sketch, "E2857", {"start": v(34.58, -879.84) * mm, "end": v(34.93, -880.04) * mm});
            skLineSegment(sketch, "E2858", {"start": v(34.93, -880.04) * mm, "end": v(35.29, -880.24) * mm});
            skLineSegment(sketch, "E2859", {"start": v(35.29, -880.24) * mm, "end": v(35.64, -880.45) * mm});
            skLineSegment(sketch, "E2860", {"start": v(35.64, -880.45) * mm, "end": v(35.98, -880.67) * mm});
            skLineSegment(sketch, "E2861", {"start": v(35.98, -880.67) * mm, "end": v(36.32, -880.9) * mm});
            skLineSegment(sketch, "E2862", {"start": v(36.32, -880.9) * mm, "end": v(36.65, -881.14) * mm});
            skLineSegment(sketch, "E2863", {"start": v(36.65, -881.14) * mm, "end": v(36.98, -881.4) * mm});
            skLineSegment(sketch, "E2864", {"start": v(36.98, -881.4) * mm, "end": v(37.3, -881.65) * mm});
            skLineSegment(sketch, "E2865", {"start": v(37.3, -881.65) * mm, "end": v(37.61, -881.91) * mm});
            skLineSegment(sketch, "E2866", {"start": v(37.61, -881.91) * mm, "end": v(37.92, -882.19) * mm});
            skLineSegment(sketch, "E2867", {"start": v(37.92, -882.19) * mm, "end": v(38.22, -882.47) * mm});
            skLineSegment(sketch, "E2868", {"start": v(38.22, -882.47) * mm, "end": v(38.51, -882.76) * mm});
            skLineSegment(sketch, "E2869", {"start": v(38.51, -882.76) * mm, "end": v(38.8, -883.06) * mm});
            skLineSegment(sketch, "E2870", {"start": v(38.8, -883.06) * mm, "end": v(39.17, -883.47) * mm});
            skLineSegment(sketch, "E2871", {"start": v(39.17, -883.47) * mm, "end": v(39.53, -883.89) * mm});
            skLineSegment(sketch, "E2872", {"start": v(39.53, -883.89) * mm, "end": v(39.88, -884.31) * mm});
            skLineSegment(sketch, "E2873", {"start": v(39.88, -884.31) * mm, "end": v(40.21, -884.75) * mm});
            skLineSegment(sketch, "E2874", {"start": v(40.21, -884.75) * mm, "end": v(40.54, -885.19) * mm});
            skLineSegment(sketch, "E2875", {"start": v(40.54, -885.19) * mm, "end": v(40.85, -885.64) * mm});
            skLineSegment(sketch, "E2876", {"start": v(40.85, -885.64) * mm, "end": v(41.15, -886.1) * mm});
            skLineSegment(sketch, "E2877", {"start": v(41.15, -886.1) * mm, "end": v(41.44, -886.56) * mm});
            skLineSegment(sketch, "E2878", {"start": v(41.44, -886.56) * mm, "end": v(41.72, -887.03) * mm});
            skLineSegment(sketch, "E2879", {"start": v(41.72, -887.03) * mm, "end": v(41.99, -887.5) * mm});
            skLineSegment(sketch, "E2880", {"start": v(41.99, -887.5) * mm, "end": v(42.24, -887.98) * mm});
            skLineSegment(sketch, "E2881", {"start": v(42.24, -887.98) * mm, "end": v(42.48, -888.47) * mm});
            skLineSegment(sketch, "E2882", {"start": v(42.48, -888.47) * mm, "end": v(42.71, -888.97) * mm});
            skLineSegment(sketch, "E2883", {"start": v(42.71, -888.97) * mm, "end": v(42.93, -889.46) * mm});
            skLineSegment(sketch, "E2884", {"start": v(42.93, -889.46) * mm, "end": v(43.14, -889.97) * mm});
            skLineSegment(sketch, "E2885", {"start": v(43.14, -889.97) * mm, "end": v(43.33, -890.48) * mm});
            skLineSegment(sketch, "E2886", {"start": v(43.33, -890.48) * mm, "end": v(43.5, -890.99) * mm});
            skLineSegment(sketch, "E2887", {"start": v(43.5, -890.99) * mm, "end": v(43.68, -891.5) * mm});
            skLineSegment(sketch, "E2888", {"start": v(43.68, -891.5) * mm, "end": v(43.83, -892.03) * mm});
            skLineSegment(sketch, "E2889", {"start": v(43.83, -892.03) * mm, "end": v(43.97, -892.55) * mm});
            skLineSegment(sketch, "E2890", {"start": v(43.97, -892.55) * mm, "end": v(44.1, -893.08) * mm});
            skLineSegment(sketch, "E2891", {"start": v(44.1, -893.08) * mm, "end": v(44.22, -893.62) * mm});
            skLineSegment(sketch, "E2892", {"start": v(44.22, -893.62) * mm, "end": v(44.32, -894.15) * mm});
            skLineSegment(sketch, "E2893", {"start": v(44.32, -894.15) * mm, "end": v(44.4, -894.7) * mm});
            skLineSegment(sketch, "E2894", {"start": v(44.4, -894.7) * mm, "end": v(44.48, -895.23) * mm});
            skLineSegment(sketch, "E2895", {"start": v(44.48, -895.23) * mm, "end": v(44.55, -895.77) * mm});
            skLineSegment(sketch, "E2896", {"start": v(44.55, -895.77) * mm, "end": v(44.6, -896.32) * mm});
            skLineSegment(sketch, "E2897", {"start": v(44.6, -896.32) * mm, "end": v(44.63, -896.87) * mm});
            skLineSegment(sketch, "E2898", {"start": v(44.63, -896.87) * mm, "end": v(44.65, -897.42) * mm});
            skLineSegment(sketch, "E2899", {"start": v(44.65, -897.42) * mm, "end": v(44.66, -897.97) * mm});
            skLineSegment(sketch, "E2900", {"start": v(44.66, -897.97) * mm, "end": v(44.66, -898.52) * mm});
            skLineSegment(sketch, "E2901", {"start": v(44.66, -898.52) * mm, "end": v(44.64, -899.07) * mm});
            skLineSegment(sketch, "E2902", {"start": v(44.64, -899.07) * mm, "end": v(44.64, -899.58) * mm});
            skLineSegment(sketch, "E2903", {"start": v(44.64, -899.58) * mm, "end": v(44.64, -900.1) * mm});
            skLineSegment(sketch, "E2904", {"start": v(44.64, -900.1) * mm, "end": v(44.62, -900.6) * mm});
            skLineSegment(sketch, "E2905", {"start": v(44.62, -900.6) * mm, "end": v(44.6, -901.12) * mm});
            skLineSegment(sketch, "E2906", {"start": v(44.6, -901.12) * mm, "end": v(44.55, -901.63) * mm});
            skLineSegment(sketch, "E2907", {"start": v(44.55, -901.63) * mm, "end": v(44.5, -902.14) * mm});
            skLineSegment(sketch, "E2908", {"start": v(44.5, -902.14) * mm, "end": v(44.42, -902.64) * mm});
            skLineSegment(sketch, "E2909", {"start": v(44.42, -902.64) * mm, "end": v(44.34, -903.14) * mm});
            skLineSegment(sketch, "E2910", {"start": v(44.34, -903.14) * mm, "end": v(44.25, -903.65) * mm});
            skLineSegment(sketch, "E2911", {"start": v(44.25, -903.65) * mm, "end": v(44.14, -904.14) * mm});
            skLineSegment(sketch, "E2912", {"start": v(44.14, -904.14) * mm, "end": v(44.02, -904.64) * mm});
            skLineSegment(sketch, "E2913", {"start": v(44.02, -904.64) * mm, "end": v(43.9, -905.13) * mm});
            skLineSegment(sketch, "E2914", {"start": v(43.9, -905.13) * mm, "end": v(43.75, -905.61) * mm});
            skLineSegment(sketch, "E2915", {"start": v(43.75, -905.61) * mm, "end": v(43.6, -906.1) * mm});
            skLineSegment(sketch, "E2916", {"start": v(43.6, -906.1) * mm, "end": v(43.43, -906.58) * mm});
            skLineSegment(sketch, "E2917", {"start": v(43.43, -906.58) * mm, "end": v(43.25, -907.05) * mm});
            skLineSegment(sketch, "E2918", {"start": v(43.25, -907.05) * mm, "end": v(43.06, -907.52) * mm});
            skLineSegment(sketch, "E2919", {"start": v(43.06, -907.52) * mm, "end": v(42.86, -907.99) * mm});
            skLineSegment(sketch, "E2920", {"start": v(42.86, -907.99) * mm, "end": v(42.65, -908.45) * mm});
            skLineSegment(sketch, "E2921", {"start": v(42.65, -908.45) * mm, "end": v(42.42, -908.9) * mm});
            skLineSegment(sketch, "E2922", {"start": v(42.42, -908.9) * mm, "end": v(42.19, -909.35) * mm});
            skLineSegment(sketch, "E2923", {"start": v(42.19, -909.35) * mm, "end": v(41.94, -909.8) * mm});
            skLineSegment(sketch, "E2924", {"start": v(41.94, -909.8) * mm, "end": v(41.68, -910.24) * mm});
            skLineSegment(sketch, "E2925", {"start": v(41.68, -910.24) * mm, "end": v(41.41, -910.67) * mm});
            skLineSegment(sketch, "E2926", {"start": v(41.41, -910.67) * mm, "end": v(41.13, -911.1) * mm});
            skLineSegment(sketch, "E2927", {"start": v(41.13, -911.1) * mm, "end": v(40.84, -911.51) * mm});
            skLineSegment(sketch, "E2928", {"start": v(40.84, -911.51) * mm, "end": v(40.54, -911.92) * mm});
            skLineSegment(sketch, "E2929", {"start": v(40.54, -911.92) * mm, "end": v(40.23, -912.33) * mm});
            skLineSegment(sketch, "E2930", {"start": v(40.23, -912.33) * mm, "end": v(39.9, -912.73) * mm});
            skLineSegment(sketch, "E2931", {"start": v(39.9, -912.73) * mm, "end": v(39.57, -913.11) * mm});
            skLineSegment(sketch, "E2932", {"start": v(39.57, -913.11) * mm, "end": v(39.23, -913.5) * mm});
            skLineSegment(sketch, "E2933", {"start": v(39.23, -913.5) * mm, "end": v(38.87, -913.87) * mm});
            skLineSegment(sketch, "E2934", {"start": v(38.87, -913.87) * mm, "end": v(38.58, -914.16) * mm});
            skLineSegment(sketch, "E2935", {"start": v(38.58, -914.16) * mm, "end": v(38.28, -914.44) * mm});
            skLineSegment(sketch, "E2936", {"start": v(38.28, -914.44) * mm, "end": v(37.97, -914.72) * mm});
            skLineSegment(sketch, "E2937", {"start": v(37.97, -914.72) * mm, "end": v(37.66, -914.99) * mm});
            skLineSegment(sketch, "E2938", {"start": v(37.66, -914.99) * mm, "end": v(37.34, -915.24) * mm});
            skLineSegment(sketch, "E2939", {"start": v(37.34, -915.24) * mm, "end": v(37.01, -915.5) * mm});
            skLineSegment(sketch, "E2940", {"start": v(37.01, -915.5) * mm, "end": v(36.68, -915.74) * mm});
            skLineSegment(sketch, "E2941", {"start": v(36.68, -915.74) * mm, "end": v(36.35, -915.97) * mm});
            skLineSegment(sketch, "E2942", {"start": v(36.35, -915.97) * mm, "end": v(36, -916.2) * mm});
            skLineSegment(sketch, "E2943", {"start": v(36, -916.2) * mm, "end": v(35.66, -916.4) * mm});
            skLineSegment(sketch, "E2944", {"start": v(35.66, -916.4) * mm, "end": v(35.3, -916.61) * mm});
            skLineSegment(sketch, "E2945", {"start": v(35.3, -916.61) * mm, "end": v(34.95, -916.81) * mm});
            skLineSegment(sketch, "E2946", {"start": v(34.95, -916.81) * mm, "end": v(34.58, -917) * mm});
            skLineSegment(sketch, "E2947", {"start": v(34.58, -917) * mm, "end": v(34.22, -917.18) * mm});
            skLineSegment(sketch, "E2948", {"start": v(34.22, -917.18) * mm, "end": v(33.85, -917.35) * mm});
            skLineSegment(sketch, "E2949", {"start": v(33.85, -917.35) * mm, "end": v(33.47, -917.51) * mm});
            skLineSegment(sketch, "E2950", {"start": v(33.47, -917.51) * mm, "end": v(33.1, -917.66) * mm});
            skLineSegment(sketch, "E2951", {"start": v(33.1, -917.66) * mm, "end": v(32.71, -917.8) * mm});
            skLineSegment(sketch, "E2952", {"start": v(32.71, -917.8) * mm, "end": v(32.33, -917.94) * mm});
            skLineSegment(sketch, "E2953", {"start": v(32.33, -917.94) * mm, "end": v(31.94, -918.06) * mm});
            skLineSegment(sketch, "E2954", {"start": v(31.94, -918.06) * mm, "end": v(31.55, -918.17) * mm});
            skLineSegment(sketch, "E2955", {"start": v(31.55, -918.17) * mm, "end": v(31.15, -918.28) * mm});
            skLineSegment(sketch, "E2956", {"start": v(31.15, -918.28) * mm, "end": v(30.75, -918.37) * mm});
            skLineSegment(sketch, "E2957", {"start": v(30.75, -918.37) * mm, "end": v(30.35, -918.46) * mm});
            skLineSegment(sketch, "E2958", {"start": v(30.35, -918.46) * mm, "end": v(29.95, -918.53) * mm});
            skLineSegment(sketch, "E2959", {"start": v(29.95, -918.53) * mm, "end": v(29.55, -918.6) * mm});
            skLineSegment(sketch, "E2960", {"start": v(29.55, -918.6) * mm, "end": v(29.14, -918.65) * mm});
            skLineSegment(sketch, "E2961", {"start": v(29.14, -918.65) * mm, "end": v(28.73, -918.7) * mm});
            skLineSegment(sketch, "E2962", {"start": v(28.73, -918.7) * mm, "end": v(28.32, -918.73) * mm});
            skLineSegment(sketch, "E2963", {"start": v(28.32, -918.73) * mm, "end": v(27.91, -918.75) * mm});
            skLineSegment(sketch, "E2964", {"start": v(27.91, -918.75) * mm, "end": v(27.5, -918.77) * mm});
            skLineSegment(sketch, "E2965", {"start": v(27.5, -918.77) * mm, "end": v(27.08, -918.77) * mm});
            skLineSegment(sketch, "E2966", {"start": v(71.33, -918.77) * mm, "end": v(70.9, -918.77) * mm});
            skLineSegment(sketch, "E2967", {"start": v(70.9, -918.77) * mm, "end": v(70.5, -918.77) * mm});
            skLineSegment(sketch, "E2968", {"start": v(70.5, -918.77) * mm, "end": v(70.07, -918.75) * mm});
            skLineSegment(sketch, "E2969", {"start": v(70.07, -918.75) * mm, "end": v(69.66, -918.72) * mm});
            skLineSegment(sketch, "E2970", {"start": v(69.66, -918.72) * mm, "end": v(69.24, -918.68) * mm});
            skLineSegment(sketch, "E2971", {"start": v(69.24, -918.68) * mm, "end": v(68.83, -918.63) * mm});
            skLineSegment(sketch, "E2972", {"start": v(68.83, -918.63) * mm, "end": v(68.42, -918.57) * mm});
            skLineSegment(sketch, "E2973", {"start": v(68.42, -918.57) * mm, "end": v(68, -918.5) * mm});
            skLineSegment(sketch, "E2974", {"start": v(68, -918.5) * mm, "end": v(67.6, -918.42) * mm});
            skLineSegment(sketch, "E2975", {"start": v(67.6, -918.42) * mm, "end": v(67.2, -918.33) * mm});
            skLineSegment(sketch, "E2976", {"start": v(67.2, -918.33) * mm, "end": v(66.8, -918.23) * mm});
            skLineSegment(sketch, "E2977", {"start": v(66.8, -918.23) * mm, "end": v(66.4, -918.12) * mm});
            skLineSegment(sketch, "E2978", {"start": v(66.4, -918.12) * mm, "end": v(66, -918) * mm});
            skLineSegment(sketch, "E2979", {"start": v(66, -918) * mm, "end": v(65.6, -917.88) * mm});
            skLineSegment(sketch, "E2980", {"start": v(65.6, -917.88) * mm, "end": v(65.21, -917.74) * mm});
            skLineSegment(sketch, "E2981", {"start": v(65.21, -917.74) * mm, "end": v(64.83, -917.59) * mm});
            skLineSegment(sketch, "E2982", {"start": v(64.83, -917.59) * mm, "end": v(64.44, -917.43) * mm});
            skLineSegment(sketch, "E2983", {"start": v(64.44, -917.43) * mm, "end": v(64.07, -917.26) * mm});
            skLineSegment(sketch, "E2984", {"start": v(64.07, -917.26) * mm, "end": v(63.7, -917.09) * mm});
            skLineSegment(sketch, "E2985", {"start": v(63.7, -917.09) * mm, "end": v(63.32, -916.9) * mm});
            skLineSegment(sketch, "E2986", {"start": v(63.32, -916.9) * mm, "end": v(62.96, -916.7) * mm});
            skLineSegment(sketch, "E2987", {"start": v(62.96, -916.7) * mm, "end": v(62.6, -916.5) * mm});
            skLineSegment(sketch, "E2988", {"start": v(62.6, -916.5) * mm, "end": v(62.24, -916.29) * mm});
            skLineSegment(sketch, "E2989", {"start": v(62.24, -916.29) * mm, "end": v(61.89, -916.07) * mm});
            skLineSegment(sketch, "E2990", {"start": v(61.89, -916.07) * mm, "end": v(61.54, -915.84) * mm});
            skLineSegment(sketch, "E2991", {"start": v(61.54, -915.84) * mm, "end": v(61.2, -915.6) * mm});
            skLineSegment(sketch, "E2992", {"start": v(61.2, -915.6) * mm, "end": v(60.87, -915.35) * mm});
            skLineSegment(sketch, "E2993", {"start": v(60.87, -915.35) * mm, "end": v(60.54, -915.09) * mm});
            skLineSegment(sketch, "E2994", {"start": v(60.54, -915.09) * mm, "end": v(60.22, -914.82) * mm});
            skLineSegment(sketch, "E2995", {"start": v(60.22, -914.82) * mm, "end": v(59.9, -914.55) * mm});
            skLineSegment(sketch, "E2996", {"start": v(59.9, -914.55) * mm, "end": v(59.6, -914.27) * mm});
            skLineSegment(sketch, "E2997", {"start": v(59.6, -914.27) * mm, "end": v(59.3, -913.97) * mm});
            skLineSegment(sketch, "E2998", {"start": v(59.3, -913.97) * mm, "end": v(58.94, -913.6) * mm});
            skLineSegment(sketch, "E2999", {"start": v(58.94, -913.6) * mm, "end": v(58.6, -913.2) * mm});
            skLineSegment(sketch, "E3000", {"start": v(58.6, -913.2) * mm, "end": v(58.28, -912.81) * mm});
            skLineSegment(sketch, "E3001", {"start": v(58.28, -912.81) * mm, "end": v(57.96, -912.4) * mm});
            skLineSegment(sketch, "E3002", {"start": v(57.96, -912.4) * mm, "end": v(57.65, -912) * mm});
            skLineSegment(sketch, "E3003", {"start": v(57.65, -912) * mm, "end": v(57.35, -911.58) * mm});
            skLineSegment(sketch, "E3004", {"start": v(57.35, -911.58) * mm, "end": v(57.07, -911.15) * mm});
            skLineSegment(sketch, "E3005", {"start": v(57.07, -911.15) * mm, "end": v(56.79, -910.72) * mm});
            skLineSegment(sketch, "E3006", {"start": v(56.79, -910.72) * mm, "end": v(56.53, -910.29) * mm});
            skLineSegment(sketch, "E3007", {"start": v(56.53, -910.29) * mm, "end": v(56.27, -909.84) * mm});
            skLineSegment(sketch, "E3008", {"start": v(56.27, -909.84) * mm, "end": v(56.03, -909.4) * mm});
            skLineSegment(sketch, "E3009", {"start": v(56.03, -909.4) * mm, "end": v(55.8, -908.94) * mm});
            skLineSegment(sketch, "E3010", {"start": v(55.8, -908.94) * mm, "end": v(55.58, -908.48) * mm});
            skLineSegment(sketch, "E3011", {"start": v(55.58, -908.48) * mm, "end": v(55.37, -908.02) * mm});
            skLineSegment(sketch, "E3012", {"start": v(55.37, -908.02) * mm, "end": v(55.17, -907.55) * mm});
            skLineSegment(sketch, "E3013", {"start": v(55.17, -907.55) * mm, "end": v(54.99, -907.07) * mm});
            skLineSegment(sketch, "E3014", {"start": v(54.99, -907.07) * mm, "end": v(54.81, -906.6) * mm});
            skLineSegment(sketch, "E3015", {"start": v(54.81, -906.6) * mm, "end": v(54.65, -906.11) * mm});
            skLineSegment(sketch, "E3016", {"start": v(54.65, -906.11) * mm, "end": v(54.5, -905.62) * mm});
            skLineSegment(sketch, "E3017", {"start": v(54.5, -905.62) * mm, "end": v(54.36, -905.13) * mm});
            skLineSegment(sketch, "E3018", {"start": v(54.36, -905.13) * mm, "end": v(54.24, -904.64) * mm});
            skLineSegment(sketch, "E3019", {"start": v(54.24, -904.64) * mm, "end": v(54.12, -904.14) * mm});
            skLineSegment(sketch, "E3020", {"start": v(54.12, -904.14) * mm, "end": v(54.02, -903.64) * mm});
            skLineSegment(sketch, "E3021", {"start": v(54.02, -903.64) * mm, "end": v(53.93, -903.14) * mm});
            skLineSegment(sketch, "E3022", {"start": v(53.93, -903.14) * mm, "end": v(53.85, -902.63) * mm});
            skLineSegment(sketch, "E3023", {"start": v(53.85, -902.63) * mm, "end": v(53.79, -902.13) * mm});
            skLineSegment(sketch, "E3024", {"start": v(53.79, -902.13) * mm, "end": v(53.74, -901.62) * mm});
            skLineSegment(sketch, "E3025", {"start": v(53.74, -901.62) * mm, "end": v(53.7, -901.1) * mm});
            skLineSegment(sketch, "E3026", {"start": v(53.7, -901.1) * mm, "end": v(53.67, -900.6) * mm});
            skLineSegment(sketch, "E3027", {"start": v(53.67, -900.6) * mm, "end": v(53.66, -900.08) * mm});
            skLineSegment(sketch, "E3028", {"start": v(53.66, -900.08) * mm, "end": v(53.66, -899.56) * mm});
            skLineSegment(sketch, "E3029", {"start": v(53.66, -899.56) * mm, "end": v(53.67, -899.04) * mm});
            skLineSegment(sketch, "E3030", {"start": v(53.67, -899.04) * mm, "end": v(53.65, -898.48) * mm});
            skLineSegment(sketch, "E3031", {"start": v(53.65, -898.48) * mm, "end": v(53.65, -897.92) * mm});
            skLineSegment(sketch, "E3032", {"start": v(53.65, -897.92) * mm, "end": v(53.66, -897.36) * mm});
            skLineSegment(sketch, "E3033", {"start": v(53.66, -897.36) * mm, "end": v(53.69, -896.8) * mm});
            skLineSegment(sketch, "E3034", {"start": v(53.69, -896.8) * mm, "end": v(53.73, -896.25) * mm});
            skLineSegment(sketch, "E3035", {"start": v(53.73, -896.25) * mm, "end": v(53.78, -895.7) * mm});
            skLineSegment(sketch, "E3036", {"start": v(53.78, -895.7) * mm, "end": v(53.85, -895.14) * mm});
            skLineSegment(sketch, "E3037", {"start": v(53.85, -895.14) * mm, "end": v(53.93, -894.6) * mm});
            skLineSegment(sketch, "E3038", {"start": v(53.93, -894.6) * mm, "end": v(54.03, -894.05) * mm});
            skLineSegment(sketch, "E3039", {"start": v(54.03, -894.05) * mm, "end": v(54.14, -893.5) * mm});
            skLineSegment(sketch, "E3040", {"start": v(54.14, -893.5) * mm, "end": v(54.26, -892.97) * mm});
            skLineSegment(sketch, "E3041", {"start": v(54.26, -892.97) * mm, "end": v(54.4, -892.43) * mm});
            skLineSegment(sketch, "E3042", {"start": v(54.4, -892.43) * mm, "end": v(54.55, -891.9) * mm});
            skLineSegment(sketch, "E3043", {"start": v(54.55, -891.9) * mm, "end": v(54.7, -891.37) * mm});
            skLineSegment(sketch, "E3044", {"start": v(54.7, -891.37) * mm, "end": v(54.88, -890.84) * mm});
            skLineSegment(sketch, "E3045", {"start": v(54.88, -890.84) * mm, "end": v(55.07, -890.32) * mm});
            skLineSegment(sketch, "E3046", {"start": v(55.07, -890.32) * mm, "end": v(55.27, -889.8) * mm});
            skLineSegment(sketch, "E3047", {"start": v(55.27, -889.8) * mm, "end": v(55.49, -889.3) * mm});
            skLineSegment(sketch, "E3048", {"start": v(55.49, -889.3) * mm, "end": v(55.71, -888.8) * mm});
            skLineSegment(sketch, "E3049", {"start": v(55.71, -888.8) * mm, "end": v(55.95, -888.3) * mm});
            skLineSegment(sketch, "E3050", {"start": v(55.95, -888.3) * mm, "end": v(56.2, -887.8) * mm});
            skLineSegment(sketch, "E3051", {"start": v(56.2, -887.8) * mm, "end": v(56.47, -887.31) * mm});
            skLineSegment(sketch, "E3052", {"start": v(56.47, -887.31) * mm, "end": v(56.74, -886.83) * mm});
            skLineSegment(sketch, "E3053", {"start": v(56.74, -886.83) * mm, "end": v(57.03, -886.36) * mm});
            skLineSegment(sketch, "E3054", {"start": v(57.03, -886.36) * mm, "end": v(57.33, -885.9) * mm});
            skLineSegment(sketch, "E3055", {"start": v(57.33, -885.9) * mm, "end": v(57.64, -885.43) * mm});
            skLineSegment(sketch, "E3056", {"start": v(57.64, -885.43) * mm, "end": v(57.96, -884.98) * mm});
            skLineSegment(sketch, "E3057", {"start": v(57.96, -884.98) * mm, "end": v(58.3, -884.53) * mm});
            skLineSegment(sketch, "E3058", {"start": v(58.3, -884.53) * mm, "end": v(58.65, -884.1) * mm});
            skLineSegment(sketch, "E3059", {"start": v(58.65, -884.1) * mm, "end": v(59, -883.67) * mm});
            skLineSegment(sketch, "E3060", {"start": v(59, -883.67) * mm, "end": v(59.38, -883.25) * mm});
            skLineSegment(sketch, "E3061", {"start": v(59.38, -883.25) * mm, "end": v(59.76, -882.84) * mm});
            skLineSegment(sketch, "E3062", {"start": v(59.76, -882.84) * mm, "end": v(60.04, -882.54) * mm});
            skLineSegment(sketch, "E3063", {"start": v(60.04, -882.54) * mm, "end": v(60.34, -882.26) * mm});
            skLineSegment(sketch, "E3064", {"start": v(60.34, -882.26) * mm, "end": v(60.64, -881.99) * mm});
            skLineSegment(sketch, "E3065", {"start": v(60.64, -881.99) * mm, "end": v(60.94, -881.72) * mm});
            skLineSegment(sketch, "E3066", {"start": v(60.94, -881.72) * mm, "end": v(61.25, -881.47) * mm});
            skLineSegment(sketch, "E3067", {"start": v(61.25, -881.47) * mm, "end": v(61.57, -881.22) * mm});
            skLineSegment(sketch, "E3068", {"start": v(61.57, -881.22) * mm, "end": v(61.9, -880.98) * mm});
            skLineSegment(sketch, "E3069", {"start": v(61.9, -880.98) * mm, "end": v(62.23, -880.74) * mm});
            skLineSegment(sketch, "E3070", {"start": v(62.23, -880.74) * mm, "end": v(62.56, -880.52) * mm});
            skLineSegment(sketch, "E3071", {"start": v(62.56, -880.52) * mm, "end": v(62.9, -880.3) * mm});
            skLineSegment(sketch, "E3072", {"start": v(62.9, -880.3) * mm, "end": v(63.25, -880.1) * mm});
            skLineSegment(sketch, "E3073", {"start": v(63.25, -880.1) * mm, "end": v(63.6, -879.9) * mm});
            skLineSegment(sketch, "E3074", {"start": v(63.6, -879.9) * mm, "end": v(63.95, -879.72) * mm});
            skLineSegment(sketch, "E3075", {"start": v(63.95, -879.72) * mm, "end": v(64.31, -879.54) * mm});
            skLineSegment(sketch, "E3076", {"start": v(64.31, -879.54) * mm, "end": v(64.68, -879.37) * mm});
            skLineSegment(sketch, "E3077", {"start": v(64.68, -879.37) * mm, "end": v(65.04, -879.22) * mm});
            skLineSegment(sketch, "E3078", {"start": v(65.04, -879.22) * mm, "end": v(65.42, -879.07) * mm});
            skLineSegment(sketch, "E3079", {"start": v(65.42, -879.07) * mm, "end": v(65.8, -878.93) * mm});
            skLineSegment(sketch, "E3080", {"start": v(65.8, -878.93) * mm, "end": v(66.17, -878.8) * mm});
            skLineSegment(sketch, "E3081", {"start": v(66.17, -878.8) * mm, "end": v(66.55, -878.67) * mm});
            skLineSegment(sketch, "E3082", {"start": v(66.55, -878.67) * mm, "end": v(66.94, -878.56) * mm});
            skLineSegment(sketch, "E3083", {"start": v(66.94, -878.56) * mm, "end": v(67.33, -878.46) * mm});
            skLineSegment(sketch, "E3084", {"start": v(67.33, -878.46) * mm, "end": v(67.72, -878.37) * mm});
            skLineSegment(sketch, "E3085", {"start": v(67.72, -878.37) * mm, "end": v(68.12, -878.29) * mm});
            skLineSegment(sketch, "E3086", {"start": v(68.12, -878.29) * mm, "end": v(68.51, -878.22) * mm});
            skLineSegment(sketch, "E3087", {"start": v(68.51, -878.22) * mm, "end": v(68.91, -878.16) * mm});
            skLineSegment(sketch, "E3088", {"start": v(68.91, -878.16) * mm, "end": v(69.31, -878.1) * mm});
            skLineSegment(sketch, "E3089", {"start": v(69.31, -878.1) * mm, "end": v(69.71, -878.07) * mm});
            skLineSegment(sketch, "E3090", {"start": v(69.71, -878.07) * mm, "end": v(70.12, -878.04) * mm});
            skLineSegment(sketch, "E3091", {"start": v(70.12, -878.04) * mm, "end": v(70.52, -878.02) * mm});
            skLineSegment(sketch, "E3092", {"start": v(70.52, -878.02) * mm, "end": v(70.93, -878) * mm});
            skLineSegment(sketch, "E3093", {"start": v(70.93, -878) * mm, "end": v(71.34, -878) * mm});
            skLineSegment(sketch, "E3094", {"start": v(71.34, -878) * mm, "end": v(71.75, -878.01) * mm});
            skLineSegment(sketch, "E3095", {"start": v(71.75, -878.01) * mm, "end": v(72.16, -878.03) * mm});
            skLineSegment(sketch, "E3096", {"start": v(72.16, -878.03) * mm, "end": v(72.58, -878.05) * mm});
            skLineSegment(sketch, "E3097", {"start": v(72.58, -878.05) * mm, "end": v(72.99, -878.09) * mm});
            skLineSegment(sketch, "E3098", {"start": v(72.99, -878.09) * mm, "end": v(73.4, -878.13) * mm});
            skLineSegment(sketch, "E3099", {"start": v(73.4, -878.13) * mm, "end": v(73.8, -878.2) * mm});
            skLineSegment(sketch, "E3100", {"start": v(73.8, -878.2) * mm, "end": v(74.2, -878.26) * mm});
            skLineSegment(sketch, "E3101", {"start": v(74.2, -878.26) * mm, "end": v(74.6, -878.34) * mm});
            skLineSegment(sketch, "E3102", {"start": v(74.6, -878.34) * mm, "end": v(75, -878.42) * mm});
            skLineSegment(sketch, "E3103", {"start": v(75, -878.42) * mm, "end": v(75.4, -878.52) * mm});
            skLineSegment(sketch, "E3104", {"start": v(75.4, -878.52) * mm, "end": v(75.8, -878.63) * mm});
            skLineSegment(sketch, "E3105", {"start": v(75.8, -878.63) * mm, "end": v(76.19, -878.75) * mm});
            skLineSegment(sketch, "E3106", {"start": v(76.19, -878.75) * mm, "end": v(76.58, -878.87) * mm});
            skLineSegment(sketch, "E3107", {"start": v(76.58, -878.87) * mm, "end": v(76.96, -879.01) * mm});
            skLineSegment(sketch, "E3108", {"start": v(76.96, -879.01) * mm, "end": v(77.34, -879.16) * mm});
            skLineSegment(sketch, "E3109", {"start": v(77.34, -879.16) * mm, "end": v(77.72, -879.32) * mm});
            skLineSegment(sketch, "E3110", {"start": v(77.72, -879.32) * mm, "end": v(78.09, -879.48) * mm});
            skLineSegment(sketch, "E3111", {"start": v(78.09, -879.48) * mm, "end": v(78.46, -879.66) * mm});
            skLineSegment(sketch, "E3112", {"start": v(78.46, -879.66) * mm, "end": v(78.82, -879.84) * mm});
            skLineSegment(sketch, "E3113", {"start": v(78.82, -879.84) * mm, "end": v(79.18, -880.04) * mm});
            skLineSegment(sketch, "E3114", {"start": v(79.18, -880.04) * mm, "end": v(79.53, -880.24) * mm});
            skLineSegment(sketch, "E3115", {"start": v(79.53, -880.24) * mm, "end": v(79.88, -880.45) * mm});
            skLineSegment(sketch, "E3116", {"start": v(79.88, -880.45) * mm, "end": v(80.23, -880.67) * mm});
            skLineSegment(sketch, "E3117", {"start": v(80.23, -880.67) * mm, "end": v(80.56, -880.9) * mm});
            skLineSegment(sketch, "E3118", {"start": v(80.56, -880.9) * mm, "end": v(80.9, -881.14) * mm});
            skLineSegment(sketch, "E3119", {"start": v(80.9, -881.14) * mm, "end": v(81.22, -881.4) * mm});
            skLineSegment(sketch, "E3120", {"start": v(81.22, -881.4) * mm, "end": v(81.54, -881.65) * mm});
            skLineSegment(sketch, "E3121", {"start": v(81.54, -881.65) * mm, "end": v(81.86, -881.91) * mm});
            skLineSegment(sketch, "E3122", {"start": v(81.86, -881.91) * mm, "end": v(82.16, -882.19) * mm});
            skLineSegment(sketch, "E3123", {"start": v(82.16, -882.19) * mm, "end": v(82.47, -882.47) * mm});
            skLineSegment(sketch, "E3124", {"start": v(82.47, -882.47) * mm, "end": v(82.76, -882.76) * mm});
            skLineSegment(sketch, "E3125", {"start": v(82.76, -882.76) * mm, "end": v(83.05, -883.06) * mm});
            skLineSegment(sketch, "E3126", {"start": v(83.05, -883.06) * mm, "end": v(83.42, -883.47) * mm});
            skLineSegment(sketch, "E3127", {"start": v(83.42, -883.47) * mm, "end": v(83.78, -883.89) * mm});
            skLineSegment(sketch, "E3128", {"start": v(83.78, -883.89) * mm, "end": v(84.12, -884.31) * mm});
            skLineSegment(sketch, "E3129", {"start": v(84.12, -884.31) * mm, "end": v(84.46, -884.75) * mm});
            skLineSegment(sketch, "E3130", {"start": v(84.46, -884.75) * mm, "end": v(84.78, -885.19) * mm});
            skLineSegment(sketch, "E3131", {"start": v(84.78, -885.19) * mm, "end": v(85.1, -885.64) * mm});
            skLineSegment(sketch, "E3132", {"start": v(85.1, -885.64) * mm, "end": v(85.4, -886.1) * mm});
            skLineSegment(sketch, "E3133", {"start": v(85.4, -886.1) * mm, "end": v(85.69, -886.56) * mm});
            skLineSegment(sketch, "E3134", {"start": v(85.69, -886.56) * mm, "end": v(85.97, -887.03) * mm});
            skLineSegment(sketch, "E3135", {"start": v(85.97, -887.03) * mm, "end": v(86.23, -887.5) * mm});
            skLineSegment(sketch, "E3136", {"start": v(86.23, -887.5) * mm, "end": v(86.49, -887.98) * mm});
            skLineSegment(sketch, "E3137", {"start": v(86.49, -887.98) * mm, "end": v(86.73, -888.47) * mm});
            skLineSegment(sketch, "E3138", {"start": v(86.73, -888.47) * mm, "end": v(86.96, -888.97) * mm});
            skLineSegment(sketch, "E3139", {"start": v(86.96, -888.97) * mm, "end": v(87.18, -889.46) * mm});
            skLineSegment(sketch, "E3140", {"start": v(87.18, -889.46) * mm, "end": v(87.38, -889.97) * mm});
            skLineSegment(sketch, "E3141", {"start": v(87.38, -889.97) * mm, "end": v(87.57, -890.48) * mm});
            skLineSegment(sketch, "E3142", {"start": v(87.57, -890.48) * mm, "end": v(87.75, -890.99) * mm});
            skLineSegment(sketch, "E3143", {"start": v(87.75, -890.99) * mm, "end": v(87.92, -891.5) * mm});
            skLineSegment(sketch, "E3144", {"start": v(87.92, -891.5) * mm, "end": v(88.08, -892.03) * mm});
            skLineSegment(sketch, "E3145", {"start": v(88.08, -892.03) * mm, "end": v(88.22, -892.55) * mm});
            skLineSegment(sketch, "E3146", {"start": v(88.22, -892.55) * mm, "end": v(88.35, -893.08) * mm});
            skLineSegment(sketch, "E3147", {"start": v(88.35, -893.08) * mm, "end": v(88.46, -893.62) * mm});
            skLineSegment(sketch, "E3148", {"start": v(88.46, -893.62) * mm, "end": v(88.56, -894.15) * mm});
            skLineSegment(sketch, "E3149", {"start": v(88.56, -894.15) * mm, "end": v(88.65, -894.7) * mm});
            skLineSegment(sketch, "E3150", {"start": v(88.65, -894.7) * mm, "end": v(88.73, -895.23) * mm});
            skLineSegment(sketch, "E3151", {"start": v(88.73, -895.23) * mm, "end": v(88.8, -895.77) * mm});
            skLineSegment(sketch, "E3152", {"start": v(88.8, -895.77) * mm, "end": v(88.84, -896.32) * mm});
            skLineSegment(sketch, "E3153", {"start": v(88.84, -896.32) * mm, "end": v(88.88, -896.87) * mm});
            skLineSegment(sketch, "E3154", {"start": v(88.88, -896.87) * mm, "end": v(88.9, -897.42) * mm});
            skLineSegment(sketch, "E3155", {"start": v(88.9, -897.42) * mm, "end": v(88.9, -897.97) * mm});
            skLineSegment(sketch, "E3156", {"start": v(88.9, -897.97) * mm, "end": v(88.9, -898.52) * mm});
            skLineSegment(sketch, "E3157", {"start": v(88.9, -898.52) * mm, "end": v(88.88, -899.07) * mm});
            skLineSegment(sketch, "E3158", {"start": v(88.88, -899.07) * mm, "end": v(88.89, -899.58) * mm});
            skLineSegment(sketch, "E3159", {"start": v(88.89, -899.58) * mm, "end": v(88.88, -900.1) * mm});
            skLineSegment(sketch, "E3160", {"start": v(88.88, -900.1) * mm, "end": v(88.87, -900.6) * mm});
            skLineSegment(sketch, "E3161", {"start": v(88.87, -900.6) * mm, "end": v(88.84, -901.12) * mm});
            skLineSegment(sketch, "E3162", {"start": v(88.84, -901.12) * mm, "end": v(88.8, -901.63) * mm});
            skLineSegment(sketch, "E3163", {"start": v(88.8, -901.63) * mm, "end": v(88.74, -902.14) * mm});
            skLineSegment(sketch, "E3164", {"start": v(88.74, -902.14) * mm, "end": v(88.67, -902.64) * mm});
            skLineSegment(sketch, "E3165", {"start": v(88.67, -902.64) * mm, "end": v(88.59, -903.14) * mm});
            skLineSegment(sketch, "E3166", {"start": v(88.59, -903.14) * mm, "end": v(88.5, -903.65) * mm});
            skLineSegment(sketch, "E3167", {"start": v(88.5, -903.65) * mm, "end": v(88.39, -904.14) * mm});
            skLineSegment(sketch, "E3168", {"start": v(88.39, -904.14) * mm, "end": v(88.27, -904.64) * mm});
            skLineSegment(sketch, "E3169", {"start": v(88.27, -904.64) * mm, "end": v(88.14, -905.13) * mm});
            skLineSegment(sketch, "E3170", {"start": v(88.14, -905.13) * mm, "end": v(88, -905.61) * mm});
            skLineSegment(sketch, "E3171", {"start": v(88, -905.61) * mm, "end": v(87.84, -906.1) * mm});
            skLineSegment(sketch, "E3172", {"start": v(87.84, -906.1) * mm, "end": v(87.68, -906.58) * mm});
            skLineSegment(sketch, "E3173", {"start": v(87.68, -906.58) * mm, "end": v(87.5, -907.05) * mm});
            skLineSegment(sketch, "E3174", {"start": v(87.5, -907.05) * mm, "end": v(87.3, -907.52) * mm});
            skLineSegment(sketch, "E3175", {"start": v(87.3, -907.52) * mm, "end": v(87.1, -907.99) * mm});
            skLineSegment(sketch, "E3176", {"start": v(87.1, -907.99) * mm, "end": v(86.9, -908.45) * mm});
            skLineSegment(sketch, "E3177", {"start": v(86.9, -908.45) * mm, "end": v(86.67, -908.9) * mm});
            skLineSegment(sketch, "E3178", {"start": v(86.67, -908.9) * mm, "end": v(86.43, -909.35) * mm});
            skLineSegment(sketch, "E3179", {"start": v(86.43, -909.35) * mm, "end": v(86.19, -909.8) * mm});
            skLineSegment(sketch, "E3180", {"start": v(86.19, -909.8) * mm, "end": v(85.93, -910.24) * mm});
            skLineSegment(sketch, "E3181", {"start": v(85.93, -910.24) * mm, "end": v(85.66, -910.67) * mm});
            skLineSegment(sketch, "E3182", {"start": v(85.66, -910.67) * mm, "end": v(85.38, -911.1) * mm});
            skLineSegment(sketch, "E3183", {"start": v(85.38, -911.1) * mm, "end": v(85.09, -911.51) * mm});
            skLineSegment(sketch, "E3184", {"start": v(85.09, -911.51) * mm, "end": v(84.79, -911.92) * mm});
            skLineSegment(sketch, "E3185", {"start": v(84.79, -911.92) * mm, "end": v(84.47, -912.33) * mm});
            skLineSegment(sketch, "E3186", {"start": v(84.47, -912.33) * mm, "end": v(84.15, -912.73) * mm});
            skLineSegment(sketch, "E3187", {"start": v(84.15, -912.73) * mm, "end": v(83.82, -913.11) * mm});
            skLineSegment(sketch, "E3188", {"start": v(83.82, -913.11) * mm, "end": v(83.47, -913.5) * mm});
            skLineSegment(sketch, "E3189", {"start": v(83.47, -913.5) * mm, "end": v(83.12, -913.87) * mm});
            skLineSegment(sketch, "E3190", {"start": v(83.12, -913.87) * mm, "end": v(82.82, -914.16) * mm});
            skLineSegment(sketch, "E3191", {"start": v(82.82, -914.16) * mm, "end": v(82.52, -914.44) * mm});
            skLineSegment(sketch, "E3192", {"start": v(82.52, -914.44) * mm, "end": v(82.22, -914.72) * mm});
            skLineSegment(sketch, "E3193", {"start": v(82.22, -914.72) * mm, "end": v(81.9, -914.99) * mm});
            skLineSegment(sketch, "E3194", {"start": v(81.9, -914.99) * mm, "end": v(81.58, -915.24) * mm});
            skLineSegment(sketch, "E3195", {"start": v(81.58, -915.24) * mm, "end": v(81.26, -915.5) * mm});
            skLineSegment(sketch, "E3196", {"start": v(81.26, -915.5) * mm, "end": v(80.93, -915.74) * mm});
            skLineSegment(sketch, "E3197", {"start": v(80.93, -915.74) * mm, "end": v(80.6, -915.97) * mm});
            skLineSegment(sketch, "E3198", {"start": v(80.6, -915.97) * mm, "end": v(80.25, -916.2) * mm});
            skLineSegment(sketch, "E3199", {"start": v(80.25, -916.2) * mm, "end": v(79.9, -916.4) * mm});
            skLineSegment(sketch, "E3200", {"start": v(79.9, -916.4) * mm, "end": v(79.55, -916.61) * mm});
            skLineSegment(sketch, "E3201", {"start": v(79.55, -916.61) * mm, "end": v(79.2, -916.81) * mm});
            skLineSegment(sketch, "E3202", {"start": v(79.2, -916.81) * mm, "end": v(78.83, -917) * mm});
            skLineSegment(sketch, "E3203", {"start": v(78.83, -917) * mm, "end": v(78.46, -917.18) * mm});
            skLineSegment(sketch, "E3204", {"start": v(78.46, -917.18) * mm, "end": v(78.1, -917.35) * mm});
            skLineSegment(sketch, "E3205", {"start": v(78.1, -917.35) * mm, "end": v(77.72, -917.51) * mm});
            skLineSegment(sketch, "E3206", {"start": v(77.72, -917.51) * mm, "end": v(77.34, -917.66) * mm});
            skLineSegment(sketch, "E3207", {"start": v(77.34, -917.66) * mm, "end": v(76.96, -917.8) * mm});
            skLineSegment(sketch, "E3208", {"start": v(76.96, -917.8) * mm, "end": v(76.57, -917.94) * mm});
            skLineSegment(sketch, "E3209", {"start": v(76.57, -917.94) * mm, "end": v(76.18, -918.06) * mm});
            skLineSegment(sketch, "E3210", {"start": v(76.18, -918.06) * mm, "end": v(75.8, -918.17) * mm});
            skLineSegment(sketch, "E3211", {"start": v(75.8, -918.17) * mm, "end": v(75.4, -918.28) * mm});
            skLineSegment(sketch, "E3212", {"start": v(75.4, -918.28) * mm, "end": v(75, -918.37) * mm});
            skLineSegment(sketch, "E3213", {"start": v(75, -918.37) * mm, "end": v(74.6, -918.46) * mm});
            skLineSegment(sketch, "E3214", {"start": v(74.6, -918.46) * mm, "end": v(74.2, -918.53) * mm});
            skLineSegment(sketch, "E3215", {"start": v(74.2, -918.53) * mm, "end": v(73.8, -918.6) * mm});
            skLineSegment(sketch, "E3216", {"start": v(73.8, -918.6) * mm, "end": v(73.39, -918.65) * mm});
            skLineSegment(sketch, "E3217", {"start": v(73.39, -918.65) * mm, "end": v(72.98, -918.7) * mm});
            skLineSegment(sketch, "E3218", {"start": v(72.98, -918.7) * mm, "end": v(72.57, -918.73) * mm});
            skLineSegment(sketch, "E3219", {"start": v(72.57, -918.73) * mm, "end": v(72.16, -918.75) * mm});
            skLineSegment(sketch, "E3220", {"start": v(72.16, -918.75) * mm, "end": v(71.74, -918.77) * mm});
            skLineSegment(sketch, "E3221", {"start": v(71.74, -918.77) * mm, "end": v(71.33, -918.77) * mm});
            skLineSegment(sketch, "E3222", {"start": v(97.9, -918.2) * mm, "end": v(97.9, -878.25) * mm});
            skLineSegment(sketch, "E3223", {"start": v(97.9, -878.25) * mm, "end": v(115.46, -878.25) * mm});
            skLineSegment(sketch, "E3224", {"start": v(115.46, -878.25) * mm, "end": v(115.96, -878.25) * mm});
            skLineSegment(sketch, "E3225", {"start": v(115.96, -878.25) * mm, "end": v(116.45, -878.28) * mm});
            skLineSegment(sketch, "E3226", {"start": v(116.45, -878.28) * mm, "end": v(116.94, -878.34) * mm});
            skLineSegment(sketch, "E3227", {"start": v(116.94, -878.34) * mm, "end": v(117.42, -878.41) * mm});
            skLineSegment(sketch, "E3228", {"start": v(117.42, -878.41) * mm, "end": v(117.9, -878.52) * mm});
            skLineSegment(sketch, "E3229", {"start": v(117.9, -878.52) * mm, "end": v(118.37, -878.64) * mm});
            skLineSegment(sketch, "E3230", {"start": v(118.37, -878.64) * mm, "end": v(118.83, -878.8) * mm});
            skLineSegment(sketch, "E3231", {"start": v(118.83, -878.8) * mm, "end": v(119.28, -878.97) * mm});
            skLineSegment(sketch, "E3232", {"start": v(119.28, -878.97) * mm, "end": v(119.73, -879.17) * mm});
            skLineSegment(sketch, "E3233", {"start": v(119.73, -879.17) * mm, "end": v(120.16, -879.39) * mm});
            skLineSegment(sketch, "E3234", {"start": v(120.16, -879.39) * mm, "end": v(120.59, -879.63) * mm});
            skLineSegment(sketch, "E3235", {"start": v(120.59, -879.63) * mm, "end": v(121, -879.89) * mm});
            skLineSegment(sketch, "E3236", {"start": v(121, -879.89) * mm, "end": v(121.4, -880.17) * mm});
            skLineSegment(sketch, "E3237", {"start": v(121.4, -880.17) * mm, "end": v(121.78, -880.48) * mm});
            skLineSegment(sketch, "E3238", {"start": v(121.78, -880.48) * mm, "end": v(122.15, -880.8) * mm});
            skLineSegment(sketch, "E3239", {"start": v(122.15, -880.8) * mm, "end": v(122.5, -881.15) * mm});
            skLineSegment(sketch, "E3240", {"start": v(122.5, -881.15) * mm, "end": v(122.85, -881.5) * mm});
            skLineSegment(sketch, "E3241", {"start": v(122.85, -881.5) * mm, "end": v(123.17, -881.87) * mm});
            skLineSegment(sketch, "E3242", {"start": v(123.17, -881.87) * mm, "end": v(123.47, -882.25) * mm});
            skLineSegment(sketch, "E3243", {"start": v(123.47, -882.25) * mm, "end": v(123.75, -882.65) * mm});
            skLineSegment(sketch, "E3244", {"start": v(123.75, -882.65) * mm, "end": v(124, -883.05) * mm});
            skLineSegment(sketch, "E3245", {"start": v(124, -883.05) * mm, "end": v(124.25, -883.47) * mm});
            skLineSegment(sketch, "E3246", {"start": v(124.25, -883.47) * mm, "end": v(124.47, -883.9) * mm});
            skLineSegment(sketch, "E3247", {"start": v(124.47, -883.9) * mm, "end": v(124.67, -884.34) * mm});
            skLineSegment(sketch, "E3248", {"start": v(124.67, -884.34) * mm, "end": v(124.84, -884.8) * mm});
            skLineSegment(sketch, "E3249", {"start": v(124.84, -884.8) * mm, "end": v(125, -885.25) * mm});
            skLineSegment(sketch, "E3250", {"start": v(125, -885.25) * mm, "end": v(125.12, -885.72) * mm});
            skLineSegment(sketch, "E3251", {"start": v(125.12, -885.72) * mm, "end": v(125.23, -886.2) * mm});
            skLineSegment(sketch, "E3252", {"start": v(125.23, -886.2) * mm, "end": v(125.32, -886.67) * mm});
            skLineSegment(sketch, "E3253", {"start": v(125.32, -886.67) * mm, "end": v(125.38, -887.15) * mm});
            skLineSegment(sketch, "E3254", {"start": v(125.38, -887.15) * mm, "end": v(125.41, -887.64) * mm});
            skLineSegment(sketch, "E3255", {"start": v(125.41, -887.64) * mm, "end": v(125.42, -888.13) * mm});
            skLineSegment(sketch, "E3256", {"start": v(125.42, -888.13) * mm, "end": v(125.43, -888.63) * mm});
            skLineSegment(sketch, "E3257", {"start": v(125.43, -888.63) * mm, "end": v(125.4, -889.13) * mm});
            skLineSegment(sketch, "E3258", {"start": v(125.4, -889.13) * mm, "end": v(125.35, -889.62) * mm});
            skLineSegment(sketch, "E3259", {"start": v(125.35, -889.62) * mm, "end": v(125.28, -890.11) * mm});
            skLineSegment(sketch, "E3260", {"start": v(125.28, -890.11) * mm, "end": v(125.18, -890.6) * mm});
            skLineSegment(sketch, "E3261", {"start": v(125.18, -890.6) * mm, "end": v(125.06, -891.08) * mm});
            skLineSegment(sketch, "E3262", {"start": v(125.06, -891.08) * mm, "end": v(124.91, -891.55) * mm});
            skLineSegment(sketch, "E3263", {"start": v(124.91, -891.55) * mm, "end": v(124.74, -892.02) * mm});
            skLineSegment(sketch, "E3264", {"start": v(124.74, -892.02) * mm, "end": v(124.55, -892.47) * mm});
            skLineSegment(sketch, "E3265", {"start": v(124.55, -892.47) * mm, "end": v(124.34, -892.92) * mm});
            skLineSegment(sketch, "E3266", {"start": v(124.34, -892.92) * mm, "end": v(124.1, -893.35) * mm});
            skLineSegment(sketch, "E3267", {"start": v(124.1, -893.35) * mm, "end": v(123.84, -893.77) * mm});
            skLineSegment(sketch, "E3268", {"start": v(123.84, -893.77) * mm, "end": v(123.56, -894.18) * mm});
            skLineSegment(sketch, "E3269", {"start": v(123.56, -894.18) * mm, "end": v(123.25, -894.58) * mm});
            skLineSegment(sketch, "E3270", {"start": v(123.25, -894.58) * mm, "end": v(122.93, -894.96) * mm});
            skLineSegment(sketch, "E3271", {"start": v(122.93, -894.96) * mm, "end": v(122.59, -895.32) * mm});
            skLineSegment(sketch, "E3272", {"start": v(122.59, -895.32) * mm, "end": v(122.22, -895.67) * mm});
            skLineSegment(sketch, "E3273", {"start": v(122.22, -895.67) * mm, "end": v(121.85, -895.99) * mm});
            skLineSegment(sketch, "E3274", {"start": v(121.85, -895.99) * mm, "end": v(121.46, -896.3) * mm});
            skLineSegment(sketch, "E3275", {"start": v(121.46, -896.3) * mm, "end": v(121.05, -896.58) * mm});
            skLineSegment(sketch, "E3276", {"start": v(121.05, -896.58) * mm, "end": v(120.64, -896.84) * mm});
            skLineSegment(sketch, "E3277", {"start": v(120.64, -896.84) * mm, "end": v(120.2, -897.08) * mm});
            skLineSegment(sketch, "E3278", {"start": v(120.2, -897.08) * mm, "end": v(119.77, -897.3) * mm});
            skLineSegment(sketch, "E3279", {"start": v(119.77, -897.3) * mm, "end": v(119.32, -897.5) * mm});
            skLineSegment(sketch, "E3280", {"start": v(119.32, -897.5) * mm, "end": v(118.86, -897.67) * mm});
            skLineSegment(sketch, "E3281", {"start": v(118.86, -897.67) * mm, "end": v(118.4, -897.82) * mm});
            skLineSegment(sketch, "E3282", {"start": v(118.4, -897.82) * mm, "end": v(117.92, -897.95) * mm});
            skLineSegment(sketch, "E3283", {"start": v(117.92, -897.95) * mm, "end": v(117.43, -898.05) * mm});
            skLineSegment(sketch, "E3284", {"start": v(117.43, -898.05) * mm, "end": v(116.95, -898.13) * mm});
            skLineSegment(sketch, "E3285", {"start": v(116.95, -898.13) * mm, "end": v(116.46, -898.18) * mm});
            skLineSegment(sketch, "E3286", {"start": v(116.46, -898.18) * mm, "end": v(115.96, -898.21) * mm});
            skLineSegment(sketch, "E3287", {"start": v(115.96, -898.21) * mm, "end": v(115.46, -898.22) * mm});
            skLineSegment(sketch, "E3288", {"start": v(115.46, -898.22) * mm, "end": v(97.9, -898.22) * mm});
            skLineSegment(sketch, "E3289", {"start": v(115.46, -898.22) * mm, "end": v(115.87, -898.22) * mm});
            skLineSegment(sketch, "E3290", {"start": v(115.87, -898.22) * mm, "end": v(116.28, -898.24) * mm});
            skLineSegment(sketch, "E3291", {"start": v(116.28, -898.24) * mm, "end": v(116.68, -898.29) * mm});
            skLineSegment(sketch, "E3292", {"start": v(116.68, -898.29) * mm, "end": v(117.08, -898.35) * mm});
            skLineSegment(sketch, "E3293", {"start": v(117.08, -898.35) * mm, "end": v(117.48, -898.44) * mm});
            skLineSegment(sketch, "E3294", {"start": v(117.48, -898.44) * mm, "end": v(117.87, -898.54) * mm});
            skLineSegment(sketch, "E3295", {"start": v(117.87, -898.54) * mm, "end": v(118.26, -898.66) * mm});
            skLineSegment(sketch, "E3296", {"start": v(118.26, -898.66) * mm, "end": v(118.63, -898.8) * mm});
            skLineSegment(sketch, "E3297", {"start": v(118.63, -898.8) * mm, "end": v(119, -898.97) * mm});
            skLineSegment(sketch, "E3298", {"start": v(119, -898.97) * mm, "end": v(119.37, -899.15) * mm});
            skLineSegment(sketch, "E3299", {"start": v(119.37, -899.15) * mm, "end": v(119.72, -899.35) * mm});
            skLineSegment(sketch, "E3300", {"start": v(119.72, -899.35) * mm, "end": v(120.06, -899.56) * mm});
            skLineSegment(sketch, "E3301", {"start": v(120.06, -899.56) * mm, "end": v(120.4, -899.8) * mm});
            skLineSegment(sketch, "E3302", {"start": v(120.4, -899.8) * mm, "end": v(120.71, -900.05) * mm});
            skLineSegment(sketch, "E3303", {"start": v(120.71, -900.05) * mm, "end": v(121.02, -900.32) * mm});
            skLineSegment(sketch, "E3304", {"start": v(121.02, -900.32) * mm, "end": v(121.31, -900.6) * mm});
            skLineSegment(sketch, "E3305", {"start": v(121.31, -900.6) * mm, "end": v(121.65, -901.1) * mm});
            skLineSegment(sketch, "E3306", {"start": v(121.65, -901.1) * mm, "end": v(121.97, -901.62) * mm});
            skLineSegment(sketch, "E3307", {"start": v(121.97, -901.62) * mm, "end": v(122.26, -902.14) * mm});
            skLineSegment(sketch, "E3308", {"start": v(122.26, -902.14) * mm, "end": v(122.53, -902.68) * mm});
            skLineSegment(sketch, "E3309", {"start": v(122.53, -902.68) * mm, "end": v(122.78, -903.23) * mm});
            skLineSegment(sketch, "E3310", {"start": v(122.78, -903.23) * mm, "end": v(123, -903.78) * mm});
            skLineSegment(sketch, "E3311", {"start": v(123, -903.78) * mm, "end": v(123.2, -904.35) * mm});
            skLineSegment(sketch, "E3312", {"start": v(123.2, -904.35) * mm, "end": v(123.36, -904.92) * mm});
            skLineSegment(sketch, "E3313", {"start": v(123.36, -904.92) * mm, "end": v(123.5, -905.5) * mm});
            skLineSegment(sketch, "E3314", {"start": v(123.5, -905.5) * mm, "end": v(123.62, -906.1) * mm});
            skLineSegment(sketch, "E3315", {"start": v(123.62, -906.1) * mm, "end": v(123.72, -906.68) * mm});
            skLineSegment(sketch, "E3316", {"start": v(123.72, -906.68) * mm, "end": v(123.78, -907.28) * mm});
            skLineSegment(sketch, "E3317", {"start": v(123.78, -907.28) * mm, "end": v(123.82, -907.88) * mm});
            skLineSegment(sketch, "E3318", {"start": v(123.82, -907.88) * mm, "end": v(123.83, -908.48) * mm});
            skLineSegment(sketch, "E3319", {"start": v(123.83, -908.48) * mm, "end": v(123.82, -909.09) * mm});
            skLineSegment(sketch, "E3320", {"start": v(123.82, -909.09) * mm, "end": v(123.77, -909.69) * mm});
            skLineSegment(sketch, "E3321", {"start": v(123.77, -909.69) * mm, "end": v(123.77, -910.23) * mm});
            skLineSegment(sketch, "E3322", {"start": v(123.77, -910.23) * mm, "end": v(123.77, -910.76) * mm});
            skLineSegment(sketch, "E3323", {"start": v(123.77, -910.76) * mm, "end": v(123.78, -911.3) * mm});
            skLineSegment(sketch, "E3324", {"start": v(123.78, -911.3) * mm, "end": v(123.8, -911.84) * mm});
            skLineSegment(sketch, "E3325", {"start": v(123.8, -911.84) * mm, "end": v(123.83, -912.38) * mm});
            skLineSegment(sketch, "E3326", {"start": v(123.83, -912.38) * mm, "end": v(123.87, -912.91) * mm});
            skLineSegment(sketch, "E3327", {"start": v(123.87, -912.91) * mm, "end": v(123.92, -913.45) * mm});
            skLineSegment(sketch, "E3328", {"start": v(123.92, -913.45) * mm, "end": v(123.98, -913.99) * mm});
            skLineSegment(sketch, "E3329", {"start": v(123.98, -913.99) * mm, "end": v(124.05, -914.52) * mm});
            skLineSegment(sketch, "E3330", {"start": v(124.05, -914.52) * mm, "end": v(124.13, -915.05) * mm});
            skLineSegment(sketch, "E3331", {"start": v(124.13, -915.05) * mm, "end": v(124.22, -915.58) * mm});
            skLineSegment(sketch, "E3332", {"start": v(124.22, -915.58) * mm, "end": v(124.32, -916.11) * mm});
            skLineSegment(sketch, "E3333", {"start": v(124.32, -916.11) * mm, "end": v(124.43, -916.64) * mm});
            skLineSegment(sketch, "E3334", {"start": v(124.43, -916.64) * mm, "end": v(124.54, -917.17) * mm});
            skLineSegment(sketch, "E3335", {"start": v(124.54, -917.17) * mm, "end": v(124.67, -917.69) * mm});
            skLineSegment(sketch, "E3336", {"start": v(124.67, -917.69) * mm, "end": v(124.8, -918.2) * mm});
            skLineSegment(sketch, "E3337", {"start": v(160.54, -909.4) * mm, "end": v(160.8, -909.9) * mm});
            skLineSegment(sketch, "E3338", {"start": v(160.8, -909.9) * mm, "end": v(161.06, -910.4) * mm});
            skLineSegment(sketch, "E3339", {"start": v(161.06, -910.4) * mm, "end": v(161.35, -910.86) * mm});
            skLineSegment(sketch, "E3340", {"start": v(161.35, -910.86) * mm, "end": v(161.65, -911.33) * mm});
            skLineSegment(sketch, "E3341", {"start": v(161.65, -911.33) * mm, "end": v(161.97, -911.78) * mm});
            skLineSegment(sketch, "E3342", {"start": v(161.97, -911.78) * mm, "end": v(162.3, -912.21) * mm});
            skLineSegment(sketch, "E3343", {"start": v(162.3, -912.21) * mm, "end": v(162.64, -912.63) * mm});
            skLineSegment(sketch, "E3344", {"start": v(162.64, -912.63) * mm, "end": v(163, -913.05) * mm});
            skLineSegment(sketch, "E3345", {"start": v(163, -913.05) * mm, "end": v(163.37, -913.44) * mm});
            skLineSegment(sketch, "E3346", {"start": v(163.37, -913.44) * mm, "end": v(163.76, -913.83) * mm});
            skLineSegment(sketch, "E3347", {"start": v(163.76, -913.83) * mm, "end": v(164.16, -914.2) * mm});
            skLineSegment(sketch, "E3348", {"start": v(164.16, -914.2) * mm, "end": v(164.57, -914.55) * mm});
            skLineSegment(sketch, "E3349", {"start": v(164.57, -914.55) * mm, "end": v(164.99, -914.89) * mm});
            skLineSegment(sketch, "E3350", {"start": v(164.99, -914.89) * mm, "end": v(165.42, -915.21) * mm});
            skLineSegment(sketch, "E3351", {"start": v(165.42, -915.21) * mm, "end": v(165.87, -915.52) * mm});
            skLineSegment(sketch, "E3352", {"start": v(165.87, -915.52) * mm, "end": v(166.32, -915.82) * mm});
            skLineSegment(sketch, "E3353", {"start": v(166.32, -915.82) * mm, "end": v(166.78, -916.1) * mm});
            skLineSegment(sketch, "E3354", {"start": v(166.78, -916.1) * mm, "end": v(167.26, -916.36) * mm});
            skLineSegment(sketch, "E3355", {"start": v(167.26, -916.36) * mm, "end": v(167.74, -916.6) * mm});
            skLineSegment(sketch, "E3356", {"start": v(167.74, -916.6) * mm, "end": v(168.23, -916.84) * mm});
            skLineSegment(sketch, "E3357", {"start": v(168.23, -916.84) * mm, "end": v(168.73, -917.05) * mm});
            skLineSegment(sketch, "E3358", {"start": v(168.73, -917.05) * mm, "end": v(169.23, -917.25) * mm});
            skLineSegment(sketch, "E3359", {"start": v(169.23, -917.25) * mm, "end": v(169.75, -917.43) * mm});
            skLineSegment(sketch, "E3360", {"start": v(169.75, -917.43) * mm, "end": v(170.27, -917.59) * mm});
            skLineSegment(sketch, "E3361", {"start": v(170.27, -917.59) * mm, "end": v(170.8, -917.73) * mm});
            skLineSegment(sketch, "E3362", {"start": v(170.8, -917.73) * mm, "end": v(171.33, -917.86) * mm});
            skLineSegment(sketch, "E3363", {"start": v(171.33, -917.86) * mm, "end": v(171.86, -917.96) * mm});
            skLineSegment(sketch, "E3364", {"start": v(171.86, -917.96) * mm, "end": v(172.4, -918.05) * mm});
            skLineSegment(sketch, "E3365", {"start": v(172.4, -918.05) * mm, "end": v(172.95, -918.12) * mm});
            skLineSegment(sketch, "E3366", {"start": v(172.95, -918.12) * mm, "end": v(173.5, -918.17) * mm});
            skLineSegment(sketch, "E3367", {"start": v(173.5, -918.17) * mm, "end": v(174.06, -918.2) * mm});
            skLineSegment(sketch, "E3368", {"start": v(174.06, -918.2) * mm, "end": v(174.62, -918.2) * mm});
            skLineSegment(sketch, "E3369", {"start": v(174.62, -918.2) * mm, "end": v(175.02, -918.2) * mm});
            skLineSegment(sketch, "E3370", {"start": v(175.02, -918.2) * mm, "end": v(175.4, -918.2) * mm});
            skLineSegment(sketch, "E3371", {"start": v(175.4, -918.2) * mm, "end": v(175.79, -918.17) * mm});
            skLineSegment(sketch, "E3372", {"start": v(175.79, -918.17) * mm, "end": v(176.16, -918.14) * mm});
            skLineSegment(sketch, "E3373", {"start": v(176.16, -918.14) * mm, "end": v(176.54, -918.1) * mm});
            skLineSegment(sketch, "E3374", {"start": v(176.54, -918.1) * mm, "end": v(176.9, -918.05) * mm});
            skLineSegment(sketch, "E3375", {"start": v(176.9, -918.05) * mm, "end": v(177.26, -917.99) * mm});
            skLineSegment(sketch, "E3376", {"start": v(177.26, -917.99) * mm, "end": v(177.61, -917.92) * mm});
            skLineSegment(sketch, "E3377", {"start": v(177.61, -917.92) * mm, "end": v(177.96, -917.85) * mm});
            skLineSegment(sketch, "E3378", {"start": v(177.96, -917.85) * mm, "end": v(178.3, -917.76) * mm});
            skLineSegment(sketch, "E3379", {"start": v(178.3, -917.76) * mm, "end": v(178.63, -917.67) * mm});
            skLineSegment(sketch, "E3380", {"start": v(178.63, -917.67) * mm, "end": v(178.96, -917.58) * mm});
            skLineSegment(sketch, "E3381", {"start": v(178.96, -917.58) * mm, "end": v(179.28, -917.47) * mm});
            skLineSegment(sketch, "E3382", {"start": v(179.28, -917.47) * mm, "end": v(179.6, -917.36) * mm});
            skLineSegment(sketch, "E3383", {"start": v(179.6, -917.36) * mm, "end": v(179.9, -917.24) * mm});
            skLineSegment(sketch, "E3384", {"start": v(179.9, -917.24) * mm, "end": v(180.2, -917.1) * mm});
            skLineSegment(sketch, "E3385", {"start": v(180.2, -917.1) * mm, "end": v(180.5, -916.97) * mm});
            skLineSegment(sketch, "E3386", {"start": v(180.5, -916.97) * mm, "end": v(180.79, -916.83) * mm});
            skLineSegment(sketch, "E3387", {"start": v(180.79, -916.83) * mm, "end": v(181.07, -916.68) * mm});
            skLineSegment(sketch, "E3388", {"start": v(181.07, -916.68) * mm, "end": v(181.35, -916.53) * mm});
            skLineSegment(sketch, "E3389", {"start": v(181.35, -916.53) * mm, "end": v(181.62, -916.37) * mm});
            skLineSegment(sketch, "E3390", {"start": v(181.62, -916.37) * mm, "end": v(181.88, -916.2) * mm});
            skLineSegment(sketch, "E3391", {"start": v(181.88, -916.2) * mm, "end": v(182.14, -916.03) * mm});
            skLineSegment(sketch, "E3392", {"start": v(182.14, -916.03) * mm, "end": v(182.4, -915.85) * mm});
            skLineSegment(sketch, "E3393", {"start": v(182.4, -915.85) * mm, "end": v(182.64, -915.66) * mm});
            skLineSegment(sketch, "E3394", {"start": v(182.64, -915.66) * mm, "end": v(182.88, -915.47) * mm});
            skLineSegment(sketch, "E3395", {"start": v(182.88, -915.47) * mm, "end": v(183.11, -915.27) * mm});
            skLineSegment(sketch, "E3396", {"start": v(183.11, -915.27) * mm, "end": v(183.34, -915.07) * mm});
            skLineSegment(sketch, "E3397", {"start": v(183.34, -915.07) * mm, "end": v(183.56, -914.86) * mm});
            skLineSegment(sketch, "E3398", {"start": v(183.56, -914.86) * mm, "end": v(183.78, -914.65) * mm});
            skLineSegment(sketch, "E3399", {"start": v(183.78, -914.65) * mm, "end": v(183.99, -914.43) * mm});
            skLineSegment(sketch, "E3400", {"start": v(183.99, -914.43) * mm, "end": v(184.19, -914.2) * mm});
            skLineSegment(sketch, "E3401", {"start": v(184.19, -914.2) * mm, "end": v(184.39, -913.98) * mm});
            skLineSegment(sketch, "E3402", {"start": v(184.39, -913.98) * mm, "end": v(184.58, -913.75) * mm});
            skLineSegment(sketch, "E3403", {"start": v(184.58, -913.75) * mm, "end": v(184.76, -913.51) * mm});
            skLineSegment(sketch, "E3404", {"start": v(184.76, -913.51) * mm, "end": v(184.94, -913.27) * mm});
            skLineSegment(sketch, "E3405", {"start": v(184.94, -913.27) * mm, "end": v(185.27, -912.78) * mm});
            skLineSegment(sketch, "E3406", {"start": v(185.27, -912.78) * mm, "end": v(185.59, -912.27) * mm});
            skLineSegment(sketch, "E3407", {"start": v(185.59, -912.27) * mm, "end": v(185.87, -911.75) * mm});
            skLineSegment(sketch, "E3408", {"start": v(185.87, -911.75) * mm, "end": v(186.13, -911.21) * mm});
            skLineSegment(sketch, "E3409", {"start": v(186.13, -911.21) * mm, "end": v(186.37, -910.67) * mm});
            skLineSegment(sketch, "E3410", {"start": v(186.37, -910.67) * mm, "end": v(186.58, -910.1) * mm});
            skLineSegment(sketch, "E3411", {"start": v(186.58, -910.1) * mm, "end": v(186.77, -909.54) * mm});
            skLineSegment(sketch, "E3412", {"start": v(186.77, -909.54) * mm, "end": v(186.93, -908.97) * mm});
            skLineSegment(sketch, "E3413", {"start": v(186.93, -908.97) * mm, "end": v(187.07, -908.38) * mm});
            skLineSegment(sketch, "E3414", {"start": v(187.07, -908.38) * mm, "end": v(187.18, -907.8) * mm});
            skLineSegment(sketch, "E3415", {"start": v(187.18, -907.8) * mm, "end": v(187.27, -907.2) * mm});
            skLineSegment(sketch, "E3416", {"start": v(187.27, -907.2) * mm, "end": v(187.33, -906.6) * mm});
            skLineSegment(sketch, "E3417", {"start": v(187.33, -906.6) * mm, "end": v(187.37, -906) * mm});
            skLineSegment(sketch, "E3418", {"start": v(187.37, -906) * mm, "end": v(187.38, -905.4) * mm});
            skLineSegment(sketch, "E3419", {"start": v(187.38, -905.4) * mm, "end": v(187.37, -904.8) * mm});
            skLineSegment(sketch, "E3420", {"start": v(187.37, -904.8) * mm, "end": v(187.33, -904.21) * mm});
            skLineSegment(sketch, "E3421", {"start": v(187.33, -904.21) * mm, "end": v(187.27, -903.61) * mm});
            skLineSegment(sketch, "E3422", {"start": v(187.27, -903.61) * mm, "end": v(187.18, -903.02) * mm});
            skLineSegment(sketch, "E3423", {"start": v(187.18, -903.02) * mm, "end": v(187.07, -902.43) * mm});
            skLineSegment(sketch, "E3424", {"start": v(187.07, -902.43) * mm, "end": v(186.93, -901.85) * mm});
            skLineSegment(sketch, "E3425", {"start": v(186.93, -901.85) * mm, "end": v(186.77, -901.28) * mm});
            skLineSegment(sketch, "E3426", {"start": v(186.77, -901.28) * mm, "end": v(186.58, -900.7) * mm});
            skLineSegment(sketch, "E3427", {"start": v(186.58, -900.7) * mm, "end": v(186.37, -900.15) * mm});
            skLineSegment(sketch, "E3428", {"start": v(186.37, -900.15) * mm, "end": v(186.13, -899.6) * mm});
            skLineSegment(sketch, "E3429", {"start": v(186.13, -899.6) * mm, "end": v(185.87, -899.07) * mm});
            skLineSegment(sketch, "E3430", {"start": v(185.87, -899.07) * mm, "end": v(185.59, -898.55) * mm});
            skLineSegment(sketch, "E3431", {"start": v(185.59, -898.55) * mm, "end": v(185.27, -898.04) * mm});
            skLineSegment(sketch, "E3432", {"start": v(185.27, -898.04) * mm, "end": v(184.94, -897.54) * mm});
            skLineSegment(sketch, "E3433", {"start": v(184.94, -897.54) * mm, "end": v(184.76, -897.3) * mm});
            skLineSegment(sketch, "E3434", {"start": v(184.76, -897.3) * mm, "end": v(184.58, -897.07) * mm});
            skLineSegment(sketch, "E3435", {"start": v(184.58, -897.07) * mm, "end": v(184.39, -896.84) * mm});
            skLineSegment(sketch, "E3436", {"start": v(184.39, -896.84) * mm, "end": v(184.19, -896.6) * mm});
            skLineSegment(sketch, "E3437", {"start": v(184.19, -896.6) * mm, "end": v(183.99, -896.39) * mm});
            skLineSegment(sketch, "E3438", {"start": v(183.99, -896.39) * mm, "end": v(183.78, -896.17) * mm});
            skLineSegment(sketch, "E3439", {"start": v(183.78, -896.17) * mm, "end": v(183.56, -895.96) * mm});
            skLineSegment(sketch, "E3440", {"start": v(183.56, -895.96) * mm, "end": v(183.34, -895.75) * mm});
            skLineSegment(sketch, "E3441", {"start": v(183.34, -895.75) * mm, "end": v(183.11, -895.55) * mm});
            skLineSegment(sketch, "E3442", {"start": v(183.11, -895.55) * mm, "end": v(182.88, -895.35) * mm});
            skLineSegment(sketch, "E3443", {"start": v(182.88, -895.35) * mm, "end": v(182.64, -895.16) * mm});
            skLineSegment(sketch, "E3444", {"start": v(182.64, -895.16) * mm, "end": v(182.4, -894.97) * mm});
            skLineSegment(sketch, "E3445", {"start": v(182.4, -894.97) * mm, "end": v(182.14, -894.8) * mm});
            skLineSegment(sketch, "E3446", {"start": v(182.14, -894.8) * mm, "end": v(181.88, -894.62) * mm});
            skLineSegment(sketch, "E3447", {"start": v(181.88, -894.62) * mm, "end": v(181.62, -894.45) * mm});
            skLineSegment(sketch, "E3448", {"start": v(181.62, -894.45) * mm, "end": v(181.35, -894.29) * mm});
            skLineSegment(sketch, "E3449", {"start": v(181.35, -894.29) * mm, "end": v(181.07, -894.13) * mm});
            skLineSegment(sketch, "E3450", {"start": v(181.07, -894.13) * mm, "end": v(180.79, -893.99) * mm});
            skLineSegment(sketch, "E3451", {"start": v(180.79, -893.99) * mm, "end": v(180.5, -893.84) * mm});
            skLineSegment(sketch, "E3452", {"start": v(180.5, -893.84) * mm, "end": v(180.2, -893.7) * mm});
            skLineSegment(sketch, "E3453", {"start": v(180.2, -893.7) * mm, "end": v(179.9, -893.58) * mm});
            skLineSegment(sketch, "E3454", {"start": v(179.9, -893.58) * mm, "end": v(179.6, -893.46) * mm});
            skLineSegment(sketch, "E3455", {"start": v(179.6, -893.46) * mm, "end": v(179.28, -893.35) * mm});
            skLineSegment(sketch, "E3456", {"start": v(179.28, -893.35) * mm, "end": v(178.96, -893.24) * mm});
            skLineSegment(sketch, "E3457", {"start": v(178.96, -893.24) * mm, "end": v(178.63, -893.14) * mm});
            skLineSegment(sketch, "E3458", {"start": v(178.63, -893.14) * mm, "end": v(178.3, -893.05) * mm});
            skLineSegment(sketch, "E3459", {"start": v(178.3, -893.05) * mm, "end": v(177.96, -892.97) * mm});
            skLineSegment(sketch, "E3460", {"start": v(177.96, -892.97) * mm, "end": v(177.61, -892.9) * mm});
            skLineSegment(sketch, "E3461", {"start": v(177.61, -892.9) * mm, "end": v(177.26, -892.83) * mm});
            skLineSegment(sketch, "E3462", {"start": v(177.26, -892.83) * mm, "end": v(176.9, -892.77) * mm});
            skLineSegment(sketch, "E3463", {"start": v(176.9, -892.77) * mm, "end": v(176.54, -892.72) * mm});
            skLineSegment(sketch, "E3464", {"start": v(176.54, -892.72) * mm, "end": v(176.16, -892.68) * mm});
            skLineSegment(sketch, "E3465", {"start": v(176.16, -892.68) * mm, "end": v(175.79, -892.65) * mm});
            skLineSegment(sketch, "E3466", {"start": v(175.79, -892.65) * mm, "end": v(175.4, -892.63) * mm});
            skLineSegment(sketch, "E3467", {"start": v(175.4, -892.63) * mm, "end": v(175.02, -892.61) * mm});
            skLineSegment(sketch, "E3468", {"start": v(175.02, -892.61) * mm, "end": v(174.62, -892.6) * mm});
            skLineSegment(sketch, "E3469", {"start": v(174.62, -892.6) * mm, "end": v(174.18, -892.61) * mm});
            skLineSegment(sketch, "E3470", {"start": v(174.18, -892.61) * mm, "end": v(173.75, -892.63) * mm});
            skLineSegment(sketch, "E3471", {"start": v(173.75, -892.63) * mm, "end": v(173.31, -892.66) * mm});
            skLineSegment(sketch, "E3472", {"start": v(173.31, -892.66) * mm, "end": v(172.88, -892.7) * mm});
            skLineSegment(sketch, "E3473", {"start": v(172.88, -892.7) * mm, "end": v(172.45, -892.74) * mm});
            skLineSegment(sketch, "E3474", {"start": v(172.45, -892.74) * mm, "end": v(172.02, -892.8) * mm});
            skLineSegment(sketch, "E3475", {"start": v(172.02, -892.8) * mm, "end": v(171.6, -892.87) * mm});
            skLineSegment(sketch, "E3476", {"start": v(171.6, -892.87) * mm, "end": v(171.17, -892.95) * mm});
            skLineSegment(sketch, "E3477", {"start": v(171.17, -892.95) * mm, "end": v(170.74, -893.04) * mm});
            skLineSegment(sketch, "E3478", {"start": v(170.74, -893.04) * mm, "end": v(170.32, -893.14) * mm});
            skLineSegment(sketch, "E3479", {"start": v(170.32, -893.14) * mm, "end": v(169.9, -893.25) * mm});
            skLineSegment(sketch, "E3480", {"start": v(169.9, -893.25) * mm, "end": v(169.5, -893.36) * mm});
            skLineSegment(sketch, "E3481", {"start": v(169.5, -893.36) * mm, "end": v(169.08, -893.5) * mm});
            skLineSegment(sketch, "E3482", {"start": v(169.08, -893.5) * mm, "end": v(168.67, -893.63) * mm});
            skLineSegment(sketch, "E3483", {"start": v(168.67, -893.63) * mm, "end": v(168.27, -893.78) * mm});
            skLineSegment(sketch, "E3484", {"start": v(168.27, -893.78) * mm, "end": v(167.87, -893.94) * mm});
            skLineSegment(sketch, "E3485", {"start": v(167.87, -893.94) * mm, "end": v(167.47, -894.1) * mm});
            skLineSegment(sketch, "E3486", {"start": v(167.47, -894.1) * mm, "end": v(167.08, -894.28) * mm});
            skLineSegment(sketch, "E3487", {"start": v(167.08, -894.28) * mm, "end": v(166.7, -894.47) * mm});
            skLineSegment(sketch, "E3488", {"start": v(166.7, -894.47) * mm, "end": v(166.31, -894.67) * mm});
            skLineSegment(sketch, "E3489", {"start": v(166.31, -894.67) * mm, "end": v(165.93, -894.87) * mm});
            skLineSegment(sketch, "E3490", {"start": v(165.93, -894.87) * mm, "end": v(165.56, -895.09) * mm});
            skLineSegment(sketch, "E3491", {"start": v(165.56, -895.09) * mm, "end": v(165.2, -895.31) * mm});
            skLineSegment(sketch, "E3492", {"start": v(165.2, -895.31) * mm, "end": v(164.83, -895.55) * mm});
            skLineSegment(sketch, "E3493", {"start": v(164.83, -895.55) * mm, "end": v(164.47, -895.79) * mm});
            skLineSegment(sketch, "E3494", {"start": v(164.47, -895.79) * mm, "end": v(164.12, -896.04) * mm});
            skLineSegment(sketch, "E3495", {"start": v(164.12, -896.04) * mm, "end": v(163.77, -896.3) * mm});
            skLineSegment(sketch, "E3496", {"start": v(163.77, -896.3) * mm, "end": v(163.43, -896.57) * mm});
            skLineSegment(sketch, "E3497", {"start": v(163.43, -896.57) * mm, "end": v(163.1, -896.84) * mm});
            skLineSegment(sketch, "E3498", {"start": v(163.1, -896.84) * mm, "end": v(162.77, -897.13) * mm});
            skLineSegment(sketch, "E3499", {"start": v(162.77, -897.13) * mm, "end": v(162.45, -897.43) * mm});
            skLineSegment(sketch, "E3500", {"start": v(162.45, -897.43) * mm, "end": v(162.14, -897.73) * mm});
            skLineSegment(sketch, "E3501", {"start": v(162.14, -897.73) * mm, "end": v(160.54, -897.4) * mm});
            skLineSegment(sketch, "E3502", {"start": v(160.54, -897.4) * mm, "end": v(163.9, -878.2) * mm});
            skLineSegment(sketch, "E3503", {"start": v(163.9, -878.2) * mm, "end": v(184.22, -878.2) * mm});
            skArc(sketch, "E3504", {"start": v(-519.75, -900.43) * mm, "mid": v(-518.65, -903.08) * mm, "end": v(-516, -904.18) * mm});
            skArc(sketch, "E3505", {"start": v(-516, -904.18) * mm, "mid": v(-513.35, -903.08) * mm, "end": v(-512.25, -900.43) * mm});
            skArc(sketch, "E3506", {"start": v(-512.25, -900.43) * mm, "mid": v(-513.35, -897.78) * mm, "end": v(-516, -896.68) * mm});
            skArc(sketch, "E3507", {"start": v(-516, -896.68) * mm, "mid": v(-518.65, -897.78) * mm, "end": v(-519.75, -900.43) * mm});
            skArc(sketch, "E3508", {"start": v(-466.24, -900.43) * mm, "mid": v(-465.14, -903.08) * mm, "end": v(-462.5, -904.18) * mm});
            skArc(sketch, "E3509", {"start": v(-462.5, -904.18) * mm, "mid": v(-459.84, -903.08) * mm, "end": v(-458.74, -900.43) * mm});
            skArc(sketch, "E3510", {"start": v(-458.74, -900.43) * mm, "mid": v(-459.84, -897.78) * mm, "end": v(-462.5, -896.68) * mm});
            skArc(sketch, "E3511", {"start": v(-462.5, -896.68) * mm, "mid": v(-465.14, -897.78) * mm, "end": v(-466.24, -900.43) * mm});
            skArc(sketch, "E3512", {"start": v(-519.75, -1050.43) * mm, "mid": v(-518.65, -1053.08) * mm, "end": v(-516, -1054.18) * mm});
            skArc(sketch, "E3513", {"start": v(-516, -1054.18) * mm, "mid": v(-513.35, -1053.08) * mm, "end": v(-512.25, -1050.43) * mm});
            skArc(sketch, "E3514", {"start": v(-512.25, -1050.43) * mm, "mid": v(-513.35, -1047.78) * mm, "end": v(-516, -1046.68) * mm});
            skArc(sketch, "E3515", {"start": v(-516, -1046.68) * mm, "mid": v(-518.65, -1047.78) * mm, "end": v(-519.75, -1050.43) * mm});
            skArc(sketch, "E3516", {"start": v(-466.24, -1050.43) * mm, "mid": v(-465.14, -1053.08) * mm, "end": v(-462.5, -1054.18) * mm});
            skArc(sketch, "E3517", {"start": v(-462.5, -1054.18) * mm, "mid": v(-459.84, -1053.08) * mm, "end": v(-458.74, -1050.43) * mm});
            skArc(sketch, "E3518", {"start": v(-458.74, -1050.43) * mm, "mid": v(-459.84, -1047.78) * mm, "end": v(-462.5, -1046.68) * mm});
            skArc(sketch, "E3519", {"start": v(-462.5, -1046.68) * mm, "mid": v(-465.14, -1047.78) * mm, "end": v(-466.24, -1050.43) * mm});
            skArc(sketch, "E3520", {"start": v(-519.75, -750.43) * mm, "mid": v(-518.65, -753.08) * mm, "end": v(-516, -754.18) * mm});
            skArc(sketch, "E3521", {"start": v(-516, -754.18) * mm, "mid": v(-513.35, -753.08) * mm, "end": v(-512.25, -750.43) * mm});
            skArc(sketch, "E3522", {"start": v(-512.25, -750.43) * mm, "mid": v(-513.35, -747.78) * mm, "end": v(-516, -746.68) * mm});
            skArc(sketch, "E3523", {"start": v(-516, -746.68) * mm, "mid": v(-518.65, -747.78) * mm, "end": v(-519.75, -750.43) * mm});
            skArc(sketch, "E3524", {"start": v(-466.24, -750.43) * mm, "mid": v(-465.14, -753.08) * mm, "end": v(-462.5, -754.18) * mm});
            skArc(sketch, "E3525", {"start": v(-462.5, -754.18) * mm, "mid": v(-459.84, -753.08) * mm, "end": v(-458.74, -750.43) * mm});
            skArc(sketch, "E3526", {"start": v(-458.74, -750.43) * mm, "mid": v(-459.84, -747.78) * mm, "end": v(-462.5, -746.68) * mm});
            skArc(sketch, "E3527", {"start": v(-462.5, -746.68) * mm, "mid": v(-465.14, -747.78) * mm, "end": v(-466.24, -750.43) * mm});
            skArc(sketch, "E3528", {"start": v(-519.75, -628.73) * mm, "mid": v(-518.65, -631.38) * mm, "end": v(-516, -632.48) * mm});
            skArc(sketch, "E3529", {"start": v(-516, -632.48) * mm, "mid": v(-513.35, -631.38) * mm, "end": v(-512.25, -628.73) * mm});
            skArc(sketch, "E3530", {"start": v(-512.25, -628.73) * mm, "mid": v(-513.35, -626.08) * mm, "end": v(-516, -624.98) * mm});
            skArc(sketch, "E3531", {"start": v(-516, -624.98) * mm, "mid": v(-518.65, -626.08) * mm, "end": v(-519.75, -628.73) * mm});
            skArc(sketch, "E3532", {"start": v(-466.24, -628.73) * mm, "mid": v(-465.14, -631.38) * mm, "end": v(-462.5, -632.48) * mm});
            skArc(sketch, "E3533", {"start": v(-462.5, -632.48) * mm, "mid": v(-459.84, -631.38) * mm, "end": v(-458.74, -628.73) * mm});
            skArc(sketch, "E3534", {"start": v(-458.74, -628.73) * mm, "mid": v(-459.84, -626.08) * mm, "end": v(-462.5, -624.98) * mm});
            skArc(sketch, "E3535", {"start": v(-462.5, -624.98) * mm, "mid": v(-465.14, -626.08) * mm, "end": v(-466.24, -628.73) * mm});
            skArc(sketch, "E3536", {"start": v(-519.75, -1130.91) * mm, "mid": v(-518.65, -1133.56) * mm, "end": v(-516, -1134.66) * mm});
            skArc(sketch, "E3537", {"start": v(-516, -1134.66) * mm, "mid": v(-513.35, -1133.56) * mm, "end": v(-512.25, -1130.91) * mm});
            skArc(sketch, "E3538", {"start": v(-512.25, -1130.91) * mm, "mid": v(-513.35, -1128.26) * mm, "end": v(-516, -1127.16) * mm});
            skArc(sketch, "E3539", {"start": v(-516, -1127.16) * mm, "mid": v(-518.65, -1128.26) * mm, "end": v(-519.75, -1130.91) * mm});
            skArc(sketch, "E3540", {"start": v(-466.24, -1130.91) * mm, "mid": v(-465.14, -1133.56) * mm, "end": v(-462.5, -1134.66) * mm});
            skArc(sketch, "E3541", {"start": v(-462.5, -1134.66) * mm, "mid": v(-459.84, -1133.56) * mm, "end": v(-458.74, -1130.91) * mm});
            skArc(sketch, "E3542", {"start": v(-458.74, -1130.91) * mm, "mid": v(-459.84, -1128.26) * mm, "end": v(-462.5, -1127.16) * mm});
            skArc(sketch, "E3543", {"start": v(-462.5, -1127.16) * mm, "mid": v(-465.14, -1128.26) * mm, "end": v(-466.24, -1130.91) * mm});
            skArc(sketch, "E3544", {"start": v(569.22, -900.43) * mm, "mid": v(570.32, -903.08) * mm, "end": v(572.97, -904.18) * mm});
            skArc(sketch, "E3545", {"start": v(572.97, -904.18) * mm, "mid": v(575.62, -903.08) * mm, "end": v(576.72, -900.43) * mm});
            skArc(sketch, "E3546", {"start": v(576.72, -900.43) * mm, "mid": v(575.62, -897.78) * mm, "end": v(572.97, -896.68) * mm});
            skArc(sketch, "E3547", {"start": v(572.97, -896.68) * mm, "mid": v(570.32, -897.78) * mm, "end": v(569.22, -900.43) * mm});
            skArc(sketch, "E3548", {"start": v(569.22, -1050.43) * mm, "mid": v(570.32, -1053.08) * mm, "end": v(572.97, -1054.18) * mm});
            skArc(sketch, "E3549", {"start": v(572.97, -1054.18) * mm, "mid": v(575.62, -1053.08) * mm, "end": v(576.72, -1050.43) * mm});
            skArc(sketch, "E3550", {"start": v(576.72, -1050.43) * mm, "mid": v(575.62, -1047.78) * mm, "end": v(572.97, -1046.68) * mm});
            skArc(sketch, "E3551", {"start": v(572.97, -1046.68) * mm, "mid": v(570.32, -1047.78) * mm, "end": v(569.22, -1050.43) * mm});
            skArc(sketch, "E3552", {"start": v(569.22, -750.43) * mm, "mid": v(570.32, -753.08) * mm, "end": v(572.97, -754.18) * mm});
            skArc(sketch, "E3553", {"start": v(572.97, -754.18) * mm, "mid": v(575.62, -753.08) * mm, "end": v(576.72, -750.43) * mm});
            skArc(sketch, "E3554", {"start": v(576.72, -750.43) * mm, "mid": v(575.62, -747.78) * mm, "end": v(572.97, -746.68) * mm});
            skArc(sketch, "E3555", {"start": v(572.97, -746.68) * mm, "mid": v(570.32, -747.78) * mm, "end": v(569.22, -750.43) * mm});
            skArc(sketch, "E3556", {"start": v(569.22, -628.73) * mm, "mid": v(570.32, -631.38) * mm, "end": v(572.97, -632.48) * mm});
            skArc(sketch, "E3557", {"start": v(572.97, -632.48) * mm, "mid": v(575.62, -631.38) * mm, "end": v(576.72, -628.73) * mm});
            skArc(sketch, "E3558", {"start": v(576.72, -628.73) * mm, "mid": v(575.62, -626.08) * mm, "end": v(572.97, -624.98) * mm});
            skArc(sketch, "E3559", {"start": v(572.97, -624.98) * mm, "mid": v(570.32, -626.08) * mm, "end": v(569.22, -628.73) * mm});
            skArc(sketch, "E3560", {"start": v(569.22, -1130.91) * mm, "mid": v(570.32, -1133.56) * mm, "end": v(572.97, -1134.66) * mm});
            skArc(sketch, "E3561", {"start": v(572.97, -1134.66) * mm, "mid": v(575.62, -1133.56) * mm, "end": v(576.72, -1130.91) * mm});
            skArc(sketch, "E3562", {"start": v(576.72, -1130.91) * mm, "mid": v(575.62, -1128.26) * mm, "end": v(572.97, -1127.16) * mm});
            skArc(sketch, "E3563", {"start": v(572.97, -1127.16) * mm, "mid": v(570.32, -1128.26) * mm, "end": v(569.22, -1130.91) * mm});
            skArc(sketch, "E3564", {"start": v(-519.75, -280.92) * mm, "mid": v(-518.65, -278.27) * mm, "end": v(-516, -277.17) * mm});
            skArc(sketch, "E3565", {"start": v(-516, -277.17) * mm, "mid": v(-513.35, -278.27) * mm, "end": v(-512.25, -280.92) * mm});
            skArc(sketch, "E3566", {"start": v(-512.25, -280.92) * mm, "mid": v(-513.35, -283.57) * mm, "end": v(-516, -284.67) * mm});
            skArc(sketch, "E3567", {"start": v(-516, -284.67) * mm, "mid": v(-518.65, -283.57) * mm, "end": v(-519.75, -280.92) * mm});
            skArc(sketch, "E3568", {"start": v(-466.24, -280.92) * mm, "mid": v(-465.14, -278.27) * mm, "end": v(-462.5, -277.17) * mm});
            skArc(sketch, "E3569", {"start": v(-462.5, -277.17) * mm, "mid": v(-459.84, -278.27) * mm, "end": v(-458.74, -280.92) * mm});
            skArc(sketch, "E3570", {"start": v(-458.74, -280.92) * mm, "mid": v(-459.84, -283.57) * mm, "end": v(-462.5, -284.67) * mm});
            skArc(sketch, "E3571", {"start": v(-462.5, -284.67) * mm, "mid": v(-465.14, -283.57) * mm, "end": v(-466.24, -280.92) * mm});
            skArc(sketch, "E3572", {"start": v(-519.75, -130.92) * mm, "mid": v(-518.65, -128.27) * mm, "end": v(-516, -127.17) * mm});
            skArc(sketch, "E3573", {"start": v(-516, -127.17) * mm, "mid": v(-513.35, -128.27) * mm, "end": v(-512.25, -130.92) * mm});
            skArc(sketch, "E3574", {"start": v(-512.25, -130.92) * mm, "mid": v(-513.35, -133.57) * mm, "end": v(-516, -134.67) * mm});
            skArc(sketch, "E3575", {"start": v(-516, -134.67) * mm, "mid": v(-518.65, -133.57) * mm, "end": v(-519.75, -130.92) * mm});
            skArc(sketch, "E3576", {"start": v(-466.24, -130.92) * mm, "mid": v(-465.14, -128.27) * mm, "end": v(-462.5, -127.17) * mm});
            skArc(sketch, "E3577", {"start": v(-462.5, -127.17) * mm, "mid": v(-459.84, -128.27) * mm, "end": v(-458.74, -130.92) * mm});
            skArc(sketch, "E3578", {"start": v(-458.74, -130.92) * mm, "mid": v(-459.84, -133.57) * mm, "end": v(-462.5, -134.67) * mm});
            skArc(sketch, "E3579", {"start": v(-462.5, -134.67) * mm, "mid": v(-465.14, -133.57) * mm, "end": v(-466.24, -130.92) * mm});
            skArc(sketch, "E3580", {"start": v(-519.75, -430.92) * mm, "mid": v(-518.65, -428.27) * mm, "end": v(-516, -427.17) * mm});
            skArc(sketch, "E3581", {"start": v(-516, -427.17) * mm, "mid": v(-513.35, -428.27) * mm, "end": v(-512.25, -430.92) * mm});
            skArc(sketch, "E3582", {"start": v(-512.25, -430.92) * mm, "mid": v(-513.35, -433.57) * mm, "end": v(-516, -434.67) * mm});
            skArc(sketch, "E3583", {"start": v(-516, -434.67) * mm, "mid": v(-518.65, -433.57) * mm, "end": v(-519.75, -430.92) * mm});
            skArc(sketch, "E3584", {"start": v(-466.24, -430.92) * mm, "mid": v(-465.14, -428.27) * mm, "end": v(-462.5, -427.17) * mm});
            skArc(sketch, "E3585", {"start": v(-462.5, -427.17) * mm, "mid": v(-459.84, -428.27) * mm, "end": v(-458.74, -430.92) * mm});
            skArc(sketch, "E3586", {"start": v(-458.74, -430.92) * mm, "mid": v(-459.84, -433.57) * mm, "end": v(-462.5, -434.67) * mm});
            skArc(sketch, "E3587", {"start": v(-462.5, -434.67) * mm, "mid": v(-465.14, -433.57) * mm, "end": v(-466.24, -430.92) * mm});
            skArc(sketch, "E3588", {"start": v(-519.75, -552.62) * mm, "mid": v(-518.65, -549.97) * mm, "end": v(-516, -548.87) * mm});
            skArc(sketch, "E3589", {"start": v(-516, -548.87) * mm, "mid": v(-513.35, -549.97) * mm, "end": v(-512.25, -552.62) * mm});
            skArc(sketch, "E3590", {"start": v(-512.25, -552.62) * mm, "mid": v(-513.35, -555.27) * mm, "end": v(-516, -556.37) * mm});
            skArc(sketch, "E3591", {"start": v(-516, -556.37) * mm, "mid": v(-518.65, -555.27) * mm, "end": v(-519.75, -552.62) * mm});
            skArc(sketch, "E3592", {"start": v(-466.24, -552.62) * mm, "mid": v(-465.14, -549.97) * mm, "end": v(-462.5, -548.87) * mm});
            skArc(sketch, "E3593", {"start": v(-462.5, -548.87) * mm, "mid": v(-459.84, -549.97) * mm, "end": v(-458.74, -552.62) * mm});
            skArc(sketch, "E3594", {"start": v(-458.74, -552.62) * mm, "mid": v(-459.84, -555.27) * mm, "end": v(-462.5, -556.37) * mm});
            skArc(sketch, "E3595", {"start": v(-462.5, -556.37) * mm, "mid": v(-465.14, -555.27) * mm, "end": v(-466.24, -552.62) * mm});
            skArc(sketch, "E3596", {"start": v(-519.75, -50.43) * mm, "mid": v(-518.65, -47.78) * mm, "end": v(-516, -46.68) * mm});
            skArc(sketch, "E3597", {"start": v(-516, -46.68) * mm, "mid": v(-513.35, -47.78) * mm, "end": v(-512.25, -50.43) * mm});
            skArc(sketch, "E3598", {"start": v(-512.25, -50.43) * mm, "mid": v(-513.35, -53.09) * mm, "end": v(-516, -54.18) * mm});
            skArc(sketch, "E3599", {"start": v(-516, -54.18) * mm, "mid": v(-518.65, -53.09) * mm, "end": v(-519.75, -50.43) * mm});
            skArc(sketch, "E3600", {"start": v(-466.24, -50.43) * mm, "mid": v(-465.14, -47.78) * mm, "end": v(-462.5, -46.68) * mm});
            skArc(sketch, "E3601", {"start": v(-462.5, -46.68) * mm, "mid": v(-459.84, -47.78) * mm, "end": v(-458.74, -50.43) * mm});
            skArc(sketch, "E3602", {"start": v(-458.74, -50.43) * mm, "mid": v(-459.84, -53.09) * mm, "end": v(-462.5, -54.18) * mm});
            skArc(sketch, "E3603", {"start": v(-462.5, -54.18) * mm, "mid": v(-465.14, -53.09) * mm, "end": v(-466.24, -50.43) * mm});
            skArc(sketch, "E3604", {"start": v(569.22, -280.92) * mm, "mid": v(570.32, -278.27) * mm, "end": v(572.97, -277.17) * mm});
            skArc(sketch, "E3605", {"start": v(572.97, -277.17) * mm, "mid": v(575.62, -278.27) * mm, "end": v(576.72, -280.92) * mm});
            skArc(sketch, "E3606", {"start": v(576.72, -280.92) * mm, "mid": v(575.62, -283.57) * mm, "end": v(572.97, -284.67) * mm});
            skArc(sketch, "E3607", {"start": v(572.97, -284.67) * mm, "mid": v(570.32, -283.57) * mm, "end": v(569.22, -280.92) * mm});
            skArc(sketch, "E3608", {"start": v(569.22, -130.92) * mm, "mid": v(570.32, -128.27) * mm, "end": v(572.97, -127.17) * mm});
            skArc(sketch, "E3609", {"start": v(572.97, -127.17) * mm, "mid": v(575.62, -128.27) * mm, "end": v(576.72, -130.92) * mm});
            skArc(sketch, "E3610", {"start": v(576.72, -130.92) * mm, "mid": v(575.62, -133.57) * mm, "end": v(572.97, -134.67) * mm});
            skArc(sketch, "E3611", {"start": v(572.97, -134.67) * mm, "mid": v(570.32, -133.57) * mm, "end": v(569.22, -130.92) * mm});
            skArc(sketch, "E3612", {"start": v(569.22, -430.92) * mm, "mid": v(570.32, -428.27) * mm, "end": v(572.97, -427.17) * mm});
            skArc(sketch, "E3613", {"start": v(572.97, -427.17) * mm, "mid": v(575.62, -428.27) * mm, "end": v(576.72, -430.92) * mm});
            skArc(sketch, "E3614", {"start": v(576.72, -430.92) * mm, "mid": v(575.62, -433.57) * mm, "end": v(572.97, -434.67) * mm});
            skArc(sketch, "E3615", {"start": v(572.97, -434.67) * mm, "mid": v(570.32, -433.57) * mm, "end": v(569.22, -430.92) * mm});
            skArc(sketch, "E3616", {"start": v(569.22, -552.62) * mm, "mid": v(570.32, -549.97) * mm, "end": v(572.97, -548.87) * mm});
            skArc(sketch, "E3617", {"start": v(572.97, -548.87) * mm, "mid": v(575.62, -549.97) * mm, "end": v(576.72, -552.62) * mm});
            skArc(sketch, "E3618", {"start": v(576.72, -552.62) * mm, "mid": v(575.62, -555.27) * mm, "end": v(572.97, -556.37) * mm});
            skArc(sketch, "E3619", {"start": v(572.97, -556.37) * mm, "mid": v(570.32, -555.27) * mm, "end": v(569.22, -552.62) * mm});
            skArc(sketch, "E3620", {"start": v(569.22, -50.43) * mm, "mid": v(570.32, -47.78) * mm, "end": v(572.97, -46.68) * mm});
            skArc(sketch, "E3621", {"start": v(572.97, -46.68) * mm, "mid": v(575.62, -47.78) * mm, "end": v(576.72, -50.43) * mm});
            skArc(sketch, "E3622", {"start": v(576.72, -50.43) * mm, "mid": v(575.62, -53.09) * mm, "end": v(572.97, -54.18) * mm});
            skArc(sketch, "E3623", {"start": v(572.97, -54.18) * mm, "mid": v(570.32, -53.09) * mm, "end": v(569.22, -50.43) * mm});
            skArc(sketch, "E3624", {"start": v(575.72, 908.18) * mm, "mid": v(574.62, 910.83) * mm, "end": v(571.97, 911.93) * mm});
            skArc(sketch, "E3625", {"start": v(571.97, 911.93) * mm, "mid": v(569.31, 910.83) * mm, "end": v(568.22, 908.18) * mm});
            skArc(sketch, "E3626", {"start": v(568.22, 908.18) * mm, "mid": v(569.31, 905.53) * mm, "end": v(571.97, 904.43) * mm});
            skArc(sketch, "E3627", {"start": v(571.97, 904.43) * mm, "mid": v(574.62, 905.53) * mm, "end": v(575.72, 908.18) * mm});
            skArc(sketch, "E3628", {"start": v(575.72, 1058.18) * mm, "mid": v(574.62, 1060.83) * mm, "end": v(571.97, 1061.93) * mm});
            skArc(sketch, "E3629", {"start": v(571.97, 1061.93) * mm, "mid": v(569.31, 1060.83) * mm, "end": v(568.22, 1058.18) * mm});
            skArc(sketch, "E3630", {"start": v(568.22, 1058.18) * mm, "mid": v(569.31, 1055.53) * mm, "end": v(571.97, 1054.43) * mm});
            skArc(sketch, "E3631", {"start": v(571.97, 1054.43) * mm, "mid": v(574.62, 1055.53) * mm, "end": v(575.72, 1058.18) * mm});
            skArc(sketch, "E3632", {"start": v(575.72, 758.18) * mm, "mid": v(574.62, 760.83) * mm, "end": v(571.97, 761.93) * mm});
            skArc(sketch, "E3633", {"start": v(571.97, 761.93) * mm, "mid": v(569.31, 760.83) * mm, "end": v(568.22, 758.18) * mm});
            skArc(sketch, "E3634", {"start": v(568.22, 758.18) * mm, "mid": v(569.31, 755.53) * mm, "end": v(571.97, 754.43) * mm});
            skArc(sketch, "E3635", {"start": v(571.97, 754.43) * mm, "mid": v(574.62, 755.53) * mm, "end": v(575.72, 758.18) * mm});
            skArc(sketch, "E3636", {"start": v(575.72, 636.48) * mm, "mid": v(574.62, 639.13) * mm, "end": v(571.97, 640.23) * mm});
            skArc(sketch, "E3637", {"start": v(571.97, 640.23) * mm, "mid": v(569.31, 639.13) * mm, "end": v(568.22, 636.48) * mm});
            skArc(sketch, "E3638", {"start": v(568.22, 636.48) * mm, "mid": v(569.31, 633.83) * mm, "end": v(571.97, 632.73) * mm});
            skArc(sketch, "E3639", {"start": v(571.97, 632.73) * mm, "mid": v(574.62, 633.83) * mm, "end": v(575.72, 636.48) * mm});
            skArc(sketch, "E3640", {"start": v(575.72, 1138.66) * mm, "mid": v(574.62, 1141.32) * mm, "end": v(571.97, 1142.41) * mm});
            skArc(sketch, "E3641", {"start": v(571.97, 1142.41) * mm, "mid": v(569.31, 1141.32) * mm, "end": v(568.22, 1138.66) * mm});
            skArc(sketch, "E3642", {"start": v(568.22, 1138.66) * mm, "mid": v(569.31, 1136.01) * mm, "end": v(571.97, 1134.91) * mm});
            skArc(sketch, "E3643", {"start": v(571.97, 1134.91) * mm, "mid": v(574.62, 1136.01) * mm, "end": v(575.72, 1138.66) * mm});
            skArc(sketch, "E3644", {"start": v(-569.1, 908.18) * mm, "mid": v(-570.19, 910.83) * mm, "end": v(-572.84, 911.93) * mm});
            skArc(sketch, "E3645", {"start": v(-572.84, 911.93) * mm, "mid": v(-575.5, 910.83) * mm, "end": v(-576.6, 908.18) * mm});
            skArc(sketch, "E3646", {"start": v(-576.6, 908.18) * mm, "mid": v(-575.5, 905.53) * mm, "end": v(-572.84, 904.43) * mm});
            skArc(sketch, "E3647", {"start": v(-572.84, 904.43) * mm, "mid": v(-570.19, 905.53) * mm, "end": v(-569.1, 908.18) * mm});
            skArc(sketch, "E3648", {"start": v(-569.1, 1058.18) * mm, "mid": v(-570.19, 1060.83) * mm, "end": v(-572.84, 1061.93) * mm});
            skArc(sketch, "E3649", {"start": v(-572.84, 1061.93) * mm, "mid": v(-575.5, 1060.83) * mm, "end": v(-576.6, 1058.18) * mm});
            skArc(sketch, "E3650", {"start": v(-576.6, 1058.18) * mm, "mid": v(-575.5, 1055.53) * mm, "end": v(-572.84, 1054.43) * mm});
            skArc(sketch, "E3651", {"start": v(-572.84, 1054.43) * mm, "mid": v(-570.19, 1055.53) * mm, "end": v(-569.1, 1058.18) * mm});
            skArc(sketch, "E3652", {"start": v(-569.1, 758.18) * mm, "mid": v(-570.19, 760.83) * mm, "end": v(-572.84, 761.93) * mm});
            skArc(sketch, "E3653", {"start": v(-572.84, 761.93) * mm, "mid": v(-575.5, 760.83) * mm, "end": v(-576.6, 758.18) * mm});
            skArc(sketch, "E3654", {"start": v(-576.6, 758.18) * mm, "mid": v(-575.5, 755.53) * mm, "end": v(-572.84, 754.43) * mm});
            skArc(sketch, "E3655", {"start": v(-572.84, 754.43) * mm, "mid": v(-570.19, 755.53) * mm, "end": v(-569.1, 758.18) * mm});
            skArc(sketch, "E3656", {"start": v(-569.1, 636.48) * mm, "mid": v(-570.19, 639.13) * mm, "end": v(-572.84, 640.23) * mm});
            skArc(sketch, "E3657", {"start": v(-572.84, 640.23) * mm, "mid": v(-575.5, 639.13) * mm, "end": v(-576.6, 636.48) * mm});
            skArc(sketch, "E3658", {"start": v(-576.6, 636.48) * mm, "mid": v(-575.5, 633.83) * mm, "end": v(-572.84, 632.73) * mm});
            skArc(sketch, "E3659", {"start": v(-572.84, 632.73) * mm, "mid": v(-570.19, 633.83) * mm, "end": v(-569.1, 636.48) * mm});
            skArc(sketch, "E3660", {"start": v(-569.1, 1138.66) * mm, "mid": v(-570.19, 1141.32) * mm, "end": v(-572.84, 1142.41) * mm});
            skArc(sketch, "E3661", {"start": v(-572.84, 1142.41) * mm, "mid": v(-575.5, 1141.32) * mm, "end": v(-576.6, 1138.66) * mm});
            skArc(sketch, "E3662", {"start": v(-576.6, 1138.66) * mm, "mid": v(-575.5, 1136.01) * mm, "end": v(-572.84, 1134.91) * mm});
            skArc(sketch, "E3663", {"start": v(-572.84, 1134.91) * mm, "mid": v(-570.19, 1136.01) * mm, "end": v(-569.1, 1138.66) * mm});
            skArc(sketch, "E3664", {"start": v(575.72, 315.9) * mm, "mid": v(574.62, 318.55) * mm, "end": v(571.97, 319.65) * mm});
            skArc(sketch, "E3665", {"start": v(571.97, 319.65) * mm, "mid": v(569.31, 318.55) * mm, "end": v(568.22, 315.9) * mm});
            skArc(sketch, "E3666", {"start": v(568.22, 315.9) * mm, "mid": v(569.31, 313.25) * mm, "end": v(571.97, 312.15) * mm});
            skArc(sketch, "E3667", {"start": v(571.97, 312.15) * mm, "mid": v(574.62, 313.25) * mm, "end": v(575.72, 315.9) * mm});
            skArc(sketch, "E3668", {"start": v(575.72, 465.9) * mm, "mid": v(574.62, 468.55) * mm, "end": v(571.97, 469.65) * mm});
            skArc(sketch, "E3669", {"start": v(571.97, 469.65) * mm, "mid": v(569.31, 468.55) * mm, "end": v(568.22, 465.9) * mm});
            skArc(sketch, "E3670", {"start": v(568.22, 465.9) * mm, "mid": v(569.31, 463.25) * mm, "end": v(571.97, 462.15) * mm});
            skArc(sketch, "E3671", {"start": v(571.97, 462.15) * mm, "mid": v(574.62, 463.25) * mm, "end": v(575.72, 465.9) * mm});
            skArc(sketch, "E3672", {"start": v(575.72, 165.9) * mm, "mid": v(574.62, 168.55) * mm, "end": v(571.97, 169.65) * mm});
            skArc(sketch, "E3673", {"start": v(571.97, 169.65) * mm, "mid": v(569.31, 168.55) * mm, "end": v(568.22, 165.9) * mm});
            skArc(sketch, "E3674", {"start": v(568.22, 165.9) * mm, "mid": v(569.31, 163.25) * mm, "end": v(571.97, 162.15) * mm});
            skArc(sketch, "E3675", {"start": v(571.97, 162.15) * mm, "mid": v(574.62, 163.25) * mm, "end": v(575.72, 165.9) * mm});
            skArc(sketch, "E3676", {"start": v(575.72, 44.2) * mm, "mid": v(574.62, 46.85) * mm, "end": v(571.97, 47.95) * mm});
            skArc(sketch, "E3677", {"start": v(571.97, 47.95) * mm, "mid": v(569.31, 46.85) * mm, "end": v(568.22, 44.2) * mm});
            skArc(sketch, "E3678", {"start": v(568.22, 44.2) * mm, "mid": v(569.31, 41.55) * mm, "end": v(571.97, 40.45) * mm});
            skArc(sketch, "E3679", {"start": v(571.97, 40.45) * mm, "mid": v(574.62, 41.55) * mm, "end": v(575.72, 44.2) * mm});
            skArc(sketch, "E3680", {"start": v(575.72, 546.38) * mm, "mid": v(574.62, 549.04) * mm, "end": v(571.97, 550.13) * mm});
            skArc(sketch, "E3681", {"start": v(571.97, 550.13) * mm, "mid": v(569.31, 549.04) * mm, "end": v(568.22, 546.38) * mm});
            skArc(sketch, "E3682", {"start": v(568.22, 546.38) * mm, "mid": v(569.31, 543.73) * mm, "end": v(571.97, 542.63) * mm});
            skArc(sketch, "E3683", {"start": v(571.97, 542.63) * mm, "mid": v(574.62, 543.73) * mm, "end": v(575.72, 546.38) * mm});
            skArc(sketch, "E3684", {"start": v(-569.1, 315.9) * mm, "mid": v(-570.19, 318.55) * mm, "end": v(-572.84, 319.65) * mm});
            skArc(sketch, "E3685", {"start": v(-572.84, 319.65) * mm, "mid": v(-575.5, 318.55) * mm, "end": v(-576.6, 315.9) * mm});
            skArc(sketch, "E3686", {"start": v(-576.6, 315.9) * mm, "mid": v(-575.5, 313.25) * mm, "end": v(-572.84, 312.15) * mm});
            skArc(sketch, "E3687", {"start": v(-572.84, 312.15) * mm, "mid": v(-570.19, 313.25) * mm, "end": v(-569.1, 315.9) * mm});
            skArc(sketch, "E3688", {"start": v(-569.1, 465.9) * mm, "mid": v(-570.19, 468.55) * mm, "end": v(-572.84, 469.65) * mm});
            skArc(sketch, "E3689", {"start": v(-572.84, 469.65) * mm, "mid": v(-575.5, 468.55) * mm, "end": v(-576.6, 465.9) * mm});
            skArc(sketch, "E3690", {"start": v(-576.6, 465.9) * mm, "mid": v(-575.5, 463.25) * mm, "end": v(-572.84, 462.15) * mm});
            skArc(sketch, "E3691", {"start": v(-572.84, 462.15) * mm, "mid": v(-570.19, 463.25) * mm, "end": v(-569.1, 465.9) * mm});
            skArc(sketch, "E3692", {"start": v(-569.1, 165.9) * mm, "mid": v(-570.19, 168.55) * mm, "end": v(-572.84, 169.65) * mm});
            skArc(sketch, "E3693", {"start": v(-572.84, 169.65) * mm, "mid": v(-575.5, 168.55) * mm, "end": v(-576.6, 165.9) * mm});
            skArc(sketch, "E3694", {"start": v(-576.6, 165.9) * mm, "mid": v(-575.5, 163.25) * mm, "end": v(-572.84, 162.15) * mm});
            skArc(sketch, "E3695", {"start": v(-572.84, 162.15) * mm, "mid": v(-570.19, 163.25) * mm, "end": v(-569.1, 165.9) * mm});
            skArc(sketch, "E3696", {"start": v(-569.1, 44.2) * mm, "mid": v(-570.19, 46.85) * mm, "end": v(-572.84, 47.95) * mm});
            skArc(sketch, "E3697", {"start": v(-572.84, 47.95) * mm, "mid": v(-575.5, 46.85) * mm, "end": v(-576.6, 44.2) * mm});
            skArc(sketch, "E3698", {"start": v(-576.6, 44.2) * mm, "mid": v(-575.5, 41.55) * mm, "end": v(-572.84, 40.45) * mm});
            skArc(sketch, "E3699", {"start": v(-572.84, 40.45) * mm, "mid": v(-570.19, 41.55) * mm, "end": v(-569.1, 44.2) * mm});
            skArc(sketch, "E3700", {"start": v(-569.1, 546.38) * mm, "mid": v(-570.19, 549.04) * mm, "end": v(-572.84, 550.13) * mm});
            skArc(sketch, "E3701", {"start": v(-572.84, 550.13) * mm, "mid": v(-575.5, 549.04) * mm, "end": v(-576.6, 546.38) * mm});
            skArc(sketch, "E3702", {"start": v(-576.6, 546.38) * mm, "mid": v(-575.5, 543.73) * mm, "end": v(-572.84, 542.63) * mm});
            skArc(sketch, "E3703", {"start": v(-572.84, 542.63) * mm, "mid": v(-570.19, 543.73) * mm, "end": v(-569.1, 546.38) * mm});
            skArc(sketch, "E3704", {"start": v(45.49, -686.19) * mm, "mid": v(42.84, -687.29) * mm, "end": v(41.74, -689.94) * mm});
            skArc(sketch, "E3705", {"start": v(41.74, -689.94) * mm, "mid": v(42.84, -692.6) * mm, "end": v(45.49, -693.69) * mm});
            skArc(sketch, "E3706", {"start": v(45.49, -693.69) * mm, "mid": v(48.14, -692.6) * mm, "end": v(49.24, -689.94) * mm});
            skArc(sketch, "E3707", {"start": v(49.24, -689.94) * mm, "mid": v(48.14, -687.29) * mm, "end": v(45.49, -686.19) * mm});
            skArc(sketch, "E3708", {"start": v(47.9, -1013.07) * mm, "mid": v(45.24, -1014.17) * mm, "end": v(44.14, -1016.82) * mm});
            skArc(sketch, "E3709", {"start": v(44.14, -1016.82) * mm, "mid": v(45.24, -1019.47) * mm, "end": v(47.9, -1020.57) * mm});
            skArc(sketch, "E3710", {"start": v(47.9, -1020.57) * mm, "mid": v(50.54, -1019.47) * mm, "end": v(51.64, -1016.82) * mm});
            skArc(sketch, "E3711", {"start": v(51.64, -1016.82) * mm, "mid": v(50.54, -1014.17) * mm, "end": v(47.9, -1013.07) * mm});
            skArc(sketch, "E3712", {"start": v(-408.45, -584.9) * mm, "mid": v(-411.1, -586) * mm, "end": v(-412.2, -588.66) * mm});
            skArc(sketch, "E3713", {"start": v(-412.2, -588.66) * mm, "mid": v(-411.1, -591.31) * mm, "end": v(-408.45, -592.4) * mm});
            skArc(sketch, "E3714", {"start": v(-408.45, -592.4) * mm, "mid": v(-405.8, -591.31) * mm, "end": v(-404.7, -588.66) * mm});
            skArc(sketch, "E3715", {"start": v(-404.7, -588.66) * mm, "mid": v(-405.8, -586) * mm, "end": v(-408.45, -584.9) * mm});
            skArc(sketch, "E3716", {"start": v(59.1, -586.04) * mm, "mid": v(56.44, -587.14) * mm, "end": v(55.34, -589.8) * mm});
            skArc(sketch, "E3717", {"start": v(55.34, -589.8) * mm, "mid": v(56.44, -592.44) * mm, "end": v(59.1, -593.54) * mm});
            skArc(sketch, "E3718", {"start": v(59.1, -593.54) * mm, "mid": v(61.74, -592.44) * mm, "end": v(62.84, -589.8) * mm});
            skArc(sketch, "E3719", {"start": v(62.84, -589.8) * mm, "mid": v(61.74, -587.14) * mm, "end": v(59.1, -586.04) * mm});
            skArc(sketch, "E3720", {"start": v(511.95, -587.62) * mm, "mid": v(509.3, -588.72) * mm, "end": v(508.2, -591.37) * mm});
            skArc(sketch, "E3721", {"start": v(508.2, -591.37) * mm, "mid": v(509.3, -594.02) * mm, "end": v(511.95, -595.12) * mm});
            skArc(sketch, "E3722", {"start": v(511.95, -595.12) * mm, "mid": v(514.6, -594.02) * mm, "end": v(515.7, -591.37) * mm});
            skArc(sketch, "E3723", {"start": v(515.7, -591.37) * mm, "mid": v(514.6, -588.72) * mm, "end": v(511.95, -587.62) * mm});
            skArc(sketch, "E3724", {"start": v(515.18, -1168.32) * mm, "mid": v(512.53, -1169.42) * mm, "end": v(511.43, -1172.07) * mm});
            skArc(sketch, "E3725", {"start": v(511.43, -1172.07) * mm, "mid": v(512.53, -1174.72) * mm, "end": v(515.18, -1175.82) * mm});
            skArc(sketch, "E3726", {"start": v(515.18, -1175.82) * mm, "mid": v(517.83, -1174.72) * mm, "end": v(518.93, -1172.07) * mm});
            skArc(sketch, "E3727", {"start": v(518.93, -1172.07) * mm, "mid": v(517.83, -1169.42) * mm, "end": v(515.18, -1168.32) * mm});
            skArc(sketch, "E3728", {"start": v(-487.7, -1169.9) * mm, "mid": v(-490.35, -1171) * mm, "end": v(-491.45, -1173.65) * mm});
            skArc(sketch, "E3729", {"start": v(-491.45, -1173.65) * mm, "mid": v(-490.35, -1176.3) * mm, "end": v(-487.7, -1177.4) * mm});
            skArc(sketch, "E3730", {"start": v(-487.7, -1177.4) * mm, "mid": v(-485.05, -1176.3) * mm, "end": v(-483.95, -1173.65) * mm});
            skArc(sketch, "E3731", {"start": v(-483.95, -1173.65) * mm, "mid": v(-485.05, -1171) * mm, "end": v(-487.7, -1169.9) * mm});
            skArc(sketch, "E3732", {"start": v(-123.55, -1181.71) * mm, "mid": v(-126.2, -1182.81) * mm, "end": v(-127.3, -1185.46) * mm});
            skArc(sketch, "E3733", {"start": v(-127.3, -1185.46) * mm, "mid": v(-126.2, -1188.11) * mm, "end": v(-123.55, -1189.21) * mm});
            skArc(sketch, "E3734", {"start": v(-123.55, -1189.21) * mm, "mid": v(-120.9, -1188.11) * mm, "end": v(-119.8, -1185.46) * mm});
            skArc(sketch, "E3735", {"start": v(-119.8, -1185.46) * mm, "mid": v(-120.9, -1182.81) * mm, "end": v(-123.55, -1181.71) * mm});
            skArc(sketch, "E3736", {"start": v(268.66, -1182.5) * mm, "mid": v(266.01, -1183.6) * mm, "end": v(264.91, -1186.25) * mm});
            skArc(sketch, "E3737", {"start": v(264.91, -1186.25) * mm, "mid": v(266.01, -1188.9) * mm, "end": v(268.66, -1190) * mm});
            skArc(sketch, "E3738", {"start": v(268.66, -1190) * mm, "mid": v(271.32, -1188.9) * mm, "end": v(272.41, -1186.25) * mm});
            skArc(sketch, "E3739", {"start": v(272.41, -1186.25) * mm, "mid": v(271.32, -1183.6) * mm, "end": v(268.66, -1182.5) * mm});
            skArc(sketch, "E3740", {"start": v(-546.9, 1183.79) * mm, "mid": v(-549.01, 1182.9) * mm, "end": v(-549.9, 1180.79) * mm});
            skArc(sketch, "E3741", {"start": v(-549.9, 1180.79) * mm, "mid": v(-549.01, 1178.67) * mm, "end": v(-546.9, 1177.79) * mm});
            skArc(sketch, "E3742", {"start": v(-546.9, 1177.79) * mm, "mid": v(-544.77, 1178.67) * mm, "end": v(-543.9, 1180.79) * mm});
            skArc(sketch, "E3743", {"start": v(-543.9, 1180.79) * mm, "mid": v(-544.77, 1182.9) * mm, "end": v(-546.9, 1183.79) * mm});
            skArc(sketch, "E3744", {"start": v(-230.11, 1192.88) * mm, "mid": v(-232.23, 1192) * mm, "end": v(-233.11, 1189.88) * mm});
            skArc(sketch, "E3745", {"start": v(-233.11, 1189.88) * mm, "mid": v(-232.23, 1187.76) * mm, "end": v(-230.11, 1186.88) * mm});
            skArc(sketch, "E3746", {"start": v(-230.11, 1186.88) * mm, "mid": v(-228, 1187.76) * mm, "end": v(-227.11, 1189.88) * mm});
            skArc(sketch, "E3747", {"start": v(-227.11, 1189.88) * mm, "mid": v(-228, 1192) * mm, "end": v(-230.11, 1192.88) * mm});
            skArc(sketch, "E3748", {"start": v(157.53, 1191.34) * mm, "mid": v(155.4, 1190.46) * mm, "end": v(154.53, 1188.34) * mm});
            skArc(sketch, "E3749", {"start": v(154.53, 1188.34) * mm, "mid": v(155.4, 1186.22) * mm, "end": v(157.53, 1185.34) * mm});
            skArc(sketch, "E3750", {"start": v(157.53, 1185.34) * mm, "mid": v(159.65, 1186.22) * mm, "end": v(160.53, 1188.34) * mm});
            skArc(sketch, "E3751", {"start": v(160.53, 1188.34) * mm, "mid": v(159.65, 1190.46) * mm, "end": v(157.53, 1191.34) * mm});
            skArc(sketch, "E3752", {"start": v(535.26, 1184.14) * mm, "mid": v(533.14, 1183.27) * mm, "end": v(532.26, 1181.14) * mm});
            skArc(sketch, "E3753", {"start": v(532.26, 1181.14) * mm, "mid": v(533.14, 1179.02) * mm, "end": v(535.26, 1178.14) * mm});
            skArc(sketch, "E3754", {"start": v(535.26, 1178.14) * mm, "mid": v(537.38, 1179.02) * mm, "end": v(538.26, 1181.14) * mm});
            skArc(sketch, "E3755", {"start": v(538.26, 1181.14) * mm, "mid": v(537.38, 1183.27) * mm, "end": v(535.26, 1184.14) * mm});
            skArc(sketch, "E3756", {"start": v(-522.42, 596.03) * mm, "mid": v(-524.54, 595.15) * mm, "end": v(-525.42, 593.03) * mm});
            skArc(sketch, "E3757", {"start": v(-525.42, 593.03) * mm, "mid": v(-524.54, 590.91) * mm, "end": v(-522.42, 590.03) * mm});
            skArc(sketch, "E3758", {"start": v(-522.42, 590.03) * mm, "mid": v(-520.3, 590.91) * mm, "end": v(-519.42, 593.03) * mm});
            skArc(sketch, "E3759", {"start": v(-519.42, 593.03) * mm, "mid": v(-520.3, 595.15) * mm, "end": v(-522.42, 596.03) * mm});
            skArc(sketch, "E3760", {"start": v(-0.73, 604.06) * mm, "mid": v(-2.85, 603.18) * mm, "end": v(-3.73, 601.06) * mm});
            skArc(sketch, "E3761", {"start": v(-3.73, 601.06) * mm, "mid": v(-2.85, 598.93) * mm, "end": v(-0.73, 598.06) * mm});
            skArc(sketch, "E3762", {"start": v(-0.73, 598.06) * mm, "mid": v(1.39, 598.93) * mm, "end": v(2.27, 601.06) * mm});
            skArc(sketch, "E3763", {"start": v(2.27, 601.06) * mm, "mid": v(1.39, 603.18) * mm, "end": v(-0.73, 604.06) * mm});
            skArc(sketch, "E3764", {"start": v(519.55, 594.46) * mm, "mid": v(517.43, 593.58) * mm, "end": v(516.55, 591.46) * mm});
            skArc(sketch, "E3765", {"start": v(516.55, 591.46) * mm, "mid": v(517.43, 589.34) * mm, "end": v(519.55, 588.46) * mm});
            skArc(sketch, "E3766", {"start": v(519.55, 588.46) * mm, "mid": v(521.67, 589.34) * mm, "end": v(522.55, 591.46) * mm});
            skArc(sketch, "E3767", {"start": v(522.55, 591.46) * mm, "mid": v(521.67, 593.58) * mm, "end": v(519.55, 594.46) * mm});
            skArc(sketch, "E3768", {"start": v(511.23, -5.01) * mm, "mid": v(509.11, -5.9) * mm, "end": v(508.23, -8.01) * mm});
            skArc(sketch, "E3769", {"start": v(508.23, -8.01) * mm, "mid": v(509.11, -10.14) * mm, "end": v(511.23, -11.01) * mm});
            skArc(sketch, "E3770", {"start": v(511.23, -11.01) * mm, "mid": v(513.35, -10.14) * mm, "end": v(514.23, -8.01) * mm});
            skArc(sketch, "E3771", {"start": v(514.23, -8.01) * mm, "mid": v(513.35, -5.9) * mm, "end": v(511.23, -5.01) * mm});
            skArc(sketch, "E3772", {"start": v(-0.07, 9.32) * mm, "mid": v(-2.2, 8.45) * mm, "end": v(-3.07, 6.32) * mm});
            skArc(sketch, "E3773", {"start": v(-3.07, 6.32) * mm, "mid": v(-2.2, 4.2) * mm, "end": v(-0.07, 3.32) * mm});
            skArc(sketch, "E3774", {"start": v(-0.07, 3.32) * mm, "mid": v(2.05, 4.2) * mm, "end": v(2.93, 6.32) * mm});
            skArc(sketch, "E3775", {"start": v(2.93, 6.32) * mm, "mid": v(2.05, 8.45) * mm, "end": v(-0.07, 9.32) * mm});
            skArc(sketch, "E3776", {"start": v(-510.03, -3.47) * mm, "mid": v(-512.16, -4.35) * mm, "end": v(-513.03, -6.47) * mm});
            skArc(sketch, "E3777", {"start": v(-513.03, -6.47) * mm, "mid": v(-512.16, -8.6) * mm, "end": v(-510.03, -9.47) * mm});
            skArc(sketch, "E3778", {"start": v(-510.03, -9.47) * mm, "mid": v(-507.91, -8.6) * mm, "end": v(-507.03, -6.47) * mm});
            skArc(sketch, "E3779", {"start": v(-507.03, -6.47) * mm, "mid": v(-507.91, -4.35) * mm, "end": v(-510.03, -3.47) * mm});
            skArc(sketch, "E3780", {"start": v(2.46, 124.15) * mm, "mid": v(0.34, 123.27) * mm, "end": v(-0.54, 121.15) * mm});
            skArc(sketch, "E3781", {"start": v(-0.54, 121.15) * mm, "mid": v(0.34, 119.02) * mm, "end": v(2.46, 118.15) * mm});
            skArc(sketch, "E3782", {"start": v(2.46, 118.15) * mm, "mid": v(4.59, 119.02) * mm, "end": v(5.46, 121.15) * mm});
            skArc(sketch, "E3783", {"start": v(5.46, 121.15) * mm, "mid": v(4.59, 123.27) * mm, "end": v(2.46, 124.15) * mm});
            skArc(sketch, "E3784", {"start": v(-1.38, 435.64) * mm, "mid": v(-3.5, 434.76) * mm, "end": v(-4.38, 432.64) * mm});
            skArc(sketch, "E3785", {"start": v(-4.38, 432.64) * mm, "mid": v(-3.5, 430.52) * mm, "end": v(-1.38, 429.64) * mm});
            skArc(sketch, "E3786", {"start": v(-1.38, 429.64) * mm, "mid": v(0.74, 430.52) * mm, "end": v(1.62, 432.64) * mm});
            skArc(sketch, "E3787", {"start": v(1.62, 432.64) * mm, "mid": v(0.74, 434.76) * mm, "end": v(-1.38, 435.64) * mm});
            skArc(sketch, "E3788", {"start": v(-3.3, 725.98) * mm, "mid": v(-5.43, 725.1) * mm, "end": v(-6.3, 722.98) * mm});
            skArc(sketch, "E3789", {"start": v(-6.3, 722.98) * mm, "mid": v(-5.43, 720.86) * mm, "end": v(-3.3, 719.98) * mm});
            skArc(sketch, "E3790", {"start": v(-3.3, 719.98) * mm, "mid": v(-1.18, 720.86) * mm, "end": v(-0.3, 722.98) * mm});
            skArc(sketch, "E3791", {"start": v(-0.3, 722.98) * mm, "mid": v(-1.18, 725.1) * mm, "end": v(-3.3, 725.98) * mm});
            skArc(sketch, "E3792", {"start": v(-11, 1031.71) * mm, "mid": v(-13.12, 1030.83) * mm, "end": v(-14, 1028.71) * mm});
            skArc(sketch, "E3793", {"start": v(-14, 1028.71) * mm, "mid": v(-13.12, 1026.59) * mm, "end": v(-11, 1025.71) * mm});
            skArc(sketch, "E3794", {"start": v(-11, 1025.71) * mm, "mid": v(-8.87, 1026.59) * mm, "end": v(-8, 1028.71) * mm});
            skArc(sketch, "E3795", {"start": v(-8, 1028.71) * mm, "mid": v(-8.87, 1030.83) * mm, "end": v(-11, 1031.71) * mm});
            skArc(sketch, "E3796", {"start": v(55.67, -442.1) * mm, "mid": v(53.55, -442.97) * mm, "end": v(52.67, -445.1) * mm});
            skArc(sketch, "E3797", {"start": v(52.67, -445.1) * mm, "mid": v(53.55, -447.22) * mm, "end": v(55.67, -448.1) * mm});
            skArc(sketch, "E3798", {"start": v(55.67, -448.1) * mm, "mid": v(57.8, -447.22) * mm, "end": v(58.67, -445.1) * mm});
            skArc(sketch, "E3799", {"start": v(58.67, -445.1) * mm, "mid": v(57.8, -442.97) * mm, "end": v(55.67, -442.1) * mm});
            skArc(sketch, "E3800", {"start": v(53.27, -165.69) * mm, "mid": v(51.14, -166.57) * mm, "end": v(50.27, -168.69) * mm});
            skArc(sketch, "E3801", {"start": v(50.27, -168.69) * mm, "mid": v(51.14, -170.81) * mm, "end": v(53.27, -171.69) * mm});
            skArc(sketch, "E3802", {"start": v(53.27, -171.69) * mm, "mid": v(55.39, -170.81) * mm, "end": v(56.27, -168.69) * mm});
            skArc(sketch, "E3803", {"start": v(56.27, -168.69) * mm, "mid": v(55.39, -166.57) * mm, "end": v(53.27, -165.69) * mm});
            skLineSegment(sketch, "E3804", {"start": v(-599.99, 1158.24) * mm, "end": v(-600, 608.96) * mm});
            skLineSegment(sketch, "E3805", {"start": v(-599.99, 565.96) * mm, "end": v(-600, 16.68) * mm});
            skLineSegment(sketch, "E3806", {"start": v(-600, -31.4) * mm, "end": v(-600, -580.67) * mm});
            skLineSegment(sketch, "E3807", {"start": v(-600, -600.67) * mm, "end": v(-600, -1149.94) * mm});
            skSolve(sketch);
        }
        {
            var Q0;
            Q0=makeQuery(id+"F0.imprint","IMPRINT",FACE,{"disambiguationData":[TD([[makeQuery(id+"F0.imprint","IMPRINT",EDGE,{"derivedFrom":sQuery(id+"F0.wireOp",EDGE,"E228")}),1.0]])]});
            var Q1;
            Q1=makeQuery(id+"F0.imprint","IMPRINT",FACE,{"disambiguationData":[TD([[makeQuery(id+"F0.imprint","IMPRINT",EDGE,{"derivedFrom":sQuery(id+"F0.wireOp",EDGE,"E531")}),-1.0]])]});
            var Q2;
            Q2=makeQuery(id+"F0.imprint","IMPRINT",FACE,{"disambiguationData":[TD([[makeQuery(id+"F0.imprint","IMPRINT",EDGE,{"derivedFrom":sQuery(id+"F0.wireOp",EDGE,"E787")}),-1.0]])]});
            var Q3;
            {var subQ0=sQuery(id+"F0.wireOp",EDGE,"E1044");Q3=makeQuery(id+"F0.imprint","IMPRINT",FACE,{"disambiguationData":[TD([[makeQuery(id+"F0.imprint","IMPRINT",EDGE,{"derivedFrom":subQ0}),-1.0]])]});}
            extrude(context, id + "F1", {"entities" : qUnion([Q0, Q1, Q2, Q3]), "depth" : 18 * mm});
        }
        {
            var Q0;
            Q0=makeQuery(id+"F0.imprint","IMPRINT",FACE,{"disambiguationData":[TD([[makeQuery(id+"F0.imprint","IMPRINT",EDGE,{"derivedFrom":sQuery(id+"F0.wireOp",EDGE,"E115")}),-1.0]])]});
            var Q1;
            Q1=makeQuery(id+"F0.imprint","IMPRINT",FACE,{"disambiguationData":[TD([[makeQuery(id+"F0.imprint","IMPRINT",EDGE,{"derivedFrom":sQuery(id+"F0.wireOp",EDGE,"E2073")}),-1.0]])]});
            var Q2;
            Q2=makeQuery(id+"F0.imprint","IMPRINT",FACE,{"disambiguationData":[TD([[makeQuery(id+"F0.imprint","IMPRINT",EDGE,{"derivedFrom":sQuery(id+"F0.wireOp",EDGE,"E2329")}),-1.0]])]});
            var Q3;
            {var subQ0=sQuery(id+"F0.wireOp",EDGE,"E2586");Q3=makeQuery(id+"F0.imprint","IMPRINT",FACE,{"disambiguationData":[TD([[makeQuery(id+"F0.imprint","IMPRINT",EDGE,{"derivedFrom":subQ0}),-1.0]])]});}
            var Q4;
            {var subQ1=sQuery(id+"F0.wireOp",EDGE,"E2701");Q4=makeQuery(id+"F0.imprint","IMPRINT",FACE,{"disambiguationData":[TD([[makeQuery(id+"F0.imprint","IMPRINT",EDGE,{"derivedFrom":subQ1}),1.0]])]});}
            extrude(context, id + "F2", {"entities" : qUnion([Q0, Q1, Q2, Q3, Q4]), "depth" : 25 * mm});
        }
    });
